FCSTD DOCUMENT  (FreeCAD 1.0R39285 (Git))
Label: TroubleBrewingCharacterIconsV2
License: All rights reserved
LicenseURL: https://en.wikipedia.org/wiki/All_rights_reserved
objects: Sketcher::SketchObject×22, Part::Extrusion×22, Part::Scale×22, Spreadsheet::Sheet×1
note: 88 computed .brp shape members not serialized (recipe doc carries the construction recipe); baked Part::Feature solids carry a one-line shape summary decoded from their .brp

FEATURE [Spreadsheet::Sheet] Spreadsheet  label="Icon_Params"
  cells = A1='IconDepth; B1='IconScale; A2(IconDepth)=3; B2(IconScale)=1.5
FEATURE [Sketcher::SketchObject] Sketch  label="Baron-Sketch"
  ArcFitTolerance = 1e-06
  FullyConstrained = false
  MakeInternals = false
  sketch-geometry (131):
    g0: BSplineCurve PolesCount=4 KnotsCount=2 Degree=3 IsPeriodic=0
    g1: BSplineCurve PolesCount=4 KnotsCount=2 Degree=3 IsPeriodic=0
    g2: BSplineCurve PolesCount=4 KnotsCount=2 Degree=3 IsPeriodic=0
    g3: BSplineCurve PolesCount=4 KnotsCount=2 Degree=3 IsPeriodic=0
    g4: BSplineCurve PolesCount=4 KnotsCount=2 Degree=3 IsPeriodic=0
    g5: BSplineCurve PolesCount=4 KnotsCount=2 Degree=3 IsPeriodic=0
    g6: BSplineCurve PolesCount=4 KnotsCount=2 Degree=3 IsPeriodic=0
    g7: BSplineCurve PolesCount=4 KnotsCount=2 Degree=3 IsPeriodic=0
    g8: BSplineCurve PolesCount=4 KnotsCount=2 Degree=3 IsPeriodic=0
    g9: BSplineCurve PolesCount=4 KnotsCount=2 Degree=3 IsPeriodic=0
    g10: BSplineCurve PolesCount=4 KnotsCount=2 Degree=3 IsPeriodic=0
    g11: BSplineCurve PolesCount=4 KnotsCount=2 Degree=3 IsPeriodic=0
    g12: BSplineCurve PolesCount=4 KnotsCount=2 Degree=3 IsPeriodic=0
    g13: BSplineCurve PolesCount=4 KnotsCount=2 Degree=3 IsPeriodic=0
    g14: BSplineCurve PolesCount=4 KnotsCount=2 Degree=3 IsPeriodic=0
    g15: BSplineCurve PolesCount=2 KnotsCount=2 Degree=1 IsPeriodic=0
    g16: BSplineCurve PolesCount=2 KnotsCount=2 Degree=1 IsPeriodic=0
    g17: BSplineCurve PolesCount=4 KnotsCount=2 Degree=3 IsPeriodic=0
    g18: BSplineCurve PolesCount=4 KnotsCount=2 Degree=3 IsPeriodic=0
    g19: BSplineCurve PolesCount=4 KnotsCount=2 Degree=3 IsPeriodic=0
    g20: BSplineCurve PolesCount=4 KnotsCount=2 Degree=3 IsPeriodic=0
    g21: BSplineCurve PolesCount=4 KnotsCount=2 Degree=3 IsPeriodic=0
    g22: BSplineCurve PolesCount=4 KnotsCount=2 Degree=3 IsPeriodic=0
    g23: BSplineCurve PolesCount=4 KnotsCount=2 Degree=3 IsPeriodic=0
    g24: BSplineCurve PolesCount=2 KnotsCount=2 Degree=1 IsPeriodic=0
    g25: BSplineCurve PolesCount=4 KnotsCount=2 Degree=3 IsPeriodic=0
    g26: BSplineCurve PolesCount=2 KnotsCount=2 Degree=1 IsPeriodic=0
    g27: BSplineCurve PolesCount=2 KnotsCount=2 Degree=1 IsPeriodic=0
    g28: BSplineCurve PolesCount=4 KnotsCount=2 Degree=3 IsPeriodic=0
    g29: BSplineCurve PolesCount=4 KnotsCount=2 Degree=3 IsPeriodic=0
    g30: BSplineCurve PolesCount=2 KnotsCount=2 Degree=1 IsPeriodic=0
    g31: BSplineCurve PolesCount=2 KnotsCount=2 Degree=1 IsPeriodic=0
    g32: BSplineCurve PolesCount=4 KnotsCount=2 Degree=3 IsPeriodic=0
    g33: BSplineCurve PolesCount=4 KnotsCount=2 Degree=3 IsPeriodic=0
    g34: BSplineCurve PolesCount=4 KnotsCount=2 Degree=3 IsPeriodic=0
    g35: BSplineCurve PolesCount=4 KnotsCount=2 Degree=3 IsPeriodic=0
    g36: BSplineCurve PolesCount=2 KnotsCount=2 Degree=1 IsPeriodic=0
    g37: BSplineCurve PolesCount=2 KnotsCount=2 Degree=1 IsPeriodic=0
    g38: BSplineCurve PolesCount=4 KnotsCount=2 Degree=3 IsPeriodic=0
    g39: BSplineCurve PolesCount=2 KnotsCount=2 Degree=1 IsPeriodic=0
    g40: BSplineCurve PolesCount=2 KnotsCount=2 Degree=1 IsPeriodic=0
    g41: BSplineCurve PolesCount=4 KnotsCount=2 Degree=3 IsPeriodic=0
    g42: BSplineCurve PolesCount=4 KnotsCount=2 Degree=3 IsPeriodic=0
    g43: BSplineCurve PolesCount=4 KnotsCount=2 Degree=3 IsPeriodic=0
    g44: BSplineCurve PolesCount=4 KnotsCount=2 Degree=3 IsPeriodic=0
    g45: BSplineCurve PolesCount=4 KnotsCount=2 Degree=3 IsPeriodic=0
    g46: BSplineCurve PolesCount=4 KnotsCount=2 Degree=3 IsPeriodic=0
    g47: BSplineCurve PolesCount=4 KnotsCount=2 Degree=3 IsPeriodic=0
    g48: BSplineCurve PolesCount=4 KnotsCount=2 Degree=3 IsPeriodic=0
    g49: BSplineCurve PolesCount=4 KnotsCount=2 Degree=3 IsPeriodic=0
    g50: BSplineCurve PolesCount=4 KnotsCount=2 Degree=3 IsPeriodic=0
    g51: BSplineCurve PolesCount=4 KnotsCount=2 Degree=3 IsPeriodic=0
    g52: BSplineCurve PolesCount=2 KnotsCount=2 Degree=1 IsPeriodic=0
    g53: BSplineCurve PolesCount=2 KnotsCount=2 Degree=1 IsPeriodic=0
    g54: BSplineCurve PolesCount=4 KnotsCount=2 Degree=3 IsPeriodic=0
    g55: BSplineCurve PolesCount=4 KnotsCount=2 Degree=3 IsPeriodic=0
    g56: BSplineCurve PolesCount=4 KnotsCount=2 Degree=3 IsPeriodic=0
    g57: BSplineCurve PolesCount=4 KnotsCount=2 Degree=3 IsPeriodic=0
    g58: BSplineCurve PolesCount=4 KnotsCount=2 Degree=3 IsPeriodic=0
    g59: BSplineCurve PolesCount=4 KnotsCount=2 Degree=3 IsPeriodic=0
    g60: BSplineCurve PolesCount=4 KnotsCount=2 Degree=3 IsPeriodic=0
    g61: BSplineCurve PolesCount=2 KnotsCount=2 Degree=1 IsPeriodic=0
    g62: BSplineCurve PolesCount=2 KnotsCount=2 Degree=1 IsPeriodic=0
    g63: BSplineCurve PolesCount=4 KnotsCount=2 Degree=3 IsPeriodic=0
    g64: BSplineCurve PolesCount=4 KnotsCount=2 Degree=3 IsPeriodic=0
    g65: BSplineCurve PolesCount=4 KnotsCount=2 Degree=3 IsPeriodic=0
    g66: BSplineCurve PolesCount=4 KnotsCount=2 Degree=3 IsPeriodic=0
    g67: BSplineCurve PolesCount=4 KnotsCount=2 Degree=3 IsPeriodic=0
    g68: BSplineCurve PolesCount=4 KnotsCount=2 Degree=3 IsPeriodic=0
    g69: BSplineCurve PolesCount=4 KnotsCount=2 Degree=3 IsPeriodic=0
    g70: BSplineCurve PolesCount=4 KnotsCount=2 Degree=3 IsPeriodic=0
    g71: BSplineCurve PolesCount=4 KnotsCount=2 Degree=3 IsPeriodic=0
    g72: BSplineCurve PolesCount=4 KnotsCount=2 Degree=3 IsPeriodic=0
    g73: BSplineCurve PolesCount=4 KnotsCount=2 Degree=3 IsPeriodic=0
    g74: BSplineCurve PolesCount=4 KnotsCount=2 Degree=3 IsPeriodic=0
    g75: BSplineCurve PolesCount=4 KnotsCount=2 Degree=3 IsPeriodic=0
    g76: BSplineCurve PolesCount=4 KnotsCount=2 Degree=3 IsPeriodic=0
    g77: BSplineCurve PolesCount=4 KnotsCount=2 Degree=3 IsPeriodic=0
    g78: BSplineCurve PolesCount=4 KnotsCount=2 Degree=3 IsPeriodic=0
    g79: BSplineCurve PolesCount=4 KnotsCount=2 Degree=3 IsPeriodic=0
    g80: BSplineCurve PolesCount=4 KnotsCount=2 Degree=3 IsPeriodic=0
    g81: BSplineCurve PolesCount=4 KnotsCount=2 Degree=3 IsPeriodic=0
    g82: BSplineCurve PolesCount=4 KnotsCount=2 Degree=3 IsPeriodic=0
    g83: BSplineCurve PolesCount=4 KnotsCount=2 Degree=3 IsPeriodic=0
    g84: BSplineCurve PolesCount=4 KnotsCount=2 Degree=3 IsPeriodic=0
    g85: BSplineCurve PolesCount=4 KnotsCount=2 Degree=3 IsPeriodic=0
    g86: BSplineCurve PolesCount=4 KnotsCount=2 Degree=3 IsPeriodic=0
    g87: BSplineCurve PolesCount=4 KnotsCount=2 Degree=3 IsPeriodic=0
    g88: BSplineCurve PolesCount=4 KnotsCount=2 Degree=3 IsPeriodic=0
    g89: BSplineCurve PolesCount=4 KnotsCount=2 Degree=3 IsPeriodic=0
    g90: BSplineCurve PolesCount=4 KnotsCount=2 Degree=3 IsPeriodic=0
    g91: BSplineCurve PolesCount=4 KnotsCount=2 Degree=3 IsPeriodic=0
    g92: BSplineCurve PolesCount=4 KnotsCount=2 Degree=3 IsPeriodic=0
    g93: BSplineCurve PolesCount=4 KnotsCount=2 Degree=3 IsPeriodic=0
    g94: BSplineCurve PolesCount=4 KnotsCount=2 Degree=3 IsPeriodic=0
    g95: BSplineCurve PolesCount=4 KnotsCount=2 Degree=3 IsPeriodic=0
    g96: BSplineCurve PolesCount=2 KnotsCount=2 Degree=1 IsPeriodic=0
    g97: BSplineCurve PolesCount=2 KnotsCount=2 Degree=1 IsPeriodic=0
    g98: BSplineCurve PolesCount=2 KnotsCount=2 Degree=1 IsPeriodic=0
    g99: BSplineCurve PolesCount=2 KnotsCount=2 Degree=1 IsPeriodic=0
    g100: BSplineCurve PolesCount=4 KnotsCount=2 Degree=3 IsPeriodic=0
    g101: BSplineCurve PolesCount=4 KnotsCount=2 Degree=3 IsPeriodic=0
    g102: BSplineCurve PolesCount=4 KnotsCount=2 Degree=3 IsPeriodic=0
    g103: BSplineCurve PolesCount=4 KnotsCount=2 Degree=3 IsPeriodic=0
    g104: BSplineCurve PolesCount=4 KnotsCount=2 Degree=3 IsPeriodic=0
    g105: BSplineCurve PolesCount=4 KnotsCount=2 Degree=3 IsPeriodic=0
    g106: BSplineCurve PolesCount=4 KnotsCount=2 Degree=3 IsPeriodic=0
    g107: BSplineCurve PolesCount=4 KnotsCount=2 Degree=3 IsPeriodic=0
    g108: BSplineCurve PolesCount=4 KnotsCount=2 Degree=3 IsPeriodic=0
    g109: BSplineCurve PolesCount=4 KnotsCount=2 Degree=3 IsPeriodic=0
    g110: BSplineCurve PolesCount=4 KnotsCount=2 Degree=3 IsPeriodic=0
    g111: BSplineCurve PolesCount=4 KnotsCount=2 Degree=3 IsPeriodic=0
    g112: BSplineCurve PolesCount=4 KnotsCount=2 Degree=3 IsPeriodic=0
    g113: BSplineCurve PolesCount=4 KnotsCount=2 Degree=3 IsPeriodic=0
    g114: BSplineCurve PolesCount=4 KnotsCount=2 Degree=3 IsPeriodic=0
    g115: BSplineCurve PolesCount=4 KnotsCount=2 Degree=3 IsPeriodic=0
    g116: BSplineCurve PolesCount=4 KnotsCount=2 Degree=3 IsPeriodic=0
    g117: BSplineCurve PolesCount=2 KnotsCount=2 Degree=1 IsPeriodic=0
    g118: BSplineCurve PolesCount=2 KnotsCount=2 Degree=1 IsPeriodic=0
    g119: BSplineCurve PolesCount=4 KnotsCount=2 Degree=3 IsPeriodic=0
    g120: BSplineCurve PolesCount=4 KnotsCount=2 Degree=3 IsPeriodic=0
    g121: BSplineCurve PolesCount=4 KnotsCount=2 Degree=3 IsPeriodic=0
    g122: BSplineCurve PolesCount=4 KnotsCount=2 Degree=3 IsPeriodic=0
    g123: BSplineCurve PolesCount=4 KnotsCount=2 Degree=3 IsPeriodic=0
    g124: BSplineCurve PolesCount=4 KnotsCount=2 Degree=3 IsPeriodic=0
    g125: BSplineCurve PolesCount=4 KnotsCount=2 Degree=3 IsPeriodic=0
    g126: BSplineCurve PolesCount=4 KnotsCount=2 Degree=3 IsPeriodic=0
    g127: BSplineCurve PolesCount=4 KnotsCount=2 Degree=3 IsPeriodic=0
    g128: BSplineCurve PolesCount=4 KnotsCount=2 Degree=3 IsPeriodic=0
    g129: BSplineCurve PolesCount=4 KnotsCount=2 Degree=3 IsPeriodic=0
    g130: BSplineCurve PolesCount=4 KnotsCount=2 Degree=3 IsPeriodic=0
  constraints (132):
    c: Coincident(g0,g1)
    c: Coincident(g1,g2)
    c: Coincident(g2,g3)
    c: Coincident(g3,g4)
    c: Coincident(g4,g5)
    c: Coincident(g5,g6)
    c: Coincident(g6,g7)
    c: Coincident(g7,g8)
    c: Coincident(g8,g9)
    c: Coincident(g9,g10)
    c: Coincident(g10,g11)
    c: Coincident(g11,g12)
    c: Coincident(g12,g13)
    c: Coincident(g13,g14)
    c: Coincident(g14,g15)
    c: Coincident(g15,g16)
    c: Coincident(g16,g17)
    c: Coincident(g17,g18)
    c: Coincident(g18,g19)
    c: Coincident(g19,g20)
    c: Coincident(g20,g21)
    c: Coincident(g21,g22)
    c: Coincident(g22,g23)
    c: Coincident(g23,g0)
    c: Coincident(g24,g25)
    c: Coincident(g25,g26)
    c: Coincident(g26,g27)
    c: Coincident(g27,g28)
    c: Coincident(g28,g29)
    c: Coincident(g29,g30)
    c: Coincident(g30,g31)
    c: Coincident(g31,g32)
    c: Coincident(g32,g33)
    c: Coincident(g33,g34)
    c: Coincident(g34,g35)
    c: Coincident(g35,g36)
    c: Coincident(g36,g37)
    c: Coincident(g37,g38)
    c: Coincident(g38,g39)
    c: Coincident(g39,g40)
    c: Coincident(g40,g41)
    c: Coincident(g41,g42)
    c: Coincident(g42,g43)
    c: Coincident(g43,g24)
    c: Coincident(g44,g45)
    c: Coincident(g45,g46)
    c: Coincident(g46,g47)
    c: Coincident(g47,g48)
    c: Coincident(g48,g49)
    c: Coincident(g49,g50)
    c: Coincident(g50,g51)
    c: Coincident(g51,g52)
    c: Coincident(g52,g53)
    c: Coincident(g53,g54)
    c: Coincident(g54,g55)
    c: Coincident(g55,g56)
    c: Coincident(g56,g57)
    c: Coincident(g57,g58)
    c: Coincident(g58,g59)
    c: Coincident(g59,g60)
    c: Coincident(g60,g61)
    c: Coincident(g61,g62)
    c: Coincident(g62,g63)
    c: Coincident(g63,g44)
    c: Coincident(g64,g65)
    c: Coincident(g65,g66)
    c: Coincident(g66,g67)
    c: Coincident(g67,g68)
    c: Coincident(g68,g69)
    c: Coincident(g69,g70)
    c: Coincident(g70,g71)
    c: Coincident(g71,g72)
    c: Coincident(g72,g73)
    c: Coincident(g73,g74)
    c: Coincident(g74,g75)
    c: Coincident(g75,g76)
    c: Coincident(g76,g77)
    c: Coincident(g77,g78)
    c: Coincident(g78,g79)
    c: Coincident(g79,g80)
    c: Coincident(g80,g81)
    c: Coincident(g81,g82)
    c: Coincident(g82,g83)
    c: Coincident(g83,g84)
    c: Coincident(g84,g64)
    c: Coincident(g85,g86)
    c: Coincident(g86,g87)
    c: Coincident(g87,g88)
    c: Coincident(g88,g89)
    c: Coincident(g89,g90)
    c: Coincident(g90,g91)
    c: Coincident(g91,g92)
    c: Coincident(g92,g93)
    c: Coincident(g93,g94)
    c: Coincident(g94,g95)
    c: Coincident(g95,g96)
    c: Coincident(g96,g97)
    c: Coincident(g97,g98)
    c: Coincident(g98,g99)
    c: Coincident(g99,g100)
    c: Coincident(g100,g101)
    c: Coincident(g101,g102)
    c: Coincident(g102,g103)
    c: Coincident(g103,g104)
    c: Coincident(g104,g105)
    c: Coincident(g105,g106)
    c: Coincident(g106,g107)
    c: Coincident(g107,g108)
    c: Coincident(g108,g109)
    c: Coincident(g109,g110)
    c: Coincident(g110,g111)
    c: Coincident(g111,g112)
    c: Coincident(g112,g113)
    c: Coincident(g113,g114)
    c: Coincident(g114,g115)
    c: Coincident(g115,g116)
    c: Coincident(g116,g117)
    c: Coincident(g117,g118)
    c: Coincident(g118,g85)
    c: Coincident(g119,g120)
    c: Coincident(g120,g121)
    c: Coincident(g121,g122)
    c: Coincident(g122,g123)
    c: Coincident(g123,g124)
    c: Coincident(g124,g125)
    c: Coincident(g125,g126)
    c: Coincident(g126,g127)
    c: Coincident(g127,g128)
    c: Coincident(g128,g129)
    c: Coincident(g129,g130)
    c: Coincident(g130,g119)
    c: Coincident(g24,g24)
FEATURE [Part::Extrusion] Extrude  label="Baron-Extrude"
  Base = -> Sketch
  Dir = (0,0,1)
  DirMode = 0
  FaceMakerClass = Part::FaceMakerBullseye
  FaceMakerMode = 3
  LengthFwd = 0
  LengthRev = 3
  Solid = true
  Symmetric = false
  expr: LengthRev = <<Icon_Params>>.IconDepth
FEATURE [Part::Scale] Scale  label="Baron"
  Base = -> Extrude
  Uniform = true
  UniformScale = 1.5
  XScale = 1
  YScale = 1
  ZScale = 1
  expr: UniformScale = <<Icon_Params>>.IconScale
FEATURE [Sketcher::SketchObject] Sketch001  label="Butler-Sketch"
  ArcFitTolerance = 1e-06
  FullyConstrained = false
  MakeInternals = false
  sketch-geometry (215):
    g0: BSplineCurve PolesCount=4 KnotsCount=2 Degree=3 IsPeriodic=0
    g1: BSplineCurve PolesCount=4 KnotsCount=2 Degree=3 IsPeriodic=0
    g2: BSplineCurve PolesCount=2 KnotsCount=2 Degree=1 IsPeriodic=0
    g3: BSplineCurve PolesCount=2 KnotsCount=2 Degree=1 IsPeriodic=0
    g4: BSplineCurve PolesCount=4 KnotsCount=2 Degree=3 IsPeriodic=0
    g5: BSplineCurve PolesCount=4 KnotsCount=2 Degree=3 IsPeriodic=0
    g6: BSplineCurve PolesCount=4 KnotsCount=2 Degree=3 IsPeriodic=0
    g7: BSplineCurve PolesCount=4 KnotsCount=2 Degree=3 IsPeriodic=0
    g8: BSplineCurve PolesCount=4 KnotsCount=2 Degree=3 IsPeriodic=0
    g9: BSplineCurve PolesCount=4 KnotsCount=2 Degree=3 IsPeriodic=0
    g10: BSplineCurve PolesCount=2 KnotsCount=2 Degree=1 IsPeriodic=0
    g11: BSplineCurve PolesCount=2 KnotsCount=2 Degree=1 IsPeriodic=0
    g12: BSplineCurve PolesCount=4 KnotsCount=2 Degree=3 IsPeriodic=0
    g13: BSplineCurve PolesCount=4 KnotsCount=2 Degree=3 IsPeriodic=0
    g14: BSplineCurve PolesCount=4 KnotsCount=2 Degree=3 IsPeriodic=0
    g15: BSplineCurve PolesCount=2 KnotsCount=2 Degree=1 IsPeriodic=0
    g16: BSplineCurve PolesCount=2 KnotsCount=2 Degree=1 IsPeriodic=0
    g17: BSplineCurve PolesCount=4 KnotsCount=2 Degree=3 IsPeriodic=0
    g18: BSplineCurve PolesCount=2 KnotsCount=2 Degree=1 IsPeriodic=0
    g19: BSplineCurve PolesCount=2 KnotsCount=2 Degree=1 IsPeriodic=0
    g20: BSplineCurve PolesCount=4 KnotsCount=2 Degree=3 IsPeriodic=0
    g21: BSplineCurve PolesCount=4 KnotsCount=2 Degree=3 IsPeriodic=0
    g22: BSplineCurve PolesCount=4 KnotsCount=2 Degree=3 IsPeriodic=0
    g23: BSplineCurve PolesCount=4 KnotsCount=2 Degree=3 IsPeriodic=0
    g24: BSplineCurve PolesCount=4 KnotsCount=2 Degree=3 IsPeriodic=0
    g25: BSplineCurve PolesCount=4 KnotsCount=2 Degree=3 IsPeriodic=0
    g26: BSplineCurve PolesCount=4 KnotsCount=2 Degree=3 IsPeriodic=0
    g27: BSplineCurve PolesCount=4 KnotsCount=2 Degree=3 IsPeriodic=0
    g28: BSplineCurve PolesCount=2 KnotsCount=2 Degree=1 IsPeriodic=0
    g29: BSplineCurve PolesCount=2 KnotsCount=2 Degree=1 IsPeriodic=0
    g30: BSplineCurve PolesCount=4 KnotsCount=2 Degree=3 IsPeriodic=0
    g31: BSplineCurve PolesCount=4 KnotsCount=2 Degree=3 IsPeriodic=0
    g32: BSplineCurve PolesCount=2 KnotsCount=2 Degree=1 IsPeriodic=0
    g33: BSplineCurve PolesCount=2 KnotsCount=2 Degree=1 IsPeriodic=0
    g34: BSplineCurve PolesCount=4 KnotsCount=2 Degree=3 IsPeriodic=0
    g35: BSplineCurve PolesCount=4 KnotsCount=2 Degree=3 IsPeriodic=0
    g36: BSplineCurve PolesCount=4 KnotsCount=2 Degree=3 IsPeriodic=0
    g37: BSplineCurve PolesCount=4 KnotsCount=2 Degree=3 IsPeriodic=0
    g38: BSplineCurve PolesCount=4 KnotsCount=2 Degree=3 IsPeriodic=0
    g39: BSplineCurve PolesCount=4 KnotsCount=2 Degree=3 IsPeriodic=0
    g40: BSplineCurve PolesCount=4 KnotsCount=2 Degree=3 IsPeriodic=0
    g41: BSplineCurve PolesCount=4 KnotsCount=2 Degree=3 IsPeriodic=0
    g42: BSplineCurve PolesCount=4 KnotsCount=2 Degree=3 IsPeriodic=0
    g43: BSplineCurve PolesCount=4 KnotsCount=2 Degree=3 IsPeriodic=0
    g44: BSplineCurve PolesCount=2 KnotsCount=2 Degree=1 IsPeriodic=0
    g45: BSplineCurve PolesCount=2 KnotsCount=2 Degree=1 IsPeriodic=0
    g46: BSplineCurve PolesCount=4 KnotsCount=2 Degree=3 IsPeriodic=0
    g47: BSplineCurve PolesCount=4 KnotsCount=2 Degree=3 IsPeriodic=0
    g48: BSplineCurve PolesCount=2 KnotsCount=2 Degree=1 IsPeriodic=0
    g49: BSplineCurve PolesCount=2 KnotsCount=2 Degree=1 IsPeriodic=0
    g50: BSplineCurve PolesCount=2 KnotsCount=2 Degree=1 IsPeriodic=0
    g51: BSplineCurve PolesCount=2 KnotsCount=2 Degree=1 IsPeriodic=0
    g52: BSplineCurve PolesCount=4 KnotsCount=2 Degree=3 IsPeriodic=0
    g53: BSplineCurve PolesCount=4 KnotsCount=2 Degree=3 IsPeriodic=0
    g54: BSplineCurve PolesCount=4 KnotsCount=2 Degree=3 IsPeriodic=0
    g55: BSplineCurve PolesCount=4 KnotsCount=2 Degree=3 IsPeriodic=0
    g56: BSplineCurve PolesCount=4 KnotsCount=2 Degree=3 IsPeriodic=0
    g57: BSplineCurve PolesCount=4 KnotsCount=2 Degree=3 IsPeriodic=0
    g58: BSplineCurve PolesCount=4 KnotsCount=2 Degree=3 IsPeriodic=0
    g59: BSplineCurve PolesCount=4 KnotsCount=2 Degree=3 IsPeriodic=0
    g60: BSplineCurve PolesCount=4 KnotsCount=2 Degree=3 IsPeriodic=0
    g61: BSplineCurve PolesCount=4 KnotsCount=2 Degree=3 IsPeriodic=0
    g62: BSplineCurve PolesCount=4 KnotsCount=2 Degree=3 IsPeriodic=0
    g63: BSplineCurve PolesCount=4 KnotsCount=2 Degree=3 IsPeriodic=0
    g64: BSplineCurve PolesCount=4 KnotsCount=2 Degree=3 IsPeriodic=0
    g65: BSplineCurve PolesCount=4 KnotsCount=2 Degree=3 IsPeriodic=0
    g66: BSplineCurve PolesCount=4 KnotsCount=2 Degree=3 IsPeriodic=0
    g67: BSplineCurve PolesCount=4 KnotsCount=2 Degree=3 IsPeriodic=0
    g68: BSplineCurve PolesCount=4 KnotsCount=2 Degree=3 IsPeriodic=0
    g69: BSplineCurve PolesCount=4 KnotsCount=2 Degree=3 IsPeriodic=0
    g70: BSplineCurve PolesCount=4 KnotsCount=2 Degree=3 IsPeriodic=0
    g71: BSplineCurve PolesCount=4 KnotsCount=2 Degree=3 IsPeriodic=0
    g72: BSplineCurve PolesCount=4 KnotsCount=2 Degree=3 IsPeriodic=0
    g73: BSplineCurve PolesCount=4 KnotsCount=2 Degree=3 IsPeriodic=0
    g74: BSplineCurve PolesCount=4 KnotsCount=2 Degree=3 IsPeriodic=0
    g75: BSplineCurve PolesCount=4 KnotsCount=2 Degree=3 IsPeriodic=0
    g76: BSplineCurve PolesCount=4 KnotsCount=2 Degree=3 IsPeriodic=0
    g77: BSplineCurve PolesCount=4 KnotsCount=2 Degree=3 IsPeriodic=0
    g78: BSplineCurve PolesCount=4 KnotsCount=2 Degree=3 IsPeriodic=0
    g79: BSplineCurve PolesCount=4 KnotsCount=2 Degree=3 IsPeriodic=0
    g80: BSplineCurve PolesCount=4 KnotsCount=2 Degree=3 IsPeriodic=0
    g81: BSplineCurve PolesCount=4 KnotsCount=2 Degree=3 IsPeriodic=0
    g82: BSplineCurve PolesCount=4 KnotsCount=2 Degree=3 IsPeriodic=0
    g83: BSplineCurve PolesCount=4 KnotsCount=2 Degree=3 IsPeriodic=0
    g84: BSplineCurve PolesCount=4 KnotsCount=2 Degree=3 IsPeriodic=0
    g85: BSplineCurve PolesCount=4 KnotsCount=2 Degree=3 IsPeriodic=0
    g86: BSplineCurve PolesCount=4 KnotsCount=2 Degree=3 IsPeriodic=0
    g87: BSplineCurve PolesCount=4 KnotsCount=2 Degree=3 IsPeriodic=0
    g88: BSplineCurve PolesCount=4 KnotsCount=2 Degree=3 IsPeriodic=0
    g89: BSplineCurve PolesCount=4 KnotsCount=2 Degree=3 IsPeriodic=0
    g90: BSplineCurve PolesCount=4 KnotsCount=2 Degree=3 IsPeriodic=0
    g91: BSplineCurve PolesCount=4 KnotsCount=2 Degree=3 IsPeriodic=0
    g92: BSplineCurve PolesCount=4 KnotsCount=2 Degree=3 IsPeriodic=0
    g93: BSplineCurve PolesCount=4 KnotsCount=2 Degree=3 IsPeriodic=0
    g94: BSplineCurve PolesCount=4 KnotsCount=2 Degree=3 IsPeriodic=0
    g95: BSplineCurve PolesCount=4 KnotsCount=2 Degree=3 IsPeriodic=0
    g96: BSplineCurve PolesCount=4 KnotsCount=2 Degree=3 IsPeriodic=0
    g97: BSplineCurve PolesCount=2 KnotsCount=2 Degree=1 IsPeriodic=0
    g98: BSplineCurve PolesCount=2 KnotsCount=2 Degree=1 IsPeriodic=0
    g99: BSplineCurve PolesCount=2 KnotsCount=2 Degree=1 IsPeriodic=0
    g100: BSplineCurve PolesCount=2 KnotsCount=2 Degree=1 IsPeriodic=0
    g101: BSplineCurve PolesCount=4 KnotsCount=2 Degree=3 IsPeriodic=0
    g102: BSplineCurve PolesCount=4 KnotsCount=2 Degree=3 IsPeriodic=0
    g103: BSplineCurve PolesCount=4 KnotsCount=2 Degree=3 IsPeriodic=0
    g104: BSplineCurve PolesCount=4 KnotsCount=2 Degree=3 IsPeriodic=0
    g105: BSplineCurve PolesCount=4 KnotsCount=2 Degree=3 IsPeriodic=0
    g106: BSplineCurve PolesCount=4 KnotsCount=2 Degree=3 IsPeriodic=0
    g107: BSplineCurve PolesCount=4 KnotsCount=2 Degree=3 IsPeriodic=0
    g108: BSplineCurve PolesCount=4 KnotsCount=2 Degree=3 IsPeriodic=0
    g109: BSplineCurve PolesCount=4 KnotsCount=2 Degree=3 IsPeriodic=0
    g110: BSplineCurve PolesCount=4 KnotsCount=2 Degree=3 IsPeriodic=0
    g111: BSplineCurve PolesCount=4 KnotsCount=2 Degree=3 IsPeriodic=0
    g112: BSplineCurve PolesCount=4 KnotsCount=2 Degree=3 IsPeriodic=0
    g113: BSplineCurve PolesCount=4 KnotsCount=2 Degree=3 IsPeriodic=0
    g114: BSplineCurve PolesCount=2 KnotsCount=2 Degree=1 IsPeriodic=0
    g115: BSplineCurve PolesCount=2 KnotsCount=2 Degree=1 IsPeriodic=0
    g116: BSplineCurve PolesCount=4 KnotsCount=2 Degree=3 IsPeriodic=0
    g117: BSplineCurve PolesCount=4 KnotsCount=2 Degree=3 IsPeriodic=0
    g118: BSplineCurve PolesCount=4 KnotsCount=2 Degree=3 IsPeriodic=0
    g119: BSplineCurve PolesCount=4 KnotsCount=2 Degree=3 IsPeriodic=0
    g120: BSplineCurve PolesCount=2 KnotsCount=2 Degree=1 IsPeriodic=0
    g121: BSplineCurve PolesCount=2 KnotsCount=2 Degree=1 IsPeriodic=0
    g122: BSplineCurve PolesCount=4 KnotsCount=2 Degree=3 IsPeriodic=0
    g123: BSplineCurve PolesCount=4 KnotsCount=2 Degree=3 IsPeriodic=0
    g124: BSplineCurve PolesCount=4 KnotsCount=2 Degree=3 IsPeriodic=0
    g125: BSplineCurve PolesCount=4 KnotsCount=2 Degree=3 IsPeriodic=0
    g126: BSplineCurve PolesCount=4 KnotsCount=2 Degree=3 IsPeriodic=0
    g127: BSplineCurve PolesCount=4 KnotsCount=2 Degree=3 IsPeriodic=0
    g128: BSplineCurve PolesCount=4 KnotsCount=2 Degree=3 IsPeriodic=0
    g129: BSplineCurve PolesCount=4 KnotsCount=2 Degree=3 IsPeriodic=0
    g130: BSplineCurve PolesCount=4 KnotsCount=2 Degree=3 IsPeriodic=0
    g131: BSplineCurve PolesCount=4 KnotsCount=2 Degree=3 IsPeriodic=0
    g132: BSplineCurve PolesCount=4 KnotsCount=2 Degree=3 IsPeriodic=0
    g133: BSplineCurve PolesCount=4 KnotsCount=2 Degree=3 IsPeriodic=0
    g134: BSplineCurve PolesCount=4 KnotsCount=2 Degree=3 IsPeriodic=0
    g135: BSplineCurve PolesCount=4 KnotsCount=2 Degree=3 IsPeriodic=0
    g136: BSplineCurve PolesCount=4 KnotsCount=2 Degree=3 IsPeriodic=0
    g137: BSplineCurve PolesCount=4 KnotsCount=2 Degree=3 IsPeriodic=0
    g138: BSplineCurve PolesCount=4 KnotsCount=2 Degree=3 IsPeriodic=0
    g139: BSplineCurve PolesCount=4 KnotsCount=2 Degree=3 IsPeriodic=0
    g140: BSplineCurve PolesCount=4 KnotsCount=2 Degree=3 IsPeriodic=0
    g141: BSplineCurve PolesCount=4 KnotsCount=2 Degree=3 IsPeriodic=0
    g142: BSplineCurve PolesCount=4 KnotsCount=2 Degree=3 IsPeriodic=0
    g143: BSplineCurve PolesCount=4 KnotsCount=2 Degree=3 IsPeriodic=0
    g144: BSplineCurve PolesCount=4 KnotsCount=2 Degree=3 IsPeriodic=0
    g145: BSplineCurve PolesCount=4 KnotsCount=2 Degree=3 IsPeriodic=0
    g146: BSplineCurve PolesCount=4 KnotsCount=2 Degree=3 IsPeriodic=0
    g147: BSplineCurve PolesCount=4 KnotsCount=2 Degree=3 IsPeriodic=0
    g148: BSplineCurve PolesCount=4 KnotsCount=2 Degree=3 IsPeriodic=0
    g149: BSplineCurve PolesCount=2 KnotsCount=2 Degree=1 IsPeriodic=0
    g150: BSplineCurve PolesCount=2 KnotsCount=2 Degree=1 IsPeriodic=0
    g151: BSplineCurve PolesCount=4 KnotsCount=2 Degree=3 IsPeriodic=0
    g152: BSplineCurve PolesCount=4 KnotsCount=2 Degree=3 IsPeriodic=0
    g153: BSplineCurve PolesCount=4 KnotsCount=2 Degree=3 IsPeriodic=0
    g154: BSplineCurve PolesCount=4 KnotsCount=2 Degree=3 IsPeriodic=0
    g155: BSplineCurve PolesCount=4 KnotsCount=2 Degree=3 IsPeriodic=0
    g156: BSplineCurve PolesCount=4 KnotsCount=2 Degree=3 IsPeriodic=0
    g157: BSplineCurve PolesCount=4 KnotsCount=2 Degree=3 IsPeriodic=0
    g158: BSplineCurve PolesCount=4 KnotsCount=2 Degree=3 IsPeriodic=0
    g159: BSplineCurve PolesCount=4 KnotsCount=2 Degree=3 IsPeriodic=0
    g160: BSplineCurve PolesCount=4 KnotsCount=2 Degree=3 IsPeriodic=0
    g161: BSplineCurve PolesCount=4 KnotsCount=2 Degree=3 IsPeriodic=0
    g162: BSplineCurve PolesCount=2 KnotsCount=2 Degree=1 IsPeriodic=0
    g163: BSplineCurve PolesCount=2 KnotsCount=2 Degree=1 IsPeriodic=0
    g164: BSplineCurve PolesCount=2 KnotsCount=2 Degree=1 IsPeriodic=0
    g165: BSplineCurve PolesCount=2 KnotsCount=2 Degree=1 IsPeriodic=0
    g166: BSplineCurve PolesCount=4 KnotsCount=2 Degree=3 IsPeriodic=0
    g167: BSplineCurve PolesCount=4 KnotsCount=2 Degree=3 IsPeriodic=0
    g168: BSplineCurve PolesCount=4 KnotsCount=2 Degree=3 IsPeriodic=0
    g169: BSplineCurve PolesCount=4 KnotsCount=2 Degree=3 IsPeriodic=0
    g170: BSplineCurve PolesCount=4 KnotsCount=2 Degree=3 IsPeriodic=0
    g171: BSplineCurve PolesCount=4 KnotsCount=2 Degree=3 IsPeriodic=0
    g172: BSplineCurve PolesCount=4 KnotsCount=2 Degree=3 IsPeriodic=0
    g173: BSplineCurve PolesCount=4 KnotsCount=2 Degree=3 IsPeriodic=0
    g174: BSplineCurve PolesCount=4 KnotsCount=2 Degree=3 IsPeriodic=0
    g175: BSplineCurve PolesCount=4 KnotsCount=2 Degree=3 IsPeriodic=0
    g176: BSplineCurve PolesCount=4 KnotsCount=2 Degree=3 IsPeriodic=0
    g177: BSplineCurve PolesCount=4 KnotsCount=2 Degree=3 IsPeriodic=0
    g178: BSplineCurve PolesCount=4 KnotsCount=2 Degree=3 IsPeriodic=0
    g179: BSplineCurve PolesCount=4 KnotsCount=2 Degree=3 IsPeriodic=0
    g180: BSplineCurve PolesCount=4 KnotsCount=2 Degree=3 IsPeriodic=0
    g181: BSplineCurve PolesCount=4 KnotsCount=2 Degree=3 IsPeriodic=0
    g182: BSplineCurve PolesCount=4 KnotsCount=2 Degree=3 IsPeriodic=0
    g183: BSplineCurve PolesCount=4 KnotsCount=2 Degree=3 IsPeriodic=0
    g184: BSplineCurve PolesCount=4 KnotsCount=2 Degree=3 IsPeriodic=0
    g185: BSplineCurve PolesCount=4 KnotsCount=2 Degree=3 IsPeriodic=0
    g186: BSplineCurve PolesCount=2 KnotsCount=2 Degree=1 IsPeriodic=0
    g187: BSplineCurve PolesCount=2 KnotsCount=2 Degree=1 IsPeriodic=0
    g188: BSplineCurve PolesCount=4 KnotsCount=2 Degree=3 IsPeriodic=0
    g189: BSplineCurve PolesCount=4 KnotsCount=2 Degree=3 IsPeriodic=0
    g190: BSplineCurve PolesCount=4 KnotsCount=2 Degree=3 IsPeriodic=0
    g191: BSplineCurve PolesCount=4 KnotsCount=2 Degree=3 IsPeriodic=0
    g192: BSplineCurve PolesCount=4 KnotsCount=2 Degree=3 IsPeriodic=0
    g193: BSplineCurve PolesCount=4 KnotsCount=2 Degree=3 IsPeriodic=0
    g194: BSplineCurve PolesCount=4 KnotsCount=2 Degree=3 IsPeriodic=0
    g195: BSplineCurve PolesCount=4 KnotsCount=2 Degree=3 IsPeriodic=0
    g196: BSplineCurve PolesCount=4 KnotsCount=2 Degree=3 IsPeriodic=0
    g197: BSplineCurve PolesCount=4 KnotsCount=2 Degree=3 IsPeriodic=0
    g198: BSplineCurve PolesCount=4 KnotsCount=2 Degree=3 IsPeriodic=0
    g199: BSplineCurve PolesCount=2 KnotsCount=2 Degree=1 IsPeriodic=0
    g200: BSplineCurve PolesCount=4 KnotsCount=2 Degree=3 IsPeriodic=0
    g201: BSplineCurve PolesCount=4 KnotsCount=2 Degree=3 IsPeriodic=0
    g202: BSplineCurve PolesCount=4 KnotsCount=2 Degree=3 IsPeriodic=0
    g203: BSplineCurve PolesCount=2 KnotsCount=2 Degree=1 IsPeriodic=0
    g204: BSplineCurve PolesCount=4 KnotsCount=2 Degree=3 IsPeriodic=0
    g205: BSplineCurve PolesCount=4 KnotsCount=2 Degree=3 IsPeriodic=0
    g206: BSplineCurve PolesCount=4 KnotsCount=2 Degree=3 IsPeriodic=0
    g207: BSplineCurve PolesCount=4 KnotsCount=2 Degree=3 IsPeriodic=0
    g208: BSplineCurve PolesCount=4 KnotsCount=2 Degree=3 IsPeriodic=0
    g209: BSplineCurve PolesCount=4 KnotsCount=2 Degree=3 IsPeriodic=0
    g210: BSplineCurve PolesCount=4 KnotsCount=2 Degree=3 IsPeriodic=0
    g211: BSplineCurve PolesCount=4 KnotsCount=2 Degree=3 IsPeriodic=0
    g212: BSplineCurve PolesCount=4 KnotsCount=2 Degree=3 IsPeriodic=0
    g213: BSplineCurve PolesCount=4 KnotsCount=2 Degree=3 IsPeriodic=0
    g214: BSplineCurve PolesCount=4 KnotsCount=2 Degree=3 IsPeriodic=0
  constraints (215):
    c: Coincident(g0,g1)
    c: Coincident(g1,g2)
    c: Coincident(g2,g3)
    c: Coincident(g3,g4)
    c: Coincident(g4,g5)
    c: Coincident(g5,g0)
    c: Coincident(g6,g7)
    c: Coincident(g7,g8)
    c: Coincident(g8,g9)
    c: Coincident(g10,g11)
    c: Coincident(g11,g12)
    c: Coincident(g12,g13)
    c: Coincident(g13,g14)
    c: Coincident(g14,g15)
    c: Coincident(g15,g16)
    c: Coincident(g16,g17)
    c: Coincident(g17,g18)
    c: Coincident(g18,g19)
    c: Coincident(g19,g20)
    c: Coincident(g20,g21)
    c: Coincident(g21,g22)
    c: Coincident(g22,g23)
    c: Coincident(g23,g24)
    c: Coincident(g24,g25)
    c: Coincident(g26,g27)
    c: Coincident(g27,g28)
    c: Coincident(g28,g29)
    c: Coincident(g29,g30)
    c: Coincident(g30,g31)
    c: Coincident(g31,g32)
    c: Coincident(g32,g33)
    c: Coincident(g33,g34)
    c: Coincident(g34,g35)
    c: Coincident(g35,g36)
    c: Coincident(g36,g26)
    c: Coincident(g37,g38)
    c: Coincident(g38,g39)
    c: Coincident(g39,g40)
    c: Coincident(g40,g41)
    c: Coincident(g41,g37)
    c: Coincident(g42,g43)
    c: Coincident(g43,g44)
    c: Coincident(g44,g45)
    c: Coincident(g45,g46)
    c: Coincident(g46,g42)
    c: Coincident(g47,g48)
    c: Coincident(g48,g49)
    c: Coincident(g49,g50)
    c: Coincident(g50,g51)
    c: Coincident(g51,g52)
    c: Coincident(g52,g47)
    c: Coincident(g53,g54)
    c: Coincident(g54,g55)
    c: Coincident(g55,g56)
    c: Coincident(g56,g57)
    c: Coincident(g57,g58)
    c: Coincident(g58,g59)
    c: Coincident(g59,g60)
    c: Coincident(g60,g61)
    c: Coincident(g61,g62)
    c: Coincident(g62,g63)
    c: Coincident(g63,g64)
    c: Coincident(g64,g65)
    c: Coincident(g65,g66)
    c: Coincident(g66,g67)
    c: Coincident(g67,g68)
    c: Coincident(g68,g69)
    c: Coincident(g69,g70)
    c: Coincident(g70,g71)
    c: Coincident(g71,g72)
    c: Coincident(g72,g73)
    c: Coincident(g73,g74)
    c: Coincident(g74,g75)
    c: Coincident(g75,g76)
    c: Coincident(g76,g77)
    c: Coincident(g77,g78)
    c: Coincident(g78,g79)
    c: Coincident(g79,g80)
    c: Coincident(g80,g81)
    c: Coincident(g81,g82)
    c: Coincident(g82,g83)
    c: Coincident(g83,g84)
    c: Coincident(g84,g85)
    c: Coincident(g85,g53)
    c: Coincident(g86,g87)
    c: Coincident(g87,g88)
    c: Coincident(g88,g89)
    c: Coincident(g89,g86)
    c: Coincident(g90,g91)
    c: Coincident(g91,g92)
    c: Coincident(g92,g93)
    c: Coincident(g93,g94)
    c: Coincident(g94,g95)
    c: Coincident(g95,g96)
    c: Coincident(g96,g97)
    c: Coincident(g97,g98)
    c: Coincident(g98,g90)
    c: Coincident(g99,g100)
    c: Coincident(g100,g101)
    c: Coincident(g101,g102)
    c: Coincident(g102,g103)
    c: Coincident(g103,g104)
    c: Coincident(g105,g106)
    c: Coincident(g106,g107)
    c: Coincident(g107,g108)
    c: Coincident(g108,g109)
    c: Coincident(g109,g110)
    c: Coincident(g110,g105)
    c: Coincident(g111,g112)
    c: Coincident(g112,g113)
    c: Coincident(g113,g114)
    c: Coincident(g114,g115)
    c: Coincident(g115,g116)
    c: Coincident(g116,g111)
    c: Coincident(g117,g118)
    c: Coincident(g118,g119)
    c: Coincident(g119,g120)
    c: Coincident(g120,g121)
    c: Coincident(g121,g122)
    c: Coincident(g122,g123)
    c: Coincident(g123,g124)
    c: Coincident(g124,g125)
    c: Coincident(g125,g126)
    c: Coincident(g126,g127)
    c: Coincident(g127,g128)
    c: Coincident(g128,g129)
    c: Coincident(g129,g130)
    c: Coincident(g130,g131)
    c: Coincident(g131,g132)
    c: Coincident(g132,g133)
    c: Coincident(g133,g134)
    c: Coincident(g134,g135)
    c: Coincident(g135,g136)
    c: Coincident(g136,g137)
    c: Coincident(g137,g138)
    c: Coincident(g138,g139)
    c: Coincident(g139,g140)
    c: Coincident(g140,g141)
    c: Coincident(g141,g142)
    c: Coincident(g142,g143)
    c: Coincident(g143,g144)
    c: Coincident(g144,g145)
    c: Coincident(g145,g146)
    c: Coincident(g146,g147)
    c: Coincident(g147,g148)
    c: Coincident(g148,g149)
    c: Coincident(g149,g150)
    c: Coincident(g150,g151)
    c: Coincident(g151,g152)
    c: Coincident(g152,g153)
    c: Coincident(g153,g154)
    c: Coincident(g154,g155)
    c: Coincident(g155,g156)
    c: Coincident(g156,g157)
    c: Coincident(g157,g158)
    c: Coincident(g158,g159)
    c: Coincident(g159,g160)
    c: Coincident(g160,g161)
    c: Coincident(g161,g162)
    c: Coincident(g162,g163)
    c: Coincident(g163,g164)
    c: Coincident(g164,g165)
    c: Coincident(g165,g166)
    c: Coincident(g166,g167)
    c: Coincident(g167,g168)
    c: Coincident(g168,g169)
    c: Coincident(g169,g170)
    c: Coincident(g170,g171)
    c: Coincident(g171,g172)
    c: Coincident(g172,g173)
    c: Coincident(g173,g174)
    c: Coincident(g174,g175)
    c: Coincident(g175,g176)
    c: Coincident(g176,g177)
    c: Coincident(g177,g178)
    c: Coincident(g178,g179)
    c: Coincident(g179,g180)
    c: Coincident(g180,g181)
    c: Coincident(g181,g182)
    c: Coincident(g182,g183)
    c: Coincident(g184,g185)
    c: Coincident(g185,g186)
    c: Coincident(g186,g187)
    c: Coincident(g187,g188)
    c: Coincident(g188,g189)
    c: Coincident(g189,g190)
    c: Coincident(g190,g191)
    c: Coincident(g191,g184)
    c: Coincident(g192,g193)
    c: Coincident(g193,g194)
    c: Coincident(g194,g195)
    c: Coincident(g195,g196)
    c: Coincident(g196,g197)
    c: Coincident(g197,g198)
    c: Coincident(g199,g200)
    c: Coincident(g200,g201)
    c: Coincident(g201,g202)
    c: Coincident(g202,g203)
    c: Coincident(g203,g199)
    c: Coincident(g204,g205)
    c: Coincident(g205,g206)
    c: Coincident(g206,g207)
    c: Coincident(g207,g208)
    c: Coincident(g208,g204)
    c: Coincident(g209,g210)
    c: Coincident(g210,g211)
    c: Coincident(g211,g212)
    c: Coincident(g212,g213)
    c: Coincident(g213,g214)
    c: Coincident(g214,g209)
    c: Coincident(g25,g10)
    c: Coincident(g117,g183)
    c: Coincident(g192,g198)
    c: Coincident(g6,g9)
    c: Coincident(g99,g104)
FEATURE [Sketcher::SketchObject] Sketch002  label="Chef-Sketch"
  ArcFitTolerance = 1e-06
  FullyConstrained = false
  MakeInternals = false
  sketch-geometry (227):
    g0: BSplineCurve PolesCount=4 KnotsCount=2 Degree=3 IsPeriodic=0
    g1: BSplineCurve PolesCount=4 KnotsCount=2 Degree=3 IsPeriodic=0
    g2: BSplineCurve PolesCount=4 KnotsCount=2 Degree=3 IsPeriodic=0
    g3: BSplineCurve PolesCount=2 KnotsCount=2 Degree=1 IsPeriodic=0
    g4: BSplineCurve PolesCount=2 KnotsCount=2 Degree=1 IsPeriodic=0
    g5: BSplineCurve PolesCount=4 KnotsCount=2 Degree=3 IsPeriodic=0
    g6: BSplineCurve PolesCount=4 KnotsCount=2 Degree=3 IsPeriodic=0
    g7: BSplineCurve PolesCount=4 KnotsCount=2 Degree=3 IsPeriodic=0
    g8: BSplineCurve PolesCount=4 KnotsCount=2 Degree=3 IsPeriodic=0
    g9: BSplineCurve PolesCount=4 KnotsCount=2 Degree=3 IsPeriodic=0
    g10: BSplineCurve PolesCount=4 KnotsCount=2 Degree=3 IsPeriodic=0
    g11: BSplineCurve PolesCount=4 KnotsCount=2 Degree=3 IsPeriodic=0
    g12: BSplineCurve PolesCount=4 KnotsCount=2 Degree=3 IsPeriodic=0
    g13: BSplineCurve PolesCount=4 KnotsCount=2 Degree=3 IsPeriodic=0
    g14: BSplineCurve PolesCount=4 KnotsCount=2 Degree=3 IsPeriodic=0
    g15: BSplineCurve PolesCount=4 KnotsCount=2 Degree=3 IsPeriodic=0
    g16: BSplineCurve PolesCount=2 KnotsCount=2 Degree=1 IsPeriodic=0
    g17: BSplineCurve PolesCount=2 KnotsCount=2 Degree=1 IsPeriodic=0
    g18: BSplineCurve PolesCount=4 KnotsCount=2 Degree=3 IsPeriodic=0
    g19: BSplineCurve PolesCount=4 KnotsCount=2 Degree=3 IsPeriodic=0
    g20: BSplineCurve PolesCount=4 KnotsCount=2 Degree=3 IsPeriodic=0
    g21: BSplineCurve PolesCount=4 KnotsCount=2 Degree=3 IsPeriodic=0
    g22: BSplineCurve PolesCount=2 KnotsCount=2 Degree=1 IsPeriodic=0
    g23: BSplineCurve PolesCount=2 KnotsCount=2 Degree=1 IsPeriodic=0
    g24: BSplineCurve PolesCount=4 KnotsCount=2 Degree=3 IsPeriodic=0
    g25: BSplineCurve PolesCount=4 KnotsCount=2 Degree=3 IsPeriodic=0
    g26: BSplineCurve PolesCount=4 KnotsCount=2 Degree=3 IsPeriodic=0
    g27: BSplineCurve PolesCount=4 KnotsCount=2 Degree=3 IsPeriodic=0
    g28: BSplineCurve PolesCount=4 KnotsCount=2 Degree=3 IsPeriodic=0
    g29: BSplineCurve PolesCount=4 KnotsCount=2 Degree=3 IsPeriodic=0
    g30: BSplineCurve PolesCount=4 KnotsCount=2 Degree=3 IsPeriodic=0
    g31: BSplineCurve PolesCount=4 KnotsCount=2 Degree=3 IsPeriodic=0
    g32: BSplineCurve PolesCount=2 KnotsCount=2 Degree=1 IsPeriodic=0
    g33: BSplineCurve PolesCount=2 KnotsCount=2 Degree=1 IsPeriodic=0
    g34: BSplineCurve PolesCount=4 KnotsCount=2 Degree=3 IsPeriodic=0
    g35: BSplineCurve PolesCount=2 KnotsCount=2 Degree=1 IsPeriodic=0
    g36: BSplineCurve PolesCount=2 KnotsCount=2 Degree=1 IsPeriodic=0
    g37: BSplineCurve PolesCount=4 KnotsCount=2 Degree=3 IsPeriodic=0
    g38: BSplineCurve PolesCount=4 KnotsCount=2 Degree=3 IsPeriodic=0
    g39: BSplineCurve PolesCount=4 KnotsCount=2 Degree=3 IsPeriodic=0
    g40: BSplineCurve PolesCount=4 KnotsCount=2 Degree=3 IsPeriodic=0
    g41: BSplineCurve PolesCount=4 KnotsCount=2 Degree=3 IsPeriodic=0
    g42: BSplineCurve PolesCount=4 KnotsCount=2 Degree=3 IsPeriodic=0
    g43: BSplineCurve PolesCount=4 KnotsCount=2 Degree=3 IsPeriodic=0
    g44: BSplineCurve PolesCount=4 KnotsCount=2 Degree=3 IsPeriodic=0
    g45: BSplineCurve PolesCount=4 KnotsCount=2 Degree=3 IsPeriodic=0
    g46: BSplineCurve PolesCount=4 KnotsCount=2 Degree=3 IsPeriodic=0
    g47: BSplineCurve PolesCount=4 KnotsCount=2 Degree=3 IsPeriodic=0
    g48: BSplineCurve PolesCount=4 KnotsCount=2 Degree=3 IsPeriodic=0
    g49: BSplineCurve PolesCount=4 KnotsCount=2 Degree=3 IsPeriodic=0
    g50: BSplineCurve PolesCount=2 KnotsCount=2 Degree=1 IsPeriodic=0
    g51: BSplineCurve PolesCount=2 KnotsCount=2 Degree=1 IsPeriodic=0
    g52: BSplineCurve PolesCount=4 KnotsCount=2 Degree=3 IsPeriodic=0
    g53: BSplineCurve PolesCount=4 KnotsCount=2 Degree=3 IsPeriodic=0
    g54: BSplineCurve PolesCount=4 KnotsCount=2 Degree=3 IsPeriodic=0
    g55: BSplineCurve PolesCount=2 KnotsCount=2 Degree=1 IsPeriodic=0
    g56: BSplineCurve PolesCount=2 KnotsCount=2 Degree=1 IsPeriodic=0
    g57: BSplineCurve PolesCount=4 KnotsCount=2 Degree=3 IsPeriodic=0
    g58: BSplineCurve PolesCount=4 KnotsCount=2 Degree=3 IsPeriodic=0
    g59: BSplineCurve PolesCount=4 KnotsCount=2 Degree=3 IsPeriodic=0
    g60: BSplineCurve PolesCount=4 KnotsCount=2 Degree=3 IsPeriodic=0
    g61: BSplineCurve PolesCount=4 KnotsCount=2 Degree=3 IsPeriodic=0
    g62: BSplineCurve PolesCount=4 KnotsCount=2 Degree=3 IsPeriodic=0
    g63: BSplineCurve PolesCount=4 KnotsCount=2 Degree=3 IsPeriodic=0
    g64: BSplineCurve PolesCount=4 KnotsCount=2 Degree=3 IsPeriodic=0
    g65: BSplineCurve PolesCount=4 KnotsCount=2 Degree=3 IsPeriodic=0
    g66: BSplineCurve PolesCount=2 KnotsCount=2 Degree=1 IsPeriodic=0
    g67: BSplineCurve PolesCount=2 KnotsCount=2 Degree=1 IsPeriodic=0
    g68: BSplineCurve PolesCount=4 KnotsCount=2 Degree=3 IsPeriodic=0
    g69: BSplineCurve PolesCount=2 KnotsCount=2 Degree=1 IsPeriodic=0
    g70: BSplineCurve PolesCount=4 KnotsCount=2 Degree=3 IsPeriodic=0
    g71: BSplineCurve PolesCount=4 KnotsCount=2 Degree=3 IsPeriodic=0
    g72: BSplineCurve PolesCount=2 KnotsCount=2 Degree=1 IsPeriodic=0
    g73: BSplineCurve PolesCount=2 KnotsCount=2 Degree=1 IsPeriodic=0
    g74: BSplineCurve PolesCount=4 KnotsCount=2 Degree=3 IsPeriodic=0
    g75: BSplineCurve PolesCount=2 KnotsCount=2 Degree=1 IsPeriodic=0
    g76: BSplineCurve PolesCount=2 KnotsCount=2 Degree=1 IsPeriodic=0
    g77: BSplineCurve PolesCount=4 KnotsCount=2 Degree=3 IsPeriodic=0
    g78: BSplineCurve PolesCount=4 KnotsCount=2 Degree=3 IsPeriodic=0
    g79: BSplineCurve PolesCount=4 KnotsCount=2 Degree=3 IsPeriodic=0
    g80: BSplineCurve PolesCount=4 KnotsCount=2 Degree=3 IsPeriodic=0
    g81: BSplineCurve PolesCount=2 KnotsCount=2 Degree=1 IsPeriodic=0
    g82: BSplineCurve PolesCount=2 KnotsCount=2 Degree=1 IsPeriodic=0
    g83: BSplineCurve PolesCount=4 KnotsCount=2 Degree=3 IsPeriodic=0
    g84: BSplineCurve PolesCount=4 KnotsCount=2 Degree=3 IsPeriodic=0
    g85: BSplineCurve PolesCount=4 KnotsCount=2 Degree=3 IsPeriodic=0
    g86: BSplineCurve PolesCount=2 KnotsCount=2 Degree=1 IsPeriodic=0
    g87: BSplineCurve PolesCount=2 KnotsCount=2 Degree=1 IsPeriodic=0
    g88: BSplineCurve PolesCount=4 KnotsCount=2 Degree=3 IsPeriodic=0
    g89: BSplineCurve PolesCount=2 KnotsCount=2 Degree=1 IsPeriodic=0
    g90: BSplineCurve PolesCount=4 KnotsCount=2 Degree=3 IsPeriodic=0
    g91: BSplineCurve PolesCount=4 KnotsCount=2 Degree=3 IsPeriodic=0
    g92: BSplineCurve PolesCount=4 KnotsCount=2 Degree=3 IsPeriodic=0
    g93: BSplineCurve PolesCount=2 KnotsCount=2 Degree=1 IsPeriodic=0
    g94: BSplineCurve PolesCount=2 KnotsCount=2 Degree=1 IsPeriodic=0
    g95: BSplineCurve PolesCount=4 KnotsCount=2 Degree=3 IsPeriodic=0
    g96: BSplineCurve PolesCount=2 KnotsCount=2 Degree=1 IsPeriodic=0
    g97: BSplineCurve PolesCount=2 KnotsCount=2 Degree=1 IsPeriodic=0
    g98: BSplineCurve PolesCount=2 KnotsCount=2 Degree=1 IsPeriodic=0
    g99: BSplineCurve PolesCount=4 KnotsCount=2 Degree=3 IsPeriodic=0
    g100: BSplineCurve PolesCount=4 KnotsCount=2 Degree=3 IsPeriodic=0
    g101: BSplineCurve PolesCount=4 KnotsCount=2 Degree=3 IsPeriodic=0
    g102: BSplineCurve PolesCount=4 KnotsCount=2 Degree=3 IsPeriodic=0
    g103: BSplineCurve PolesCount=4 KnotsCount=2 Degree=3 IsPeriodic=0
    g104: BSplineCurve PolesCount=4 KnotsCount=2 Degree=3 IsPeriodic=0
    g105: BSplineCurve PolesCount=4 KnotsCount=2 Degree=3 IsPeriodic=0
    g106: BSplineCurve PolesCount=4 KnotsCount=2 Degree=3 IsPeriodic=0
    g107: BSplineCurve PolesCount=4 KnotsCount=2 Degree=3 IsPeriodic=0
    g108: BSplineCurve PolesCount=4 KnotsCount=2 Degree=3 IsPeriodic=0
    g109: BSplineCurve PolesCount=4 KnotsCount=2 Degree=3 IsPeriodic=0
    g110: BSplineCurve PolesCount=4 KnotsCount=2 Degree=3 IsPeriodic=0
    g111: BSplineCurve PolesCount=2 KnotsCount=2 Degree=1 IsPeriodic=0
    g112: BSplineCurve PolesCount=4 KnotsCount=2 Degree=3 IsPeriodic=0
    g113: BSplineCurve PolesCount=4 KnotsCount=2 Degree=3 IsPeriodic=0
    g114: BSplineCurve PolesCount=4 KnotsCount=2 Degree=3 IsPeriodic=0
    g115: BSplineCurve PolesCount=4 KnotsCount=2 Degree=3 IsPeriodic=0
    g116: BSplineCurve PolesCount=4 KnotsCount=2 Degree=3 IsPeriodic=0
    g117: BSplineCurve PolesCount=2 KnotsCount=2 Degree=1 IsPeriodic=0
    g118: BSplineCurve PolesCount=2 KnotsCount=2 Degree=1 IsPeriodic=0
    g119: BSplineCurve PolesCount=4 KnotsCount=2 Degree=3 IsPeriodic=0
    g120: BSplineCurve PolesCount=4 KnotsCount=2 Degree=3 IsPeriodic=0
    g121: BSplineCurve PolesCount=4 KnotsCount=2 Degree=3 IsPeriodic=0
    g122: BSplineCurve PolesCount=4 KnotsCount=2 Degree=3 IsPeriodic=0
    g123: BSplineCurve PolesCount=4 KnotsCount=2 Degree=3 IsPeriodic=0
    g124: BSplineCurve PolesCount=4 KnotsCount=2 Degree=3 IsPeriodic=0
    g125: BSplineCurve PolesCount=2 KnotsCount=2 Degree=1 IsPeriodic=0
    g126: BSplineCurve PolesCount=4 KnotsCount=2 Degree=3 IsPeriodic=0
    g127: BSplineCurve PolesCount=4 KnotsCount=2 Degree=3 IsPeriodic=0
    g128: BSplineCurve PolesCount=2 KnotsCount=2 Degree=1 IsPeriodic=0
    g129: BSplineCurve PolesCount=2 KnotsCount=2 Degree=1 IsPeriodic=0
    g130: BSplineCurve PolesCount=4 KnotsCount=2 Degree=3 IsPeriodic=0
    g131: BSplineCurve PolesCount=4 KnotsCount=2 Degree=3 IsPeriodic=0
    g132: BSplineCurve PolesCount=4 KnotsCount=2 Degree=3 IsPeriodic=0
    g133: BSplineCurve PolesCount=4 KnotsCount=2 Degree=3 IsPeriodic=0
    g134: BSplineCurve PolesCount=4 KnotsCount=2 Degree=3 IsPeriodic=0
    g135: BSplineCurve PolesCount=4 KnotsCount=2 Degree=3 IsPeriodic=0
    g136: BSplineCurve PolesCount=4 KnotsCount=2 Degree=3 IsPeriodic=0
    g137: BSplineCurve PolesCount=2 KnotsCount=2 Degree=1 IsPeriodic=0
    g138: BSplineCurve PolesCount=2 KnotsCount=2 Degree=1 IsPeriodic=0
    g139: BSplineCurve PolesCount=4 KnotsCount=2 Degree=3 IsPeriodic=0
    g140: BSplineCurve PolesCount=4 KnotsCount=2 Degree=3 IsPeriodic=0
    g141: BSplineCurve PolesCount=2 KnotsCount=2 Degree=1 IsPeriodic=0
    g142: BSplineCurve PolesCount=2 KnotsCount=2 Degree=1 IsPeriodic=0
    g143: BSplineCurve PolesCount=4 KnotsCount=2 Degree=3 IsPeriodic=0
    g144: BSplineCurve PolesCount=4 KnotsCount=2 Degree=3 IsPeriodic=0
    g145: BSplineCurve PolesCount=4 KnotsCount=2 Degree=3 IsPeriodic=0
    g146: BSplineCurve PolesCount=4 KnotsCount=2 Degree=3 IsPeriodic=0
    g147: BSplineCurve PolesCount=4 KnotsCount=2 Degree=3 IsPeriodic=0
    g148: BSplineCurve PolesCount=4 KnotsCount=2 Degree=3 IsPeriodic=0
    g149: BSplineCurve PolesCount=4 KnotsCount=2 Degree=3 IsPeriodic=0
    g150: BSplineCurve PolesCount=4 KnotsCount=2 Degree=3 IsPeriodic=0
    g151: BSplineCurve PolesCount=4 KnotsCount=2 Degree=3 IsPeriodic=0
    g152: BSplineCurve PolesCount=4 KnotsCount=2 Degree=3 IsPeriodic=0
    g153: BSplineCurve PolesCount=4 KnotsCount=2 Degree=3 IsPeriodic=0
    g154: BSplineCurve PolesCount=4 KnotsCount=2 Degree=3 IsPeriodic=0
    g155: BSplineCurve PolesCount=4 KnotsCount=2 Degree=3 IsPeriodic=0
    g156: BSplineCurve PolesCount=4 KnotsCount=2 Degree=3 IsPeriodic=0
    g157: BSplineCurve PolesCount=4 KnotsCount=2 Degree=3 IsPeriodic=0
    g158: BSplineCurve PolesCount=4 KnotsCount=2 Degree=3 IsPeriodic=0
    g159: BSplineCurve PolesCount=4 KnotsCount=2 Degree=3 IsPeriodic=0
    g160: BSplineCurve PolesCount=4 KnotsCount=2 Degree=3 IsPeriodic=0
    g161: BSplineCurve PolesCount=4 KnotsCount=2 Degree=3 IsPeriodic=0
    g162: BSplineCurve PolesCount=4 KnotsCount=2 Degree=3 IsPeriodic=0
    g163: BSplineCurve PolesCount=4 KnotsCount=2 Degree=3 IsPeriodic=0
    g164: BSplineCurve PolesCount=4 KnotsCount=2 Degree=3 IsPeriodic=0
    g165: BSplineCurve PolesCount=4 KnotsCount=2 Degree=3 IsPeriodic=0
    g166: BSplineCurve PolesCount=4 KnotsCount=2 Degree=3 IsPeriodic=0
    g167: BSplineCurve PolesCount=4 KnotsCount=2 Degree=3 IsPeriodic=0
    g168: BSplineCurve PolesCount=4 KnotsCount=2 Degree=3 IsPeriodic=0
    g169: BSplineCurve PolesCount=4 KnotsCount=2 Degree=3 IsPeriodic=0
    g170: BSplineCurve PolesCount=4 KnotsCount=2 Degree=3 IsPeriodic=0
    g171: BSplineCurve PolesCount=4 KnotsCount=2 Degree=3 IsPeriodic=0
    g172: BSplineCurve PolesCount=4 KnotsCount=2 Degree=3 IsPeriodic=0
    g173: BSplineCurve PolesCount=4 KnotsCount=2 Degree=3 IsPeriodic=0
    g174: BSplineCurve PolesCount=4 KnotsCount=2 Degree=3 IsPeriodic=0
    g175: BSplineCurve PolesCount=4 KnotsCount=2 Degree=3 IsPeriodic=0
    g176: BSplineCurve PolesCount=4 KnotsCount=2 Degree=3 IsPeriodic=0
    g177: BSplineCurve PolesCount=4 KnotsCount=2 Degree=3 IsPeriodic=0
    g178: BSplineCurve PolesCount=4 KnotsCount=2 Degree=3 IsPeriodic=0
    g179: BSplineCurve PolesCount=4 KnotsCount=2 Degree=3 IsPeriodic=0
    g180: BSplineCurve PolesCount=4 KnotsCount=2 Degree=3 IsPeriodic=0
    g181: BSplineCurve PolesCount=4 KnotsCount=2 Degree=3 IsPeriodic=0
    g182: BSplineCurve PolesCount=4 KnotsCount=2 Degree=3 IsPeriodic=0
    g183: BSplineCurve PolesCount=4 KnotsCount=2 Degree=3 IsPeriodic=0
    g184: BSplineCurve PolesCount=4 KnotsCount=2 Degree=3 IsPeriodic=0
    g185: BSplineCurve PolesCount=4 KnotsCount=2 Degree=3 IsPeriodic=0
    g186: BSplineCurve PolesCount=4 KnotsCount=2 Degree=3 IsPeriodic=0
    g187: BSplineCurve PolesCount=4 KnotsCount=2 Degree=3 IsPeriodic=0
    g188: BSplineCurve PolesCount=4 KnotsCount=2 Degree=3 IsPeriodic=0
    g189: BSplineCurve PolesCount=4 KnotsCount=2 Degree=3 IsPeriodic=0
    g190: BSplineCurve PolesCount=4 KnotsCount=2 Degree=3 IsPeriodic=0
    g191: BSplineCurve PolesCount=4 KnotsCount=2 Degree=3 IsPeriodic=0
    g192: BSplineCurve PolesCount=4 KnotsCount=2 Degree=3 IsPeriodic=0
    g193: BSplineCurve PolesCount=2 KnotsCount=2 Degree=1 IsPeriodic=0
    g194: BSplineCurve PolesCount=2 KnotsCount=2 Degree=1 IsPeriodic=0
    g195: BSplineCurve PolesCount=4 KnotsCount=2 Degree=3 IsPeriodic=0
    g196: BSplineCurve PolesCount=4 KnotsCount=2 Degree=3 IsPeriodic=0
    g197: BSplineCurve PolesCount=4 KnotsCount=2 Degree=3 IsPeriodic=0
    g198: BSplineCurve PolesCount=2 KnotsCount=2 Degree=1 IsPeriodic=0
    g199: BSplineCurve PolesCount=2 KnotsCount=2 Degree=1 IsPeriodic=0
    g200: BSplineCurve PolesCount=4 KnotsCount=2 Degree=3 IsPeriodic=0
    g201: BSplineCurve PolesCount=4 KnotsCount=2 Degree=3 IsPeriodic=0
    g202: BSplineCurve PolesCount=4 KnotsCount=2 Degree=3 IsPeriodic=0
    g203: BSplineCurve PolesCount=4 KnotsCount=2 Degree=3 IsPeriodic=0
    g204: BSplineCurve PolesCount=4 KnotsCount=2 Degree=3 IsPeriodic=0
    g205: BSplineCurve PolesCount=4 KnotsCount=2 Degree=3 IsPeriodic=0
    g206: BSplineCurve PolesCount=4 KnotsCount=2 Degree=3 IsPeriodic=0
    g207: BSplineCurve PolesCount=4 KnotsCount=2 Degree=3 IsPeriodic=0
    g208: BSplineCurve PolesCount=4 KnotsCount=2 Degree=3 IsPeriodic=0
    g209: BSplineCurve PolesCount=4 KnotsCount=2 Degree=3 IsPeriodic=0
    g210: BSplineCurve PolesCount=4 KnotsCount=2 Degree=3 IsPeriodic=0
    g211: BSplineCurve PolesCount=4 KnotsCount=2 Degree=3 IsPeriodic=0
    g212: BSplineCurve PolesCount=2 KnotsCount=2 Degree=1 IsPeriodic=0
    g213: BSplineCurve PolesCount=2 KnotsCount=2 Degree=1 IsPeriodic=0
    g214: BSplineCurve PolesCount=4 KnotsCount=2 Degree=3 IsPeriodic=0
    g215: BSplineCurve PolesCount=4 KnotsCount=2 Degree=3 IsPeriodic=0
    g216: BSplineCurve PolesCount=4 KnotsCount=2 Degree=3 IsPeriodic=0
    g217: BSplineCurve PolesCount=4 KnotsCount=2 Degree=3 IsPeriodic=0
    g218: BSplineCurve PolesCount=4 KnotsCount=2 Degree=3 IsPeriodic=0
    g219: BSplineCurve PolesCount=4 KnotsCount=2 Degree=3 IsPeriodic=0
    g220: BSplineCurve PolesCount=4 KnotsCount=2 Degree=3 IsPeriodic=0
    g221: BSplineCurve PolesCount=4 KnotsCount=2 Degree=3 IsPeriodic=0
    g222: BSplineCurve PolesCount=4 KnotsCount=2 Degree=3 IsPeriodic=0
    g223: BSplineCurve PolesCount=4 KnotsCount=2 Degree=3 IsPeriodic=0
    g224: BSplineCurve PolesCount=4 KnotsCount=2 Degree=3 IsPeriodic=0
    g225: BSplineCurve PolesCount=4 KnotsCount=2 Degree=3 IsPeriodic=0
    g226: BSplineCurve PolesCount=4 KnotsCount=2 Degree=3 IsPeriodic=0
  constraints (232):
    c: Coincident(g0,g1)
    c: Coincident(g1,g2)
    c: Coincident(g2,g3)
    c: Coincident(g3,g4)
    c: Coincident(g4,g5)
    c: Coincident(g5,g6)
    c: Coincident(g6,g7)
    c: Coincident(g7,g8)
    c: Coincident(g8,g9)
    c: Coincident(g9,g10)
    c: Coincident(g10,g11)
    c: Coincident(g11,g12)
    c: Coincident(g12,g13)
    c: Coincident(g13,g14)
    c: Coincident(g14,g15)
    c: Coincident(g15,g16)
    c: Coincident(g16,g17)
    c: Coincident(g17,g18)
    c: Coincident(g18,g19)
    c: Coincident(g19,g20)
    c: Coincident(g20,g21)
    c: Coincident(g21,g22)
    c: Coincident(g22,g23)
    c: Coincident(g23,g24)
    c: Coincident(g24,g25)
    c: Coincident(g25,g26)
    c: Coincident(g26,g27)
    c: Coincident(g27,g28)
    c: Coincident(g28,g29)
    c: Coincident(g29,g30)
    c: Coincident(g30,g31)
    c: Coincident(g31,g32)
    c: Coincident(g32,g33)
    c: Coincident(g33,g34)
    c: Coincident(g34,g35)
    c: Coincident(g35,g36)
    c: Coincident(g36,g37)
    c: Coincident(g37,g38)
    c: Coincident(g38,g39)
    c: Coincident(g39,g40)
    c: Coincident(g40,g41)
    c: Coincident(g41,g42)
    c: Coincident(g42,g43)
    c: Coincident(g43,g44)
    c: Coincident(g44,g0)
    c: Coincident(g45,g46)
    c: Coincident(g46,g47)
    c: Coincident(g47,g45)
    c: Coincident(g48,g49)
    c: Coincident(g49,g50)
    c: Coincident(g50,g51)
    c: Coincident(g51,g52)
    c: Coincident(g52,g53)
    c: Coincident(g53,g54)
    c: Coincident(g54,g55)
    c: Coincident(g55,g56)
    c: Coincident(g56,g48)
    c: Coincident(g57,g58)
    c: Coincident(g58,g59)
    c: Coincident(g59,g60)
    c: Coincident(g60,g57)
    c: Coincident(g61,g62)
    c: Coincident(g62,g63)
    c: Coincident(g63,g64)
    c: Coincident(g64,g65)
    c: Coincident(g65,g66)
    c: Coincident(g66,g67)
    c: Coincident(g67,g68)
    c: Coincident(g68,g61)
    c: Coincident(g69,g70)
    c: Coincident(g70,g71)
    c: Coincident(g71,g72)
    c: Coincident(g72,g73)
    c: Coincident(g73,g74)
    c: Coincident(g74,g75)
    c: Coincident(g75,g69)
    c: Coincident(g76,g77)
    c: Coincident(g77,g78)
    c: Coincident(g78,g79)
    c: Coincident(g79,g80)
    c: Coincident(g80,g81)
    c: Coincident(g81,g76)
    c: Coincident(g82,g83)
    c: Coincident(g83,g84)
    c: Coincident(g84,g85)
    c: Coincident(g85,g86)
    c: Coincident(g86,g87)
    c: Coincident(g87,g88)
    c: Coincident(g88,g82)
    c: Coincident(g89,g90)
    c: Coincident(g90,g91)
    c: Coincident(g91,g92)
    c: Coincident(g92,g93)
    c: Coincident(g93,g94)
    c: Coincident(g94,g95)
    c: Coincident(g95,g89)
    c: Coincident(g96,g97)
    c: Coincident(g97,g98)
    c: Coincident(g98,g99)
    c: Coincident(g99,g100)
    c: Coincident(g100,g101)
    c: Coincident(g101,g102)
    c: Coincident(g102,g103)
    c: Coincident(g103,g104)
    c: Coincident(g104,g96)
    c: Coincident(g105,g106)
    c: Coincident(g106,g107)
    c: Coincident(g107,g108)
    c: Coincident(g108,g109)
    c: Coincident(g109,g110)
    c: Coincident(g110,g105)
    c: Coincident(g111,g112)
    c: Coincident(g112,g113)
    c: Coincident(g113,g114)
    c: Coincident(g114,g115)
    c: Coincident(g115,g116)
    c: Coincident(g116,g117)
    c: Coincident(g117,g118)
    c: Coincident(g118,g119)
    c: Coincident(g119,g111)
    c: Coincident(g120,g121)
    c: Coincident(g121,g122)
    c: Coincident(g122,g123)
    c: Coincident(g123,g124)
    c: Coincident(g124,g120)
    c: Coincident(g125,g126)
    c: Coincident(g126,g127)
    c: Coincident(g127,g128)
    c: Coincident(g128,g129)
    c: Coincident(g129,g130)
    c: Coincident(g130,g131)
    c: Coincident(g131,g132)
    c: Coincident(g132,g133)
    c: Coincident(g133,g134)
    c: Coincident(g134,g135)
    c: Coincident(g135,g136)
    c: Coincident(g136,g137)
    c: Coincident(g137,g138)
    c: Coincident(g138,g139)
    c: Coincident(g139,g140)
    c: Coincident(g140,g141)
    c: Coincident(g141,g142)
    c: Coincident(g142,g143)
    c: Coincident(g143,g144)
    c: Coincident(g144,g145)
    c: Coincident(g145,g146)
    c: Coincident(g146,g147)
    c: Coincident(g147,g148)
    c: Coincident(g148,g149)
    c: Coincident(g149,g150)
    c: Coincident(g150,g151)
    c: Coincident(g151,g152)
    c: Coincident(g152,g153)
    c: Coincident(g153,g154)
    c: Coincident(g154,g155)
    c: Coincident(g155,g156)
    c: Coincident(g156,g157)
    c: Coincident(g157,g158)
    c: Coincident(g158,g159)
    c: Coincident(g159,g160)
    c: Coincident(g160,g161)
    c: Coincident(g161,g162)
    c: Coincident(g162,g163)
    c: Coincident(g163,g164)
    c: Coincident(g164,g165)
    c: Coincident(g165,g166)
    c: Coincident(g166,g167)
    c: Coincident(g167,g168)
    c: Coincident(g168,g169)
    c: Coincident(g169,g170)
    c: Coincident(g170,g171)
    c: Coincident(g171,g172)
    c: Coincident(g172,g173)
    c: Coincident(g173,g174)
    c: Coincident(g174,g175)
    c: Coincident(g175,g176)
    c: Coincident(g176,g177)
    c: Coincident(g177,g178)
    c: Coincident(g178,g179)
    c: Coincident(g179,g180)
    c: Coincident(g180,g181)
    c: Coincident(g181,g182)
    c: Coincident(g182,g183)
    c: Coincident(g183,g184)
    c: Coincident(g184,g185)
    c: Coincident(g185,g186)
    c: Coincident(g186,g187)
    c: Coincident(g187,g188)
    c: Coincident(g188,g189)
    c: Coincident(g189,g190)
    c: Coincident(g190,g191)
    c: Coincident(g191,g192)
    c: Coincident(g192,g193)
    c: Coincident(g193,g194)
    c: Coincident(g194,g195)
    c: Coincident(g195,g196)
    c: Coincident(g196,g197)
    c: Coincident(g197,g198)
    c: Coincident(g198,g199)
    c: Coincident(g199,g200)
    c: Coincident(g200,g201)
    c: Coincident(g201,g202)
    c: Coincident(g202,g203)
    c: Coincident(g203,g204)
    c: Coincident(g204,g205)
    c: Coincident(g205,g206)
    c: Coincident(g206,g207)
    c: Coincident(g207,g208)
    c: Coincident(g208,g209)
    c: Coincident(g209,g210)
    c: Coincident(g210,g211)
    c: Coincident(g211,g212)
    c: Coincident(g212,g213)
    c: Coincident(g213,g214)
    c: Coincident(g214,g215)
    c: Coincident(g215,g216)
    c: Coincident(g216,g217)
    c: Coincident(g217,g218)
    c: Coincident(g218,g219)
    c: Coincident(g219,g220)
    c: Coincident(g220,g221)
    c: Coincident(g221,g222)
    c: Coincident(g222,g223)
    c: Coincident(g223,g224)
    c: Coincident(g224,g225)
    c: Coincident(g225,g226)
    c: Coincident(g226,g125)
    c: Coincident(g111,g111)
    c: Coincident(g96,g96)
    c: Coincident(g89,g89)
    c: Coincident(g82,g82)
    c: Coincident(g125,g125)
FEATURE [Sketcher::SketchObject] Sketch003  label="Drunk-Sketch"
  ArcFitTolerance = 1e-06
  FullyConstrained = false
  MakeInternals = false
  sketch-geometry (324):
    g0: BSplineCurve PolesCount=4 KnotsCount=2 Degree=3 IsPeriodic=0
    g1: BSplineCurve PolesCount=4 KnotsCount=2 Degree=3 IsPeriodic=0
    g2: BSplineCurve PolesCount=4 KnotsCount=2 Degree=3 IsPeriodic=0
    g3: BSplineCurve PolesCount=4 KnotsCount=2 Degree=3 IsPeriodic=0
    g4: BSplineCurve PolesCount=4 KnotsCount=2 Degree=3 IsPeriodic=0
    g5: BSplineCurve PolesCount=4 KnotsCount=2 Degree=3 IsPeriodic=0
    g6: BSplineCurve PolesCount=4 KnotsCount=2 Degree=3 IsPeriodic=0
    g7: BSplineCurve PolesCount=4 KnotsCount=2 Degree=3 IsPeriodic=0
    g8: BSplineCurve PolesCount=4 KnotsCount=2 Degree=3 IsPeriodic=0
    g9: BSplineCurve PolesCount=4 KnotsCount=2 Degree=3 IsPeriodic=0
    g10: BSplineCurve PolesCount=4 KnotsCount=2 Degree=3 IsPeriodic=0
    g11: BSplineCurve PolesCount=4 KnotsCount=2 Degree=3 IsPeriodic=0
    g12: BSplineCurve PolesCount=4 KnotsCount=2 Degree=3 IsPeriodic=0
    g13: BSplineCurve PolesCount=4 KnotsCount=2 Degree=3 IsPeriodic=0
    g14: BSplineCurve PolesCount=4 KnotsCount=2 Degree=3 IsPeriodic=0
    g15: BSplineCurve PolesCount=4 KnotsCount=2 Degree=3 IsPeriodic=0
    g16: BSplineCurve PolesCount=2 KnotsCount=2 Degree=1 IsPeriodic=0
    g17: BSplineCurve PolesCount=2 KnotsCount=2 Degree=1 IsPeriodic=0
    g18: BSplineCurve PolesCount=4 KnotsCount=2 Degree=3 IsPeriodic=0
    g19: BSplineCurve PolesCount=4 KnotsCount=2 Degree=3 IsPeriodic=0
    g20: BSplineCurve PolesCount=4 KnotsCount=2 Degree=3 IsPeriodic=0
    g21: BSplineCurve PolesCount=4 KnotsCount=2 Degree=3 IsPeriodic=0
    g22: BSplineCurve PolesCount=4 KnotsCount=2 Degree=3 IsPeriodic=0
    g23: BSplineCurve PolesCount=4 KnotsCount=2 Degree=3 IsPeriodic=0
    g24: BSplineCurve PolesCount=4 KnotsCount=2 Degree=3 IsPeriodic=0
    g25: BSplineCurve PolesCount=4 KnotsCount=2 Degree=3 IsPeriodic=0
    g26: BSplineCurve PolesCount=4 KnotsCount=2 Degree=3 IsPeriodic=0
    g27: BSplineCurve PolesCount=4 KnotsCount=2 Degree=3 IsPeriodic=0
    g28: BSplineCurve PolesCount=4 KnotsCount=2 Degree=3 IsPeriodic=0
    g29: BSplineCurve PolesCount=4 KnotsCount=2 Degree=3 IsPeriodic=0
    g30: BSplineCurve PolesCount=4 KnotsCount=2 Degree=3 IsPeriodic=0
    g31: BSplineCurve PolesCount=4 KnotsCount=2 Degree=3 IsPeriodic=0
    g32: BSplineCurve PolesCount=4 KnotsCount=2 Degree=3 IsPeriodic=0
    g33: BSplineCurve PolesCount=4 KnotsCount=2 Degree=3 IsPeriodic=0
    g34: BSplineCurve PolesCount=4 KnotsCount=2 Degree=3 IsPeriodic=0
    g35: BSplineCurve PolesCount=4 KnotsCount=2 Degree=3 IsPeriodic=0
    g36: BSplineCurve PolesCount=4 KnotsCount=2 Degree=3 IsPeriodic=0
    g37: BSplineCurve PolesCount=4 KnotsCount=2 Degree=3 IsPeriodic=0
    g38: BSplineCurve PolesCount=4 KnotsCount=2 Degree=3 IsPeriodic=0
    g39: BSplineCurve PolesCount=4 KnotsCount=2 Degree=3 IsPeriodic=0
    g40: BSplineCurve PolesCount=4 KnotsCount=2 Degree=3 IsPeriodic=0
    g41: BSplineCurve PolesCount=4 KnotsCount=2 Degree=3 IsPeriodic=0
    g42: BSplineCurve PolesCount=4 KnotsCount=2 Degree=3 IsPeriodic=0
    g43: BSplineCurve PolesCount=4 KnotsCount=2 Degree=3 IsPeriodic=0
    g44: BSplineCurve PolesCount=4 KnotsCount=2 Degree=3 IsPeriodic=0
    g45: BSplineCurve PolesCount=4 KnotsCount=2 Degree=3 IsPeriodic=0
    g46: BSplineCurve PolesCount=4 KnotsCount=2 Degree=3 IsPeriodic=0
    g47: BSplineCurve PolesCount=2 KnotsCount=2 Degree=1 IsPeriodic=0
    g48: BSplineCurve PolesCount=2 KnotsCount=2 Degree=1 IsPeriodic=0
    g49: BSplineCurve PolesCount=4 KnotsCount=2 Degree=3 IsPeriodic=0
    g50: BSplineCurve PolesCount=4 KnotsCount=2 Degree=3 IsPeriodic=0
    g51: BSplineCurve PolesCount=4 KnotsCount=2 Degree=3 IsPeriodic=0
    g52: BSplineCurve PolesCount=4 KnotsCount=2 Degree=3 IsPeriodic=0
    g53: BSplineCurve PolesCount=4 KnotsCount=2 Degree=3 IsPeriodic=0
    g54: BSplineCurve PolesCount=4 KnotsCount=2 Degree=3 IsPeriodic=0
    g55: BSplineCurve PolesCount=4 KnotsCount=2 Degree=3 IsPeriodic=0
    g56: BSplineCurve PolesCount=2 KnotsCount=2 Degree=1 IsPeriodic=0
    g57: BSplineCurve PolesCount=2 KnotsCount=2 Degree=1 IsPeriodic=0
    g58: BSplineCurve PolesCount=4 KnotsCount=2 Degree=3 IsPeriodic=0
    g59: BSplineCurve PolesCount=4 KnotsCount=2 Degree=3 IsPeriodic=0
    g60: BSplineCurve PolesCount=4 KnotsCount=2 Degree=3 IsPeriodic=0
    g61: BSplineCurve PolesCount=4 KnotsCount=2 Degree=3 IsPeriodic=0
    g62: BSplineCurve PolesCount=4 KnotsCount=2 Degree=3 IsPeriodic=0
    g63: BSplineCurve PolesCount=4 KnotsCount=2 Degree=3 IsPeriodic=0
    g64: BSplineCurve PolesCount=4 KnotsCount=2 Degree=3 IsPeriodic=0
    g65: BSplineCurve PolesCount=4 KnotsCount=2 Degree=3 IsPeriodic=0
    g66: BSplineCurve PolesCount=4 KnotsCount=2 Degree=3 IsPeriodic=0
    g67: BSplineCurve PolesCount=2 KnotsCount=2 Degree=1 IsPeriodic=0
    g68: BSplineCurve PolesCount=4 KnotsCount=2 Degree=3 IsPeriodic=0
    g69: BSplineCurve PolesCount=4 KnotsCount=2 Degree=3 IsPeriodic=0
    g70: BSplineCurve PolesCount=4 KnotsCount=2 Degree=3 IsPeriodic=0
    g71: BSplineCurve PolesCount=4 KnotsCount=2 Degree=3 IsPeriodic=0
    g72: BSplineCurve PolesCount=4 KnotsCount=2 Degree=3 IsPeriodic=0
    g73: BSplineCurve PolesCount=4 KnotsCount=2 Degree=3 IsPeriodic=0
    g74: BSplineCurve PolesCount=2 KnotsCount=2 Degree=1 IsPeriodic=0
    g75: BSplineCurve PolesCount=2 KnotsCount=2 Degree=1 IsPeriodic=0
    g76: BSplineCurve PolesCount=4 KnotsCount=2 Degree=3 IsPeriodic=0
    g77: BSplineCurve PolesCount=4 KnotsCount=2 Degree=3 IsPeriodic=0
    g78: BSplineCurve PolesCount=4 KnotsCount=2 Degree=3 IsPeriodic=0
    g79: BSplineCurve PolesCount=4 KnotsCount=2 Degree=3 IsPeriodic=0
    g80: BSplineCurve PolesCount=4 KnotsCount=2 Degree=3 IsPeriodic=0
    g81: BSplineCurve PolesCount=4 KnotsCount=2 Degree=3 IsPeriodic=0
    g82: BSplineCurve PolesCount=4 KnotsCount=2 Degree=3 IsPeriodic=0
    g83: BSplineCurve PolesCount=4 KnotsCount=2 Degree=3 IsPeriodic=0
    g84: BSplineCurve PolesCount=4 KnotsCount=2 Degree=3 IsPeriodic=0
    g85: BSplineCurve PolesCount=4 KnotsCount=2 Degree=3 IsPeriodic=0
    g86: BSplineCurve PolesCount=4 KnotsCount=2 Degree=3 IsPeriodic=0
    g87: BSplineCurve PolesCount=4 KnotsCount=2 Degree=3 IsPeriodic=0
    g88: BSplineCurve PolesCount=4 KnotsCount=2 Degree=3 IsPeriodic=0
    g89: BSplineCurve PolesCount=4 KnotsCount=2 Degree=3 IsPeriodic=0
    g90: BSplineCurve PolesCount=4 KnotsCount=2 Degree=3 IsPeriodic=0
    g91: BSplineCurve PolesCount=4 KnotsCount=2 Degree=3 IsPeriodic=0
    g92: BSplineCurve PolesCount=4 KnotsCount=2 Degree=3 IsPeriodic=0
    g93: BSplineCurve PolesCount=4 KnotsCount=2 Degree=3 IsPeriodic=0
    g94: BSplineCurve PolesCount=2 KnotsCount=2 Degree=1 IsPeriodic=0
    g95: BSplineCurve PolesCount=4 KnotsCount=2 Degree=3 IsPeriodic=0
    g96: BSplineCurve PolesCount=4 KnotsCount=2 Degree=3 IsPeriodic=0
    g97: BSplineCurve PolesCount=4 KnotsCount=2 Degree=3 IsPeriodic=0
    g98: BSplineCurve PolesCount=4 KnotsCount=2 Degree=3 IsPeriodic=0
    g99: BSplineCurve PolesCount=4 KnotsCount=2 Degree=3 IsPeriodic=0
    g100: BSplineCurve PolesCount=4 KnotsCount=2 Degree=3 IsPeriodic=0
    g101: BSplineCurve PolesCount=4 KnotsCount=2 Degree=3 IsPeriodic=0
    g102: BSplineCurve PolesCount=4 KnotsCount=2 Degree=3 IsPeriodic=0
    g103: BSplineCurve PolesCount=4 KnotsCount=2 Degree=3 IsPeriodic=0
    g104: BSplineCurve PolesCount=4 KnotsCount=2 Degree=3 IsPeriodic=0
    g105: BSplineCurve PolesCount=4 KnotsCount=2 Degree=3 IsPeriodic=0
    g106: BSplineCurve PolesCount=4 KnotsCount=2 Degree=3 IsPeriodic=0
    g107: BSplineCurve PolesCount=4 KnotsCount=2 Degree=3 IsPeriodic=0
    g108: BSplineCurve PolesCount=4 KnotsCount=2 Degree=3 IsPeriodic=0
    g109: BSplineCurve PolesCount=2 KnotsCount=2 Degree=1 IsPeriodic=0
    g110: BSplineCurve PolesCount=2 KnotsCount=2 Degree=1 IsPeriodic=0
    g111: BSplineCurve PolesCount=4 KnotsCount=2 Degree=3 IsPeriodic=0
    g112: BSplineCurve PolesCount=4 KnotsCount=2 Degree=3 IsPeriodic=0
    g113: BSplineCurve PolesCount=4 KnotsCount=2 Degree=3 IsPeriodic=0
    g114: BSplineCurve PolesCount=4 KnotsCount=2 Degree=3 IsPeriodic=0
    g115: BSplineCurve PolesCount=4 KnotsCount=2 Degree=3 IsPeriodic=0
    g116: BSplineCurve PolesCount=4 KnotsCount=2 Degree=3 IsPeriodic=0
    g117: BSplineCurve PolesCount=4 KnotsCount=2 Degree=3 IsPeriodic=0
    g118: BSplineCurve PolesCount=4 KnotsCount=2 Degree=3 IsPeriodic=0
    g119: BSplineCurve PolesCount=4 KnotsCount=2 Degree=3 IsPeriodic=0
    g120: BSplineCurve PolesCount=4 KnotsCount=2 Degree=3 IsPeriodic=0
    g121: BSplineCurve PolesCount=4 KnotsCount=2 Degree=3 IsPeriodic=0
    g122: BSplineCurve PolesCount=4 KnotsCount=2 Degree=3 IsPeriodic=0
    g123: BSplineCurve PolesCount=2 KnotsCount=2 Degree=1 IsPeriodic=0
    g124: BSplineCurve PolesCount=4 KnotsCount=2 Degree=3 IsPeriodic=0
    g125: BSplineCurve PolesCount=4 KnotsCount=2 Degree=3 IsPeriodic=0
    g126: BSplineCurve PolesCount=4 KnotsCount=2 Degree=3 IsPeriodic=0
    g127: BSplineCurve PolesCount=2 KnotsCount=2 Degree=1 IsPeriodic=0
    g128: BSplineCurve PolesCount=2 KnotsCount=2 Degree=1 IsPeriodic=0
    g129: BSplineCurve PolesCount=4 KnotsCount=2 Degree=3 IsPeriodic=0
    g130: BSplineCurve PolesCount=4 KnotsCount=2 Degree=3 IsPeriodic=0
    g131: BSplineCurve PolesCount=4 KnotsCount=2 Degree=3 IsPeriodic=0
    g132: BSplineCurve PolesCount=4 KnotsCount=2 Degree=3 IsPeriodic=0
    g133: BSplineCurve PolesCount=4 KnotsCount=2 Degree=3 IsPeriodic=0
    g134: BSplineCurve PolesCount=4 KnotsCount=2 Degree=3 IsPeriodic=0
    g135: BSplineCurve PolesCount=4 KnotsCount=2 Degree=3 IsPeriodic=0
    g136: BSplineCurve PolesCount=4 KnotsCount=2 Degree=3 IsPeriodic=0
    g137: BSplineCurve PolesCount=4 KnotsCount=2 Degree=3 IsPeriodic=0
    g138: BSplineCurve PolesCount=4 KnotsCount=2 Degree=3 IsPeriodic=0
    g139: BSplineCurve PolesCount=2 KnotsCount=2 Degree=1 IsPeriodic=0
    g140: BSplineCurve PolesCount=2 KnotsCount=2 Degree=1 IsPeriodic=0
    g141: BSplineCurve PolesCount=4 KnotsCount=2 Degree=3 IsPeriodic=0
    g142: BSplineCurve PolesCount=4 KnotsCount=2 Degree=3 IsPeriodic=0
    g143: BSplineCurve PolesCount=4 KnotsCount=2 Degree=3 IsPeriodic=0
    g144: BSplineCurve PolesCount=4 KnotsCount=2 Degree=3 IsPeriodic=0
    g145: BSplineCurve PolesCount=4 KnotsCount=2 Degree=3 IsPeriodic=0
    g146: BSplineCurve PolesCount=2 KnotsCount=2 Degree=1 IsPeriodic=0
    g147: BSplineCurve PolesCount=4 KnotsCount=2 Degree=3 IsPeriodic=0
    g148: BSplineCurve PolesCount=4 KnotsCount=2 Degree=3 IsPeriodic=0
    g149: BSplineCurve PolesCount=4 KnotsCount=2 Degree=3 IsPeriodic=0
    g150: BSplineCurve PolesCount=2 KnotsCount=2 Degree=1 IsPeriodic=0
    g151: BSplineCurve PolesCount=2 KnotsCount=2 Degree=1 IsPeriodic=0
    g152: BSplineCurve PolesCount=4 KnotsCount=2 Degree=3 IsPeriodic=0
    g153: BSplineCurve PolesCount=4 KnotsCount=2 Degree=3 IsPeriodic=0
    g154: BSplineCurve PolesCount=4 KnotsCount=2 Degree=3 IsPeriodic=0
    g155: BSplineCurve PolesCount=4 KnotsCount=2 Degree=3 IsPeriodic=0
    g156: BSplineCurve PolesCount=4 KnotsCount=2 Degree=3 IsPeriodic=0
    g157: BSplineCurve PolesCount=4 KnotsCount=2 Degree=3 IsPeriodic=0
    g158: BSplineCurve PolesCount=4 KnotsCount=2 Degree=3 IsPeriodic=0
    g159: BSplineCurve PolesCount=4 KnotsCount=2 Degree=3 IsPeriodic=0
    g160: BSplineCurve PolesCount=4 KnotsCount=2 Degree=3 IsPeriodic=0
    g161: BSplineCurve PolesCount=4 KnotsCount=2 Degree=3 IsPeriodic=0
    g162: BSplineCurve PolesCount=4 KnotsCount=2 Degree=3 IsPeriodic=0
    g163: BSplineCurve PolesCount=2 KnotsCount=2 Degree=1 IsPeriodic=0
    g164: BSplineCurve PolesCount=4 KnotsCount=2 Degree=3 IsPeriodic=0
    g165: BSplineCurve PolesCount=4 KnotsCount=2 Degree=3 IsPeriodic=0
    g166: BSplineCurve PolesCount=4 KnotsCount=2 Degree=3 IsPeriodic=0
    g167: BSplineCurve PolesCount=4 KnotsCount=2 Degree=3 IsPeriodic=0
    g168: BSplineCurve PolesCount=4 KnotsCount=2 Degree=3 IsPeriodic=0
    g169: BSplineCurve PolesCount=4 KnotsCount=2 Degree=3 IsPeriodic=0
    g170: BSplineCurve PolesCount=4 KnotsCount=2 Degree=3 IsPeriodic=0
    g171: BSplineCurve PolesCount=4 KnotsCount=2 Degree=3 IsPeriodic=0
    g172: BSplineCurve PolesCount=4 KnotsCount=2 Degree=3 IsPeriodic=0
    g173: BSplineCurve PolesCount=4 KnotsCount=2 Degree=3 IsPeriodic=0
    g174: BSplineCurve PolesCount=4 KnotsCount=2 Degree=3 IsPeriodic=0
    g175: BSplineCurve PolesCount=4 KnotsCount=2 Degree=3 IsPeriodic=0
    g176: BSplineCurve PolesCount=4 KnotsCount=2 Degree=3 IsPeriodic=0
    g177: BSplineCurve PolesCount=4 KnotsCount=2 Degree=3 IsPeriodic=0
    g178: BSplineCurve PolesCount=4 KnotsCount=2 Degree=3 IsPeriodic=0
    g179: BSplineCurve PolesCount=4 KnotsCount=2 Degree=3 IsPeriodic=0
    g180: BSplineCurve PolesCount=4 KnotsCount=2 Degree=3 IsPeriodic=0
    g181: BSplineCurve PolesCount=4 KnotsCount=2 Degree=3 IsPeriodic=0
    g182: BSplineCurve PolesCount=4 KnotsCount=2 Degree=3 IsPeriodic=0
    g183: BSplineCurve PolesCount=4 KnotsCount=2 Degree=3 IsPeriodic=0
    g184: BSplineCurve PolesCount=4 KnotsCount=2 Degree=3 IsPeriodic=0
    g185: BSplineCurve PolesCount=4 KnotsCount=2 Degree=3 IsPeriodic=0
    g186: BSplineCurve PolesCount=4 KnotsCount=2 Degree=3 IsPeriodic=0
    g187: BSplineCurve PolesCount=4 KnotsCount=2 Degree=3 IsPeriodic=0
    g188: BSplineCurve PolesCount=4 KnotsCount=2 Degree=3 IsPeriodic=0
    g189: BSplineCurve PolesCount=4 KnotsCount=2 Degree=3 IsPeriodic=0
    g190: BSplineCurve PolesCount=4 KnotsCount=2 Degree=3 IsPeriodic=0
    g191: BSplineCurve PolesCount=4 KnotsCount=2 Degree=3 IsPeriodic=0
    g192: BSplineCurve PolesCount=4 KnotsCount=2 Degree=3 IsPeriodic=0
    g193: BSplineCurve PolesCount=4 KnotsCount=2 Degree=3 IsPeriodic=0
    g194: BSplineCurve PolesCount=4 KnotsCount=2 Degree=3 IsPeriodic=0
    g195: BSplineCurve PolesCount=4 KnotsCount=2 Degree=3 IsPeriodic=0
    g196: BSplineCurve PolesCount=2 KnotsCount=2 Degree=1 IsPeriodic=0
    g197: BSplineCurve PolesCount=2 KnotsCount=2 Degree=1 IsPeriodic=0
    g198: BSplineCurve PolesCount=4 KnotsCount=2 Degree=3 IsPeriodic=0
    g199: BSplineCurve PolesCount=4 KnotsCount=2 Degree=3 IsPeriodic=0
    g200: BSplineCurve PolesCount=4 KnotsCount=2 Degree=3 IsPeriodic=0
    g201: BSplineCurve PolesCount=4 KnotsCount=2 Degree=3 IsPeriodic=0
    g202: BSplineCurve PolesCount=4 KnotsCount=2 Degree=3 IsPeriodic=0
    g203: BSplineCurve PolesCount=4 KnotsCount=2 Degree=3 IsPeriodic=0
    g204: BSplineCurve PolesCount=4 KnotsCount=2 Degree=3 IsPeriodic=0
    g205: BSplineCurve PolesCount=4 KnotsCount=2 Degree=3 IsPeriodic=0
    g206: BSplineCurve PolesCount=4 KnotsCount=2 Degree=3 IsPeriodic=0
    g207: BSplineCurve PolesCount=4 KnotsCount=2 Degree=3 IsPeriodic=0
    g208: BSplineCurve PolesCount=4 KnotsCount=2 Degree=3 IsPeriodic=0
    g209: BSplineCurve PolesCount=4 KnotsCount=2 Degree=3 IsPeriodic=0
    g210: BSplineCurve PolesCount=4 KnotsCount=2 Degree=3 IsPeriodic=0
    g211: BSplineCurve PolesCount=4 KnotsCount=2 Degree=3 IsPeriodic=0
    g212: BSplineCurve PolesCount=4 KnotsCount=2 Degree=3 IsPeriodic=0
    g213: BSplineCurve PolesCount=4 KnotsCount=2 Degree=3 IsPeriodic=0
    g214: BSplineCurve PolesCount=4 KnotsCount=2 Degree=3 IsPeriodic=0
    g215: BSplineCurve PolesCount=4 KnotsCount=2 Degree=3 IsPeriodic=0
    g216: BSplineCurve PolesCount=4 KnotsCount=2 Degree=3 IsPeriodic=0
    g217: BSplineCurve PolesCount=4 KnotsCount=2 Degree=3 IsPeriodic=0
    g218: BSplineCurve PolesCount=4 KnotsCount=2 Degree=3 IsPeriodic=0
    g219: BSplineCurve PolesCount=4 KnotsCount=2 Degree=3 IsPeriodic=0
    g220: BSplineCurve PolesCount=4 KnotsCount=2 Degree=3 IsPeriodic=0
    g221: BSplineCurve PolesCount=4 KnotsCount=2 Degree=3 IsPeriodic=0
    g222: BSplineCurve PolesCount=4 KnotsCount=2 Degree=3 IsPeriodic=0
    g223: BSplineCurve PolesCount=4 KnotsCount=2 Degree=3 IsPeriodic=0
    g224: BSplineCurve PolesCount=4 KnotsCount=2 Degree=3 IsPeriodic=0
    g225: BSplineCurve PolesCount=4 KnotsCount=2 Degree=3 IsPeriodic=0
    g226: BSplineCurve PolesCount=4 KnotsCount=2 Degree=3 IsPeriodic=0
    g227: BSplineCurve PolesCount=4 KnotsCount=2 Degree=3 IsPeriodic=0
    g228: BSplineCurve PolesCount=4 KnotsCount=2 Degree=3 IsPeriodic=0
    g229: BSplineCurve PolesCount=4 KnotsCount=2 Degree=3 IsPeriodic=0
    g230: BSplineCurve PolesCount=4 KnotsCount=2 Degree=3 IsPeriodic=0
    g231: BSplineCurve PolesCount=4 KnotsCount=2 Degree=3 IsPeriodic=0
    g232: BSplineCurve PolesCount=4 KnotsCount=2 Degree=3 IsPeriodic=0
    g233: BSplineCurve PolesCount=4 KnotsCount=2 Degree=3 IsPeriodic=0
    g234: BSplineCurve PolesCount=4 KnotsCount=2 Degree=3 IsPeriodic=0
    g235: BSplineCurve PolesCount=4 KnotsCount=2 Degree=3 IsPeriodic=0
    g236: BSplineCurve PolesCount=4 KnotsCount=2 Degree=3 IsPeriodic=0
    g237: BSplineCurve PolesCount=4 KnotsCount=2 Degree=3 IsPeriodic=0
    g238: BSplineCurve PolesCount=4 KnotsCount=2 Degree=3 IsPeriodic=0
    g239: BSplineCurve PolesCount=4 KnotsCount=2 Degree=3 IsPeriodic=0
    g240: BSplineCurve PolesCount=4 KnotsCount=2 Degree=3 IsPeriodic=0
    g241: BSplineCurve PolesCount=4 KnotsCount=2 Degree=3 IsPeriodic=0
    g242: BSplineCurve PolesCount=4 KnotsCount=2 Degree=3 IsPeriodic=0
    g243: BSplineCurve PolesCount=4 KnotsCount=2 Degree=3 IsPeriodic=0
    g244: BSplineCurve PolesCount=4 KnotsCount=2 Degree=3 IsPeriodic=0
    g245: BSplineCurve PolesCount=4 KnotsCount=2 Degree=3 IsPeriodic=0
    g246: BSplineCurve PolesCount=4 KnotsCount=2 Degree=3 IsPeriodic=0
    g247: BSplineCurve PolesCount=2 KnotsCount=2 Degree=1 IsPeriodic=0
    g248: BSplineCurve PolesCount=2 KnotsCount=2 Degree=1 IsPeriodic=0
    g249: BSplineCurve PolesCount=4 KnotsCount=2 Degree=3 IsPeriodic=0
    g250: BSplineCurve PolesCount=4 KnotsCount=2 Degree=3 IsPeriodic=0
    g251: BSplineCurve PolesCount=4 KnotsCount=2 Degree=3 IsPeriodic=0
    g252: BSplineCurve PolesCount=2 KnotsCount=2 Degree=1 IsPeriodic=0
    g253: BSplineCurve PolesCount=2 KnotsCount=2 Degree=1 IsPeriodic=0
    g254: BSplineCurve PolesCount=2 KnotsCount=2 Degree=1 IsPeriodic=0
    g255: BSplineCurve PolesCount=4 KnotsCount=2 Degree=3 IsPeriodic=0
    g256: BSplineCurve PolesCount=4 KnotsCount=2 Degree=3 IsPeriodic=0
    g257: BSplineCurve PolesCount=4 KnotsCount=2 Degree=3 IsPeriodic=0
    g258: BSplineCurve PolesCount=4 KnotsCount=2 Degree=3 IsPeriodic=0
    g259: BSplineCurve PolesCount=4 KnotsCount=2 Degree=3 IsPeriodic=0
    g260: BSplineCurve PolesCount=4 KnotsCount=2 Degree=3 IsPeriodic=0
    g261: BSplineCurve PolesCount=4 KnotsCount=2 Degree=3 IsPeriodic=0
    g262: BSplineCurve PolesCount=4 KnotsCount=2 Degree=3 IsPeriodic=0
    g263: BSplineCurve PolesCount=4 KnotsCount=2 Degree=3 IsPeriodic=0
    g264: BSplineCurve PolesCount=4 KnotsCount=2 Degree=3 IsPeriodic=0
    g265: BSplineCurve PolesCount=4 KnotsCount=2 Degree=3 IsPeriodic=0
    g266: BSplineCurve PolesCount=4 KnotsCount=2 Degree=3 IsPeriodic=0
    g267: BSplineCurve PolesCount=4 KnotsCount=2 Degree=3 IsPeriodic=0
    g268: BSplineCurve PolesCount=4 KnotsCount=2 Degree=3 IsPeriodic=0
    g269: BSplineCurve PolesCount=4 KnotsCount=2 Degree=3 IsPeriodic=0
    g270: BSplineCurve PolesCount=4 KnotsCount=2 Degree=3 IsPeriodic=0
    g271: BSplineCurve PolesCount=4 KnotsCount=2 Degree=3 IsPeriodic=0
    g272: BSplineCurve PolesCount=4 KnotsCount=2 Degree=3 IsPeriodic=0
    g273: BSplineCurve PolesCount=4 KnotsCount=2 Degree=3 IsPeriodic=0
    g274: BSplineCurve PolesCount=4 KnotsCount=2 Degree=3 IsPeriodic=0
    g275: BSplineCurve PolesCount=4 KnotsCount=2 Degree=3 IsPeriodic=0
    g276: BSplineCurve PolesCount=4 KnotsCount=2 Degree=3 IsPeriodic=0
    g277: BSplineCurve PolesCount=4 KnotsCount=2 Degree=3 IsPeriodic=0
    g278: BSplineCurve PolesCount=4 KnotsCount=2 Degree=3 IsPeriodic=0
    g279: BSplineCurve PolesCount=4 KnotsCount=2 Degree=3 IsPeriodic=0
    g280: BSplineCurve PolesCount=4 KnotsCount=2 Degree=3 IsPeriodic=0
    g281: BSplineCurve PolesCount=4 KnotsCount=2 Degree=3 IsPeriodic=0
    g282: BSplineCurve PolesCount=4 KnotsCount=2 Degree=3 IsPeriodic=0
    g283: BSplineCurve PolesCount=4 KnotsCount=2 Degree=3 IsPeriodic=0
    g284: BSplineCurve PolesCount=4 KnotsCount=2 Degree=3 IsPeriodic=0
    g285: BSplineCurve PolesCount=4 KnotsCount=2 Degree=3 IsPeriodic=0
    g286: BSplineCurve PolesCount=4 KnotsCount=2 Degree=3 IsPeriodic=0
    g287: BSplineCurve PolesCount=4 KnotsCount=2 Degree=3 IsPeriodic=0
    g288: BSplineCurve PolesCount=4 KnotsCount=2 Degree=3 IsPeriodic=0
    g289: BSplineCurve PolesCount=4 KnotsCount=2 Degree=3 IsPeriodic=0
    g290: BSplineCurve PolesCount=4 KnotsCount=2 Degree=3 IsPeriodic=0
    g291: BSplineCurve PolesCount=4 KnotsCount=2 Degree=3 IsPeriodic=0
    g292: BSplineCurve PolesCount=4 KnotsCount=2 Degree=3 IsPeriodic=0
    g293: BSplineCurve PolesCount=4 KnotsCount=2 Degree=3 IsPeriodic=0
    g294: BSplineCurve PolesCount=4 KnotsCount=2 Degree=3 IsPeriodic=0
    g295: BSplineCurve PolesCount=4 KnotsCount=2 Degree=3 IsPeriodic=0
    g296: BSplineCurve PolesCount=4 KnotsCount=2 Degree=3 IsPeriodic=0
    g297: BSplineCurve PolesCount=4 KnotsCount=2 Degree=3 IsPeriodic=0
    g298: BSplineCurve PolesCount=4 KnotsCount=2 Degree=3 IsPeriodic=0
    g299: BSplineCurve PolesCount=4 KnotsCount=2 Degree=3 IsPeriodic=0
    g300: BSplineCurve PolesCount=4 KnotsCount=2 Degree=3 IsPeriodic=0
    g301: BSplineCurve PolesCount=4 KnotsCount=2 Degree=3 IsPeriodic=0
    g302: BSplineCurve PolesCount=4 KnotsCount=2 Degree=3 IsPeriodic=0
    g303: BSplineCurve PolesCount=4 KnotsCount=2 Degree=3 IsPeriodic=0
    g304: BSplineCurve PolesCount=4 KnotsCount=2 Degree=3 IsPeriodic=0
    g305: BSplineCurve PolesCount=4 KnotsCount=2 Degree=3 IsPeriodic=0
    g306: BSplineCurve PolesCount=4 KnotsCount=2 Degree=3 IsPeriodic=0
    g307: BSplineCurve PolesCount=4 KnotsCount=2 Degree=3 IsPeriodic=0
    g308: BSplineCurve PolesCount=4 KnotsCount=2 Degree=3 IsPeriodic=0
    g309: BSplineCurve PolesCount=4 KnotsCount=2 Degree=3 IsPeriodic=0
    g310: BSplineCurve PolesCount=4 KnotsCount=2 Degree=3 IsPeriodic=0
    g311: BSplineCurve PolesCount=4 KnotsCount=2 Degree=3 IsPeriodic=0
    g312: BSplineCurve PolesCount=4 KnotsCount=2 Degree=3 IsPeriodic=0
    g313: BSplineCurve PolesCount=4 KnotsCount=2 Degree=3 IsPeriodic=0
    g314: BSplineCurve PolesCount=4 KnotsCount=2 Degree=3 IsPeriodic=0
    g315: BSplineCurve PolesCount=4 KnotsCount=2 Degree=3 IsPeriodic=0
    g316: BSplineCurve PolesCount=4 KnotsCount=2 Degree=3 IsPeriodic=0
    g317: BSplineCurve PolesCount=4 KnotsCount=2 Degree=3 IsPeriodic=0
    g318: BSplineCurve PolesCount=4 KnotsCount=2 Degree=3 IsPeriodic=0
    g319: BSplineCurve PolesCount=4 KnotsCount=2 Degree=3 IsPeriodic=0
    g320: BSplineCurve PolesCount=4 KnotsCount=2 Degree=3 IsPeriodic=0
    g321: BSplineCurve PolesCount=4 KnotsCount=2 Degree=3 IsPeriodic=0
    g322: BSplineCurve PolesCount=4 KnotsCount=2 Degree=3 IsPeriodic=0
    g323: BSplineCurve PolesCount=4 KnotsCount=2 Degree=3 IsPeriodic=0
  constraints (329):
    c: Coincident(g0,g1)
    c: Coincident(g1,g2)
    c: Coincident(g2,g3)
    c: Coincident(g3,g4)
    c: Coincident(g4,g5)
    c: Coincident(g5,g6)
    c: Coincident(g6,g7)
    c: Coincident(g7,g8)
    c: Coincident(g8,g9)
    c: Coincident(g9,g10)
    c: Coincident(g10,g11)
    c: Coincident(g11,g12)
    c: Coincident(g12,g13)
    c: Coincident(g13,g14)
    c: Coincident(g14,g15)
    c: Coincident(g15,g16)
    c: Coincident(g16,g17)
    c: Coincident(g17,g18)
    c: Coincident(g18,g19)
    c: Coincident(g19,g20)
    c: Coincident(g20,g21)
    c: Coincident(g21,g22)
    c: Coincident(g22,g23)
    c: Coincident(g23,g24)
    c: Coincident(g24,g25)
    c: Coincident(g25,g26)
    c: Coincident(g26,g27)
    c: Coincident(g27,g28)
    c: Coincident(g28,g29)
    c: Coincident(g29,g30)
    c: Coincident(g30,g31)
    c: Coincident(g31,g32)
    c: Coincident(g32,g33)
    c: Coincident(g33,g34)
    c: Coincident(g34,g35)
    c: Coincident(g35,g36)
    c: Coincident(g36,g37)
    c: Coincident(g37,g38)
    c: Coincident(g38,g39)
    c: Coincident(g39,g40)
    c: Coincident(g40,g41)
    c: Coincident(g41,g42)
    c: Coincident(g42,g43)
    c: Coincident(g43,g44)
    c: Coincident(g44,g45)
    c: Coincident(g45,g46)
    c: Coincident(g46,g47)
    c: Coincident(g47,g48)
    c: Coincident(g48,g49)
    c: Coincident(g49,g50)
    c: Coincident(g50,g51)
    c: Coincident(g51,g52)
    c: Coincident(g52,g53)
    c: Coincident(g53,g54)
    c: Coincident(g54,g55)
    c: Coincident(g55,g56)
    c: Coincident(g56,g57)
    c: Coincident(g57,g58)
    c: Coincident(g58,g59)
    c: Coincident(g59,g60)
    c: Coincident(g60,g61)
    c: Coincident(g61,g62)
    c: Coincident(g62,g63)
    c: Coincident(g63,g64)
    c: Coincident(g64,g65)
    c: Coincident(g65,g66)
    c: Coincident(g66,g67)
    c: Coincident(g67,g0)
    c: Coincident(g68,g69)
    c: Coincident(g69,g70)
    c: Coincident(g70,g71)
    c: Coincident(g71,g72)
    c: Coincident(g72,g73)
    c: Coincident(g73,g74)
    c: Coincident(g74,g75)
    c: Coincident(g75,g68)
    c: Coincident(g76,g77)
    c: Coincident(g77,g78)
    c: Coincident(g78,g79)
    c: Coincident(g79,g80)
    c: Coincident(g80,g81)
    c: Coincident(g81,g82)
    c: Coincident(g82,g83)
    c: Coincident(g83,g84)
    c: Coincident(g84,g85)
    c: Coincident(g85,g86)
    c: Coincident(g86,g87)
    c: Coincident(g87,g88)
    c: Coincident(g88,g76)
    c: Coincident(g89,g90)
    c: Coincident(g90,g91)
    c: Coincident(g91,g92)
    c: Coincident(g92,g93)
    c: Coincident(g93,g89)
    c: Coincident(g94,g95)
    c: Coincident(g95,g96)
    c: Coincident(g96,g97)
    c: Coincident(g97,g98)
    c: Coincident(g98,g99)
    c: Coincident(g99,g100)
    c: Coincident(g100,g101)
    c: Coincident(g101,g102)
    c: Coincident(g102,g103)
    c: Coincident(g103,g104)
    c: Coincident(g104,g105)
    c: Coincident(g105,g106)
    c: Coincident(g106,g107)
    c: Coincident(g107,g108)
    c: Coincident(g108,g109)
    c: Coincident(g109,g110)
    c: Coincident(g110,g111)
    c: Coincident(g111,g112)
    c: Coincident(g112,g113)
    c: Coincident(g113,g114)
    c: Coincident(g114,g94)
    c: Coincident(g115,g116)
    c: Coincident(g116,g117)
    c: Coincident(g117,g118)
    c: Coincident(g118,g119)
    c: Coincident(g119,g120)
    c: Coincident(g120,g121)
    c: Coincident(g121,g122)
    c: Coincident(g122,g115)
    c: Coincident(g123,g124)
    c: Coincident(g124,g125)
    c: Coincident(g125,g126)
    c: Coincident(g126,g127)
    c: Coincident(g127,g128)
    c: Coincident(g128,g129)
    c: Coincident(g129,g130)
    c: Coincident(g130,g131)
    c: Coincident(g131,g132)
    c: Coincident(g132,g133)
    c: Coincident(g133,g134)
    c: Coincident(g134,g135)
    c: Coincident(g135,g136)
    c: Coincident(g136,g137)
    c: Coincident(g137,g138)
    c: Coincident(g138,g139)
    c: Coincident(g139,g140)
    c: Coincident(g140,g141)
    c: Coincident(g141,g142)
    c: Coincident(g142,g143)
    c: Coincident(g143,g144)
    c: Coincident(g144,g145)
    c: Coincident(g145,g123)
    c: Coincident(g146,g147)
    c: Coincident(g147,g148)
    c: Coincident(g148,g149)
    c: Coincident(g149,g150)
    c: Coincident(g150,g151)
    c: Coincident(g151,g152)
    c: Coincident(g152,g153)
    c: Coincident(g153,g154)
    c: Coincident(g154,g146)
    c: Coincident(g155,g156)
    c: Coincident(g156,g157)
    c: Coincident(g157,g158)
    c: Coincident(g158,g159)
    c: Coincident(g159,g160)
    c: Coincident(g160,g161)
    c: Coincident(g161,g162)
    c: Coincident(g162,g155)
    c: Coincident(g163,g164)
    c: Coincident(g164,g165)
    c: Coincident(g165,g166)
    c: Coincident(g166,g167)
    c: Coincident(g167,g168)
    c: Coincident(g168,g169)
    c: Coincident(g169,g170)
    c: Coincident(g170,g171)
    c: Coincident(g171,g172)
    c: Coincident(g172,g173)
    c: Coincident(g173,g174)
    c: Coincident(g174,g175)
    c: Coincident(g175,g176)
    c: Coincident(g176,g177)
    c: Coincident(g177,g178)
    c: Coincident(g178,g179)
    c: Coincident(g179,g180)
    c: Coincident(g180,g181)
    c: Coincident(g181,g182)
    c: Coincident(g182,g183)
    c: Coincident(g183,g184)
    c: Coincident(g184,g185)
    c: Coincident(g185,g186)
    c: Coincident(g186,g187)
    c: Coincident(g187,g188)
    c: Coincident(g188,g189)
    c: Coincident(g189,g190)
    c: Coincident(g190,g191)
    c: Coincident(g191,g192)
    c: Coincident(g192,g193)
    c: Coincident(g193,g194)
    c: Coincident(g194,g195)
    c: Coincident(g195,g196)
    c: Coincident(g196,g197)
    c: Coincident(g197,g198)
    c: Coincident(g198,g199)
    c: Coincident(g199,g200)
    c: Coincident(g200,g201)
    c: Coincident(g201,g202)
    c: Coincident(g202,g203)
    c: Coincident(g203,g204)
    c: Coincident(g204,g205)
    c: Coincident(g205,g206)
    c: Coincident(g206,g207)
    c: Coincident(g207,g208)
    c: Coincident(g208,g209)
    c: Coincident(g209,g210)
    c: Coincident(g210,g211)
    c: Coincident(g211,g212)
    c: Coincident(g212,g213)
    c: Coincident(g213,g214)
    c: Coincident(g214,g215)
    c: Coincident(g215,g216)
    c: Coincident(g216,g217)
    c: Coincident(g217,g218)
    c: Coincident(g218,g219)
    c: Coincident(g219,g220)
    c: Coincident(g220,g221)
    c: Coincident(g221,g222)
    c: Coincident(g222,g223)
    c: Coincident(g223,g224)
    c: Coincident(g224,g225)
    c: Coincident(g225,g226)
    c: Coincident(g226,g227)
    c: Coincident(g227,g228)
    c: Coincident(g228,g229)
    c: Coincident(g229,g163)
    c: Coincident(g230,g231)
    c: Coincident(g231,g232)
    c: Coincident(g232,g233)
    c: Coincident(g233,g234)
    c: Coincident(g234,g235)
    c: Coincident(g235,g236)
    c: Coincident(g236,g230)
    c: Coincident(g237,g238)
    c: Coincident(g238,g239)
    c: Coincident(g239,g240)
    c: Coincident(g240,g241)
    c: Coincident(g241,g242)
    c: Coincident(g242,g243)
    c: Coincident(g243,g244)
    c: Coincident(g244,g245)
    c: Coincident(g245,g246)
    c: Coincident(g246,g247)
    c: Coincident(g247,g248)
    c: Coincident(g248,g249)
    c: Coincident(g249,g250)
    c: Coincident(g250,g251)
    c: Coincident(g251,g252)
    c: Coincident(g252,g253)
    c: Coincident(g253,g237)
    c: Coincident(g254,g255)
    c: Coincident(g255,g256)
    c: Coincident(g256,g257)
    c: Coincident(g257,g254)
    c: Coincident(g258,g259)
    c: Coincident(g259,g260)
    c: Coincident(g260,g258)
    c: Coincident(g261,g262)
    c: Coincident(g262,g263)
    c: Coincident(g263,g264)
    c: Coincident(g264,g265)
    c: Coincident(g265,g266)
    c: Coincident(g266,g267)
    c: Coincident(g267,g268)
    c: Coincident(g268,g269)
    c: Coincident(g269,g270)
    c: Coincident(g270,g271)
    c: Coincident(g271,g272)
    c: Coincident(g272,g273)
    c: Coincident(g273,g274)
    c: Coincident(g274,g275)
    c: Coincident(g275,g276)
    c: Coincident(g276,g277)
    c: Coincident(g277,g278)
    c: Coincident(g278,g279)
    c: Coincident(g279,g280)
    c: Coincident(g280,g281)
    c: Coincident(g281,g282)
    c: Coincident(g282,g283)
    c: Coincident(g283,g284)
    c: Coincident(g284,g285)
    c: Coincident(g285,g286)
    c: Coincident(g286,g287)
    c: Coincident(g287,g288)
    c: Coincident(g288,g261)
    c: Coincident(g289,g290)
    c: Coincident(g290,g291)
    c: Coincident(g291,g292)
    c: Coincident(g292,g293)
    c: Coincident(g293,g294)
    c: Coincident(g294,g295)
    c: Coincident(g295,g296)
    c: Coincident(g296,g297)
    c: Coincident(g297,g289)
    c: Coincident(g298,g299)
    c: Coincident(g299,g300)
    c: Coincident(g300,g298)
    c: Coincident(g301,g302)
    c: Coincident(g302,g303)
    c: Coincident(g303,g304)
    c: Coincident(g304,g305)
    c: Coincident(g305,g306)
    c: Coincident(g306,g307)
    c: Coincident(g307,g308)
    c: Coincident(g308,g301)
    c: Coincident(g309,g310)
    c: Coincident(g310,g311)
    c: Coincident(g311,g309)
    c: Coincident(g312,g313)
    c: Coincident(g313,g314)
    c: Coincident(g314,g312)
    c: Coincident(g315,g316)
    c: Coincident(g316,g317)
    c: Coincident(g317,g315)
    c: Coincident(g318,g319)
    c: Coincident(g319,g320)
    c: Coincident(g320,g318)
    c: Coincident(g321,g322)
    c: Coincident(g322,g323)
    c: Coincident(g323,g321)
    c: Coincident(g123,g123)
    c: Coincident(g254,g254)
    c: Coincident(g94,g94)
    c: Coincident(g163,g163)
    c: Coincident(g146,g146)
FEATURE [Sketcher::SketchObject] Sketch004  label="Empath-Sketch"
  ArcFitTolerance = 1e-06
  FullyConstrained = false
  MakeInternals = false
  sketch-geometry (137):
    g0: BSplineCurve PolesCount=4 KnotsCount=2 Degree=3 IsPeriodic=0
    g1: BSplineCurve PolesCount=4 KnotsCount=2 Degree=3 IsPeriodic=0
    g2: BSplineCurve PolesCount=4 KnotsCount=2 Degree=3 IsPeriodic=0
    g3: BSplineCurve PolesCount=4 KnotsCount=2 Degree=3 IsPeriodic=0
    g4: BSplineCurve PolesCount=4 KnotsCount=2 Degree=3 IsPeriodic=0
    g5: BSplineCurve PolesCount=4 KnotsCount=2 Degree=3 IsPeriodic=0
    g6: BSplineCurve PolesCount=4 KnotsCount=2 Degree=3 IsPeriodic=0
    g7: BSplineCurve PolesCount=4 KnotsCount=2 Degree=3 IsPeriodic=0
    g8: BSplineCurve PolesCount=4 KnotsCount=2 Degree=3 IsPeriodic=0
    g9: BSplineCurve PolesCount=4 KnotsCount=2 Degree=3 IsPeriodic=0
    g10: BSplineCurve PolesCount=4 KnotsCount=2 Degree=3 IsPeriodic=0
    g11: BSplineCurve PolesCount=2 KnotsCount=2 Degree=1 IsPeriodic=0
    g12: BSplineCurve PolesCount=2 KnotsCount=2 Degree=1 IsPeriodic=0
    g13: BSplineCurve PolesCount=4 KnotsCount=2 Degree=3 IsPeriodic=0
    g14: BSplineCurve PolesCount=4 KnotsCount=2 Degree=3 IsPeriodic=0
    g15: BSplineCurve PolesCount=4 KnotsCount=2 Degree=3 IsPeriodic=0
    g16: BSplineCurve PolesCount=4 KnotsCount=2 Degree=3 IsPeriodic=0
    g17: BSplineCurve PolesCount=4 KnotsCount=2 Degree=3 IsPeriodic=0
    g18: BSplineCurve PolesCount=4 KnotsCount=2 Degree=3 IsPeriodic=0
    g19: BSplineCurve PolesCount=4 KnotsCount=2 Degree=3 IsPeriodic=0
    g20: BSplineCurve PolesCount=4 KnotsCount=2 Degree=3 IsPeriodic=0
    g21: BSplineCurve PolesCount=4 KnotsCount=2 Degree=3 IsPeriodic=0
    g22: BSplineCurve PolesCount=4 KnotsCount=2 Degree=3 IsPeriodic=0
    g23: BSplineCurve PolesCount=4 KnotsCount=2 Degree=3 IsPeriodic=0
    g24: BSplineCurve PolesCount=4 KnotsCount=2 Degree=3 IsPeriodic=0
    g25: BSplineCurve PolesCount=4 KnotsCount=2 Degree=3 IsPeriodic=0
    g26: BSplineCurve PolesCount=2 KnotsCount=2 Degree=1 IsPeriodic=0
    g27: BSplineCurve PolesCount=2 KnotsCount=2 Degree=1 IsPeriodic=0
    g28: BSplineCurve PolesCount=4 KnotsCount=2 Degree=3 IsPeriodic=0
    g29: BSplineCurve PolesCount=4 KnotsCount=2 Degree=3 IsPeriodic=0
    g30: BSplineCurve PolesCount=4 KnotsCount=2 Degree=3 IsPeriodic=0
    g31: BSplineCurve PolesCount=4 KnotsCount=2 Degree=3 IsPeriodic=0
    g32: BSplineCurve PolesCount=4 KnotsCount=2 Degree=3 IsPeriodic=0
    g33: BSplineCurve PolesCount=4 KnotsCount=2 Degree=3 IsPeriodic=0
    g34: BSplineCurve PolesCount=4 KnotsCount=2 Degree=3 IsPeriodic=0
    g35: BSplineCurve PolesCount=4 KnotsCount=2 Degree=3 IsPeriodic=0
    g36: BSplineCurve PolesCount=4 KnotsCount=2 Degree=3 IsPeriodic=0
    g37: BSplineCurve PolesCount=4 KnotsCount=2 Degree=3 IsPeriodic=0
    g38: BSplineCurve PolesCount=4 KnotsCount=2 Degree=3 IsPeriodic=0
    g39: BSplineCurve PolesCount=4 KnotsCount=2 Degree=3 IsPeriodic=0
    g40: BSplineCurve PolesCount=4 KnotsCount=2 Degree=3 IsPeriodic=0
    g41: BSplineCurve PolesCount=2 KnotsCount=2 Degree=1 IsPeriodic=0
    g42: BSplineCurve PolesCount=2 KnotsCount=2 Degree=1 IsPeriodic=0
    g43: BSplineCurve PolesCount=2 KnotsCount=2 Degree=1 IsPeriodic=0
    g44: BSplineCurve PolesCount=4 KnotsCount=2 Degree=3 IsPeriodic=0
    g45: BSplineCurve PolesCount=4 KnotsCount=2 Degree=3 IsPeriodic=0
    g46: BSplineCurve PolesCount=4 KnotsCount=2 Degree=3 IsPeriodic=0
    g47: BSplineCurve PolesCount=4 KnotsCount=2 Degree=3 IsPeriodic=0
    g48: BSplineCurve PolesCount=4 KnotsCount=2 Degree=3 IsPeriodic=0
    g49: BSplineCurve PolesCount=4 KnotsCount=2 Degree=3 IsPeriodic=0
    g50: BSplineCurve PolesCount=4 KnotsCount=2 Degree=3 IsPeriodic=0
    g51: BSplineCurve PolesCount=4 KnotsCount=2 Degree=3 IsPeriodic=0
    g52: BSplineCurve PolesCount=4 KnotsCount=2 Degree=3 IsPeriodic=0
    g53: BSplineCurve PolesCount=4 KnotsCount=2 Degree=3 IsPeriodic=0
    g54: BSplineCurve PolesCount=4 KnotsCount=2 Degree=3 IsPeriodic=0
    g55: BSplineCurve PolesCount=4 KnotsCount=2 Degree=3 IsPeriodic=0
    g56: BSplineCurve PolesCount=4 KnotsCount=2 Degree=3 IsPeriodic=0
    g57: BSplineCurve PolesCount=4 KnotsCount=2 Degree=3 IsPeriodic=0
    g58: BSplineCurve PolesCount=4 KnotsCount=2 Degree=3 IsPeriodic=0
    g59: BSplineCurve PolesCount=4 KnotsCount=2 Degree=3 IsPeriodic=0
    g60: BSplineCurve PolesCount=4 KnotsCount=2 Degree=3 IsPeriodic=0
    g61: BSplineCurve PolesCount=2 KnotsCount=2 Degree=1 IsPeriodic=0
    g62: BSplineCurve PolesCount=2 KnotsCount=2 Degree=1 IsPeriodic=0
    g63: BSplineCurve PolesCount=4 KnotsCount=2 Degree=3 IsPeriodic=0
    g64: BSplineCurve PolesCount=4 KnotsCount=2 Degree=3 IsPeriodic=0
    g65: BSplineCurve PolesCount=4 KnotsCount=2 Degree=3 IsPeriodic=0
    g66: BSplineCurve PolesCount=4 KnotsCount=2 Degree=3 IsPeriodic=0
    g67: BSplineCurve PolesCount=4 KnotsCount=2 Degree=3 IsPeriodic=0
    g68: BSplineCurve PolesCount=4 KnotsCount=2 Degree=3 IsPeriodic=0
    g69: BSplineCurve PolesCount=4 KnotsCount=2 Degree=3 IsPeriodic=0
    g70: BSplineCurve PolesCount=4 KnotsCount=2 Degree=3 IsPeriodic=0
    g71: BSplineCurve PolesCount=4 KnotsCount=2 Degree=3 IsPeriodic=0
    g72: BSplineCurve PolesCount=2 KnotsCount=2 Degree=1 IsPeriodic=0
    g73: BSplineCurve PolesCount=2 KnotsCount=2 Degree=1 IsPeriodic=0
    g74: BSplineCurve PolesCount=4 KnotsCount=2 Degree=3 IsPeriodic=0
    g75: BSplineCurve PolesCount=4 KnotsCount=2 Degree=3 IsPeriodic=0
    g76: BSplineCurve PolesCount=4 KnotsCount=2 Degree=3 IsPeriodic=0
    g77: BSplineCurve PolesCount=4 KnotsCount=2 Degree=3 IsPeriodic=0
    g78: BSplineCurve PolesCount=4 KnotsCount=2 Degree=3 IsPeriodic=0
    g79: BSplineCurve PolesCount=4 KnotsCount=2 Degree=3 IsPeriodic=0
    g80: BSplineCurve PolesCount=4 KnotsCount=2 Degree=3 IsPeriodic=0
    g81: BSplineCurve PolesCount=4 KnotsCount=2 Degree=3 IsPeriodic=0
    g82: BSplineCurve PolesCount=4 KnotsCount=2 Degree=3 IsPeriodic=0
    g83: BSplineCurve PolesCount=4 KnotsCount=2 Degree=3 IsPeriodic=0
    g84: BSplineCurve PolesCount=4 KnotsCount=2 Degree=3 IsPeriodic=0
    g85: BSplineCurve PolesCount=4 KnotsCount=2 Degree=3 IsPeriodic=0
    g86: BSplineCurve PolesCount=4 KnotsCount=2 Degree=3 IsPeriodic=0
    g87: BSplineCurve PolesCount=4 KnotsCount=2 Degree=3 IsPeriodic=0
    g88: BSplineCurve PolesCount=4 KnotsCount=2 Degree=3 IsPeriodic=0
    g89: BSplineCurve PolesCount=4 KnotsCount=2 Degree=3 IsPeriodic=0
    g90: BSplineCurve PolesCount=4 KnotsCount=2 Degree=3 IsPeriodic=0
    g91: BSplineCurve PolesCount=4 KnotsCount=2 Degree=3 IsPeriodic=0
    g92: BSplineCurve PolesCount=4 KnotsCount=2 Degree=3 IsPeriodic=0
    g93: BSplineCurve PolesCount=4 KnotsCount=2 Degree=3 IsPeriodic=0
    g94: BSplineCurve PolesCount=4 KnotsCount=2 Degree=3 IsPeriodic=0
    g95: BSplineCurve PolesCount=4 KnotsCount=2 Degree=3 IsPeriodic=0
    g96: BSplineCurve PolesCount=4 KnotsCount=2 Degree=3 IsPeriodic=0
    g97: BSplineCurve PolesCount=4 KnotsCount=2 Degree=3 IsPeriodic=0
    g98: BSplineCurve PolesCount=4 KnotsCount=2 Degree=3 IsPeriodic=0
    g99: BSplineCurve PolesCount=4 KnotsCount=2 Degree=3 IsPeriodic=0
    g100: BSplineCurve PolesCount=2 KnotsCount=2 Degree=1 IsPeriodic=0
    g101: BSplineCurve PolesCount=2 KnotsCount=2 Degree=1 IsPeriodic=0
    g102: BSplineCurve PolesCount=2 KnotsCount=2 Degree=1 IsPeriodic=0
    g103: BSplineCurve PolesCount=4 KnotsCount=2 Degree=3 IsPeriodic=0
    g104: BSplineCurve PolesCount=4 KnotsCount=2 Degree=3 IsPeriodic=0
    g105: BSplineCurve PolesCount=4 KnotsCount=2 Degree=3 IsPeriodic=0
    g106: BSplineCurve PolesCount=4 KnotsCount=2 Degree=3 IsPeriodic=0
    g107: BSplineCurve PolesCount=4 KnotsCount=2 Degree=3 IsPeriodic=0
    g108: BSplineCurve PolesCount=4 KnotsCount=2 Degree=3 IsPeriodic=0
    g109: BSplineCurve PolesCount=4 KnotsCount=2 Degree=3 IsPeriodic=0
    g110: BSplineCurve PolesCount=4 KnotsCount=2 Degree=3 IsPeriodic=0
    g111: BSplineCurve PolesCount=4 KnotsCount=2 Degree=3 IsPeriodic=0
    g112: BSplineCurve PolesCount=4 KnotsCount=2 Degree=3 IsPeriodic=0
    g113: BSplineCurve PolesCount=4 KnotsCount=2 Degree=3 IsPeriodic=0
    g114: BSplineCurve PolesCount=2 KnotsCount=2 Degree=1 IsPeriodic=0
    g115: BSplineCurve PolesCount=2 KnotsCount=2 Degree=1 IsPeriodic=0
    g116: BSplineCurve PolesCount=4 KnotsCount=2 Degree=3 IsPeriodic=0
    g117: BSplineCurve PolesCount=4 KnotsCount=2 Degree=3 IsPeriodic=0
    g118: BSplineCurve PolesCount=4 KnotsCount=2 Degree=3 IsPeriodic=0
    g119: BSplineCurve PolesCount=4 KnotsCount=2 Degree=3 IsPeriodic=0
    g120: BSplineCurve PolesCount=4 KnotsCount=2 Degree=3 IsPeriodic=0
    g121: BSplineCurve PolesCount=4 KnotsCount=2 Degree=3 IsPeriodic=0
    g122: BSplineCurve PolesCount=4 KnotsCount=2 Degree=3 IsPeriodic=0
    g123: BSplineCurve PolesCount=4 KnotsCount=2 Degree=3 IsPeriodic=0
    g124: BSplineCurve PolesCount=4 KnotsCount=2 Degree=3 IsPeriodic=0
    g125: BSplineCurve PolesCount=4 KnotsCount=2 Degree=3 IsPeriodic=0
    g126: BSplineCurve PolesCount=4 KnotsCount=2 Degree=3 IsPeriodic=0
    g127: BSplineCurve PolesCount=4 KnotsCount=2 Degree=3 IsPeriodic=0
    g128: BSplineCurve PolesCount=4 KnotsCount=2 Degree=3 IsPeriodic=0
    g129: BSplineCurve PolesCount=4 KnotsCount=2 Degree=3 IsPeriodic=0
    g130: BSplineCurve PolesCount=4 KnotsCount=2 Degree=3 IsPeriodic=0
    g131: BSplineCurve PolesCount=4 KnotsCount=2 Degree=3 IsPeriodic=0
    g132: BSplineCurve PolesCount=4 KnotsCount=2 Degree=3 IsPeriodic=0
    g133: BSplineCurve PolesCount=4 KnotsCount=2 Degree=3 IsPeriodic=0
    g134: BSplineCurve PolesCount=4 KnotsCount=2 Degree=3 IsPeriodic=0
    g135: BSplineCurve PolesCount=4 KnotsCount=2 Degree=3 IsPeriodic=0
    g136: BSplineCurve PolesCount=4 KnotsCount=2 Degree=3 IsPeriodic=0
  constraints (139):
    c: Coincident(g0,g1)
    c: Coincident(g1,g2)
    c: Coincident(g2,g3)
    c: Coincident(g3,g4)
    c: Coincident(g4,g5)
    c: Coincident(g5,g6)
    c: Coincident(g6,g7)
    c: Coincident(g7,g8)
    c: Coincident(g8,g9)
    c: Coincident(g9,g10)
    c: Coincident(g10,g11)
    c: Coincident(g11,g12)
    c: Coincident(g12,g13)
    c: Coincident(g13,g14)
    c: Coincident(g14,g15)
    c: Coincident(g15,g16)
    c: Coincident(g16,g17)
    c: Coincident(g17,g18)
    c: Coincident(g18,g19)
    c: Coincident(g19,g20)
    c: Coincident(g20,g21)
    c: Coincident(g21,g22)
    c: Coincident(g22,g23)
    c: Coincident(g23,g24)
    c: Coincident(g24,g25)
    c: Coincident(g25,g26)
    c: Coincident(g26,g27)
    c: Coincident(g27,g28)
    c: Coincident(g28,g29)
    c: Coincident(g29,g30)
    c: Coincident(g30,g31)
    c: Coincident(g31,g32)
    c: Coincident(g32,g33)
    c: Coincident(g33,g34)
    c: Coincident(g34,g35)
    c: Coincident(g35,g36)
    c: Coincident(g36,g37)
    c: Coincident(g37,g38)
    c: Coincident(g38,g39)
    c: Coincident(g39,g40)
    c: Coincident(g40,g41)
    c: Coincident(g41,g42)
    c: Coincident(g42,g0)
    c: Coincident(g43,g44)
    c: Coincident(g44,g45)
    c: Coincident(g45,g46)
    c: Coincident(g46,g47)
    c: Coincident(g47,g48)
    c: Coincident(g48,g49)
    c: Coincident(g49,g50)
    c: Coincident(g50,g51)
    c: Coincident(g51,g52)
    c: Coincident(g52,g53)
    c: Coincident(g53,g54)
    c: Coincident(g54,g55)
    c: Coincident(g55,g56)
    c: Coincident(g56,g57)
    c: Coincident(g57,g58)
    c: Coincident(g58,g43)
    c: Coincident(g59,g60)
    c: Coincident(g60,g61)
    c: Coincident(g61,g62)
    c: Coincident(g62,g63)
    c: Coincident(g63,g64)
    c: Coincident(g64,g65)
    c: Coincident(g65,g66)
    c: Coincident(g66,g67)
    c: Coincident(g67,g68)
    c: Coincident(g68,g69)
    c: Coincident(g69,g70)
    c: Coincident(g70,g71)
    c: Coincident(g71,g72)
    c: Coincident(g72,g73)
    c: Coincident(g73,g74)
    c: Coincident(g74,g75)
    c: Coincident(g75,g76)
    c: Coincident(g76,g77)
    c: Coincident(g77,g78)
    c: Coincident(g78,g79)
    c: Coincident(g79,g80)
    c: Coincident(g80,g81)
    c: Coincident(g81,g82)
    c: Coincident(g82,g83)
    c: Coincident(g83,g84)
    c: Coincident(g84,g85)
    c: Coincident(g85,g86)
    c: Coincident(g86,g87)
    c: Coincident(g87,g88)
    c: Coincident(g88,g89)
    c: Coincident(g89,g90)
    c: Coincident(g90,g91)
    c: Coincident(g91,g92)
    c: Coincident(g92,g93)
    c: Coincident(g93,g94)
    c: Coincident(g94,g95)
    c: Coincident(g95,g96)
    c: Coincident(g96,g97)
    c: Coincident(g97,g98)
    c: Coincident(g98,g99)
    c: Coincident(g99,g100)
    c: Coincident(g100,g101)
    c: Coincident(g101,g59)
    c: Coincident(g102,g103)
    c: Coincident(g103,g104)
    c: Coincident(g104,g105)
    c: Coincident(g105,g106)
    c: Coincident(g106,g107)
    c: Coincident(g107,g108)
    c: Coincident(g108,g109)
    c: Coincident(g109,g110)
    c: Coincident(g110,g111)
    c: Coincident(g111,g112)
    c: Coincident(g112,g113)
    c: Coincident(g113,g114)
    c: Coincident(g114,g115)
    c: Coincident(g115,g116)
    c: Coincident(g116,g117)
    c: Coincident(g117,g118)
    c: Coincident(g118,g119)
    c: Coincident(g119,g120)
    c: Coincident(g120,g121)
    c: Coincident(g121,g122)
    c: Coincident(g122,g123)
    c: Coincident(g123,g124)
    c: Coincident(g124,g125)
    c: Coincident(g125,g126)
    c: Coincident(g126,g127)
    c: Coincident(g127,g128)
    c: Coincident(g128,g129)
    c: Coincident(g129,g130)
    c: Coincident(g130,g131)
    c: Coincident(g131,g132)
    c: Coincident(g132,g133)
    c: Coincident(g133,g134)
    c: Coincident(g134,g135)
    c: Coincident(g135,g136)
    c: Coincident(g136,g102)
    c: Coincident(g43,g43)
    c: Coincident(g102,g102)
FEATURE [Sketcher::SketchObject] Sketch005  label="Fortune_Teller-Sketch"
  ArcFitTolerance = 1e-06
  FullyConstrained = false
  MakeInternals = false
  sketch-geometry (145):
    g0: BSplineCurve PolesCount=4 KnotsCount=2 Degree=3 IsPeriodic=0
    g1: BSplineCurve PolesCount=4 KnotsCount=2 Degree=3 IsPeriodic=0
    g2: BSplineCurve PolesCount=4 KnotsCount=2 Degree=3 IsPeriodic=0
    g3: BSplineCurve PolesCount=4 KnotsCount=2 Degree=3 IsPeriodic=0
    g4: BSplineCurve PolesCount=4 KnotsCount=2 Degree=3 IsPeriodic=0
    g5: BSplineCurve PolesCount=4 KnotsCount=2 Degree=3 IsPeriodic=0
    g6: BSplineCurve PolesCount=4 KnotsCount=2 Degree=3 IsPeriodic=0
    g7: BSplineCurve PolesCount=4 KnotsCount=2 Degree=3 IsPeriodic=0
    g8: BSplineCurve PolesCount=4 KnotsCount=2 Degree=3 IsPeriodic=0
    g9: BSplineCurve PolesCount=4 KnotsCount=2 Degree=3 IsPeriodic=0
    g10: BSplineCurve PolesCount=4 KnotsCount=2 Degree=3 IsPeriodic=0
    g11: BSplineCurve PolesCount=4 KnotsCount=2 Degree=3 IsPeriodic=0
    g12: BSplineCurve PolesCount=4 KnotsCount=2 Degree=3 IsPeriodic=0
    g13: BSplineCurve PolesCount=4 KnotsCount=2 Degree=3 IsPeriodic=0
    g14: BSplineCurve PolesCount=4 KnotsCount=2 Degree=3 IsPeriodic=0
    g15: BSplineCurve PolesCount=4 KnotsCount=2 Degree=3 IsPeriodic=0
    g16: BSplineCurve PolesCount=4 KnotsCount=2 Degree=3 IsPeriodic=0
    g17: BSplineCurve PolesCount=4 KnotsCount=2 Degree=3 IsPeriodic=0
    g18: BSplineCurve PolesCount=4 KnotsCount=2 Degree=3 IsPeriodic=0
    g19: BSplineCurve PolesCount=4 KnotsCount=2 Degree=3 IsPeriodic=0
    g20: BSplineCurve PolesCount=4 KnotsCount=2 Degree=3 IsPeriodic=0
    g21: BSplineCurve PolesCount=4 KnotsCount=2 Degree=3 IsPeriodic=0
    g22: BSplineCurve PolesCount=4 KnotsCount=2 Degree=3 IsPeriodic=0
    g23: BSplineCurve PolesCount=4 KnotsCount=2 Degree=3 IsPeriodic=0
    g24: BSplineCurve PolesCount=4 KnotsCount=2 Degree=3 IsPeriodic=0
    g25: BSplineCurve PolesCount=4 KnotsCount=2 Degree=3 IsPeriodic=0
    g26: BSplineCurve PolesCount=2 KnotsCount=2 Degree=1 IsPeriodic=0
    g27: BSplineCurve PolesCount=2 KnotsCount=2 Degree=1 IsPeriodic=0
    g28: BSplineCurve PolesCount=4 KnotsCount=2 Degree=3 IsPeriodic=0
    g29: BSplineCurve PolesCount=4 KnotsCount=2 Degree=3 IsPeriodic=0
    g30: BSplineCurve PolesCount=4 KnotsCount=2 Degree=3 IsPeriodic=0
    g31: BSplineCurve PolesCount=4 KnotsCount=2 Degree=3 IsPeriodic=0
    g32: BSplineCurve PolesCount=4 KnotsCount=2 Degree=3 IsPeriodic=0
    g33: BSplineCurve PolesCount=4 KnotsCount=2 Degree=3 IsPeriodic=0
    g34: BSplineCurve PolesCount=2 KnotsCount=2 Degree=1 IsPeriodic=0
    g35: BSplineCurve PolesCount=2 KnotsCount=2 Degree=1 IsPeriodic=0
    g36: BSplineCurve PolesCount=4 KnotsCount=2 Degree=3 IsPeriodic=0
    g37: BSplineCurve PolesCount=2 KnotsCount=2 Degree=1 IsPeriodic=0
    g38: BSplineCurve PolesCount=2 KnotsCount=2 Degree=1 IsPeriodic=0
    g39: BSplineCurve PolesCount=4 KnotsCount=2 Degree=3 IsPeriodic=0
    g40: BSplineCurve PolesCount=4 KnotsCount=2 Degree=3 IsPeriodic=0
    g41: BSplineCurve PolesCount=4 KnotsCount=2 Degree=3 IsPeriodic=0
    g42: BSplineCurve PolesCount=4 KnotsCount=2 Degree=3 IsPeriodic=0
    g43: BSplineCurve PolesCount=4 KnotsCount=2 Degree=3 IsPeriodic=0
    g44: BSplineCurve PolesCount=4 KnotsCount=2 Degree=3 IsPeriodic=0
    g45: BSplineCurve PolesCount=4 KnotsCount=2 Degree=3 IsPeriodic=0
    g46: BSplineCurve PolesCount=4 KnotsCount=2 Degree=3 IsPeriodic=0
    g47: BSplineCurve PolesCount=4 KnotsCount=2 Degree=3 IsPeriodic=0
    g48: BSplineCurve PolesCount=4 KnotsCount=2 Degree=3 IsPeriodic=0
    g49: BSplineCurve PolesCount=4 KnotsCount=2 Degree=3 IsPeriodic=0
    g50: BSplineCurve PolesCount=4 KnotsCount=2 Degree=3 IsPeriodic=0
    g51: BSplineCurve PolesCount=4 KnotsCount=2 Degree=3 IsPeriodic=0
    g52: BSplineCurve PolesCount=4 KnotsCount=2 Degree=3 IsPeriodic=0
    g53: BSplineCurve PolesCount=4 KnotsCount=2 Degree=3 IsPeriodic=0
    g54: BSplineCurve PolesCount=4 KnotsCount=2 Degree=3 IsPeriodic=0
    g55: BSplineCurve PolesCount=4 KnotsCount=2 Degree=3 IsPeriodic=0
    g56: BSplineCurve PolesCount=4 KnotsCount=2 Degree=3 IsPeriodic=0
    g57: BSplineCurve PolesCount=4 KnotsCount=2 Degree=3 IsPeriodic=0
    g58: BSplineCurve PolesCount=4 KnotsCount=2 Degree=3 IsPeriodic=0
    g59: BSplineCurve PolesCount=4 KnotsCount=2 Degree=3 IsPeriodic=0
    g60: BSplineCurve PolesCount=4 KnotsCount=2 Degree=3 IsPeriodic=0
    g61: BSplineCurve PolesCount=4 KnotsCount=2 Degree=3 IsPeriodic=0
    g62: BSplineCurve PolesCount=4 KnotsCount=2 Degree=3 IsPeriodic=0
    g63: BSplineCurve PolesCount=4 KnotsCount=2 Degree=3 IsPeriodic=0
    g64: BSplineCurve PolesCount=4 KnotsCount=2 Degree=3 IsPeriodic=0
    g65: BSplineCurve PolesCount=4 KnotsCount=2 Degree=3 IsPeriodic=0
    g66: BSplineCurve PolesCount=4 KnotsCount=2 Degree=3 IsPeriodic=0
    g67: BSplineCurve PolesCount=4 KnotsCount=2 Degree=3 IsPeriodic=0
    g68: BSplineCurve PolesCount=4 KnotsCount=2 Degree=3 IsPeriodic=0
    g69: BSplineCurve PolesCount=4 KnotsCount=2 Degree=3 IsPeriodic=0
    g70: BSplineCurve PolesCount=2 KnotsCount=2 Degree=1 IsPeriodic=0
    g71: BSplineCurve PolesCount=4 KnotsCount=2 Degree=3 IsPeriodic=0
    g72: BSplineCurve PolesCount=4 KnotsCount=2 Degree=3 IsPeriodic=0
    g73: BSplineCurve PolesCount=4 KnotsCount=2 Degree=3 IsPeriodic=0
    g74: BSplineCurve PolesCount=4 KnotsCount=2 Degree=3 IsPeriodic=0
    g75: BSplineCurve PolesCount=4 KnotsCount=2 Degree=3 IsPeriodic=0
    g76: BSplineCurve PolesCount=4 KnotsCount=2 Degree=3 IsPeriodic=0
    g77: BSplineCurve PolesCount=4 KnotsCount=2 Degree=3 IsPeriodic=0
    g78: BSplineCurve PolesCount=4 KnotsCount=2 Degree=3 IsPeriodic=0
    g79: BSplineCurve PolesCount=4 KnotsCount=2 Degree=3 IsPeriodic=0
    g80: BSplineCurve PolesCount=2 KnotsCount=2 Degree=1 IsPeriodic=0
    g81: BSplineCurve PolesCount=4 KnotsCount=2 Degree=3 IsPeriodic=0
    g82: BSplineCurve PolesCount=4 KnotsCount=2 Degree=3 IsPeriodic=0
    g83: BSplineCurve PolesCount=4 KnotsCount=2 Degree=3 IsPeriodic=0
    g84: BSplineCurve PolesCount=4 KnotsCount=2 Degree=3 IsPeriodic=0
    g85: BSplineCurve PolesCount=4 KnotsCount=2 Degree=3 IsPeriodic=0
    g86: BSplineCurve PolesCount=4 KnotsCount=2 Degree=3 IsPeriodic=0
    g87: BSplineCurve PolesCount=4 KnotsCount=2 Degree=3 IsPeriodic=0
    g88: BSplineCurve PolesCount=4 KnotsCount=2 Degree=3 IsPeriodic=0
    g89: BSplineCurve PolesCount=4 KnotsCount=2 Degree=3 IsPeriodic=0
    g90: BSplineCurve PolesCount=4 KnotsCount=2 Degree=3 IsPeriodic=0
    g91: BSplineCurve PolesCount=4 KnotsCount=2 Degree=3 IsPeriodic=0
    g92: BSplineCurve PolesCount=2 KnotsCount=2 Degree=1 IsPeriodic=0
    g93: BSplineCurve PolesCount=2 KnotsCount=2 Degree=1 IsPeriodic=0
    g94: BSplineCurve PolesCount=4 KnotsCount=2 Degree=3 IsPeriodic=0
    g95: BSplineCurve PolesCount=4 KnotsCount=2 Degree=3 IsPeriodic=0
    g96: BSplineCurve PolesCount=4 KnotsCount=2 Degree=3 IsPeriodic=0
    g97: BSplineCurve PolesCount=4 KnotsCount=2 Degree=3 IsPeriodic=0
    g98: BSplineCurve PolesCount=4 KnotsCount=2 Degree=3 IsPeriodic=0
    g99: BSplineCurve PolesCount=4 KnotsCount=2 Degree=3 IsPeriodic=0
    g100: BSplineCurve PolesCount=4 KnotsCount=2 Degree=3 IsPeriodic=0
    g101: BSplineCurve PolesCount=4 KnotsCount=2 Degree=3 IsPeriodic=0
    g102: BSplineCurve PolesCount=4 KnotsCount=2 Degree=3 IsPeriodic=0
    g103: BSplineCurve PolesCount=4 KnotsCount=2 Degree=3 IsPeriodic=0
    g104: BSplineCurve PolesCount=4 KnotsCount=2 Degree=3 IsPeriodic=0
    g105: BSplineCurve PolesCount=4 KnotsCount=2 Degree=3 IsPeriodic=0
    g106: BSplineCurve PolesCount=4 KnotsCount=2 Degree=3 IsPeriodic=0
    g107: BSplineCurve PolesCount=4 KnotsCount=2 Degree=3 IsPeriodic=0
    g108: BSplineCurve PolesCount=4 KnotsCount=2 Degree=3 IsPeriodic=0
    g109: BSplineCurve PolesCount=4 KnotsCount=2 Degree=3 IsPeriodic=0
    g110: BSplineCurve PolesCount=4 KnotsCount=2 Degree=3 IsPeriodic=0
    g111: BSplineCurve PolesCount=4 KnotsCount=2 Degree=3 IsPeriodic=0
    g112: BSplineCurve PolesCount=4 KnotsCount=2 Degree=3 IsPeriodic=0
    g113: BSplineCurve PolesCount=4 KnotsCount=2 Degree=3 IsPeriodic=0
    g114: BSplineCurve PolesCount=4 KnotsCount=2 Degree=3 IsPeriodic=0
    g115: BSplineCurve PolesCount=4 KnotsCount=2 Degree=3 IsPeriodic=0
    g116: BSplineCurve PolesCount=4 KnotsCount=2 Degree=3 IsPeriodic=0
    g117: BSplineCurve PolesCount=4 KnotsCount=2 Degree=3 IsPeriodic=0
    g118: BSplineCurve PolesCount=4 KnotsCount=2 Degree=3 IsPeriodic=0
    g119: BSplineCurve PolesCount=4 KnotsCount=2 Degree=3 IsPeriodic=0
    g120: BSplineCurve PolesCount=4 KnotsCount=2 Degree=3 IsPeriodic=0
    g121: BSplineCurve PolesCount=4 KnotsCount=2 Degree=3 IsPeriodic=0
    g122: BSplineCurve PolesCount=4 KnotsCount=2 Degree=3 IsPeriodic=0
    g123: BSplineCurve PolesCount=4 KnotsCount=2 Degree=3 IsPeriodic=0
    g124: BSplineCurve PolesCount=4 KnotsCount=2 Degree=3 IsPeriodic=0
    g125: BSplineCurve PolesCount=4 KnotsCount=2 Degree=3 IsPeriodic=0
    g126: BSplineCurve PolesCount=4 KnotsCount=2 Degree=3 IsPeriodic=0
    g127: BSplineCurve PolesCount=4 KnotsCount=2 Degree=3 IsPeriodic=0
    g128: BSplineCurve PolesCount=4 KnotsCount=2 Degree=3 IsPeriodic=0
    g129: BSplineCurve PolesCount=4 KnotsCount=2 Degree=3 IsPeriodic=0
    g130: BSplineCurve PolesCount=4 KnotsCount=2 Degree=3 IsPeriodic=0
    g131: BSplineCurve PolesCount=2 KnotsCount=2 Degree=1 IsPeriodic=0
    g132: BSplineCurve PolesCount=4 KnotsCount=2 Degree=3 IsPeriodic=0
    g133: BSplineCurve PolesCount=4 KnotsCount=2 Degree=3 IsPeriodic=0
    g134: BSplineCurve PolesCount=4 KnotsCount=2 Degree=3 IsPeriodic=0
    g135: BSplineCurve PolesCount=4 KnotsCount=2 Degree=3 IsPeriodic=0
    g136: BSplineCurve PolesCount=4 KnotsCount=2 Degree=3 IsPeriodic=0
    g137: BSplineCurve PolesCount=4 KnotsCount=2 Degree=3 IsPeriodic=0
    g138: BSplineCurve PolesCount=4 KnotsCount=2 Degree=3 IsPeriodic=0
    g139: BSplineCurve PolesCount=2 KnotsCount=2 Degree=1 IsPeriodic=0
    g140: BSplineCurve PolesCount=4 KnotsCount=2 Degree=3 IsPeriodic=0
    g141: BSplineCurve PolesCount=4 KnotsCount=2 Degree=3 IsPeriodic=0
    g142: BSplineCurve PolesCount=4 KnotsCount=2 Degree=3 IsPeriodic=0
    g143: BSplineCurve PolesCount=4 KnotsCount=2 Degree=3 IsPeriodic=0
    g144: BSplineCurve PolesCount=2 KnotsCount=2 Degree=1 IsPeriodic=0
  constraints (148):
    c: Coincident(g0,g1)
    c: Coincident(g1,g2)
    c: Coincident(g2,g3)
    c: Coincident(g3,g4)
    c: Coincident(g4,g5)
    c: Coincident(g5,g6)
    c: Coincident(g6,g7)
    c: Coincident(g7,g8)
    c: Coincident(g8,g9)
    c: Coincident(g9,g10)
    c: Coincident(g10,g11)
    c: Coincident(g11,g12)
    c: Coincident(g12,g13)
    c: Coincident(g13,g14)
    c: Coincident(g14,g15)
    c: Coincident(g15,g16)
    c: Coincident(g16,g17)
    c: Coincident(g17,g18)
    c: Coincident(g18,g19)
    c: Coincident(g19,g20)
    c: Coincident(g20,g21)
    c: Coincident(g21,g22)
    c: Coincident(g22,g23)
    c: Coincident(g23,g24)
    c: Coincident(g24,g25)
    c: Coincident(g25,g26)
    c: Coincident(g26,g27)
    c: Coincident(g27,g28)
    c: Coincident(g28,g29)
    c: Coincident(g29,g30)
    c: Coincident(g30,g31)
    c: Coincident(g31,g32)
    c: Coincident(g32,g33)
    c: Coincident(g33,g34)
    c: Coincident(g34,g35)
    c: Coincident(g35,g36)
    c: Coincident(g36,g37)
    c: Coincident(g37,g38)
    c: Coincident(g38,g39)
    c: Coincident(g39,g0)
    c: Coincident(g40,g41)
    c: Coincident(g41,g42)
    c: Coincident(g42,g43)
    c: Coincident(g43,g44)
    c: Coincident(g44,g40)
    c: Coincident(g45,g46)
    c: Coincident(g46,g47)
    c: Coincident(g47,g48)
    c: Coincident(g48,g45)
    c: Coincident(g49,g50)
    c: Coincident(g50,g51)
    c: Coincident(g51,g52)
    c: Coincident(g52,g49)
    c: Coincident(g53,g54)
    c: Coincident(g54,g55)
    c: Coincident(g55,g56)
    c: Coincident(g56,g57)
    c: Coincident(g57,g53)
    c: Coincident(g58,g59)
    c: Coincident(g59,g60)
    c: Coincident(g60,g61)
    c: Coincident(g61,g62)
    c: Coincident(g62,g63)
    c: Coincident(g63,g64)
    c: Coincident(g64,g58)
    c: Coincident(g65,g66)
    c: Coincident(g66,g67)
    c: Coincident(g67,g68)
    c: Coincident(g68,g69)
    c: Coincident(g69,g65)
    c: Coincident(g70,g71)
    c: Coincident(g71,g72)
    c: Coincident(g72,g73)
    c: Coincident(g73,g70)
    c: Coincident(g74,g75)
    c: Coincident(g75,g76)
    c: Coincident(g76,g74)
    c: Coincident(g77,g78)
    c: Coincident(g78,g79)
    c: Coincident(g79,g77)
    c: Coincident(g80,g81)
    c: Coincident(g81,g82)
    c: Coincident(g82,g83)
    c: Coincident(g83,g80)
    c: Coincident(g84,g85)
    c: Coincident(g85,g86)
    c: Coincident(g86,g84)
    c: Coincident(g87,g88)
    c: Coincident(g88,g89)
    c: Coincident(g89,g87)
    c: Coincident(g90,g91)
    c: Coincident(g91,g92)
    c: Coincident(g92,g93)
    c: Coincident(g93,g94)
    c: Coincident(g94,g95)
    c: Coincident(g95,g90)
    c: Coincident(g96,g97)
    c: Coincident(g97,g98)
    c: Coincident(g98,g99)
    c: Coincident(g99,g96)
    c: Coincident(g100,g101)
    c: Coincident(g101,g102)
    c: Coincident(g102,g100)
    c: Coincident(g103,g104)
    c: Coincident(g104,g105)
    c: Coincident(g105,g106)
    c: Coincident(g106,g103)
    c: Coincident(g107,g108)
    c: Coincident(g108,g109)
    c: Coincident(g109,g110)
    c: Coincident(g110,g107)
    c: Coincident(g111,g112)
    c: Coincident(g112,g113)
    c: Coincident(g113,g111)
    c: Coincident(g114,g115)
    c: Coincident(g115,g116)
    c: Coincident(g116,g117)
    c: Coincident(g117,g118)
    c: Coincident(g118,g119)
    c: Coincident(g119,g120)
    c: Coincident(g120,g121)
    c: Coincident(g121,g122)
    c: Coincident(g122,g123)
    c: Coincident(g123,g124)
    c: Coincident(g124,g114)
    c: Coincident(g125,g126)
    c: Coincident(g126,g127)
    c: Coincident(g127,g128)
    c: Coincident(g128,g129)
    c: Coincident(g129,g125)
    c: Coincident(g130,g131)
    c: Coincident(g131,g132)
    c: Coincident(g132,g133)
    c: Coincident(g133,g134)
    c: Coincident(g134,g135)
    c: Coincident(g135,g136)
    c: Coincident(g136,g137)
    c: Coincident(g137,g138)
    c: Coincident(g138,g130)
    c: Coincident(g139,g140)
    c: Coincident(g140,g141)
    c: Coincident(g141,g142)
    c: Coincident(g142,g143)
    c: Coincident(g143,g144)
    c: Coincident(g144,g139)
    c: Coincident(g130,g131)
    c: Coincident(g70,g70)
    c: Coincident(g80,g80)
FEATURE [Sketcher::SketchObject] Sketch006  label="Imp-Sketch"
  ArcFitTolerance = 1e-06
  FullyConstrained = false
  MakeInternals = false
  sketch-geometry (85):
    g0: BSplineCurve PolesCount=4 KnotsCount=2 Degree=3 IsPeriodic=0
    g1: BSplineCurve PolesCount=4 KnotsCount=2 Degree=3 IsPeriodic=0
    g2: BSplineCurve PolesCount=4 KnotsCount=2 Degree=3 IsPeriodic=0
    g3: BSplineCurve PolesCount=4 KnotsCount=2 Degree=3 IsPeriodic=0
    g4: BSplineCurve PolesCount=4 KnotsCount=2 Degree=3 IsPeriodic=0
    g5: BSplineCurve PolesCount=4 KnotsCount=2 Degree=3 IsPeriodic=0
    g6: BSplineCurve PolesCount=4 KnotsCount=2 Degree=3 IsPeriodic=0
    g7: BSplineCurve PolesCount=4 KnotsCount=2 Degree=3 IsPeriodic=0
    g8: BSplineCurve PolesCount=4 KnotsCount=2 Degree=3 IsPeriodic=0
    g9: BSplineCurve PolesCount=4 KnotsCount=2 Degree=3 IsPeriodic=0
    g10: BSplineCurve PolesCount=4 KnotsCount=2 Degree=3 IsPeriodic=0
    g11: BSplineCurve PolesCount=4 KnotsCount=2 Degree=3 IsPeriodic=0
    g12: BSplineCurve PolesCount=4 KnotsCount=2 Degree=3 IsPeriodic=0
    g13: BSplineCurve PolesCount=4 KnotsCount=2 Degree=3 IsPeriodic=0
    g14: BSplineCurve PolesCount=2 KnotsCount=2 Degree=1 IsPeriodic=0
    g15: BSplineCurve PolesCount=2 KnotsCount=2 Degree=1 IsPeriodic=0
    g16: BSplineCurve PolesCount=4 KnotsCount=2 Degree=3 IsPeriodic=0
    g17: BSplineCurve PolesCount=2 KnotsCount=2 Degree=1 IsPeriodic=0
    g18: BSplineCurve PolesCount=2 KnotsCount=2 Degree=1 IsPeriodic=0
    g19: BSplineCurve PolesCount=4 KnotsCount=2 Degree=3 IsPeriodic=0
    g20: BSplineCurve PolesCount=4 KnotsCount=2 Degree=3 IsPeriodic=0
    g21: BSplineCurve PolesCount=2 KnotsCount=2 Degree=1 IsPeriodic=0
    g22: BSplineCurve PolesCount=2 KnotsCount=2 Degree=1 IsPeriodic=0
    g23: BSplineCurve PolesCount=4 KnotsCount=2 Degree=3 IsPeriodic=0
    g24: BSplineCurve PolesCount=4 KnotsCount=2 Degree=3 IsPeriodic=0
    g25: BSplineCurve PolesCount=4 KnotsCount=2 Degree=3 IsPeriodic=0
    g26: BSplineCurve PolesCount=4 KnotsCount=2 Degree=3 IsPeriodic=0
    g27: BSplineCurve PolesCount=4 KnotsCount=2 Degree=3 IsPeriodic=0
    g28: BSplineCurve PolesCount=4 KnotsCount=2 Degree=3 IsPeriodic=0
    g29: BSplineCurve PolesCount=4 KnotsCount=2 Degree=3 IsPeriodic=0
    g30: BSplineCurve PolesCount=4 KnotsCount=2 Degree=3 IsPeriodic=0
    g31: BSplineCurve PolesCount=4 KnotsCount=2 Degree=3 IsPeriodic=0
    g32: BSplineCurve PolesCount=2 KnotsCount=2 Degree=1 IsPeriodic=0
    g33: BSplineCurve PolesCount=2 KnotsCount=2 Degree=1 IsPeriodic=0
    g34: BSplineCurve PolesCount=2 KnotsCount=2 Degree=1 IsPeriodic=0
    g35: BSplineCurve PolesCount=2 KnotsCount=2 Degree=1 IsPeriodic=0
    g36: BSplineCurve PolesCount=4 KnotsCount=2 Degree=3 IsPeriodic=0
    g37: BSplineCurve PolesCount=4 KnotsCount=2 Degree=3 IsPeriodic=0
    g38: BSplineCurve PolesCount=4 KnotsCount=2 Degree=3 IsPeriodic=0
    g39: BSplineCurve PolesCount=4 KnotsCount=2 Degree=3 IsPeriodic=0
    g40: BSplineCurve PolesCount=4 KnotsCount=2 Degree=3 IsPeriodic=0
    g41: BSplineCurve PolesCount=2 KnotsCount=2 Degree=1 IsPeriodic=0
    g42: BSplineCurve PolesCount=2 KnotsCount=2 Degree=1 IsPeriodic=0
    g43: BSplineCurve PolesCount=4 KnotsCount=2 Degree=3 IsPeriodic=0
    g44: BSplineCurve PolesCount=4 KnotsCount=2 Degree=3 IsPeriodic=0
    g45: BSplineCurve PolesCount=4 KnotsCount=2 Degree=3 IsPeriodic=0
    g46: BSplineCurve PolesCount=4 KnotsCount=2 Degree=3 IsPeriodic=0
    g47: BSplineCurve PolesCount=2 KnotsCount=2 Degree=1 IsPeriodic=0
    g48: BSplineCurve PolesCount=2 KnotsCount=2 Degree=1 IsPeriodic=0
    g49: BSplineCurve PolesCount=2 KnotsCount=2 Degree=1 IsPeriodic=0
    g50: BSplineCurve PolesCount=2 KnotsCount=2 Degree=1 IsPeriodic=0
    g51: BSplineCurve PolesCount=4 KnotsCount=2 Degree=3 IsPeriodic=0
    g52: BSplineCurve PolesCount=4 KnotsCount=2 Degree=3 IsPeriodic=0
    g53: BSplineCurve PolesCount=4 KnotsCount=2 Degree=3 IsPeriodic=0
    g54: BSplineCurve PolesCount=4 KnotsCount=2 Degree=3 IsPeriodic=0
    g55: BSplineCurve PolesCount=4 KnotsCount=2 Degree=3 IsPeriodic=0
    g56: BSplineCurve PolesCount=2 KnotsCount=2 Degree=1 IsPeriodic=0
    g57: BSplineCurve PolesCount=2 KnotsCount=2 Degree=1 IsPeriodic=0
    g58: BSplineCurve PolesCount=2 KnotsCount=2 Degree=1 IsPeriodic=0
    g59: BSplineCurve PolesCount=2 KnotsCount=2 Degree=1 IsPeriodic=0
    g60: BSplineCurve PolesCount=4 KnotsCount=2 Degree=3 IsPeriodic=0
    g61: BSplineCurve PolesCount=4 KnotsCount=2 Degree=3 IsPeriodic=0
    g62: BSplineCurve PolesCount=2 KnotsCount=2 Degree=1 IsPeriodic=0
    g63: BSplineCurve PolesCount=4 KnotsCount=2 Degree=3 IsPeriodic=0
    g64: BSplineCurve PolesCount=4 KnotsCount=2 Degree=3 IsPeriodic=0
    g65: BSplineCurve PolesCount=4 KnotsCount=2 Degree=3 IsPeriodic=0
    g66: BSplineCurve PolesCount=4 KnotsCount=2 Degree=3 IsPeriodic=0
    g67: BSplineCurve PolesCount=4 KnotsCount=2 Degree=3 IsPeriodic=0
    g68: BSplineCurve PolesCount=4 KnotsCount=2 Degree=3 IsPeriodic=0
    g69: BSplineCurve PolesCount=4 KnotsCount=2 Degree=3 IsPeriodic=0
    g70: BSplineCurve PolesCount=2 KnotsCount=2 Degree=1 IsPeriodic=0
    g71: BSplineCurve PolesCount=4 KnotsCount=2 Degree=3 IsPeriodic=0
    g72: BSplineCurve PolesCount=4 KnotsCount=2 Degree=3 IsPeriodic=0
    g73: BSplineCurve PolesCount=4 KnotsCount=2 Degree=3 IsPeriodic=0
    g74: BSplineCurve PolesCount=4 KnotsCount=2 Degree=3 IsPeriodic=0
    g75: BSplineCurve PolesCount=4 KnotsCount=2 Degree=3 IsPeriodic=0
    g76: BSplineCurve PolesCount=4 KnotsCount=2 Degree=3 IsPeriodic=0
    g77: BSplineCurve PolesCount=4 KnotsCount=2 Degree=3 IsPeriodic=0
    g78: BSplineCurve PolesCount=4 KnotsCount=2 Degree=3 IsPeriodic=0
    g79: BSplineCurve PolesCount=4 KnotsCount=2 Degree=3 IsPeriodic=0
    g80: BSplineCurve PolesCount=4 KnotsCount=2 Degree=3 IsPeriodic=0
    g81: BSplineCurve PolesCount=4 KnotsCount=2 Degree=3 IsPeriodic=0
    g82: BSplineCurve PolesCount=4 KnotsCount=2 Degree=3 IsPeriodic=0
    g83: BSplineCurve PolesCount=4 KnotsCount=2 Degree=3 IsPeriodic=0
    g84: BSplineCurve PolesCount=4 KnotsCount=2 Degree=3 IsPeriodic=0
  constraints (87):
    c: Coincident(g0,g1)
    c: Coincident(g1,g2)
    c: Coincident(g2,g3)
    c: Coincident(g3,g4)
    c: Coincident(g4,g5)
    c: Coincident(g5,g6)
    c: Coincident(g6,g7)
    c: Coincident(g7,g8)
    c: Coincident(g8,g9)
    c: Coincident(g9,g10)
    c: Coincident(g10,g11)
    c: Coincident(g11,g12)
    c: Coincident(g12,g13)
    c: Coincident(g13,g14)
    c: Coincident(g14,g15)
    c: Coincident(g15,g16)
    c: Coincident(g16,g17)
    c: Coincident(g17,g18)
    c: Coincident(g18,g19)
    c: Coincident(g19,g20)
    c: Coincident(g20,g21)
    c: Coincident(g21,g22)
    c: Coincident(g22,g23)
    c: Coincident(g23,g24)
    c: Coincident(g24,g25)
    c: Coincident(g25,g26)
    c: Coincident(g26,g27)
    c: Coincident(g27,g28)
    c: Coincident(g28,g29)
    c: Coincident(g29,g30)
    c: Coincident(g30,g31)
    c: Coincident(g31,g32)
    c: Coincident(g32,g33)
    c: Coincident(g33,g34)
    c: Coincident(g34,g35)
    c: Coincident(g35,g36)
    c: Coincident(g36,g37)
    c: Coincident(g37,g38)
    c: Coincident(g38,g39)
    c: Coincident(g39,g40)
    c: Coincident(g40,g41)
    c: Coincident(g41,g42)
    c: Coincident(g42,g43)
    c: Coincident(g43,g44)
    c: Coincident(g44,g45)
    c: Coincident(g45,g46)
    c: Coincident(g46,g47)
    c: Coincident(g47,g48)
    c: Coincident(g48,g49)
    c: Coincident(g49,g50)
    c: Coincident(g50,g51)
    c: Coincident(g51,g52)
    c: Coincident(g52,g53)
    c: Coincident(g53,g54)
    c: Coincident(g54,g55)
    c: Coincident(g55,g56)
    c: Coincident(g56,g57)
    c: Coincident(g57,g58)
    c: Coincident(g58,g59)
    c: Coincident(g59,g60)
    c: Coincident(g60,g61)
    c: Coincident(g61,g62)
    c: Coincident(g62,g0)
    c: Coincident(g63,g64)
    c: Coincident(g64,g65)
    c: Coincident(g65,g66)
    c: Coincident(g66,g67)
    c: Coincident(g67,g68)
    c: Coincident(g68,g69)
    c: Coincident(g69,g63)
    c: Coincident(g70,g71)
    c: Coincident(g71,g72)
    c: Coincident(g72,g73)
    c: Coincident(g73,g74)
    c: Coincident(g74,g75)
    c: Coincident(g75,g76)
    c: Coincident(g76,g70)
    c: Coincident(g77,g78)
    c: Coincident(g78,g79)
    c: Coincident(g79,g80)
    c: Coincident(g80,g81)
    c: Coincident(g81,g82)
    c: Coincident(g82,g83)
    c: Coincident(g83,g84)
    c: Coincident(g84,g77)
    c: Coincident(g70,g70)
    c: Coincident(g61,g0)
FEATURE [Sketcher::SketchObject] Sketch007  label="Investigator-Sketch"
  ArcFitTolerance = 1e-06
  FullyConstrained = false
  MakeInternals = false
  sketch-geometry (199):
    g0: BSplineCurve PolesCount=4 KnotsCount=2 Degree=3 IsPeriodic=0
    g1: BSplineCurve PolesCount=4 KnotsCount=2 Degree=3 IsPeriodic=0
    g2: BSplineCurve PolesCount=4 KnotsCount=2 Degree=3 IsPeriodic=0
    g3: BSplineCurve PolesCount=4 KnotsCount=2 Degree=3 IsPeriodic=0
    g4: BSplineCurve PolesCount=4 KnotsCount=2 Degree=3 IsPeriodic=0
    g5: BSplineCurve PolesCount=4 KnotsCount=2 Degree=3 IsPeriodic=0
    g6: BSplineCurve PolesCount=4 KnotsCount=2 Degree=3 IsPeriodic=0
    g7: BSplineCurve PolesCount=4 KnotsCount=2 Degree=3 IsPeriodic=0
    g8: BSplineCurve PolesCount=4 KnotsCount=2 Degree=3 IsPeriodic=0
    g9: BSplineCurve PolesCount=4 KnotsCount=2 Degree=3 IsPeriodic=0
    g10: BSplineCurve PolesCount=4 KnotsCount=2 Degree=3 IsPeriodic=0
    g11: BSplineCurve PolesCount=4 KnotsCount=2 Degree=3 IsPeriodic=0
    g12: BSplineCurve PolesCount=4 KnotsCount=2 Degree=3 IsPeriodic=0
    g13: BSplineCurve PolesCount=4 KnotsCount=2 Degree=3 IsPeriodic=0
    g14: BSplineCurve PolesCount=4 KnotsCount=2 Degree=3 IsPeriodic=0
    g15: BSplineCurve PolesCount=4 KnotsCount=2 Degree=3 IsPeriodic=0
    g16: BSplineCurve PolesCount=4 KnotsCount=2 Degree=3 IsPeriodic=0
    g17: BSplineCurve PolesCount=4 KnotsCount=2 Degree=3 IsPeriodic=0
    g18: BSplineCurve PolesCount=4 KnotsCount=2 Degree=3 IsPeriodic=0
    g19: BSplineCurve PolesCount=4 KnotsCount=2 Degree=3 IsPeriodic=0
    g20: BSplineCurve PolesCount=4 KnotsCount=2 Degree=3 IsPeriodic=0
    g21: BSplineCurve PolesCount=4 KnotsCount=2 Degree=3 IsPeriodic=0
    g22: BSplineCurve PolesCount=4 KnotsCount=2 Degree=3 IsPeriodic=0
    g23: BSplineCurve PolesCount=4 KnotsCount=2 Degree=3 IsPeriodic=0
    g24: BSplineCurve PolesCount=4 KnotsCount=2 Degree=3 IsPeriodic=0
    g25: BSplineCurve PolesCount=4 KnotsCount=2 Degree=3 IsPeriodic=0
    g26: BSplineCurve PolesCount=4 KnotsCount=2 Degree=3 IsPeriodic=0
    g27: BSplineCurve PolesCount=4 KnotsCount=2 Degree=3 IsPeriodic=0
    g28: BSplineCurve PolesCount=4 KnotsCount=2 Degree=3 IsPeriodic=0
    g29: BSplineCurve PolesCount=4 KnotsCount=2 Degree=3 IsPeriodic=0
    g30: BSplineCurve PolesCount=4 KnotsCount=2 Degree=3 IsPeriodic=0
    g31: BSplineCurve PolesCount=4 KnotsCount=2 Degree=3 IsPeriodic=0
    g32: BSplineCurve PolesCount=4 KnotsCount=2 Degree=3 IsPeriodic=0
    g33: BSplineCurve PolesCount=4 KnotsCount=2 Degree=3 IsPeriodic=0
    g34: BSplineCurve PolesCount=4 KnotsCount=2 Degree=3 IsPeriodic=0
    g35: BSplineCurve PolesCount=4 KnotsCount=2 Degree=3 IsPeriodic=0
    g36: BSplineCurve PolesCount=4 KnotsCount=2 Degree=3 IsPeriodic=0
    g37: BSplineCurve PolesCount=4 KnotsCount=2 Degree=3 IsPeriodic=0
    g38: BSplineCurve PolesCount=4 KnotsCount=2 Degree=3 IsPeriodic=0
    g39: BSplineCurve PolesCount=4 KnotsCount=2 Degree=3 IsPeriodic=0
    g40: BSplineCurve PolesCount=4 KnotsCount=2 Degree=3 IsPeriodic=0
    g41: BSplineCurve PolesCount=4 KnotsCount=2 Degree=3 IsPeriodic=0
    g42: BSplineCurve PolesCount=4 KnotsCount=2 Degree=3 IsPeriodic=0
    g43: BSplineCurve PolesCount=4 KnotsCount=2 Degree=3 IsPeriodic=0
    g44: BSplineCurve PolesCount=4 KnotsCount=2 Degree=3 IsPeriodic=0
    g45: BSplineCurve PolesCount=4 KnotsCount=2 Degree=3 IsPeriodic=0
    g46: BSplineCurve PolesCount=4 KnotsCount=2 Degree=3 IsPeriodic=0
    g47: BSplineCurve PolesCount=4 KnotsCount=2 Degree=3 IsPeriodic=0
    g48: BSplineCurve PolesCount=4 KnotsCount=2 Degree=3 IsPeriodic=0
    g49: BSplineCurve PolesCount=2 KnotsCount=2 Degree=1 IsPeriodic=0
    g50: BSplineCurve PolesCount=4 KnotsCount=2 Degree=3 IsPeriodic=0
    g51: BSplineCurve PolesCount=4 KnotsCount=2 Degree=3 IsPeriodic=0
    g52: BSplineCurve PolesCount=4 KnotsCount=2 Degree=3 IsPeriodic=0
    g53: BSplineCurve PolesCount=4 KnotsCount=2 Degree=3 IsPeriodic=0
    g54: BSplineCurve PolesCount=4 KnotsCount=2 Degree=3 IsPeriodic=0
    g55: BSplineCurve PolesCount=4 KnotsCount=2 Degree=3 IsPeriodic=0
    g56: BSplineCurve PolesCount=4 KnotsCount=2 Degree=3 IsPeriodic=0
    g57: BSplineCurve PolesCount=4 KnotsCount=2 Degree=3 IsPeriodic=0
    g58: BSplineCurve PolesCount=4 KnotsCount=2 Degree=3 IsPeriodic=0
    g59: BSplineCurve PolesCount=4 KnotsCount=2 Degree=3 IsPeriodic=0
    g60: BSplineCurve PolesCount=4 KnotsCount=2 Degree=3 IsPeriodic=0
    g61: BSplineCurve PolesCount=4 KnotsCount=2 Degree=3 IsPeriodic=0
    g62: BSplineCurve PolesCount=4 KnotsCount=2 Degree=3 IsPeriodic=0
    g63: BSplineCurve PolesCount=4 KnotsCount=2 Degree=3 IsPeriodic=0
    g64: BSplineCurve PolesCount=4 KnotsCount=2 Degree=3 IsPeriodic=0
    g65: BSplineCurve PolesCount=4 KnotsCount=2 Degree=3 IsPeriodic=0
    g66: BSplineCurve PolesCount=4 KnotsCount=2 Degree=3 IsPeriodic=0
    g67: BSplineCurve PolesCount=4 KnotsCount=2 Degree=3 IsPeriodic=0
    g68: BSplineCurve PolesCount=4 KnotsCount=2 Degree=3 IsPeriodic=0
    g69: BSplineCurve PolesCount=4 KnotsCount=2 Degree=3 IsPeriodic=0
    g70: BSplineCurve PolesCount=4 KnotsCount=2 Degree=3 IsPeriodic=0
    g71: BSplineCurve PolesCount=4 KnotsCount=2 Degree=3 IsPeriodic=0
    g72: BSplineCurve PolesCount=4 KnotsCount=2 Degree=3 IsPeriodic=0
    g73: BSplineCurve PolesCount=4 KnotsCount=2 Degree=3 IsPeriodic=0
    g74: BSplineCurve PolesCount=4 KnotsCount=2 Degree=3 IsPeriodic=0
    g75: BSplineCurve PolesCount=4 KnotsCount=2 Degree=3 IsPeriodic=0
    g76: BSplineCurve PolesCount=4 KnotsCount=2 Degree=3 IsPeriodic=0
    g77: BSplineCurve PolesCount=4 KnotsCount=2 Degree=3 IsPeriodic=0
    g78: BSplineCurve PolesCount=4 KnotsCount=2 Degree=3 IsPeriodic=0
    g79: BSplineCurve PolesCount=4 KnotsCount=2 Degree=3 IsPeriodic=0
    g80: BSplineCurve PolesCount=4 KnotsCount=2 Degree=3 IsPeriodic=0
    g81: BSplineCurve PolesCount=4 KnotsCount=2 Degree=3 IsPeriodic=0
    g82: BSplineCurve PolesCount=4 KnotsCount=2 Degree=3 IsPeriodic=0
    g83: BSplineCurve PolesCount=4 KnotsCount=2 Degree=3 IsPeriodic=0
    g84: BSplineCurve PolesCount=4 KnotsCount=2 Degree=3 IsPeriodic=0
    g85: BSplineCurve PolesCount=4 KnotsCount=2 Degree=3 IsPeriodic=0
    g86: BSplineCurve PolesCount=4 KnotsCount=2 Degree=3 IsPeriodic=0
    g87: BSplineCurve PolesCount=4 KnotsCount=2 Degree=3 IsPeriodic=0
    g88: BSplineCurve PolesCount=4 KnotsCount=2 Degree=3 IsPeriodic=0
    g89: BSplineCurve PolesCount=4 KnotsCount=2 Degree=3 IsPeriodic=0
    g90: BSplineCurve PolesCount=4 KnotsCount=2 Degree=3 IsPeriodic=0
    g91: BSplineCurve PolesCount=4 KnotsCount=2 Degree=3 IsPeriodic=0
    g92: BSplineCurve PolesCount=4 KnotsCount=2 Degree=3 IsPeriodic=0
    g93: BSplineCurve PolesCount=2 KnotsCount=2 Degree=1 IsPeriodic=0
    g94: BSplineCurve PolesCount=4 KnotsCount=2 Degree=3 IsPeriodic=0
    g95: BSplineCurve PolesCount=4 KnotsCount=2 Degree=3 IsPeriodic=0
    g96: BSplineCurve PolesCount=4 KnotsCount=2 Degree=3 IsPeriodic=0
    g97: BSplineCurve PolesCount=2 KnotsCount=2 Degree=1 IsPeriodic=0
    g98: BSplineCurve PolesCount=4 KnotsCount=2 Degree=3 IsPeriodic=0
    g99: BSplineCurve PolesCount=4 KnotsCount=2 Degree=3 IsPeriodic=0
    g100: BSplineCurve PolesCount=4 KnotsCount=2 Degree=3 IsPeriodic=0
    g101: BSplineCurve PolesCount=4 KnotsCount=2 Degree=3 IsPeriodic=0
    g102: BSplineCurve PolesCount=4 KnotsCount=2 Degree=3 IsPeriodic=0
    g103: BSplineCurve PolesCount=4 KnotsCount=2 Degree=3 IsPeriodic=0
    g104: BSplineCurve PolesCount=2 KnotsCount=2 Degree=1 IsPeriodic=0
    g105: BSplineCurve PolesCount=4 KnotsCount=2 Degree=3 IsPeriodic=0
    g106: BSplineCurve PolesCount=4 KnotsCount=2 Degree=3 IsPeriodic=0
    g107: BSplineCurve PolesCount=4 KnotsCount=2 Degree=3 IsPeriodic=0
    g108: BSplineCurve PolesCount=4 KnotsCount=2 Degree=3 IsPeriodic=0
    g109: BSplineCurve PolesCount=4 KnotsCount=2 Degree=3 IsPeriodic=0
    g110: BSplineCurve PolesCount=4 KnotsCount=2 Degree=3 IsPeriodic=0
    g111: BSplineCurve PolesCount=4 KnotsCount=2 Degree=3 IsPeriodic=0
    g112: BSplineCurve PolesCount=2 KnotsCount=2 Degree=1 IsPeriodic=0
    g113: BSplineCurve PolesCount=4 KnotsCount=2 Degree=3 IsPeriodic=0
    g114: BSplineCurve PolesCount=4 KnotsCount=2 Degree=3 IsPeriodic=0
    g115: BSplineCurve PolesCount=4 KnotsCount=2 Degree=3 IsPeriodic=0
    g116: BSplineCurve PolesCount=4 KnotsCount=2 Degree=3 IsPeriodic=0
    g117: BSplineCurve PolesCount=4 KnotsCount=2 Degree=3 IsPeriodic=0
    g118: BSplineCurve PolesCount=4 KnotsCount=2 Degree=3 IsPeriodic=0
    g119: BSplineCurve PolesCount=4 KnotsCount=2 Degree=3 IsPeriodic=0
    g120: BSplineCurve PolesCount=4 KnotsCount=2 Degree=3 IsPeriodic=0
    g121: BSplineCurve PolesCount=4 KnotsCount=2 Degree=3 IsPeriodic=0
    g122: BSplineCurve PolesCount=4 KnotsCount=2 Degree=3 IsPeriodic=0
    g123: BSplineCurve PolesCount=4 KnotsCount=2 Degree=3 IsPeriodic=0
    g124: BSplineCurve PolesCount=4 KnotsCount=2 Degree=3 IsPeriodic=0
    g125: BSplineCurve PolesCount=4 KnotsCount=2 Degree=3 IsPeriodic=0
    g126: BSplineCurve PolesCount=4 KnotsCount=2 Degree=3 IsPeriodic=0
    g127: BSplineCurve PolesCount=4 KnotsCount=2 Degree=3 IsPeriodic=0
    g128: BSplineCurve PolesCount=4 KnotsCount=2 Degree=3 IsPeriodic=0
    g129: BSplineCurve PolesCount=4 KnotsCount=2 Degree=3 IsPeriodic=0
    g130: BSplineCurve PolesCount=4 KnotsCount=2 Degree=3 IsPeriodic=0
    g131: BSplineCurve PolesCount=2 KnotsCount=2 Degree=1 IsPeriodic=0
    g132: BSplineCurve PolesCount=4 KnotsCount=2 Degree=3 IsPeriodic=0
    g133: BSplineCurve PolesCount=4 KnotsCount=2 Degree=3 IsPeriodic=0
    g134: BSplineCurve PolesCount=4 KnotsCount=2 Degree=3 IsPeriodic=0
    g135: BSplineCurve PolesCount=4 KnotsCount=2 Degree=3 IsPeriodic=0
    g136: BSplineCurve PolesCount=4 KnotsCount=2 Degree=3 IsPeriodic=0
    g137: BSplineCurve PolesCount=4 KnotsCount=2 Degree=3 IsPeriodic=0
    g138: BSplineCurve PolesCount=4 KnotsCount=2 Degree=3 IsPeriodic=0
    g139: BSplineCurve PolesCount=4 KnotsCount=2 Degree=3 IsPeriodic=0
    g140: BSplineCurve PolesCount=4 KnotsCount=2 Degree=3 IsPeriodic=0
    g141: BSplineCurve PolesCount=4 KnotsCount=2 Degree=3 IsPeriodic=0
    g142: BSplineCurve PolesCount=2 KnotsCount=2 Degree=1 IsPeriodic=0
    g143: BSplineCurve PolesCount=4 KnotsCount=2 Degree=3 IsPeriodic=0
    g144: BSplineCurve PolesCount=2 KnotsCount=2 Degree=1 IsPeriodic=0
    g145: BSplineCurve PolesCount=2 KnotsCount=2 Degree=1 IsPeriodic=0
    g146: BSplineCurve PolesCount=4 KnotsCount=2 Degree=3 IsPeriodic=0
    g147: BSplineCurve PolesCount=4 KnotsCount=2 Degree=3 IsPeriodic=0
    g148: BSplineCurve PolesCount=4 KnotsCount=2 Degree=3 IsPeriodic=0
    g149: BSplineCurve PolesCount=4 KnotsCount=2 Degree=3 IsPeriodic=0
    g150: BSplineCurve PolesCount=4 KnotsCount=2 Degree=3 IsPeriodic=0
    g151: BSplineCurve PolesCount=4 KnotsCount=2 Degree=3 IsPeriodic=0
    g152: BSplineCurve PolesCount=4 KnotsCount=2 Degree=3 IsPeriodic=0
    g153: BSplineCurve PolesCount=4 KnotsCount=2 Degree=3 IsPeriodic=0
    g154: BSplineCurve PolesCount=4 KnotsCount=2 Degree=3 IsPeriodic=0
    g155: BSplineCurve PolesCount=4 KnotsCount=2 Degree=3 IsPeriodic=0
    g156: BSplineCurve PolesCount=4 KnotsCount=2 Degree=3 IsPeriodic=0
    g157: BSplineCurve PolesCount=4 KnotsCount=2 Degree=3 IsPeriodic=0
    g158: BSplineCurve PolesCount=4 KnotsCount=2 Degree=3 IsPeriodic=0
    g159: BSplineCurve PolesCount=2 KnotsCount=2 Degree=1 IsPeriodic=0
    g160: BSplineCurve PolesCount=4 KnotsCount=2 Degree=3 IsPeriodic=0
    g161: BSplineCurve PolesCount=4 KnotsCount=2 Degree=3 IsPeriodic=0
    g162: BSplineCurve PolesCount=4 KnotsCount=2 Degree=3 IsPeriodic=0
    g163: BSplineCurve PolesCount=4 KnotsCount=2 Degree=3 IsPeriodic=0
    g164: BSplineCurve PolesCount=4 KnotsCount=2 Degree=3 IsPeriodic=0
    g165: BSplineCurve PolesCount=4 KnotsCount=2 Degree=3 IsPeriodic=0
    g166: BSplineCurve PolesCount=4 KnotsCount=2 Degree=3 IsPeriodic=0
    g167: BSplineCurve PolesCount=4 KnotsCount=2 Degree=3 IsPeriodic=0
    g168: BSplineCurve PolesCount=2 KnotsCount=2 Degree=1 IsPeriodic=0
    g169: BSplineCurve PolesCount=2 KnotsCount=2 Degree=1 IsPeriodic=0
    g170: BSplineCurve PolesCount=2 KnotsCount=2 Degree=1 IsPeriodic=0
    g171: BSplineCurve PolesCount=4 KnotsCount=2 Degree=3 IsPeriodic=0
    g172: BSplineCurve PolesCount=4 KnotsCount=2 Degree=3 IsPeriodic=0
    g173: BSplineCurve PolesCount=4 KnotsCount=2 Degree=3 IsPeriodic=0
    g174: BSplineCurve PolesCount=2 KnotsCount=2 Degree=1 IsPeriodic=0
    g175: BSplineCurve PolesCount=4 KnotsCount=2 Degree=3 IsPeriodic=0
    g176: BSplineCurve PolesCount=4 KnotsCount=2 Degree=3 IsPeriodic=0
    g177: BSplineCurve PolesCount=4 KnotsCount=2 Degree=3 IsPeriodic=0
    g178: BSplineCurve PolesCount=4 KnotsCount=2 Degree=3 IsPeriodic=0
    g179: BSplineCurve PolesCount=4 KnotsCount=2 Degree=3 IsPeriodic=0
    g180: BSplineCurve PolesCount=4 KnotsCount=2 Degree=3 IsPeriodic=0
    g181: BSplineCurve PolesCount=4 KnotsCount=2 Degree=3 IsPeriodic=0
    g182: BSplineCurve PolesCount=4 KnotsCount=2 Degree=3 IsPeriodic=0
    g183: BSplineCurve PolesCount=4 KnotsCount=2 Degree=3 IsPeriodic=0
    g184: BSplineCurve PolesCount=4 KnotsCount=2 Degree=3 IsPeriodic=0
    g185: BSplineCurve PolesCount=4 KnotsCount=2 Degree=3 IsPeriodic=0
    g186: BSplineCurve PolesCount=4 KnotsCount=2 Degree=3 IsPeriodic=0
    g187: BSplineCurve PolesCount=4 KnotsCount=2 Degree=3 IsPeriodic=0
    g188: BSplineCurve PolesCount=4 KnotsCount=2 Degree=3 IsPeriodic=0
    g189: BSplineCurve PolesCount=4 KnotsCount=2 Degree=3 IsPeriodic=0
    g190: BSplineCurve PolesCount=4 KnotsCount=2 Degree=3 IsPeriodic=0
    g191: BSplineCurve PolesCount=4 KnotsCount=2 Degree=3 IsPeriodic=0
    g192: BSplineCurve PolesCount=4 KnotsCount=2 Degree=3 IsPeriodic=0
    g193: BSplineCurve PolesCount=4 KnotsCount=2 Degree=3 IsPeriodic=0
    g194: BSplineCurve PolesCount=4 KnotsCount=2 Degree=3 IsPeriodic=0
    g195: BSplineCurve PolesCount=4 KnotsCount=2 Degree=3 IsPeriodic=0
    g196: BSplineCurve PolesCount=2 KnotsCount=2 Degree=1 IsPeriodic=0
    g197: BSplineCurve PolesCount=2 KnotsCount=2 Degree=1 IsPeriodic=0
    g198: BSplineCurve PolesCount=4 KnotsCount=2 Degree=3 IsPeriodic=0
  constraints (209):
    c: Coincident(g0,g1)
    c: Coincident(g1,g2)
    c: Coincident(g2,g3)
    c: Coincident(g3,g4)
    c: Coincident(g4,g5)
    c: Coincident(g5,g6)
    c: Coincident(g6,g7)
    c: Coincident(g7,g8)
    c: Coincident(g8,g9)
    c: Coincident(g9,g10)
    c: Coincident(g10,g11)
    c: Coincident(g11,g12)
    c: Coincident(g12,g13)
    c: Coincident(g13,g14)
    c: Coincident(g14,g15)
    c: Coincident(g15,g16)
    c: Coincident(g16,g17)
    c: Coincident(g17,g18)
    c: Coincident(g18,g19)
    c: Coincident(g19,g20)
    c: Coincident(g20,g21)
    c: Coincident(g21,g22)
    c: Coincident(g22,g23)
    c: Coincident(g23,g24)
    c: Coincident(g24,g25)
    c: Coincident(g25,g26)
    c: Coincident(g26,g27)
    c: Coincident(g27,g28)
    c: Coincident(g28,g29)
    c: Coincident(g29,g30)
    c: Coincident(g30,g31)
    c: Coincident(g31,g32)
    c: Coincident(g32,g33)
    c: Coincident(g33,g34)
    c: Coincident(g34,g35)
    c: Coincident(g35,g36)
    c: Coincident(g36,g37)
    c: Coincident(g37,g38)
    c: Coincident(g38,g39)
    c: Coincident(g39,g40)
    c: Coincident(g40,g41)
    c: Coincident(g41,g42)
    c: Coincident(g42,g43)
    c: Coincident(g43,g44)
    c: Coincident(g44,g0)
    c: Coincident(g45,g46)
    c: Coincident(g46,g47)
    c: Coincident(g47,g48)
    c: Coincident(g48,g45)
    c: Coincident(g49,g50)
    c: Coincident(g50,g51)
    c: Coincident(g51,g52)
    c: Coincident(g52,g53)
    c: Coincident(g53,g49)
    c: Coincident(g54,g55)
    c: Coincident(g55,g56)
    c: Coincident(g56,g57)
    c: Coincident(g57,g58)
    c: Coincident(g58,g59)
    c: Coincident(g59,g60)
    c: Coincident(g60,g54)
    c: Coincident(g61,g62)
    c: Coincident(g62,g63)
    c: Coincident(g63,g61)
    c: Coincident(g64,g65)
    c: Coincident(g65,g66)
    c: Coincident(g66,g67)
    c: Coincident(g67,g64)
    c: Coincident(g68,g69)
    c: Coincident(g69,g70)
    c: Coincident(g70,g71)
    c: Coincident(g71,g72)
    c: Coincident(g72,g73)
    c: Coincident(g73,g68)
    c: Coincident(g74,g75)
    c: Coincident(g75,g76)
    c: Coincident(g76,g77)
    c: Coincident(g77,g78)
    c: Coincident(g78,g79)
    c: Coincident(g79,g80)
    c: Coincident(g80,g81)
    c: Coincident(g81,g82)
    c: Coincident(g82,g74)
    c: Coincident(g83,g84)
    c: Coincident(g84,g85)
    c: Coincident(g85,g83)
    c: Coincident(g86,g87)
    c: Coincident(g87,g88)
    c: Coincident(g88,g89)
    c: Coincident(g89,g86)
    c: Coincident(g90,g91)
    c: Coincident(g91,g92)
    c: Coincident(g92,g90)
    c: Coincident(g93,g94)
    c: Coincident(g94,g95)
    c: Coincident(g95,g96)
    c: Coincident(g96,g93)
    c: Coincident(g97,g98)
    c: Coincident(g98,g99)
    c: Coincident(g99,g100)
    c: Coincident(g100,g97)
    c: Coincident(g101,g102)
    c: Coincident(g102,g103)
    c: Coincident(g103,g101)
    c: Coincident(g104,g105)
    c: Coincident(g105,g106)
    c: Coincident(g106,g107)
    c: Coincident(g107,g108)
    c: Coincident(g108,g109)
    c: Coincident(g109,g110)
    c: Coincident(g110,g111)
    c: Coincident(g111,g104)
    c: Coincident(g112,g113)
    c: Coincident(g113,g114)
    c: Coincident(g114,g115)
    c: Coincident(g115,g116)
    c: Coincident(g116,g117)
    c: Coincident(g117,g112)
    c: Coincident(g118,g119)
    c: Coincident(g119,g120)
    c: Coincident(g120,g118)
    c: Coincident(g121,g122)
    c: Coincident(g122,g123)
    c: Coincident(g123,g124)
    c: Coincident(g124,g121)
    c: Coincident(g125,g126)
    c: Coincident(g126,g127)
    c: Coincident(g127,g125)
    c: Coincident(g128,g129)
    c: Coincident(g129,g130)
    c: Coincident(g130,g128)
    c: Coincident(g131,g132)
    c: Coincident(g132,g133)
    c: Coincident(g133,g134)
    c: Coincident(g134,g135)
    c: Coincident(g135,g131)
    c: Coincident(g136,g137)
    c: Coincident(g137,g138)
    c: Coincident(g138,g136)
    c: Coincident(g139,g140)
    c: Coincident(g140,g141)
    c: Coincident(g141,g139)
    c: Coincident(g142,g143)
    c: Coincident(g143,g144)
    c: Coincident(g144,g145)
    c: Coincident(g145,g146)
    c: Coincident(g146,g147)
    c: Coincident(g147,g142)
    c: Coincident(g148,g149)
    c: Coincident(g149,g150)
    c: Coincident(g150,g151)
    c: Coincident(g151,g152)
    c: Coincident(g152,g148)
    c: Coincident(g153,g154)
    c: Coincident(g154,g155)
    c: Coincident(g155,g156)
    c: Coincident(g156,g157)
    c: Coincident(g157,g158)
    c: Coincident(g158,g153)
    c: Coincident(g159,g160)
    c: Coincident(g160,g161)
    c: Coincident(g161,g162)
    c: Coincident(g162,g163)
    c: Coincident(g163,g164)
    c: Coincident(g164,g165)
    c: Coincident(g165,g166)
    c: Coincident(g166,g167)
    c: Coincident(g167,g159)
    c: Coincident(g168,g169)
    c: Coincident(g169,g170)
    c: Coincident(g170,g171)
    c: Coincident(g171,g172)
    c: Coincident(g172,g173)
    c: Coincident(g173,g168)
    c: Coincident(g174,g175)
    c: Coincident(g175,g176)
    c: Coincident(g176,g177)
    c: Coincident(g177,g178)
    c: Coincident(g178,g179)
    c: Coincident(g179,g174)
    c: Coincident(g180,g181)
    c: Coincident(g181,g182)
    c: Coincident(g182,g180)
    c: Coincident(g183,g184)
    c: Coincident(g184,g185)
    c: Coincident(g185,g186)
    c: Coincident(g186,g183)
    c: Coincident(g187,g188)
    c: Coincident(g188,g189)
    c: Coincident(g189,g190)
    c: Coincident(g190,g191)
    c: Coincident(g191,g187)
    c: Coincident(g192,g193)
    c: Coincident(g193,g194)
    c: Coincident(g194,g195)
    c: Coincident(g195,g196)
    c: Coincident(g196,g197)
    c: Coincident(g197,g198)
    c: Coincident(g198,g192)
    c: Coincident(g142,g142)
    c: Coincident(g174,g174)
    c: Coincident(g112,g112)
    c: Coincident(g93,g93)
    c: Coincident(g97,g97)
    c: Coincident(g104,g104)
    c: Coincident(g159,g159)
    c: Coincident(g131,g131)
    c: Coincident(g168,g168)
    c: Coincident(g49,g49)
FEATURE [Sketcher::SketchObject] Sketch008  label="Librarian-Sketch"
  ArcFitTolerance = 1e-06
  FullyConstrained = false
  MakeInternals = false
  sketch-geometry (146):
    g0: BSplineCurve PolesCount=4 KnotsCount=2 Degree=3 IsPeriodic=0
    g1: BSplineCurve PolesCount=2 KnotsCount=2 Degree=1 IsPeriodic=0
    g2: BSplineCurve PolesCount=2 KnotsCount=2 Degree=1 IsPeriodic=0
    g3: BSplineCurve PolesCount=4 KnotsCount=2 Degree=3 IsPeriodic=0
    g4: BSplineCurve PolesCount=4 KnotsCount=2 Degree=3 IsPeriodic=0
    g5: BSplineCurve PolesCount=4 KnotsCount=2 Degree=3 IsPeriodic=0
    g6: BSplineCurve PolesCount=4 KnotsCount=2 Degree=3 IsPeriodic=0
    g7: BSplineCurve PolesCount=4 KnotsCount=2 Degree=3 IsPeriodic=0
    g8: BSplineCurve PolesCount=4 KnotsCount=2 Degree=3 IsPeriodic=0
    g9: BSplineCurve PolesCount=4 KnotsCount=2 Degree=3 IsPeriodic=0
    g10: BSplineCurve PolesCount=4 KnotsCount=2 Degree=3 IsPeriodic=0
    g11: BSplineCurve PolesCount=4 KnotsCount=2 Degree=3 IsPeriodic=0
    g12: BSplineCurve PolesCount=4 KnotsCount=2 Degree=3 IsPeriodic=0
    g13: BSplineCurve PolesCount=4 KnotsCount=2 Degree=3 IsPeriodic=0
    g14: BSplineCurve PolesCount=4 KnotsCount=2 Degree=3 IsPeriodic=0
    g15: BSplineCurve PolesCount=2 KnotsCount=2 Degree=1 IsPeriodic=0
    g16: BSplineCurve PolesCount=2 KnotsCount=2 Degree=1 IsPeriodic=0
    g17: BSplineCurve PolesCount=4 KnotsCount=2 Degree=3 IsPeriodic=0
    g18: BSplineCurve PolesCount=4 KnotsCount=2 Degree=3 IsPeriodic=0
    g19: BSplineCurve PolesCount=4 KnotsCount=2 Degree=3 IsPeriodic=0
    g20: BSplineCurve PolesCount=2 KnotsCount=2 Degree=1 IsPeriodic=0
    g21: BSplineCurve PolesCount=2 KnotsCount=2 Degree=1 IsPeriodic=0
    g22: BSplineCurve PolesCount=2 KnotsCount=2 Degree=1 IsPeriodic=0
    g23: BSplineCurve PolesCount=2 KnotsCount=2 Degree=1 IsPeriodic=0
    g24: BSplineCurve PolesCount=4 KnotsCount=2 Degree=3 IsPeriodic=0
    g25: BSplineCurve PolesCount=4 KnotsCount=2 Degree=3 IsPeriodic=0
    g26: BSplineCurve PolesCount=4 KnotsCount=2 Degree=3 IsPeriodic=0
    g27: BSplineCurve PolesCount=4 KnotsCount=2 Degree=3 IsPeriodic=0
    g28: BSplineCurve PolesCount=4 KnotsCount=2 Degree=3 IsPeriodic=0
    g29: BSplineCurve PolesCount=4 KnotsCount=2 Degree=3 IsPeriodic=0
    g30: BSplineCurve PolesCount=4 KnotsCount=2 Degree=3 IsPeriodic=0
    g31: BSplineCurve PolesCount=4 KnotsCount=2 Degree=3 IsPeriodic=0
    g32: BSplineCurve PolesCount=4 KnotsCount=2 Degree=3 IsPeriodic=0
    g33: BSplineCurve PolesCount=4 KnotsCount=2 Degree=3 IsPeriodic=0
    g34: BSplineCurve PolesCount=4 KnotsCount=2 Degree=3 IsPeriodic=0
    g35: BSplineCurve PolesCount=4 KnotsCount=2 Degree=3 IsPeriodic=0
    g36: BSplineCurve PolesCount=2 KnotsCount=2 Degree=1 IsPeriodic=0
    g37: BSplineCurve PolesCount=2 KnotsCount=2 Degree=1 IsPeriodic=0
    g38: BSplineCurve PolesCount=4 KnotsCount=2 Degree=3 IsPeriodic=0
    g39: BSplineCurve PolesCount=4 KnotsCount=2 Degree=3 IsPeriodic=0
    g40: BSplineCurve PolesCount=4 KnotsCount=2 Degree=3 IsPeriodic=0
    g41: BSplineCurve PolesCount=4 KnotsCount=2 Degree=3 IsPeriodic=0
    g42: BSplineCurve PolesCount=4 KnotsCount=2 Degree=3 IsPeriodic=0
    g43: BSplineCurve PolesCount=2 KnotsCount=2 Degree=1 IsPeriodic=0
    g44: BSplineCurve PolesCount=2 KnotsCount=2 Degree=1 IsPeriodic=0
    g45: BSplineCurve PolesCount=2 KnotsCount=2 Degree=1 IsPeriodic=0
    g46: BSplineCurve PolesCount=4 KnotsCount=2 Degree=3 IsPeriodic=0
    g47: BSplineCurve PolesCount=4 KnotsCount=2 Degree=3 IsPeriodic=0
    g48: BSplineCurve PolesCount=4 KnotsCount=2 Degree=3 IsPeriodic=0
    g49: BSplineCurve PolesCount=4 KnotsCount=2 Degree=3 IsPeriodic=0
    g50: BSplineCurve PolesCount=4 KnotsCount=2 Degree=3 IsPeriodic=0
    g51: BSplineCurve PolesCount=4 KnotsCount=2 Degree=3 IsPeriodic=0
    g52: BSplineCurve PolesCount=2 KnotsCount=2 Degree=1 IsPeriodic=0
    g53: BSplineCurve PolesCount=2 KnotsCount=2 Degree=1 IsPeriodic=0
    g54: BSplineCurve PolesCount=4 KnotsCount=2 Degree=3 IsPeriodic=0
    g55: BSplineCurve PolesCount=4 KnotsCount=2 Degree=3 IsPeriodic=0
    g56: BSplineCurve PolesCount=4 KnotsCount=2 Degree=3 IsPeriodic=0
    g57: BSplineCurve PolesCount=4 KnotsCount=2 Degree=3 IsPeriodic=0
    g58: BSplineCurve PolesCount=4 KnotsCount=2 Degree=3 IsPeriodic=0
    g59: BSplineCurve PolesCount=4 KnotsCount=2 Degree=3 IsPeriodic=0
    g60: BSplineCurve PolesCount=4 KnotsCount=2 Degree=3 IsPeriodic=0
    g61: BSplineCurve PolesCount=4 KnotsCount=2 Degree=3 IsPeriodic=0
    g62: BSplineCurve PolesCount=4 KnotsCount=2 Degree=3 IsPeriodic=0
    g63: BSplineCurve PolesCount=4 KnotsCount=2 Degree=3 IsPeriodic=0
    g64: BSplineCurve PolesCount=4 KnotsCount=2 Degree=3 IsPeriodic=0
    g65: BSplineCurve PolesCount=4 KnotsCount=2 Degree=3 IsPeriodic=0
    g66: BSplineCurve PolesCount=4 KnotsCount=2 Degree=3 IsPeriodic=0
    g67: BSplineCurve PolesCount=4 KnotsCount=2 Degree=3 IsPeriodic=0
    g68: BSplineCurve PolesCount=4 KnotsCount=2 Degree=3 IsPeriodic=0
    g69: BSplineCurve PolesCount=4 KnotsCount=2 Degree=3 IsPeriodic=0
    g70: BSplineCurve PolesCount=2 KnotsCount=2 Degree=1 IsPeriodic=0
    g71: BSplineCurve PolesCount=2 KnotsCount=2 Degree=1 IsPeriodic=0
    g72: BSplineCurve PolesCount=4 KnotsCount=2 Degree=3 IsPeriodic=0
    g73: BSplineCurve PolesCount=4 KnotsCount=2 Degree=3 IsPeriodic=0
    g74: BSplineCurve PolesCount=4 KnotsCount=2 Degree=3 IsPeriodic=0
    g75: BSplineCurve PolesCount=4 KnotsCount=2 Degree=3 IsPeriodic=0
    g76: BSplineCurve PolesCount=4 KnotsCount=2 Degree=3 IsPeriodic=0
    g77: BSplineCurve PolesCount=4 KnotsCount=2 Degree=3 IsPeriodic=0
    g78: BSplineCurve PolesCount=4 KnotsCount=2 Degree=3 IsPeriodic=0
    g79: BSplineCurve PolesCount=4 KnotsCount=2 Degree=3 IsPeriodic=0
    g80: BSplineCurve PolesCount=4 KnotsCount=2 Degree=3 IsPeriodic=0
    g81: BSplineCurve PolesCount=4 KnotsCount=2 Degree=3 IsPeriodic=0
    g82: BSplineCurve PolesCount=4 KnotsCount=2 Degree=3 IsPeriodic=0
    g83: BSplineCurve PolesCount=4 KnotsCount=2 Degree=3 IsPeriodic=0
    g84: BSplineCurve PolesCount=4 KnotsCount=2 Degree=3 IsPeriodic=0
    g85: BSplineCurve PolesCount=4 KnotsCount=2 Degree=3 IsPeriodic=0
    g86: BSplineCurve PolesCount=4 KnotsCount=2 Degree=3 IsPeriodic=0
    g87: BSplineCurve PolesCount=4 KnotsCount=2 Degree=3 IsPeriodic=0
    g88: BSplineCurve PolesCount=4 KnotsCount=2 Degree=3 IsPeriodic=0
    g89: BSplineCurve PolesCount=4 KnotsCount=2 Degree=3 IsPeriodic=0
    g90: BSplineCurve PolesCount=4 KnotsCount=2 Degree=3 IsPeriodic=0
    g91: BSplineCurve PolesCount=2 KnotsCount=2 Degree=1 IsPeriodic=0
    g92: BSplineCurve PolesCount=4 KnotsCount=2 Degree=3 IsPeriodic=0
    g93: BSplineCurve PolesCount=2 KnotsCount=2 Degree=1 IsPeriodic=0
    g94: BSplineCurve PolesCount=2 KnotsCount=2 Degree=1 IsPeriodic=0
    g95: BSplineCurve PolesCount=4 KnotsCount=2 Degree=3 IsPeriodic=0
    g96: BSplineCurve PolesCount=4 KnotsCount=2 Degree=3 IsPeriodic=0
    g97: BSplineCurve PolesCount=4 KnotsCount=2 Degree=3 IsPeriodic=0
    g98: BSplineCurve PolesCount=4 KnotsCount=2 Degree=3 IsPeriodic=0
    g99: BSplineCurve PolesCount=4 KnotsCount=2 Degree=3 IsPeriodic=0
    g100: BSplineCurve PolesCount=2 KnotsCount=2 Degree=1 IsPeriodic=0
    g101: BSplineCurve PolesCount=2 KnotsCount=2 Degree=1 IsPeriodic=0
    g102: BSplineCurve PolesCount=4 KnotsCount=2 Degree=3 IsPeriodic=0
    g103: BSplineCurve PolesCount=4 KnotsCount=2 Degree=3 IsPeriodic=0
    g104: BSplineCurve PolesCount=4 KnotsCount=2 Degree=3 IsPeriodic=0
    g105: BSplineCurve PolesCount=4 KnotsCount=2 Degree=3 IsPeriodic=0
    g106: BSplineCurve PolesCount=4 KnotsCount=2 Degree=3 IsPeriodic=0
    g107: BSplineCurve PolesCount=4 KnotsCount=2 Degree=3 IsPeriodic=0
    g108: BSplineCurve PolesCount=4 KnotsCount=2 Degree=3 IsPeriodic=0
    g109: BSplineCurve PolesCount=2 KnotsCount=2 Degree=1 IsPeriodic=0
    g110: BSplineCurve PolesCount=2 KnotsCount=2 Degree=1 IsPeriodic=0
    g111: BSplineCurve PolesCount=4 KnotsCount=2 Degree=3 IsPeriodic=0
    g112: BSplineCurve PolesCount=4 KnotsCount=2 Degree=3 IsPeriodic=0
    g113: BSplineCurve PolesCount=4 KnotsCount=2 Degree=3 IsPeriodic=0
    g114: BSplineCurve PolesCount=4 KnotsCount=2 Degree=3 IsPeriodic=0
    g115: BSplineCurve PolesCount=4 KnotsCount=2 Degree=3 IsPeriodic=0
    g116: BSplineCurve PolesCount=4 KnotsCount=2 Degree=3 IsPeriodic=0
    g117: BSplineCurve PolesCount=4 KnotsCount=2 Degree=3 IsPeriodic=0
    g118: BSplineCurve PolesCount=2 KnotsCount=2 Degree=1 IsPeriodic=0
    g119: BSplineCurve PolesCount=2 KnotsCount=2 Degree=1 IsPeriodic=0
    g120: BSplineCurve PolesCount=4 KnotsCount=2 Degree=3 IsPeriodic=0
    g121: BSplineCurve PolesCount=4 KnotsCount=2 Degree=3 IsPeriodic=0
    g122: BSplineCurve PolesCount=4 KnotsCount=2 Degree=3 IsPeriodic=0
    g123: BSplineCurve PolesCount=4 KnotsCount=2 Degree=3 IsPeriodic=0
    g124: BSplineCurve PolesCount=4 KnotsCount=2 Degree=3 IsPeriodic=0
    g125: BSplineCurve PolesCount=4 KnotsCount=2 Degree=3 IsPeriodic=0
    g126: BSplineCurve PolesCount=4 KnotsCount=2 Degree=3 IsPeriodic=0
    g127: BSplineCurve PolesCount=4 KnotsCount=2 Degree=3 IsPeriodic=0
    g128: BSplineCurve PolesCount=4 KnotsCount=2 Degree=3 IsPeriodic=0
    g129: BSplineCurve PolesCount=4 KnotsCount=2 Degree=3 IsPeriodic=0
    g130: BSplineCurve PolesCount=4 KnotsCount=2 Degree=3 IsPeriodic=0
    g131: BSplineCurve PolesCount=4 KnotsCount=2 Degree=3 IsPeriodic=0
    g132: BSplineCurve PolesCount=4 KnotsCount=2 Degree=3 IsPeriodic=0
    g133: BSplineCurve PolesCount=4 KnotsCount=2 Degree=3 IsPeriodic=0
    g134: BSplineCurve PolesCount=4 KnotsCount=2 Degree=3 IsPeriodic=0
    g135: BSplineCurve PolesCount=4 KnotsCount=2 Degree=3 IsPeriodic=0
    g136: BSplineCurve PolesCount=4 KnotsCount=2 Degree=3 IsPeriodic=0
    g137: BSplineCurve PolesCount=4 KnotsCount=2 Degree=3 IsPeriodic=0
    g138: BSplineCurve PolesCount=4 KnotsCount=2 Degree=3 IsPeriodic=0
    g139: BSplineCurve PolesCount=4 KnotsCount=2 Degree=3 IsPeriodic=0
    g140: BSplineCurve PolesCount=4 KnotsCount=2 Degree=3 IsPeriodic=0
    g141: BSplineCurve PolesCount=4 KnotsCount=2 Degree=3 IsPeriodic=0
    g142: BSplineCurve PolesCount=4 KnotsCount=2 Degree=3 IsPeriodic=0
    g143: BSplineCurve PolesCount=2 KnotsCount=2 Degree=1 IsPeriodic=0
    g144: BSplineCurve PolesCount=2 KnotsCount=2 Degree=1 IsPeriodic=0
    g145: BSplineCurve PolesCount=4 KnotsCount=2 Degree=3 IsPeriodic=0
  constraints (148):
    c: Coincident(g0,g1)
    c: Coincident(g1,g2)
    c: Coincident(g2,g3)
    c: Coincident(g3,g4)
    c: Coincident(g4,g5)
    c: Coincident(g5,g6)
    c: Coincident(g6,g7)
    c: Coincident(g7,g8)
    c: Coincident(g8,g9)
    c: Coincident(g9,g10)
    c: Coincident(g10,g11)
    c: Coincident(g11,g12)
    c: Coincident(g12,g13)
    c: Coincident(g13,g14)
    c: Coincident(g14,g15)
    c: Coincident(g15,g16)
    c: Coincident(g16,g17)
    c: Coincident(g17,g18)
    c: Coincident(g18,g19)
    c: Coincident(g19,g20)
    c: Coincident(g20,g21)
    c: Coincident(g21,g22)
    c: Coincident(g22,g23)
    c: Coincident(g23,g24)
    c: Coincident(g24,g25)
    c: Coincident(g25,g26)
    c: Coincident(g26,g27)
    c: Coincident(g27,g28)
    c: Coincident(g28,g29)
    c: Coincident(g29,g30)
    c: Coincident(g30,g31)
    c: Coincident(g31,g32)
    c: Coincident(g32,g33)
    c: Coincident(g33,g34)
    c: Coincident(g34,g35)
    c: Coincident(g35,g36)
    c: Coincident(g36,g37)
    c: Coincident(g37,g38)
    c: Coincident(g38,g39)
    c: Coincident(g39,g40)
    c: Coincident(g40,g41)
    c: Coincident(g41,g42)
    c: Coincident(g42,g43)
    c: Coincident(g43,g44)
    c: Coincident(g44,g0)
    c: Coincident(g45,g46)
    c: Coincident(g46,g47)
    c: Coincident(g47,g48)
    c: Coincident(g48,g49)
    c: Coincident(g49,g50)
    c: Coincident(g50,g51)
    c: Coincident(g51,g52)
    c: Coincident(g52,g53)
    c: Coincident(g53,g54)
    c: Coincident(g54,g45)
    c: Coincident(g55,g56)
    c: Coincident(g56,g57)
    c: Coincident(g57,g58)
    c: Coincident(g58,g59)
    c: Coincident(g59,g60)
    c: Coincident(g60,g61)
    c: Coincident(g61,g62)
    c: Coincident(g62,g63)
    c: Coincident(g63,g64)
    c: Coincident(g64,g65)
    c: Coincident(g65,g66)
    c: Coincident(g66,g67)
    c: Coincident(g67,g68)
    c: Coincident(g68,g69)
    c: Coincident(g69,g70)
    c: Coincident(g70,g71)
    c: Coincident(g71,g72)
    c: Coincident(g72,g73)
    c: Coincident(g73,g74)
    c: Coincident(g74,g75)
    c: Coincident(g75,g76)
    c: Coincident(g76,g77)
    c: Coincident(g77,g78)
    c: Coincident(g78,g79)
    c: Coincident(g79,g80)
    c: Coincident(g80,g81)
    c: Coincident(g81,g82)
    c: Coincident(g82,g83)
    c: Coincident(g83,g84)
    c: Coincident(g84,g85)
    c: Coincident(g85,g86)
    c: Coincident(g86,g87)
    c: Coincident(g87,g88)
    c: Coincident(g88,g89)
    c: Coincident(g89,g90)
    c: Coincident(g90,g55)
    c: Coincident(g91,g92)
    c: Coincident(g92,g93)
    c: Coincident(g93,g94)
    c: Coincident(g94,g95)
    c: Coincident(g95,g96)
    c: Coincident(g96,g97)
    c: Coincident(g97,g98)
    c: Coincident(g98,g99)
    c: Coincident(g99,g100)
    c: Coincident(g100,g101)
    c: Coincident(g101,g102)
    c: Coincident(g102,g103)
    c: Coincident(g103,g104)
    c: Coincident(g104,g105)
    c: Coincident(g105,g91)
    c: Coincident(g106,g107)
    c: Coincident(g107,g108)
    c: Coincident(g108,g109)
    c: Coincident(g109,g110)
    c: Coincident(g110,g111)
    c: Coincident(g111,g112)
    c: Coincident(g112,g113)
    c: Coincident(g113,g114)
    c: Coincident(g114,g115)
    c: Coincident(g115,g116)
    c: Coincident(g116,g117)
    c: Coincident(g117,g118)
    c: Coincident(g118,g119)
    c: Coincident(g119,g120)
    c: Coincident(g120,g121)
    c: Coincident(g121,g122)
    c: Coincident(g122,g123)
    c: Coincident(g123,g124)
    c: Coincident(g124,g125)
    c: Coincident(g125,g106)
    c: Coincident(g126,g127)
    c: Coincident(g127,g128)
    c: Coincident(g128,g129)
    c: Coincident(g129,g126)
    c: Coincident(g130,g131)
    c: Coincident(g131,g132)
    c: Coincident(g132,g130)
    c: Coincident(g133,g134)
    c: Coincident(g134,g135)
    c: Coincident(g135,g136)
    c: Coincident(g136,g137)
    c: Coincident(g137,g138)
    c: Coincident(g138,g133)
    c: Coincident(g139,g140)
    c: Coincident(g140,g141)
    c: Coincident(g141,g142)
    c: Coincident(g142,g143)
    c: Coincident(g143,g144)
    c: Coincident(g144,g145)
    c: Coincident(g145,g139)
    c: Coincident(g91,g91)
    c: Coincident(g45,g45)
FEATURE [Sketcher::SketchObject] Sketch009  label="Mayor-Sketch"
  ArcFitTolerance = 1e-06
  FullyConstrained = false
  MakeInternals = false
  sketch-geometry (268):
    g0: BSplineCurve PolesCount=4 KnotsCount=2 Degree=3 IsPeriodic=0
    g1: BSplineCurve PolesCount=4 KnotsCount=2 Degree=3 IsPeriodic=0
    g2: BSplineCurve PolesCount=2 KnotsCount=2 Degree=1 IsPeriodic=0
    g3: BSplineCurve PolesCount=2 KnotsCount=2 Degree=1 IsPeriodic=0
    g4: BSplineCurve PolesCount=2 KnotsCount=2 Degree=1 IsPeriodic=0
    g5: BSplineCurve PolesCount=2 KnotsCount=2 Degree=1 IsPeriodic=0
    g6: BSplineCurve PolesCount=4 KnotsCount=2 Degree=3 IsPeriodic=0
    g7: BSplineCurve PolesCount=4 KnotsCount=2 Degree=3 IsPeriodic=0
    g8: BSplineCurve PolesCount=4 KnotsCount=2 Degree=3 IsPeriodic=0
    g9: BSplineCurve PolesCount=4 KnotsCount=2 Degree=3 IsPeriodic=0
    g10: BSplineCurve PolesCount=2 KnotsCount=2 Degree=1 IsPeriodic=0
    g11: BSplineCurve PolesCount=4 KnotsCount=2 Degree=3 IsPeriodic=0
    g12: BSplineCurve PolesCount=4 KnotsCount=2 Degree=3 IsPeriodic=0
    g13: BSplineCurve PolesCount=4 KnotsCount=2 Degree=3 IsPeriodic=0
    g14: BSplineCurve PolesCount=2 KnotsCount=2 Degree=1 IsPeriodic=0
    g15: BSplineCurve PolesCount=2 KnotsCount=2 Degree=1 IsPeriodic=0
    g16: BSplineCurve PolesCount=4 KnotsCount=2 Degree=3 IsPeriodic=0
    g17: BSplineCurve PolesCount=2 KnotsCount=2 Degree=1 IsPeriodic=0
    g18: BSplineCurve PolesCount=2 KnotsCount=2 Degree=1 IsPeriodic=0
    g19: BSplineCurve PolesCount=4 KnotsCount=2 Degree=3 IsPeriodic=0
    g20: BSplineCurve PolesCount=4 KnotsCount=2 Degree=3 IsPeriodic=0
    g21: BSplineCurve PolesCount=4 KnotsCount=2 Degree=3 IsPeriodic=0
    g22: BSplineCurve PolesCount=4 KnotsCount=2 Degree=3 IsPeriodic=0
    g23: BSplineCurve PolesCount=4 KnotsCount=2 Degree=3 IsPeriodic=0
    g24: BSplineCurve PolesCount=4 KnotsCount=2 Degree=3 IsPeriodic=0
    g25: BSplineCurve PolesCount=4 KnotsCount=2 Degree=3 IsPeriodic=0
    g26: BSplineCurve PolesCount=4 KnotsCount=2 Degree=3 IsPeriodic=0
    g27: BSplineCurve PolesCount=4 KnotsCount=2 Degree=3 IsPeriodic=0
    g28: BSplineCurve PolesCount=4 KnotsCount=2 Degree=3 IsPeriodic=0
    g29: BSplineCurve PolesCount=4 KnotsCount=2 Degree=3 IsPeriodic=0
    g30: BSplineCurve PolesCount=4 KnotsCount=2 Degree=3 IsPeriodic=0
    g31: BSplineCurve PolesCount=4 KnotsCount=2 Degree=3 IsPeriodic=0
    g32: BSplineCurve PolesCount=4 KnotsCount=2 Degree=3 IsPeriodic=0
    g33: BSplineCurve PolesCount=4 KnotsCount=2 Degree=3 IsPeriodic=0
    g34: BSplineCurve PolesCount=4 KnotsCount=2 Degree=3 IsPeriodic=0
    g35: BSplineCurve PolesCount=4 KnotsCount=2 Degree=3 IsPeriodic=0
    g36: BSplineCurve PolesCount=4 KnotsCount=2 Degree=3 IsPeriodic=0
    g37: BSplineCurve PolesCount=4 KnotsCount=2 Degree=3 IsPeriodic=0
    g38: BSplineCurve PolesCount=4 KnotsCount=2 Degree=3 IsPeriodic=0
    g39: BSplineCurve PolesCount=4 KnotsCount=2 Degree=3 IsPeriodic=0
    g40: BSplineCurve PolesCount=4 KnotsCount=2 Degree=3 IsPeriodic=0
    g41: BSplineCurve PolesCount=4 KnotsCount=2 Degree=3 IsPeriodic=0
    g42: BSplineCurve PolesCount=4 KnotsCount=2 Degree=3 IsPeriodic=0
    g43: BSplineCurve PolesCount=2 KnotsCount=2 Degree=1 IsPeriodic=0
    g44: BSplineCurve PolesCount=2 KnotsCount=2 Degree=1 IsPeriodic=0
    g45: BSplineCurve PolesCount=4 KnotsCount=2 Degree=3 IsPeriodic=0
    g46: BSplineCurve PolesCount=2 KnotsCount=2 Degree=1 IsPeriodic=0
    g47: BSplineCurve PolesCount=4 KnotsCount=2 Degree=3 IsPeriodic=0
    g48: BSplineCurve PolesCount=4 KnotsCount=2 Degree=3 IsPeriodic=0
    g49: BSplineCurve PolesCount=4 KnotsCount=2 Degree=3 IsPeriodic=0
    g50: BSplineCurve PolesCount=4 KnotsCount=2 Degree=3 IsPeriodic=0
    g51: BSplineCurve PolesCount=4 KnotsCount=2 Degree=3 IsPeriodic=0
    g52: BSplineCurve PolesCount=4 KnotsCount=2 Degree=3 IsPeriodic=0
    g53: BSplineCurve PolesCount=4 KnotsCount=2 Degree=3 IsPeriodic=0
    g54: BSplineCurve PolesCount=4 KnotsCount=2 Degree=3 IsPeriodic=0
    g55: BSplineCurve PolesCount=4 KnotsCount=2 Degree=3 IsPeriodic=0
    g56: BSplineCurve PolesCount=4 KnotsCount=2 Degree=3 IsPeriodic=0
    g57: BSplineCurve PolesCount=4 KnotsCount=2 Degree=3 IsPeriodic=0
    g58: BSplineCurve PolesCount=4 KnotsCount=2 Degree=3 IsPeriodic=0
    g59: BSplineCurve PolesCount=4 KnotsCount=2 Degree=3 IsPeriodic=0
    g60: BSplineCurve PolesCount=4 KnotsCount=2 Degree=3 IsPeriodic=0
    g61: BSplineCurve PolesCount=4 KnotsCount=2 Degree=3 IsPeriodic=0
    g62: BSplineCurve PolesCount=4 KnotsCount=2 Degree=3 IsPeriodic=0
    g63: BSplineCurve PolesCount=4 KnotsCount=2 Degree=3 IsPeriodic=0
    g64: BSplineCurve PolesCount=4 KnotsCount=2 Degree=3 IsPeriodic=0
    g65: BSplineCurve PolesCount=4 KnotsCount=2 Degree=3 IsPeriodic=0
    g66: BSplineCurve PolesCount=4 KnotsCount=2 Degree=3 IsPeriodic=0
    g67: BSplineCurve PolesCount=4 KnotsCount=2 Degree=3 IsPeriodic=0
    g68: BSplineCurve PolesCount=4 KnotsCount=2 Degree=3 IsPeriodic=0
    g69: BSplineCurve PolesCount=4 KnotsCount=2 Degree=3 IsPeriodic=0
    g70: BSplineCurve PolesCount=4 KnotsCount=2 Degree=3 IsPeriodic=0
    g71: BSplineCurve PolesCount=4 KnotsCount=2 Degree=3 IsPeriodic=0
    g72: BSplineCurve PolesCount=4 KnotsCount=2 Degree=3 IsPeriodic=0
    g73: BSplineCurve PolesCount=4 KnotsCount=2 Degree=3 IsPeriodic=0
    g74: BSplineCurve PolesCount=4 KnotsCount=2 Degree=3 IsPeriodic=0
    g75: BSplineCurve PolesCount=4 KnotsCount=2 Degree=3 IsPeriodic=0
    g76: BSplineCurve PolesCount=4 KnotsCount=2 Degree=3 IsPeriodic=0
    g77: BSplineCurve PolesCount=4 KnotsCount=2 Degree=3 IsPeriodic=0
    g78: BSplineCurve PolesCount=4 KnotsCount=2 Degree=3 IsPeriodic=0
    g79: BSplineCurve PolesCount=2 KnotsCount=2 Degree=1 IsPeriodic=0
    g80: BSplineCurve PolesCount=2 KnotsCount=2 Degree=1 IsPeriodic=0
    g81: BSplineCurve PolesCount=2 KnotsCount=2 Degree=1 IsPeriodic=0
    g82: BSplineCurve PolesCount=2 KnotsCount=2 Degree=1 IsPeriodic=0
    g83: BSplineCurve PolesCount=4 KnotsCount=2 Degree=3 IsPeriodic=0
    g84: BSplineCurve PolesCount=4 KnotsCount=2 Degree=3 IsPeriodic=0
    g85: BSplineCurve PolesCount=4 KnotsCount=2 Degree=3 IsPeriodic=0
    g86: BSplineCurve PolesCount=2 KnotsCount=2 Degree=1 IsPeriodic=0
    g87: BSplineCurve PolesCount=4 KnotsCount=2 Degree=3 IsPeriodic=0
    g88: BSplineCurve PolesCount=4 KnotsCount=2 Degree=3 IsPeriodic=0
    g89: BSplineCurve PolesCount=4 KnotsCount=2 Degree=3 IsPeriodic=0
    g90: BSplineCurve PolesCount=4 KnotsCount=2 Degree=3 IsPeriodic=0
    g91: BSplineCurve PolesCount=4 KnotsCount=2 Degree=3 IsPeriodic=0
    g92: BSplineCurve PolesCount=4 KnotsCount=2 Degree=3 IsPeriodic=0
    g93: BSplineCurve PolesCount=2 KnotsCount=2 Degree=1 IsPeriodic=0
    g94: BSplineCurve PolesCount=2 KnotsCount=2 Degree=1 IsPeriodic=0
    g95: BSplineCurve PolesCount=4 KnotsCount=2 Degree=3 IsPeriodic=0
    g96: BSplineCurve PolesCount=4 KnotsCount=2 Degree=3 IsPeriodic=0
    g97: BSplineCurve PolesCount=4 KnotsCount=2 Degree=3 IsPeriodic=0
    g98: BSplineCurve PolesCount=4 KnotsCount=2 Degree=3 IsPeriodic=0
    g99: BSplineCurve PolesCount=4 KnotsCount=2 Degree=3 IsPeriodic=0
    g100: BSplineCurve PolesCount=4 KnotsCount=2 Degree=3 IsPeriodic=0
    g101: BSplineCurve PolesCount=4 KnotsCount=2 Degree=3 IsPeriodic=0
    g102: BSplineCurve PolesCount=4 KnotsCount=2 Degree=3 IsPeriodic=0
    g103: BSplineCurve PolesCount=4 KnotsCount=2 Degree=3 IsPeriodic=0
    g104: BSplineCurve PolesCount=4 KnotsCount=2 Degree=3 IsPeriodic=0
    g105: BSplineCurve PolesCount=4 KnotsCount=2 Degree=3 IsPeriodic=0
    g106: BSplineCurve PolesCount=4 KnotsCount=2 Degree=3 IsPeriodic=0
    g107: BSplineCurve PolesCount=2 KnotsCount=2 Degree=1 IsPeriodic=0
    g108: BSplineCurve PolesCount=2 KnotsCount=2 Degree=1 IsPeriodic=0
    g109: BSplineCurve PolesCount=2 KnotsCount=2 Degree=1 IsPeriodic=0
    g110: BSplineCurve PolesCount=2 KnotsCount=2 Degree=1 IsPeriodic=0
    g111: BSplineCurve PolesCount=4 KnotsCount=2 Degree=3 IsPeriodic=0
    g112: BSplineCurve PolesCount=4 KnotsCount=2 Degree=3 IsPeriodic=0
    g113: BSplineCurve PolesCount=4 KnotsCount=2 Degree=3 IsPeriodic=0
    g114: BSplineCurve PolesCount=4 KnotsCount=2 Degree=3 IsPeriodic=0
    g115: BSplineCurve PolesCount=4 KnotsCount=2 Degree=3 IsPeriodic=0
    g116: BSplineCurve PolesCount=4 KnotsCount=2 Degree=3 IsPeriodic=0
    g117: BSplineCurve PolesCount=4 KnotsCount=2 Degree=3 IsPeriodic=0
    g118: BSplineCurve PolesCount=4 KnotsCount=2 Degree=3 IsPeriodic=0
    g119: BSplineCurve PolesCount=4 KnotsCount=2 Degree=3 IsPeriodic=0
    g120: BSplineCurve PolesCount=2 KnotsCount=2 Degree=1 IsPeriodic=0
    g121: BSplineCurve PolesCount=2 KnotsCount=2 Degree=1 IsPeriodic=0
    g122: BSplineCurve PolesCount=4 KnotsCount=2 Degree=3 IsPeriodic=0
    g123: BSplineCurve PolesCount=2 KnotsCount=2 Degree=1 IsPeriodic=0
    g124: BSplineCurve PolesCount=4 KnotsCount=2 Degree=3 IsPeriodic=0
    g125: BSplineCurve PolesCount=4 KnotsCount=2 Degree=3 IsPeriodic=0
    g126: BSplineCurve PolesCount=4 KnotsCount=2 Degree=3 IsPeriodic=0
    g127: BSplineCurve PolesCount=4 KnotsCount=2 Degree=3 IsPeriodic=0
    g128: BSplineCurve PolesCount=4 KnotsCount=2 Degree=3 IsPeriodic=0
    g129: BSplineCurve PolesCount=4 KnotsCount=2 Degree=3 IsPeriodic=0
    g130: BSplineCurve PolesCount=4 KnotsCount=2 Degree=3 IsPeriodic=0
    g131: BSplineCurve PolesCount=4 KnotsCount=2 Degree=3 IsPeriodic=0
    g132: BSplineCurve PolesCount=4 KnotsCount=2 Degree=3 IsPeriodic=0
    g133: BSplineCurve PolesCount=4 KnotsCount=2 Degree=3 IsPeriodic=0
    g134: BSplineCurve PolesCount=4 KnotsCount=2 Degree=3 IsPeriodic=0
    g135: BSplineCurve PolesCount=4 KnotsCount=2 Degree=3 IsPeriodic=0
    g136: BSplineCurve PolesCount=4 KnotsCount=2 Degree=3 IsPeriodic=0
    g137: BSplineCurve PolesCount=4 KnotsCount=2 Degree=3 IsPeriodic=0
    g138: BSplineCurve PolesCount=4 KnotsCount=2 Degree=3 IsPeriodic=0
    g139: BSplineCurve PolesCount=4 KnotsCount=2 Degree=3 IsPeriodic=0
    g140: BSplineCurve PolesCount=4 KnotsCount=2 Degree=3 IsPeriodic=0
    g141: BSplineCurve PolesCount=4 KnotsCount=2 Degree=3 IsPeriodic=0
    g142: BSplineCurve PolesCount=4 KnotsCount=2 Degree=3 IsPeriodic=0
    g143: BSplineCurve PolesCount=4 KnotsCount=2 Degree=3 IsPeriodic=0
    g144: BSplineCurve PolesCount=4 KnotsCount=2 Degree=3 IsPeriodic=0
    g145: BSplineCurve PolesCount=4 KnotsCount=2 Degree=3 IsPeriodic=0
    g146: BSplineCurve PolesCount=4 KnotsCount=2 Degree=3 IsPeriodic=0
    g147: BSplineCurve PolesCount=4 KnotsCount=2 Degree=3 IsPeriodic=0
    g148: BSplineCurve PolesCount=2 KnotsCount=2 Degree=1 IsPeriodic=0
    g149: BSplineCurve PolesCount=2 KnotsCount=2 Degree=1 IsPeriodic=0
    g150: BSplineCurve PolesCount=4 KnotsCount=2 Degree=3 IsPeriodic=0
    g151: BSplineCurve PolesCount=4 KnotsCount=2 Degree=3 IsPeriodic=0
    g152: BSplineCurve PolesCount=4 KnotsCount=2 Degree=3 IsPeriodic=0
    g153: BSplineCurve PolesCount=4 KnotsCount=2 Degree=3 IsPeriodic=0
    g154: BSplineCurve PolesCount=4 KnotsCount=2 Degree=3 IsPeriodic=0
    g155: BSplineCurve PolesCount=4 KnotsCount=2 Degree=3 IsPeriodic=0
    g156: BSplineCurve PolesCount=4 KnotsCount=2 Degree=3 IsPeriodic=0
    g157: BSplineCurve PolesCount=4 KnotsCount=2 Degree=3 IsPeriodic=0
    g158: BSplineCurve PolesCount=2 KnotsCount=2 Degree=1 IsPeriodic=0
    g159: BSplineCurve PolesCount=2 KnotsCount=2 Degree=1 IsPeriodic=0
    g160: BSplineCurve PolesCount=4 KnotsCount=2 Degree=3 IsPeriodic=0
    g161: BSplineCurve PolesCount=2 KnotsCount=2 Degree=1 IsPeriodic=0
    g162: BSplineCurve PolesCount=4 KnotsCount=2 Degree=3 IsPeriodic=0
    g163: BSplineCurve PolesCount=4 KnotsCount=2 Degree=3 IsPeriodic=0
    g164: BSplineCurve PolesCount=4 KnotsCount=2 Degree=3 IsPeriodic=0
    g165: BSplineCurve PolesCount=4 KnotsCount=2 Degree=3 IsPeriodic=0
    g166: BSplineCurve PolesCount=4 KnotsCount=2 Degree=3 IsPeriodic=0
    g167: BSplineCurve PolesCount=4 KnotsCount=2 Degree=3 IsPeriodic=0
    g168: BSplineCurve PolesCount=4 KnotsCount=2 Degree=3 IsPeriodic=0
    g169: BSplineCurve PolesCount=4 KnotsCount=2 Degree=3 IsPeriodic=0
    g170: BSplineCurve PolesCount=4 KnotsCount=2 Degree=3 IsPeriodic=0
    g171: BSplineCurve PolesCount=4 KnotsCount=2 Degree=3 IsPeriodic=0
    g172: BSplineCurve PolesCount=4 KnotsCount=2 Degree=3 IsPeriodic=0
    g173: BSplineCurve PolesCount=4 KnotsCount=2 Degree=3 IsPeriodic=0
    g174: BSplineCurve PolesCount=4 KnotsCount=2 Degree=3 IsPeriodic=0
    g175: BSplineCurve PolesCount=2 KnotsCount=2 Degree=1 IsPeriodic=0
    g176: BSplineCurve PolesCount=2 KnotsCount=2 Degree=1 IsPeriodic=0
    g177: BSplineCurve PolesCount=2 KnotsCount=2 Degree=1 IsPeriodic=0
    g178: BSplineCurve PolesCount=4 KnotsCount=2 Degree=3 IsPeriodic=0
    g179: BSplineCurve PolesCount=2 KnotsCount=2 Degree=1 IsPeriodic=0
    g180: BSplineCurve PolesCount=2 KnotsCount=2 Degree=1 IsPeriodic=0
    g181: BSplineCurve PolesCount=4 KnotsCount=2 Degree=3 IsPeriodic=0
    g182: BSplineCurve PolesCount=4 KnotsCount=2 Degree=3 IsPeriodic=0
    g183: BSplineCurve PolesCount=4 KnotsCount=2 Degree=3 IsPeriodic=0
    g184: BSplineCurve PolesCount=4 KnotsCount=2 Degree=3 IsPeriodic=0
    g185: BSplineCurve PolesCount=2 KnotsCount=2 Degree=1 IsPeriodic=0
    g186: BSplineCurve PolesCount=2 KnotsCount=2 Degree=1 IsPeriodic=0
    g187: BSplineCurve PolesCount=4 KnotsCount=2 Degree=3 IsPeriodic=0
    g188: BSplineCurve PolesCount=2 KnotsCount=2 Degree=1 IsPeriodic=0
    g189: BSplineCurve PolesCount=2 KnotsCount=2 Degree=1 IsPeriodic=0
    g190: BSplineCurve PolesCount=4 KnotsCount=2 Degree=3 IsPeriodic=0
    g191: BSplineCurve PolesCount=4 KnotsCount=2 Degree=3 IsPeriodic=0
    g192: BSplineCurve PolesCount=4 KnotsCount=2 Degree=3 IsPeriodic=0
    g193: BSplineCurve PolesCount=4 KnotsCount=2 Degree=3 IsPeriodic=0
    g194: BSplineCurve PolesCount=4 KnotsCount=2 Degree=3 IsPeriodic=0
    g195: BSplineCurve PolesCount=4 KnotsCount=2 Degree=3 IsPeriodic=0
    g196: BSplineCurve PolesCount=4 KnotsCount=2 Degree=3 IsPeriodic=0
    g197: BSplineCurve PolesCount=2 KnotsCount=2 Degree=1 IsPeriodic=0
    g198: BSplineCurve PolesCount=2 KnotsCount=2 Degree=1 IsPeriodic=0
    g199: BSplineCurve PolesCount=4 KnotsCount=2 Degree=3 IsPeriodic=0
    g200: BSplineCurve PolesCount=2 KnotsCount=2 Degree=1 IsPeriodic=0
    g201: BSplineCurve PolesCount=2 KnotsCount=2 Degree=1 IsPeriodic=0
    g202: BSplineCurve PolesCount=4 KnotsCount=2 Degree=3 IsPeriodic=0
    g203: BSplineCurve PolesCount=2 KnotsCount=2 Degree=1 IsPeriodic=0
    g204: BSplineCurve PolesCount=2 KnotsCount=2 Degree=1 IsPeriodic=0
    g205: BSplineCurve PolesCount=4 KnotsCount=2 Degree=3 IsPeriodic=0
    g206: BSplineCurve PolesCount=4 KnotsCount=2 Degree=3 IsPeriodic=0
    g207: BSplineCurve PolesCount=4 KnotsCount=2 Degree=3 IsPeriodic=0
    g208: BSplineCurve PolesCount=4 KnotsCount=2 Degree=3 IsPeriodic=0
    g209: BSplineCurve PolesCount=2 KnotsCount=2 Degree=1 IsPeriodic=0
    g210: BSplineCurve PolesCount=2 KnotsCount=2 Degree=1 IsPeriodic=0
    g211: BSplineCurve PolesCount=4 KnotsCount=2 Degree=3 IsPeriodic=0
    g212: BSplineCurve PolesCount=4 KnotsCount=2 Degree=3 IsPeriodic=0
    g213: BSplineCurve PolesCount=4 KnotsCount=2 Degree=3 IsPeriodic=0
    g214: BSplineCurve PolesCount=2 KnotsCount=2 Degree=1 IsPeriodic=0
    g215: BSplineCurve PolesCount=2 KnotsCount=2 Degree=1 IsPeriodic=0
    g216: BSplineCurve PolesCount=2 KnotsCount=2 Degree=1 IsPeriodic=0
    g217: BSplineCurve PolesCount=2 KnotsCount=2 Degree=1 IsPeriodic=0
    g218: BSplineCurve PolesCount=4 KnotsCount=2 Degree=3 IsPeriodic=0
    g219: BSplineCurve PolesCount=4 KnotsCount=2 Degree=3 IsPeriodic=0
    g220: BSplineCurve PolesCount=2 KnotsCount=2 Degree=1 IsPeriodic=0
    g221: BSplineCurve PolesCount=2 KnotsCount=2 Degree=1 IsPeriodic=0
    g222: BSplineCurve PolesCount=4 KnotsCount=2 Degree=3 IsPeriodic=0
    g223: BSplineCurve PolesCount=2 KnotsCount=2 Degree=1 IsPeriodic=0
    g224: BSplineCurve PolesCount=4 KnotsCount=2 Degree=3 IsPeriodic=0
    g225: BSplineCurve PolesCount=4 KnotsCount=2 Degree=3 IsPeriodic=0
    g226: BSplineCurve PolesCount=4 KnotsCount=2 Degree=3 IsPeriodic=0
    g227: BSplineCurve PolesCount=4 KnotsCount=2 Degree=3 IsPeriodic=0
    g228: BSplineCurve PolesCount=4 KnotsCount=2 Degree=3 IsPeriodic=0
    g229: BSplineCurve PolesCount=4 KnotsCount=2 Degree=3 IsPeriodic=0
    g230: BSplineCurve PolesCount=4 KnotsCount=2 Degree=3 IsPeriodic=0
    g231: BSplineCurve PolesCount=4 KnotsCount=2 Degree=3 IsPeriodic=0
    g232: BSplineCurve PolesCount=4 KnotsCount=2 Degree=3 IsPeriodic=0
    g233: BSplineCurve PolesCount=4 KnotsCount=2 Degree=3 IsPeriodic=0
    g234: BSplineCurve PolesCount=4 KnotsCount=2 Degree=3 IsPeriodic=0
    g235: BSplineCurve PolesCount=4 KnotsCount=2 Degree=3 IsPeriodic=0
    g236: BSplineCurve PolesCount=2 KnotsCount=2 Degree=1 IsPeriodic=0
    g237: BSplineCurve PolesCount=2 KnotsCount=2 Degree=1 IsPeriodic=0
    g238: BSplineCurve PolesCount=2 KnotsCount=2 Degree=1 IsPeriodic=0
    g239: BSplineCurve PolesCount=2 KnotsCount=2 Degree=1 IsPeriodic=0
    g240: BSplineCurve PolesCount=4 KnotsCount=2 Degree=3 IsPeriodic=0
    g241: BSplineCurve PolesCount=2 KnotsCount=2 Degree=1 IsPeriodic=0
    g242: BSplineCurve PolesCount=2 KnotsCount=2 Degree=1 IsPeriodic=0
    g243: BSplineCurve PolesCount=4 KnotsCount=2 Degree=3 IsPeriodic=0
    g244: BSplineCurve PolesCount=2 KnotsCount=2 Degree=1 IsPeriodic=0
    g245: BSplineCurve PolesCount=4 KnotsCount=2 Degree=3 IsPeriodic=0
    g246: BSplineCurve PolesCount=4 KnotsCount=2 Degree=3 IsPeriodic=0
    g247: BSplineCurve PolesCount=4 KnotsCount=2 Degree=3 IsPeriodic=0
    g248: BSplineCurve PolesCount=4 KnotsCount=2 Degree=3 IsPeriodic=0
    g249: BSplineCurve PolesCount=2 KnotsCount=2 Degree=1 IsPeriodic=0
    g250: BSplineCurve PolesCount=2 KnotsCount=2 Degree=1 IsPeriodic=0
    g251: BSplineCurve PolesCount=4 KnotsCount=2 Degree=3 IsPeriodic=0
    g252: BSplineCurve PolesCount=2 KnotsCount=2 Degree=1 IsPeriodic=0
    g253: BSplineCurve PolesCount=2 KnotsCount=2 Degree=1 IsPeriodic=0
    g254: BSplineCurve PolesCount=2 KnotsCount=2 Degree=1 IsPeriodic=0
    g255: BSplineCurve PolesCount=2 KnotsCount=2 Degree=1 IsPeriodic=0
    g256: BSplineCurve PolesCount=2 KnotsCount=2 Degree=1 IsPeriodic=0
    g257: BSplineCurve PolesCount=2 KnotsCount=2 Degree=1 IsPeriodic=0
    g258: BSplineCurve PolesCount=4 KnotsCount=2 Degree=3 IsPeriodic=0
    g259: BSplineCurve PolesCount=4 KnotsCount=2 Degree=3 IsPeriodic=0
    g260: BSplineCurve PolesCount=4 KnotsCount=2 Degree=3 IsPeriodic=0
    g261: BSplineCurve PolesCount=4 KnotsCount=2 Degree=3 IsPeriodic=0
    g262: BSplineCurve PolesCount=4 KnotsCount=2 Degree=3 IsPeriodic=0
    g263: BSplineCurve PolesCount=4 KnotsCount=2 Degree=3 IsPeriodic=0
    g264: BSplineCurve PolesCount=4 KnotsCount=2 Degree=3 IsPeriodic=0
    g265: BSplineCurve PolesCount=4 KnotsCount=2 Degree=3 IsPeriodic=0
    g266: BSplineCurve PolesCount=4 KnotsCount=2 Degree=3 IsPeriodic=0
    g267: BSplineCurve PolesCount=2 KnotsCount=2 Degree=1 IsPeriodic=0
  constraints (277):
    c: Coincident(g0,g1)
    c: Coincident(g1,g2)
    c: Coincident(g2,g3)
    c: Coincident(g3,g4)
    c: Coincident(g4,g5)
    c: Coincident(g5,g6)
    c: Coincident(g6,g7)
    c: Coincident(g7,g8)
    c: Coincident(g8,g9)
    c: Coincident(g9,g10)
    c: Coincident(g10,g0)
    c: Coincident(g11,g12)
    c: Coincident(g12,g13)
    c: Coincident(g13,g14)
    c: Coincident(g14,g15)
    c: Coincident(g15,g16)
    c: Coincident(g16,g17)
    c: Coincident(g17,g18)
    c: Coincident(g18,g11)
    c: Coincident(g19,g20)
    c: Coincident(g20,g21)
    c: Coincident(g21,g22)
    c: Coincident(g22,g23)
    c: Coincident(g23,g24)
    c: Coincident(g24,g25)
    c: Coincident(g25,g26)
    c: Coincident(g26,g27)
    c: Coincident(g27,g28)
    c: Coincident(g28,g29)
    c: Coincident(g29,g30)
    c: Coincident(g30,g31)
    c: Coincident(g31,g32)
    c: Coincident(g32,g33)
    c: Coincident(g33,g34)
    c: Coincident(g34,g35)
    c: Coincident(g35,g36)
    c: Coincident(g36,g37)
    c: Coincident(g37,g38)
    c: Coincident(g38,g39)
    c: Coincident(g39,g40)
    c: Coincident(g40,g41)
    c: Coincident(g41,g42)
    c: Coincident(g42,g43)
    c: Coincident(g43,g44)
    c: Coincident(g44,g45)
    c: Coincident(g45,g19)
    c: Coincident(g46,g47)
    c: Coincident(g47,g48)
    c: Coincident(g48,g49)
    c: Coincident(g49,g50)
    c: Coincident(g50,g51)
    c: Coincident(g51,g52)
    c: Coincident(g52,g53)
    c: Coincident(g53,g54)
    c: Coincident(g54,g55)
    c: Coincident(g55,g56)
    c: Coincident(g56,g57)
    c: Coincident(g57,g58)
    c: Coincident(g58,g59)
    c: Coincident(g59,g60)
    c: Coincident(g60,g61)
    c: Coincident(g61,g62)
    c: Coincident(g62,g46)
    c: Coincident(g63,g64)
    c: Coincident(g64,g65)
    c: Coincident(g65,g66)
    c: Coincident(g66,g67)
    c: Coincident(g67,g68)
    c: Coincident(g68,g69)
    c: Coincident(g69,g70)
    c: Coincident(g70,g71)
    c: Coincident(g71,g72)
    c: Coincident(g72,g73)
    c: Coincident(g73,g74)
    c: Coincident(g74,g75)
    c: Coincident(g75,g76)
    c: Coincident(g76,g77)
    c: Coincident(g77,g78)
    c: Coincident(g78,g79)
    c: Coincident(g79,g80)
    c: Coincident(g80,g81)
    c: Coincident(g81,g82)
    c: Coincident(g82,g63)
    c: Coincident(g83,g84)
    c: Coincident(g84,g85)
    c: Coincident(g85,g83)
    c: Coincident(g86,g87)
    c: Coincident(g87,g88)
    c: Coincident(g88,g89)
    c: Coincident(g89,g90)
    c: Coincident(g90,g91)
    c: Coincident(g91,g92)
    c: Coincident(g92,g93)
    c: Coincident(g93,g94)
    c: Coincident(g94,g95)
    c: Coincident(g95,g96)
    c: Coincident(g96,g97)
    c: Coincident(g97,g98)
    c: Coincident(g98,g99)
    c: Coincident(g99,g86)
    c: Coincident(g100,g101)
    c: Coincident(g101,g102)
    c: Coincident(g102,g103)
    c: Coincident(g103,g104)
    c: Coincident(g104,g105)
    c: Coincident(g105,g106)
    c: Coincident(g106,g107)
    c: Coincident(g107,g108)
    c: Coincident(g108,g109)
    c: Coincident(g109,g110)
    c: Coincident(g110,g111)
    c: Coincident(g111,g112)
    c: Coincident(g112,g113)
    c: Coincident(g113,g114)
    c: Coincident(g114,g115)
    c: Coincident(g115,g116)
    c: Coincident(g116,g117)
    c: Coincident(g117,g118)
    c: Coincident(g118,g119)
    c: Coincident(g119,g120)
    c: Coincident(g120,g121)
    c: Coincident(g121,g122)
    c: Coincident(g122,g123)
    c: Coincident(g123,g100)
    c: Coincident(g124,g125)
    c: Coincident(g125,g126)
    c: Coincident(g126,g127)
    c: Coincident(g127,g128)
    c: Coincident(g128,g129)
    c: Coincident(g129,g130)
    c: Coincident(g130,g131)
    c: Coincident(g131,g132)
    c: Coincident(g132,g133)
    c: Coincident(g133,g134)
    c: Coincident(g134,g135)
    c: Coincident(g135,g136)
    c: Coincident(g136,g137)
    c: Coincident(g137,g124)
    c: Coincident(g138,g139)
    c: Coincident(g139,g140)
    c: Coincident(g140,g141)
    c: Coincident(g141,g142)
    c: Coincident(g142,g143)
    c: Coincident(g143,g144)
    c: Coincident(g144,g145)
    c: Coincident(g145,g146)
    c: Coincident(g146,g147)
    c: Coincident(g147,g148)
    c: Coincident(g148,g149)
    c: Coincident(g149,g150)
    c: Coincident(g150,g151)
    c: Coincident(g151,g152)
    c: Coincident(g152,g153)
    c: Coincident(g153,g154)
    c: Coincident(g154,g155)
    c: Coincident(g155,g156)
    c: Coincident(g156,g157)
    c: Coincident(g157,g158)
    c: Coincident(g158,g159)
    c: Coincident(g159,g160)
    c: Coincident(g160,g161)
    c: Coincident(g161,g138)
    c: Coincident(g162,g163)
    c: Coincident(g163,g164)
    c: Coincident(g164,g165)
    c: Coincident(g165,g166)
    c: Coincident(g166,g167)
    c: Coincident(g167,g168)
    c: Coincident(g168,g169)
    c: Coincident(g169,g170)
    c: Coincident(g170,g171)
    c: Coincident(g171,g172)
    c: Coincident(g172,g173)
    c: Coincident(g173,g174)
    c: Coincident(g174,g162)
    c: Coincident(g175,g176)
    c: Coincident(g176,g177)
    c: Coincident(g177,g178)
    c: Coincident(g178,g179)
    c: Coincident(g179,g180)
    c: Coincident(g180,g181)
    c: Coincident(g181,g175)
    c: Coincident(g182,g183)
    c: Coincident(g183,g184)
    c: Coincident(g184,g182)
    c: Coincident(g185,g186)
    c: Coincident(g186,g187)
    c: Coincident(g187,g188)
    c: Coincident(g188,g189)
    c: Coincident(g189,g190)
    c: Coincident(g190,g191)
    c: Coincident(g191,g192)
    c: Coincident(g192,g193)
    c: Coincident(g193,g194)
    c: Coincident(g194,g195)
    c: Coincident(g195,g196)
    c: Coincident(g196,g197)
    c: Coincident(g197,g198)
    c: Coincident(g198,g199)
    c: Coincident(g199,g200)
    c: Coincident(g200,g201)
    c: Coincident(g201,g202)
    c: Coincident(g202,g185)
    c: Coincident(g203,g204)
    c: Coincident(g204,g205)
    c: Coincident(g205,g206)
    c: Coincident(g206,g207)
    c: Coincident(g207,g208)
    c: Coincident(g208,g209)
    c: Coincident(g209,g210)
    c: Coincident(g210,g211)
    c: Coincident(g211,g212)
    c: Coincident(g212,g213)
    c: Coincident(g213,g214)
    c: Coincident(g214,g215)
    c: Coincident(g215,g216)
    c: Coincident(g216,g217)
    c: Coincident(g217,g218)
    c: Coincident(g218,g219)
    c: Coincident(g219,g220)
    c: Coincident(g220,g221)
    c: Coincident(g221,g222)
    c: Coincident(g222,g223)
    c: Coincident(g223,g203)
    c: Coincident(g224,g225)
    c: Coincident(g225,g226)
    c: Coincident(g226,g227)
    c: Coincident(g227,g228)
    c: Coincident(g228,g229)
    c: Coincident(g229,g230)
    c: Coincident(g230,g231)
    c: Coincident(g231,g224)
    c: Coincident(g232,g233)
    c: Coincident(g233,g234)
    c: Coincident(g234,g235)
    c: Coincident(g235,g236)
    c: Coincident(g236,g237)
    c: Coincident(g237,g238)
    c: Coincident(g238,g239)
    c: Coincident(g239,g240)
    c: Coincident(g240,g241)
    c: Coincident(g241,g242)
    c: Coincident(g242,g243)
    c: Coincident(g243,g244)
    c: Coincident(g244,g232)
    c: Coincident(g245,g246)
    c: Coincident(g246,g247)
    c: Coincident(g247,g248)
    c: Coincident(g248,g249)
    c: Coincident(g249,g250)
    c: Coincident(g250,g251)
    c: Coincident(g251,g252)
    c: Coincident(g252,g253)
    c: Coincident(g253,g254)
    c: Coincident(g254,g255)
    c: Coincident(g255,g245)
    c: Coincident(g256,g257)
    c: Coincident(g257,g258)
    c: Coincident(g258,g259)
    c: Coincident(g259,g260)
    c: Coincident(g260,g261)
    c: Coincident(g261,g262)
    c: Coincident(g262,g263)
    c: Coincident(g263,g264)
    c: Coincident(g264,g265)
    c: Coincident(g265,g266)
    c: Coincident(g266,g267)
    c: Coincident(g267,g256)
    c: Coincident(g222,g203)
    c: Coincident(g9,g0)
    c: Coincident(g160,g138)
    c: Coincident(g175,g175)
    c: Coincident(g266,g256)
    c: Coincident(g122,g100)
    c: Coincident(g86,g86)
    c: Coincident(g243,g232)
    c: Coincident(g46,g46)
FEATURE [Sketcher::SketchObject] Sketch010  label="Monk-Sketch"
  ArcFitTolerance = 1e-06
  FullyConstrained = false
  MakeInternals = false
  sketch-geometry (271):
    g0: BSplineCurve PolesCount=4 KnotsCount=2 Degree=3 IsPeriodic=0
    g1: BSplineCurve PolesCount=4 KnotsCount=2 Degree=3 IsPeriodic=0
    g2: BSplineCurve PolesCount=4 KnotsCount=2 Degree=3 IsPeriodic=0
    g3: BSplineCurve PolesCount=4 KnotsCount=2 Degree=3 IsPeriodic=0
    g4: BSplineCurve PolesCount=4 KnotsCount=2 Degree=3 IsPeriodic=0
    g5: BSplineCurve PolesCount=4 KnotsCount=2 Degree=3 IsPeriodic=0
    g6: BSplineCurve PolesCount=4 KnotsCount=2 Degree=3 IsPeriodic=0
    g7: BSplineCurve PolesCount=4 KnotsCount=2 Degree=3 IsPeriodic=0
    g8: BSplineCurve PolesCount=4 KnotsCount=2 Degree=3 IsPeriodic=0
    g9: BSplineCurve PolesCount=4 KnotsCount=2 Degree=3 IsPeriodic=0
    g10: BSplineCurve PolesCount=4 KnotsCount=2 Degree=3 IsPeriodic=0
    g11: BSplineCurve PolesCount=4 KnotsCount=2 Degree=3 IsPeriodic=0
    g12: BSplineCurve PolesCount=4 KnotsCount=2 Degree=3 IsPeriodic=0
    g13: BSplineCurve PolesCount=4 KnotsCount=2 Degree=3 IsPeriodic=0
    g14: BSplineCurve PolesCount=4 KnotsCount=2 Degree=3 IsPeriodic=0
    g15: BSplineCurve PolesCount=4 KnotsCount=2 Degree=3 IsPeriodic=0
    g16: BSplineCurve PolesCount=4 KnotsCount=2 Degree=3 IsPeriodic=0
    g17: BSplineCurve PolesCount=4 KnotsCount=2 Degree=3 IsPeriodic=0
    g18: BSplineCurve PolesCount=4 KnotsCount=2 Degree=3 IsPeriodic=0
    g19: BSplineCurve PolesCount=4 KnotsCount=2 Degree=3 IsPeriodic=0
    g20: BSplineCurve PolesCount=4 KnotsCount=2 Degree=3 IsPeriodic=0
    g21: BSplineCurve PolesCount=4 KnotsCount=2 Degree=3 IsPeriodic=0
    g22: BSplineCurve PolesCount=4 KnotsCount=2 Degree=3 IsPeriodic=0
    g23: BSplineCurve PolesCount=4 KnotsCount=2 Degree=3 IsPeriodic=0
    g24: BSplineCurve PolesCount=4 KnotsCount=2 Degree=3 IsPeriodic=0
    g25: BSplineCurve PolesCount=4 KnotsCount=2 Degree=3 IsPeriodic=0
    g26: BSplineCurve PolesCount=4 KnotsCount=2 Degree=3 IsPeriodic=0
    g27: BSplineCurve PolesCount=4 KnotsCount=2 Degree=3 IsPeriodic=0
    g28: BSplineCurve PolesCount=4 KnotsCount=2 Degree=3 IsPeriodic=0
    g29: BSplineCurve PolesCount=4 KnotsCount=2 Degree=3 IsPeriodic=0
    g30: BSplineCurve PolesCount=4 KnotsCount=2 Degree=3 IsPeriodic=0
    g31: BSplineCurve PolesCount=4 KnotsCount=2 Degree=3 IsPeriodic=0
    g32: BSplineCurve PolesCount=4 KnotsCount=2 Degree=3 IsPeriodic=0
    g33: BSplineCurve PolesCount=4 KnotsCount=2 Degree=3 IsPeriodic=0
    g34: BSplineCurve PolesCount=4 KnotsCount=2 Degree=3 IsPeriodic=0
    g35: BSplineCurve PolesCount=4 KnotsCount=2 Degree=3 IsPeriodic=0
    g36: BSplineCurve PolesCount=4 KnotsCount=2 Degree=3 IsPeriodic=0
    g37: BSplineCurve PolesCount=4 KnotsCount=2 Degree=3 IsPeriodic=0
    g38: BSplineCurve PolesCount=4 KnotsCount=2 Degree=3 IsPeriodic=0
    g39: BSplineCurve PolesCount=4 KnotsCount=2 Degree=3 IsPeriodic=0
    g40: BSplineCurve PolesCount=4 KnotsCount=2 Degree=3 IsPeriodic=0
    g41: BSplineCurve PolesCount=4 KnotsCount=2 Degree=3 IsPeriodic=0
    g42: BSplineCurve PolesCount=4 KnotsCount=2 Degree=3 IsPeriodic=0
    g43: BSplineCurve PolesCount=4 KnotsCount=2 Degree=3 IsPeriodic=0
    g44: BSplineCurve PolesCount=4 KnotsCount=2 Degree=3 IsPeriodic=0
    g45: BSplineCurve PolesCount=4 KnotsCount=2 Degree=3 IsPeriodic=0
    g46: BSplineCurve PolesCount=2 KnotsCount=2 Degree=1 IsPeriodic=0
    g47: BSplineCurve PolesCount=2 KnotsCount=2 Degree=1 IsPeriodic=0
    g48: BSplineCurve PolesCount=4 KnotsCount=2 Degree=3 IsPeriodic=0
    g49: BSplineCurve PolesCount=4 KnotsCount=2 Degree=3 IsPeriodic=0
    g50: BSplineCurve PolesCount=4 KnotsCount=2 Degree=3 IsPeriodic=0
    g51: BSplineCurve PolesCount=4 KnotsCount=2 Degree=3 IsPeriodic=0
    g52: BSplineCurve PolesCount=4 KnotsCount=2 Degree=3 IsPeriodic=0
    g53: BSplineCurve PolesCount=4 KnotsCount=2 Degree=3 IsPeriodic=0
    g54: BSplineCurve PolesCount=4 KnotsCount=2 Degree=3 IsPeriodic=0
    g55: BSplineCurve PolesCount=4 KnotsCount=2 Degree=3 IsPeriodic=0
    g56: BSplineCurve PolesCount=4 KnotsCount=2 Degree=3 IsPeriodic=0
    g57: BSplineCurve PolesCount=4 KnotsCount=2 Degree=3 IsPeriodic=0
    g58: BSplineCurve PolesCount=4 KnotsCount=2 Degree=3 IsPeriodic=0
    g59: BSplineCurve PolesCount=4 KnotsCount=2 Degree=3 IsPeriodic=0
    g60: BSplineCurve PolesCount=4 KnotsCount=2 Degree=3 IsPeriodic=0
    g61: BSplineCurve PolesCount=4 KnotsCount=2 Degree=3 IsPeriodic=0
    g62: BSplineCurve PolesCount=4 KnotsCount=2 Degree=3 IsPeriodic=0
    g63: BSplineCurve PolesCount=4 KnotsCount=2 Degree=3 IsPeriodic=0
    g64: BSplineCurve PolesCount=4 KnotsCount=2 Degree=3 IsPeriodic=0
    g65: BSplineCurve PolesCount=4 KnotsCount=2 Degree=3 IsPeriodic=0
    g66: BSplineCurve PolesCount=4 KnotsCount=2 Degree=3 IsPeriodic=0
    g67: BSplineCurve PolesCount=4 KnotsCount=2 Degree=3 IsPeriodic=0
    g68: BSplineCurve PolesCount=4 KnotsCount=2 Degree=3 IsPeriodic=0
    g69: BSplineCurve PolesCount=4 KnotsCount=2 Degree=3 IsPeriodic=0
    g70: BSplineCurve PolesCount=4 KnotsCount=2 Degree=3 IsPeriodic=0
    g71: BSplineCurve PolesCount=2 KnotsCount=2 Degree=1 IsPeriodic=0
    g72: BSplineCurve PolesCount=4 KnotsCount=2 Degree=3 IsPeriodic=0
    g73: BSplineCurve PolesCount=4 KnotsCount=2 Degree=3 IsPeriodic=0
    g74: BSplineCurve PolesCount=4 KnotsCount=2 Degree=3 IsPeriodic=0
    g75: BSplineCurve PolesCount=4 KnotsCount=2 Degree=3 IsPeriodic=0
    g76: BSplineCurve PolesCount=4 KnotsCount=2 Degree=3 IsPeriodic=0
    g77: BSplineCurve PolesCount=4 KnotsCount=2 Degree=3 IsPeriodic=0
    g78: BSplineCurve PolesCount=4 KnotsCount=2 Degree=3 IsPeriodic=0
    g79: BSplineCurve PolesCount=4 KnotsCount=2 Degree=3 IsPeriodic=0
    g80: BSplineCurve PolesCount=4 KnotsCount=2 Degree=3 IsPeriodic=0
    g81: BSplineCurve PolesCount=4 KnotsCount=2 Degree=3 IsPeriodic=0
    g82: BSplineCurve PolesCount=4 KnotsCount=2 Degree=3 IsPeriodic=0
    g83: BSplineCurve PolesCount=4 KnotsCount=2 Degree=3 IsPeriodic=0
    g84: BSplineCurve PolesCount=4 KnotsCount=2 Degree=3 IsPeriodic=0
    g85: BSplineCurve PolesCount=4 KnotsCount=2 Degree=3 IsPeriodic=0
    g86: BSplineCurve PolesCount=4 KnotsCount=2 Degree=3 IsPeriodic=0
    g87: BSplineCurve PolesCount=4 KnotsCount=2 Degree=3 IsPeriodic=0
    g88: BSplineCurve PolesCount=4 KnotsCount=2 Degree=3 IsPeriodic=0
    g89: BSplineCurve PolesCount=4 KnotsCount=2 Degree=3 IsPeriodic=0
    g90: BSplineCurve PolesCount=4 KnotsCount=2 Degree=3 IsPeriodic=0
    g91: BSplineCurve PolesCount=4 KnotsCount=2 Degree=3 IsPeriodic=0
    g92: BSplineCurve PolesCount=4 KnotsCount=2 Degree=3 IsPeriodic=0
    g93: BSplineCurve PolesCount=4 KnotsCount=2 Degree=3 IsPeriodic=0
    g94: BSplineCurve PolesCount=4 KnotsCount=2 Degree=3 IsPeriodic=0
    g95: BSplineCurve PolesCount=4 KnotsCount=2 Degree=3 IsPeriodic=0
    g96: BSplineCurve PolesCount=4 KnotsCount=2 Degree=3 IsPeriodic=0
    g97: BSplineCurve PolesCount=4 KnotsCount=2 Degree=3 IsPeriodic=0
    g98: BSplineCurve PolesCount=4 KnotsCount=2 Degree=3 IsPeriodic=0
    g99: BSplineCurve PolesCount=4 KnotsCount=2 Degree=3 IsPeriodic=0
    g100: BSplineCurve PolesCount=4 KnotsCount=2 Degree=3 IsPeriodic=0
    g101: BSplineCurve PolesCount=4 KnotsCount=2 Degree=3 IsPeriodic=0
    g102: BSplineCurve PolesCount=4 KnotsCount=2 Degree=3 IsPeriodic=0
    g103: BSplineCurve PolesCount=4 KnotsCount=2 Degree=3 IsPeriodic=0
    g104: BSplineCurve PolesCount=4 KnotsCount=2 Degree=3 IsPeriodic=0
    g105: BSplineCurve PolesCount=4 KnotsCount=2 Degree=3 IsPeriodic=0
    g106: BSplineCurve PolesCount=4 KnotsCount=2 Degree=3 IsPeriodic=0
    g107: BSplineCurve PolesCount=2 KnotsCount=2 Degree=1 IsPeriodic=0
    g108: BSplineCurve PolesCount=2 KnotsCount=2 Degree=1 IsPeriodic=0
    g109: BSplineCurve PolesCount=4 KnotsCount=2 Degree=3 IsPeriodic=0
    g110: BSplineCurve PolesCount=4 KnotsCount=2 Degree=3 IsPeriodic=0
    g111: BSplineCurve PolesCount=4 KnotsCount=2 Degree=3 IsPeriodic=0
    g112: BSplineCurve PolesCount=4 KnotsCount=2 Degree=3 IsPeriodic=0
    g113: BSplineCurve PolesCount=4 KnotsCount=2 Degree=3 IsPeriodic=0
    g114: BSplineCurve PolesCount=2 KnotsCount=2 Degree=1 IsPeriodic=0
    g115: BSplineCurve PolesCount=2 KnotsCount=2 Degree=1 IsPeriodic=0
    g116: BSplineCurve PolesCount=4 KnotsCount=2 Degree=3 IsPeriodic=0
    g117: BSplineCurve PolesCount=2 KnotsCount=2 Degree=1 IsPeriodic=0
    g118: BSplineCurve PolesCount=2 KnotsCount=2 Degree=1 IsPeriodic=0
    g119: BSplineCurve PolesCount=4 KnotsCount=2 Degree=3 IsPeriodic=0
    g120: BSplineCurve PolesCount=4 KnotsCount=2 Degree=3 IsPeriodic=0
    g121: BSplineCurve PolesCount=4 KnotsCount=2 Degree=3 IsPeriodic=0
    g122: BSplineCurve PolesCount=4 KnotsCount=2 Degree=3 IsPeriodic=0
    g123: BSplineCurve PolesCount=4 KnotsCount=2 Degree=3 IsPeriodic=0
    g124: BSplineCurve PolesCount=4 KnotsCount=2 Degree=3 IsPeriodic=0
    g125: BSplineCurve PolesCount=4 KnotsCount=2 Degree=3 IsPeriodic=0
    g126: BSplineCurve PolesCount=4 KnotsCount=2 Degree=3 IsPeriodic=0
    g127: BSplineCurve PolesCount=4 KnotsCount=2 Degree=3 IsPeriodic=0
    g128: BSplineCurve PolesCount=4 KnotsCount=2 Degree=3 IsPeriodic=0
    g129: BSplineCurve PolesCount=4 KnotsCount=2 Degree=3 IsPeriodic=0
    g130: BSplineCurve PolesCount=4 KnotsCount=2 Degree=3 IsPeriodic=0
    g131: BSplineCurve PolesCount=4 KnotsCount=2 Degree=3 IsPeriodic=0
    g132: BSplineCurve PolesCount=4 KnotsCount=2 Degree=3 IsPeriodic=0
    g133: BSplineCurve PolesCount=4 KnotsCount=2 Degree=3 IsPeriodic=0
    g134: BSplineCurve PolesCount=4 KnotsCount=2 Degree=3 IsPeriodic=0
    g135: BSplineCurve PolesCount=4 KnotsCount=2 Degree=3 IsPeriodic=0
    g136: BSplineCurve PolesCount=4 KnotsCount=2 Degree=3 IsPeriodic=0
    g137: BSplineCurve PolesCount=4 KnotsCount=2 Degree=3 IsPeriodic=0
    g138: BSplineCurve PolesCount=4 KnotsCount=2 Degree=3 IsPeriodic=0
    g139: BSplineCurve PolesCount=4 KnotsCount=2 Degree=3 IsPeriodic=0
    g140: BSplineCurve PolesCount=4 KnotsCount=2 Degree=3 IsPeriodic=0
    g141: BSplineCurve PolesCount=4 KnotsCount=2 Degree=3 IsPeriodic=0
    g142: BSplineCurve PolesCount=4 KnotsCount=2 Degree=3 IsPeriodic=0
    g143: BSplineCurve PolesCount=4 KnotsCount=2 Degree=3 IsPeriodic=0
    g144: BSplineCurve PolesCount=4 KnotsCount=2 Degree=3 IsPeriodic=0
    g145: BSplineCurve PolesCount=4 KnotsCount=2 Degree=3 IsPeriodic=0
    g146: BSplineCurve PolesCount=4 KnotsCount=2 Degree=3 IsPeriodic=0
    g147: BSplineCurve PolesCount=4 KnotsCount=2 Degree=3 IsPeriodic=0
    g148: BSplineCurve PolesCount=4 KnotsCount=2 Degree=3 IsPeriodic=0
    g149: BSplineCurve PolesCount=4 KnotsCount=2 Degree=3 IsPeriodic=0
    g150: BSplineCurve PolesCount=4 KnotsCount=2 Degree=3 IsPeriodic=0
    g151: BSplineCurve PolesCount=4 KnotsCount=2 Degree=3 IsPeriodic=0
    g152: BSplineCurve PolesCount=2 KnotsCount=2 Degree=1 IsPeriodic=0
    g153: BSplineCurve PolesCount=4 KnotsCount=2 Degree=3 IsPeriodic=0
    g154: BSplineCurve PolesCount=4 KnotsCount=2 Degree=3 IsPeriodic=0
    g155: BSplineCurve PolesCount=4 KnotsCount=2 Degree=3 IsPeriodic=0
    g156: BSplineCurve PolesCount=4 KnotsCount=2 Degree=3 IsPeriodic=0
    g157: BSplineCurve PolesCount=4 KnotsCount=2 Degree=3 IsPeriodic=0
    g158: BSplineCurve PolesCount=4 KnotsCount=2 Degree=3 IsPeriodic=0
    g159: BSplineCurve PolesCount=4 KnotsCount=2 Degree=3 IsPeriodic=0
    g160: BSplineCurve PolesCount=2 KnotsCount=2 Degree=1 IsPeriodic=0
    g161: BSplineCurve PolesCount=4 KnotsCount=2 Degree=3 IsPeriodic=0
    g162: BSplineCurve PolesCount=2 KnotsCount=2 Degree=1 IsPeriodic=0
    g163: BSplineCurve PolesCount=2 KnotsCount=2 Degree=1 IsPeriodic=0
    g164: BSplineCurve PolesCount=4 KnotsCount=2 Degree=3 IsPeriodic=0
    g165: BSplineCurve PolesCount=2 KnotsCount=2 Degree=1 IsPeriodic=0
    g166: BSplineCurve PolesCount=2 KnotsCount=2 Degree=1 IsPeriodic=0
    g167: BSplineCurve PolesCount=2 KnotsCount=2 Degree=1 IsPeriodic=0
    g168: BSplineCurve PolesCount=2 KnotsCount=2 Degree=1 IsPeriodic=0
    g169: BSplineCurve PolesCount=4 KnotsCount=2 Degree=3 IsPeriodic=0
    g170: BSplineCurve PolesCount=4 KnotsCount=2 Degree=3 IsPeriodic=0
    g171: BSplineCurve PolesCount=2 KnotsCount=2 Degree=1 IsPeriodic=0
    g172: BSplineCurve PolesCount=2 KnotsCount=2 Degree=1 IsPeriodic=0
    g173: BSplineCurve PolesCount=4 KnotsCount=2 Degree=3 IsPeriodic=0
    g174: BSplineCurve PolesCount=4 KnotsCount=2 Degree=3 IsPeriodic=0
    g175: BSplineCurve PolesCount=2 KnotsCount=2 Degree=1 IsPeriodic=0
    g176: BSplineCurve PolesCount=4 KnotsCount=2 Degree=3 IsPeriodic=0
    g177: BSplineCurve PolesCount=4 KnotsCount=2 Degree=3 IsPeriodic=0
    g178: BSplineCurve PolesCount=4 KnotsCount=2 Degree=3 IsPeriodic=0
    g179: BSplineCurve PolesCount=4 KnotsCount=2 Degree=3 IsPeriodic=0
    g180: BSplineCurve PolesCount=4 KnotsCount=2 Degree=3 IsPeriodic=0
    g181: BSplineCurve PolesCount=4 KnotsCount=2 Degree=3 IsPeriodic=0
    g182: BSplineCurve PolesCount=4 KnotsCount=2 Degree=3 IsPeriodic=0
    g183: BSplineCurve PolesCount=4 KnotsCount=2 Degree=3 IsPeriodic=0
    g184: BSplineCurve PolesCount=4 KnotsCount=2 Degree=3 IsPeriodic=0
    g185: BSplineCurve PolesCount=4 KnotsCount=2 Degree=3 IsPeriodic=0
    g186: BSplineCurve PolesCount=4 KnotsCount=2 Degree=3 IsPeriodic=0
    g187: BSplineCurve PolesCount=4 KnotsCount=2 Degree=3 IsPeriodic=0
    g188: BSplineCurve PolesCount=4 KnotsCount=2 Degree=3 IsPeriodic=0
    g189: BSplineCurve PolesCount=4 KnotsCount=2 Degree=3 IsPeriodic=0
    g190: BSplineCurve PolesCount=4 KnotsCount=2 Degree=3 IsPeriodic=0
    g191: BSplineCurve PolesCount=4 KnotsCount=2 Degree=3 IsPeriodic=0
    g192: BSplineCurve PolesCount=4 KnotsCount=2 Degree=3 IsPeriodic=0
    g193: BSplineCurve PolesCount=4 KnotsCount=2 Degree=3 IsPeriodic=0
    g194: BSplineCurve PolesCount=4 KnotsCount=2 Degree=3 IsPeriodic=0
    g195: BSplineCurve PolesCount=4 KnotsCount=2 Degree=3 IsPeriodic=0
    g196: BSplineCurve PolesCount=4 KnotsCount=2 Degree=3 IsPeriodic=0
    g197: BSplineCurve PolesCount=2 KnotsCount=2 Degree=1 IsPeriodic=0
    g198: BSplineCurve PolesCount=2 KnotsCount=2 Degree=1 IsPeriodic=0
    g199: BSplineCurve PolesCount=2 KnotsCount=2 Degree=1 IsPeriodic=0
    g200: BSplineCurve PolesCount=2 KnotsCount=2 Degree=1 IsPeriodic=0
    g201: BSplineCurve PolesCount=4 KnotsCount=2 Degree=3 IsPeriodic=0
    g202: BSplineCurve PolesCount=4 KnotsCount=2 Degree=3 IsPeriodic=0
    g203: BSplineCurve PolesCount=4 KnotsCount=2 Degree=3 IsPeriodic=0
    g204: BSplineCurve PolesCount=4 KnotsCount=2 Degree=3 IsPeriodic=0
    g205: BSplineCurve PolesCount=4 KnotsCount=2 Degree=3 IsPeriodic=0
    g206: BSplineCurve PolesCount=4 KnotsCount=2 Degree=3 IsPeriodic=0
    g207: BSplineCurve PolesCount=4 KnotsCount=2 Degree=3 IsPeriodic=0
    g208: BSplineCurve PolesCount=4 KnotsCount=2 Degree=3 IsPeriodic=0
    g209: BSplineCurve PolesCount=4 KnotsCount=2 Degree=3 IsPeriodic=0
    g210: BSplineCurve PolesCount=4 KnotsCount=2 Degree=3 IsPeriodic=0
    g211: BSplineCurve PolesCount=4 KnotsCount=2 Degree=3 IsPeriodic=0
    g212: BSplineCurve PolesCount=2 KnotsCount=2 Degree=1 IsPeriodic=0
    g213: BSplineCurve PolesCount=2 KnotsCount=2 Degree=1 IsPeriodic=0
    g214: BSplineCurve PolesCount=4 KnotsCount=2 Degree=3 IsPeriodic=0
    g215: BSplineCurve PolesCount=4 KnotsCount=2 Degree=3 IsPeriodic=0
    g216: BSplineCurve PolesCount=4 KnotsCount=2 Degree=3 IsPeriodic=0
    g217: BSplineCurve PolesCount=4 KnotsCount=2 Degree=3 IsPeriodic=0
    g218: BSplineCurve PolesCount=4 KnotsCount=2 Degree=3 IsPeriodic=0
    g219: BSplineCurve PolesCount=4 KnotsCount=2 Degree=3 IsPeriodic=0
    g220: BSplineCurve PolesCount=4 KnotsCount=2 Degree=3 IsPeriodic=0
    g221: BSplineCurve PolesCount=4 KnotsCount=2 Degree=3 IsPeriodic=0
    g222: BSplineCurve PolesCount=4 KnotsCount=2 Degree=3 IsPeriodic=0
    g223: BSplineCurve PolesCount=2 KnotsCount=2 Degree=1 IsPeriodic=0
    g224: BSplineCurve PolesCount=2 KnotsCount=2 Degree=1 IsPeriodic=0
    g225: BSplineCurve PolesCount=2 KnotsCount=2 Degree=1 IsPeriodic=0
    g226: BSplineCurve PolesCount=2 KnotsCount=2 Degree=1 IsPeriodic=0
    g227: BSplineCurve PolesCount=2 KnotsCount=2 Degree=1 IsPeriodic=0
    g228: BSplineCurve PolesCount=4 KnotsCount=2 Degree=3 IsPeriodic=0
    g229: BSplineCurve PolesCount=2 KnotsCount=2 Degree=1 IsPeriodic=0
    g230: BSplineCurve PolesCount=2 KnotsCount=2 Degree=1 IsPeriodic=0
    g231: BSplineCurve PolesCount=2 KnotsCount=2 Degree=1 IsPeriodic=0
    g232: BSplineCurve PolesCount=4 KnotsCount=2 Degree=3 IsPeriodic=0
    g233: BSplineCurve PolesCount=4 KnotsCount=2 Degree=3 IsPeriodic=0
    g234: BSplineCurve PolesCount=4 KnotsCount=2 Degree=3 IsPeriodic=0
    g235: BSplineCurve PolesCount=4 KnotsCount=2 Degree=3 IsPeriodic=0
    g236: BSplineCurve PolesCount=4 KnotsCount=2 Degree=3 IsPeriodic=0
    g237: BSplineCurve PolesCount=4 KnotsCount=2 Degree=3 IsPeriodic=0
    g238: BSplineCurve PolesCount=4 KnotsCount=2 Degree=3 IsPeriodic=0
    g239: BSplineCurve PolesCount=4 KnotsCount=2 Degree=3 IsPeriodic=0
    g240: BSplineCurve PolesCount=4 KnotsCount=2 Degree=3 IsPeriodic=0
    g241: BSplineCurve PolesCount=4 KnotsCount=2 Degree=3 IsPeriodic=0
    g242: BSplineCurve PolesCount=4 KnotsCount=2 Degree=3 IsPeriodic=0
    g243: BSplineCurve PolesCount=4 KnotsCount=2 Degree=3 IsPeriodic=0
    g244: BSplineCurve PolesCount=4 KnotsCount=2 Degree=3 IsPeriodic=0
    g245: BSplineCurve PolesCount=4 KnotsCount=2 Degree=3 IsPeriodic=0
    g246: BSplineCurve PolesCount=4 KnotsCount=2 Degree=3 IsPeriodic=0
    g247: BSplineCurve PolesCount=4 KnotsCount=2 Degree=3 IsPeriodic=0
    g248: BSplineCurve PolesCount=4 KnotsCount=2 Degree=3 IsPeriodic=0
    g249: BSplineCurve PolesCount=4 KnotsCount=2 Degree=3 IsPeriodic=0
    g250: BSplineCurve PolesCount=4 KnotsCount=2 Degree=3 IsPeriodic=0
    g251: BSplineCurve PolesCount=4 KnotsCount=2 Degree=3 IsPeriodic=0
    g252: BSplineCurve PolesCount=4 KnotsCount=2 Degree=3 IsPeriodic=0
    g253: BSplineCurve PolesCount=4 KnotsCount=2 Degree=3 IsPeriodic=0
    g254: BSplineCurve PolesCount=4 KnotsCount=2 Degree=3 IsPeriodic=0
    g255: BSplineCurve PolesCount=4 KnotsCount=2 Degree=3 IsPeriodic=0
    g256: BSplineCurve PolesCount=4 KnotsCount=2 Degree=3 IsPeriodic=0
    g257: BSplineCurve PolesCount=4 KnotsCount=2 Degree=3 IsPeriodic=0
    g258: BSplineCurve PolesCount=4 KnotsCount=2 Degree=3 IsPeriodic=0
    g259: BSplineCurve PolesCount=4 KnotsCount=2 Degree=3 IsPeriodic=0
    g260: BSplineCurve PolesCount=4 KnotsCount=2 Degree=3 IsPeriodic=0
    g261: BSplineCurve PolesCount=4 KnotsCount=2 Degree=3 IsPeriodic=0
    g262: BSplineCurve PolesCount=4 KnotsCount=2 Degree=3 IsPeriodic=0
    g263: BSplineCurve PolesCount=4 KnotsCount=2 Degree=3 IsPeriodic=0
    g264: BSplineCurve PolesCount=4 KnotsCount=2 Degree=3 IsPeriodic=0
    g265: BSplineCurve PolesCount=2 KnotsCount=2 Degree=1 IsPeriodic=0
    g266: BSplineCurve PolesCount=2 KnotsCount=2 Degree=1 IsPeriodic=0
    g267: BSplineCurve PolesCount=4 KnotsCount=2 Degree=3 IsPeriodic=0
    g268: BSplineCurve PolesCount=2 KnotsCount=2 Degree=1 IsPeriodic=0
    g269: BSplineCurve PolesCount=2 KnotsCount=2 Degree=1 IsPeriodic=0
    g270: BSplineCurve PolesCount=4 KnotsCount=2 Degree=3 IsPeriodic=0
  constraints (275):
    c: Coincident(g0,g1)
    c: Coincident(g1,g2)
    c: Coincident(g2,g3)
    c: Coincident(g3,g4)
    c: Coincident(g4,g5)
    c: Coincident(g5,g6)
    c: Coincident(g6,g7)
    c: Coincident(g7,g8)
    c: Coincident(g8,g9)
    c: Coincident(g9,g10)
    c: Coincident(g10,g11)
    c: Coincident(g11,g12)
    c: Coincident(g12,g13)
    c: Coincident(g13,g14)
    c: Coincident(g14,g15)
    c: Coincident(g15,g16)
    c: Coincident(g16,g17)
    c: Coincident(g17,g18)
    c: Coincident(g18,g19)
    c: Coincident(g19,g20)
    c: Coincident(g20,g21)
    c: Coincident(g21,g22)
    c: Coincident(g22,g23)
    c: Coincident(g23,g24)
    c: Coincident(g24,g25)
    c: Coincident(g25,g26)
    c: Coincident(g26,g27)
    c: Coincident(g27,g28)
    c: Coincident(g28,g29)
    c: Coincident(g29,g30)
    c: Coincident(g30,g31)
    c: Coincident(g31,g32)
    c: Coincident(g32,g33)
    c: Coincident(g33,g34)
    c: Coincident(g34,g35)
    c: Coincident(g35,g36)
    c: Coincident(g36,g37)
    c: Coincident(g37,g38)
    c: Coincident(g38,g39)
    c: Coincident(g39,g40)
    c: Coincident(g40,g41)
    c: Coincident(g41,g42)
    c: Coincident(g42,g43)
    c: Coincident(g43,g44)
    c: Coincident(g44,g45)
    c: Coincident(g45,g46)
    c: Coincident(g46,g47)
    c: Coincident(g47,g48)
    c: Coincident(g48,g49)
    c: Coincident(g49,g50)
    c: Coincident(g50,g51)
    c: Coincident(g51,g52)
    c: Coincident(g52,g53)
    c: Coincident(g53,g54)
    c: Coincident(g54,g55)
    c: Coincident(g55,g56)
    c: Coincident(g56,g57)
    c: Coincident(g57,g58)
    c: Coincident(g58,g59)
    c: Coincident(g59,g60)
    c: Coincident(g60,g61)
    c: Coincident(g61,g62)
    c: Coincident(g62,g63)
    c: Coincident(g63,g64)
    c: Coincident(g64,g65)
    c: Coincident(g65,g66)
    c: Coincident(g66,g67)
    c: Coincident(g67,g68)
    c: Coincident(g68,g69)
    c: Coincident(g69,g70)
    c: Coincident(g70,g71)
    c: Coincident(g71,g0)
    c: Coincident(g72,g73)
    c: Coincident(g73,g74)
    c: Coincident(g74,g75)
    c: Coincident(g75,g72)
    c: Coincident(g76,g77)
    c: Coincident(g77,g78)
    c: Coincident(g78,g79)
    c: Coincident(g79,g76)
    c: Coincident(g80,g81)
    c: Coincident(g81,g82)
    c: Coincident(g82,g83)
    c: Coincident(g83,g84)
    c: Coincident(g84,g85)
    c: Coincident(g85,g86)
    c: Coincident(g86,g87)
    c: Coincident(g87,g88)
    c: Coincident(g88,g89)
    c: Coincident(g89,g90)
    c: Coincident(g90,g91)
    c: Coincident(g91,g92)
    c: Coincident(g92,g93)
    c: Coincident(g93,g94)
    c: Coincident(g94,g95)
    c: Coincident(g95,g96)
    c: Coincident(g96,g97)
    c: Coincident(g97,g98)
    c: Coincident(g98,g99)
    c: Coincident(g99,g100)
    c: Coincident(g100,g101)
    c: Coincident(g101,g102)
    c: Coincident(g102,g103)
    c: Coincident(g103,g104)
    c: Coincident(g104,g105)
    c: Coincident(g105,g106)
    c: Coincident(g106,g107)
    c: Coincident(g107,g108)
    c: Coincident(g108,g109)
    c: Coincident(g109,g110)
    c: Coincident(g110,g111)
    c: Coincident(g111,g112)
    c: Coincident(g112,g113)
    c: Coincident(g113,g114)
    c: Coincident(g114,g115)
    c: Coincident(g115,g116)
    c: Coincident(g116,g117)
    c: Coincident(g117,g118)
    c: Coincident(g118,g119)
    c: Coincident(g119,g120)
    c: Coincident(g120,g121)
    c: Coincident(g121,g122)
    c: Coincident(g122,g123)
    c: Coincident(g123,g124)
    c: Coincident(g124,g125)
    c: Coincident(g125,g126)
    c: Coincident(g126,g127)
    c: Coincident(g127,g128)
    c: Coincident(g128,g129)
    c: Coincident(g129,g130)
    c: Coincident(g130,g131)
    c: Coincident(g131,g132)
    c: Coincident(g132,g133)
    c: Coincident(g133,g134)
    c: Coincident(g134,g135)
    c: Coincident(g135,g136)
    c: Coincident(g136,g137)
    c: Coincident(g137,g138)
    c: Coincident(g138,g139)
    c: Coincident(g139,g140)
    c: Coincident(g140,g141)
    c: Coincident(g141,g142)
    c: Coincident(g142,g143)
    c: Coincident(g143,g144)
    c: Coincident(g144,g145)
    c: Coincident(g145,g146)
    c: Coincident(g146,g147)
    c: Coincident(g147,g148)
    c: Coincident(g148,g149)
    c: Coincident(g149,g150)
    c: Coincident(g150,g151)
    c: Coincident(g151,g152)
    c: Coincident(g152,g80)
    c: Coincident(g153,g154)
    c: Coincident(g154,g155)
    c: Coincident(g155,g156)
    c: Coincident(g156,g157)
    c: Coincident(g157,g158)
    c: Coincident(g158,g159)
    c: Coincident(g159,g153)
    c: Coincident(g160,g161)
    c: Coincident(g161,g162)
    c: Coincident(g162,g163)
    c: Coincident(g163,g164)
    c: Coincident(g164,g165)
    c: Coincident(g165,g166)
    c: Coincident(g166,g167)
    c: Coincident(g167,g168)
    c: Coincident(g168,g169)
    c: Coincident(g169,g170)
    c: Coincident(g170,g171)
    c: Coincident(g171,g172)
    c: Coincident(g172,g173)
    c: Coincident(g173,g174)
    c: Coincident(g174,g160)
    c: Coincident(g175,g176)
    c: Coincident(g176,g177)
    c: Coincident(g177,g178)
    c: Coincident(g178,g175)
    c: Coincident(g179,g180)
    c: Coincident(g180,g181)
    c: Coincident(g181,g182)
    c: Coincident(g182,g179)
    c: Coincident(g183,g184)
    c: Coincident(g184,g185)
    c: Coincident(g185,g186)
    c: Coincident(g186,g183)
    c: Coincident(g187,g188)
    c: Coincident(g188,g189)
    c: Coincident(g189,g187)
    c: Coincident(g190,g191)
    c: Coincident(g191,g192)
    c: Coincident(g192,g190)
    c: Coincident(g193,g194)
    c: Coincident(g194,g195)
    c: Coincident(g195,g196)
    c: Coincident(g196,g197)
    c: Coincident(g197,g198)
    c: Coincident(g198,g199)
    c: Coincident(g199,g200)
    c: Coincident(g200,g201)
    c: Coincident(g201,g202)
    c: Coincident(g202,g203)
    c: Coincident(g203,g193)
    c: Coincident(g204,g205)
    c: Coincident(g205,g206)
    c: Coincident(g206,g207)
    c: Coincident(g207,g204)
    c: Coincident(g208,g209)
    c: Coincident(g209,g210)
    c: Coincident(g210,g211)
    c: Coincident(g211,g212)
    c: Coincident(g212,g213)
    c: Coincident(g213,g214)
    c: Coincident(g214,g208)
    c: Coincident(g215,g216)
    c: Coincident(g216,g217)
    c: Coincident(g217,g218)
    c: Coincident(g218,g215)
    c: Coincident(g219,g220)
    c: Coincident(g220,g221)
    c: Coincident(g221,g222)
    c: Coincident(g222,g223)
    c: Coincident(g223,g224)
    c: Coincident(g224,g225)
    c: Coincident(g225,g226)
    c: Coincident(g226,g219)
    c: Coincident(g227,g228)
    c: Coincident(g228,g229)
    c: Coincident(g229,g230)
    c: Coincident(g230,g231)
    c: Coincident(g231,g227)
    c: Coincident(g232,g233)
    c: Coincident(g233,g234)
    c: Coincident(g234,g235)
    c: Coincident(g235,g232)
    c: Coincident(g236,g237)
    c: Coincident(g237,g238)
    c: Coincident(g238,g239)
    c: Coincident(g239,g236)
    c: Coincident(g240,g241)
    c: Coincident(g241,g242)
    c: Coincident(g242,g243)
    c: Coincident(g243,g244)
    c: Coincident(g244,g240)
    c: Coincident(g245,g246)
    c: Coincident(g246,g247)
    c: Coincident(g247,g248)
    c: Coincident(g248,g245)
    c: Coincident(g249,g250)
    c: Coincident(g250,g251)
    c: Coincident(g251,g252)
    c: Coincident(g252,g253)
    c: Coincident(g253,g254)
    c: Coincident(g254,g255)
    c: Coincident(g255,g256)
    c: Coincident(g256,g249)
    c: Coincident(g257,g258)
    c: Coincident(g258,g259)
    c: Coincident(g259,g260)
    c: Coincident(g260,g257)
    c: Coincident(g261,g262)
    c: Coincident(g262,g263)
    c: Coincident(g263,g264)
    c: Coincident(g264,g265)
    c: Coincident(g265,g266)
    c: Coincident(g266,g267)
    c: Coincident(g267,g268)
    c: Coincident(g268,g269)
    c: Coincident(g269,g270)
    c: Coincident(g270,g261)
    c: Coincident(g175,g175)
    c: Coincident(g151,g80)
    c: Coincident(g160,g160)
    c: Coincident(g70,g0)
FEATURE [Sketcher::SketchObject] Sketch011  label="Poisoner-Sketch"
  ArcFitTolerance = 1e-06
  FullyConstrained = false
  MakeInternals = false
  sketch-geometry (107):
    g0: BSplineCurve PolesCount=4 KnotsCount=2 Degree=3 IsPeriodic=0
    g1: BSplineCurve PolesCount=4 KnotsCount=2 Degree=3 IsPeriodic=0
    g2: BSplineCurve PolesCount=4 KnotsCount=2 Degree=3 IsPeriodic=0
    g3: BSplineCurve PolesCount=4 KnotsCount=2 Degree=3 IsPeriodic=0
    g4: BSplineCurve PolesCount=4 KnotsCount=2 Degree=3 IsPeriodic=0
    g5: BSplineCurve PolesCount=4 KnotsCount=2 Degree=3 IsPeriodic=0
    g6: BSplineCurve PolesCount=4 KnotsCount=2 Degree=3 IsPeriodic=0
    g7: BSplineCurve PolesCount=4 KnotsCount=2 Degree=3 IsPeriodic=0
    g8: BSplineCurve PolesCount=4 KnotsCount=2 Degree=3 IsPeriodic=0
    g9: BSplineCurve PolesCount=4 KnotsCount=2 Degree=3 IsPeriodic=0
    g10: BSplineCurve PolesCount=2 KnotsCount=2 Degree=1 IsPeriodic=0
    g11: BSplineCurve PolesCount=2 KnotsCount=2 Degree=1 IsPeriodic=0
    g12: BSplineCurve PolesCount=2 KnotsCount=2 Degree=1 IsPeriodic=0
    g13: BSplineCurve PolesCount=2 KnotsCount=2 Degree=1 IsPeriodic=0
    g14: BSplineCurve PolesCount=4 KnotsCount=2 Degree=3 IsPeriodic=0
    g15: BSplineCurve PolesCount=4 KnotsCount=2 Degree=3 IsPeriodic=0
    g16: BSplineCurve PolesCount=4 KnotsCount=2 Degree=3 IsPeriodic=0
    g17: BSplineCurve PolesCount=4 KnotsCount=2 Degree=3 IsPeriodic=0
    g18: BSplineCurve PolesCount=4 KnotsCount=2 Degree=3 IsPeriodic=0
    g19: BSplineCurve PolesCount=4 KnotsCount=2 Degree=3 IsPeriodic=0
    g20: BSplineCurve PolesCount=4 KnotsCount=2 Degree=3 IsPeriodic=0
    g21: BSplineCurve PolesCount=4 KnotsCount=2 Degree=3 IsPeriodic=0
    g22: BSplineCurve PolesCount=4 KnotsCount=2 Degree=3 IsPeriodic=0
    g23: BSplineCurve PolesCount=4 KnotsCount=2 Degree=3 IsPeriodic=0
    g24: BSplineCurve PolesCount=4 KnotsCount=2 Degree=3 IsPeriodic=0
    g25: BSplineCurve PolesCount=4 KnotsCount=2 Degree=3 IsPeriodic=0
    g26: BSplineCurve PolesCount=4 KnotsCount=2 Degree=3 IsPeriodic=0
    g27: BSplineCurve PolesCount=4 KnotsCount=2 Degree=3 IsPeriodic=0
    g28: BSplineCurve PolesCount=4 KnotsCount=2 Degree=3 IsPeriodic=0
    g29: BSplineCurve PolesCount=4 KnotsCount=2 Degree=3 IsPeriodic=0
    g30: BSplineCurve PolesCount=4 KnotsCount=2 Degree=3 IsPeriodic=0
    g31: BSplineCurve PolesCount=4 KnotsCount=2 Degree=3 IsPeriodic=0
    g32: BSplineCurve PolesCount=4 KnotsCount=2 Degree=3 IsPeriodic=0
    g33: BSplineCurve PolesCount=4 KnotsCount=2 Degree=3 IsPeriodic=0
    g34: BSplineCurve PolesCount=4 KnotsCount=2 Degree=3 IsPeriodic=0
    g35: BSplineCurve PolesCount=4 KnotsCount=2 Degree=3 IsPeriodic=0
    g36: BSplineCurve PolesCount=4 KnotsCount=2 Degree=3 IsPeriodic=0
    g37: BSplineCurve PolesCount=2 KnotsCount=2 Degree=1 IsPeriodic=0
    g38: BSplineCurve PolesCount=4 KnotsCount=2 Degree=3 IsPeriodic=0
    g39: BSplineCurve PolesCount=4 KnotsCount=2 Degree=3 IsPeriodic=0
    g40: BSplineCurve PolesCount=4 KnotsCount=2 Degree=3 IsPeriodic=0
    g41: BSplineCurve PolesCount=4 KnotsCount=2 Degree=3 IsPeriodic=0
    g42: BSplineCurve PolesCount=4 KnotsCount=2 Degree=3 IsPeriodic=0
    g43: BSplineCurve PolesCount=2 KnotsCount=2 Degree=1 IsPeriodic=0
    g44: BSplineCurve PolesCount=2 KnotsCount=2 Degree=1 IsPeriodic=0
    g45: BSplineCurve PolesCount=4 KnotsCount=2 Degree=3 IsPeriodic=0
    g46: BSplineCurve PolesCount=2 KnotsCount=2 Degree=1 IsPeriodic=0
    g47: BSplineCurve PolesCount=4 KnotsCount=2 Degree=3 IsPeriodic=0
    g48: BSplineCurve PolesCount=4 KnotsCount=2 Degree=3 IsPeriodic=0
    g49: BSplineCurve PolesCount=4 KnotsCount=2 Degree=3 IsPeriodic=0
    g50: BSplineCurve PolesCount=4 KnotsCount=2 Degree=3 IsPeriodic=0
    g51: BSplineCurve PolesCount=4 KnotsCount=2 Degree=3 IsPeriodic=0
    g52: BSplineCurve PolesCount=4 KnotsCount=2 Degree=3 IsPeriodic=0
    g53: BSplineCurve PolesCount=4 KnotsCount=2 Degree=3 IsPeriodic=0
    g54: BSplineCurve PolesCount=4 KnotsCount=2 Degree=3 IsPeriodic=0
    g55: BSplineCurve PolesCount=2 KnotsCount=2 Degree=1 IsPeriodic=0
    g56: BSplineCurve PolesCount=2 KnotsCount=2 Degree=1 IsPeriodic=0
    g57: BSplineCurve PolesCount=4 KnotsCount=2 Degree=3 IsPeriodic=0
    g58: BSplineCurve PolesCount=4 KnotsCount=2 Degree=3 IsPeriodic=0
    g59: BSplineCurve PolesCount=4 KnotsCount=2 Degree=3 IsPeriodic=0
    g60: BSplineCurve PolesCount=4 KnotsCount=2 Degree=3 IsPeriodic=0
    g61: BSplineCurve PolesCount=4 KnotsCount=2 Degree=3 IsPeriodic=0
    g62: BSplineCurve PolesCount=4 KnotsCount=2 Degree=3 IsPeriodic=0
    g63: BSplineCurve PolesCount=4 KnotsCount=2 Degree=3 IsPeriodic=0
    g64: BSplineCurve PolesCount=4 KnotsCount=2 Degree=3 IsPeriodic=0
    g65: BSplineCurve PolesCount=4 KnotsCount=2 Degree=3 IsPeriodic=0
    g66: BSplineCurve PolesCount=4 KnotsCount=2 Degree=3 IsPeriodic=0
    g67: BSplineCurve PolesCount=4 KnotsCount=2 Degree=3 IsPeriodic=0
    g68: BSplineCurve PolesCount=4 KnotsCount=2 Degree=3 IsPeriodic=0
    g69: BSplineCurve PolesCount=4 KnotsCount=2 Degree=3 IsPeriodic=0
    g70: BSplineCurve PolesCount=4 KnotsCount=2 Degree=3 IsPeriodic=0
    g71: BSplineCurve PolesCount=4 KnotsCount=2 Degree=3 IsPeriodic=0
    g72: BSplineCurve PolesCount=4 KnotsCount=2 Degree=3 IsPeriodic=0
    g73: BSplineCurve PolesCount=4 KnotsCount=2 Degree=3 IsPeriodic=0
    g74: BSplineCurve PolesCount=4 KnotsCount=2 Degree=3 IsPeriodic=0
    g75: BSplineCurve PolesCount=4 KnotsCount=2 Degree=3 IsPeriodic=0
    g76: BSplineCurve PolesCount=4 KnotsCount=2 Degree=3 IsPeriodic=0
    g77: BSplineCurve PolesCount=4 KnotsCount=2 Degree=3 IsPeriodic=0
    g78: BSplineCurve PolesCount=4 KnotsCount=2 Degree=3 IsPeriodic=0
    g79: BSplineCurve PolesCount=4 KnotsCount=2 Degree=3 IsPeriodic=0
    g80: BSplineCurve PolesCount=4 KnotsCount=2 Degree=3 IsPeriodic=0
    g81: BSplineCurve PolesCount=4 KnotsCount=2 Degree=3 IsPeriodic=0
    g82: BSplineCurve PolesCount=4 KnotsCount=2 Degree=3 IsPeriodic=0
    g83: BSplineCurve PolesCount=2 KnotsCount=2 Degree=1 IsPeriodic=0
    g84: BSplineCurve PolesCount=4 KnotsCount=2 Degree=3 IsPeriodic=0
    g85: BSplineCurve PolesCount=4 KnotsCount=2 Degree=3 IsPeriodic=0
    g86: BSplineCurve PolesCount=4 KnotsCount=2 Degree=3 IsPeriodic=0
    g87: BSplineCurve PolesCount=4 KnotsCount=2 Degree=3 IsPeriodic=0
    g88: BSplineCurve PolesCount=4 KnotsCount=2 Degree=3 IsPeriodic=0
    g89: BSplineCurve PolesCount=4 KnotsCount=2 Degree=3 IsPeriodic=0
    g90: BSplineCurve PolesCount=4 KnotsCount=2 Degree=3 IsPeriodic=0
    g91: BSplineCurve PolesCount=4 KnotsCount=2 Degree=3 IsPeriodic=0
    g92: BSplineCurve PolesCount=4 KnotsCount=2 Degree=3 IsPeriodic=0
    g93: BSplineCurve PolesCount=4 KnotsCount=2 Degree=3 IsPeriodic=0
    g94: BSplineCurve PolesCount=4 KnotsCount=2 Degree=3 IsPeriodic=0
    g95: BSplineCurve PolesCount=4 KnotsCount=2 Degree=3 IsPeriodic=0
    g96: BSplineCurve PolesCount=4 KnotsCount=2 Degree=3 IsPeriodic=0
    g97: BSplineCurve PolesCount=4 KnotsCount=2 Degree=3 IsPeriodic=0
    g98: BSplineCurve PolesCount=4 KnotsCount=2 Degree=3 IsPeriodic=0
    g99: BSplineCurve PolesCount=4 KnotsCount=2 Degree=3 IsPeriodic=0
    g100: BSplineCurve PolesCount=4 KnotsCount=2 Degree=3 IsPeriodic=0
    g101: BSplineCurve PolesCount=4 KnotsCount=2 Degree=3 IsPeriodic=0
    g102: BSplineCurve PolesCount=4 KnotsCount=2 Degree=3 IsPeriodic=0
    g103: BSplineCurve PolesCount=4 KnotsCount=2 Degree=3 IsPeriodic=0
    g104: BSplineCurve PolesCount=4 KnotsCount=2 Degree=3 IsPeriodic=0
    g105: BSplineCurve PolesCount=4 KnotsCount=2 Degree=3 IsPeriodic=0
    g106: BSplineCurve PolesCount=4 KnotsCount=2 Degree=3 IsPeriodic=0
  constraints (110):
    c: Coincident(g0,g1)
    c: Coincident(g1,g2)
    c: Coincident(g2,g3)
    c: Coincident(g3,g4)
    c: Coincident(g4,g5)
    c: Coincident(g5,g6)
    c: Coincident(g6,g7)
    c: Coincident(g7,g8)
    c: Coincident(g8,g9)
    c: Coincident(g9,g10)
    c: Coincident(g10,g11)
    c: Coincident(g11,g12)
    c: Coincident(g12,g13)
    c: Coincident(g13,g14)
    c: Coincident(g14,g15)
    c: Coincident(g15,g16)
    c: Coincident(g16,g17)
    c: Coincident(g17,g18)
    c: Coincident(g18,g19)
    c: Coincident(g19,g20)
    c: Coincident(g20,g21)
    c: Coincident(g21,g22)
    c: Coincident(g22,g23)
    c: Coincident(g23,g24)
    c: Coincident(g24,g25)
    c: Coincident(g25,g26)
    c: Coincident(g26,g27)
    c: Coincident(g27,g28)
    c: Coincident(g28,g29)
    c: Coincident(g29,g30)
    c: Coincident(g30,g31)
    c: Coincident(g31,g32)
    c: Coincident(g32,g33)
    c: Coincident(g33,g34)
    c: Coincident(g34,g35)
    c: Coincident(g35,g36)
    c: Coincident(g36,g0)
    c: Coincident(g37,g38)
    c: Coincident(g38,g39)
    c: Coincident(g39,g40)
    c: Coincident(g40,g41)
    c: Coincident(g41,g42)
    c: Coincident(g42,g43)
    c: Coincident(g43,g44)
    c: Coincident(g44,g45)
    c: Coincident(g45,g37)
    c: Coincident(g46,g47)
    c: Coincident(g47,g48)
    c: Coincident(g48,g49)
    c: Coincident(g49,g50)
    c: Coincident(g50,g51)
    c: Coincident(g51,g52)
    c: Coincident(g52,g53)
    c: Coincident(g53,g54)
    c: Coincident(g54,g55)
    c: Coincident(g55,g56)
    c: Coincident(g56,g57)
    c: Coincident(g57,g58)
    c: Coincident(g58,g59)
    c: Coincident(g59,g60)
    c: Coincident(g60,g61)
    c: Coincident(g61,g62)
    c: Coincident(g62,g63)
    c: Coincident(g63,g64)
    c: Coincident(g64,g65)
    c: Coincident(g65,g66)
    c: Coincident(g66,g67)
    c: Coincident(g67,g68)
    c: Coincident(g68,g46)
    c: Coincident(g69,g70)
    c: Coincident(g70,g71)
    c: Coincident(g71,g72)
    c: Coincident(g72,g73)
    c: Coincident(g73,g74)
    c: Coincident(g74,g75)
    c: Coincident(g75,g76)
    c: Coincident(g76,g69)
    c: Coincident(g77,g78)
    c: Coincident(g78,g79)
    c: Coincident(g79,g77)
    c: Coincident(g80,g81)
    c: Coincident(g81,g82)
    c: Coincident(g82,g80)
    c: Coincident(g83,g84)
    c: Coincident(g84,g85)
    c: Coincident(g85,g86)
    c: Coincident(g86,g87)
    c: Coincident(g87,g88)
    c: Coincident(g88,g89)
    c: Coincident(g89,g90)
    c: Coincident(g90,g91)
    c: Coincident(g91,g92)
    c: Coincident(g92,g93)
    c: Coincident(g93,g94)
    c: Coincident(g94,g95)
    c: Coincident(g95,g96)
    c: Coincident(g96,g97)
    c: Coincident(g97,g98)
    c: Coincident(g98,g99)
    c: Coincident(g99,g100)
    c: Coincident(g100,g101)
    c: Coincident(g101,g102)
    c: Coincident(g102,g103)
    c: Coincident(g103,g104)
    c: Coincident(g104,g105)
    c: Coincident(g105,g106)
    c: Coincident(g106,g83)
    c: Coincident(g83,g83)
    c: Coincident(g46,g46)
    c: Coincident(g37,g37)
FEATURE [Sketcher::SketchObject] Sketch012  label="Ravenskeeper-Sketch"
  ArcFitTolerance = 1e-06
  FullyConstrained = false
  MakeInternals = false
  sketch-geometry (109):
    g0: BSplineCurve PolesCount=4 KnotsCount=2 Degree=3 IsPeriodic=0
    g1: BSplineCurve PolesCount=4 KnotsCount=2 Degree=3 IsPeriodic=0
    g2: BSplineCurve PolesCount=2 KnotsCount=2 Degree=1 IsPeriodic=0
    g3: BSplineCurve PolesCount=2 KnotsCount=2 Degree=1 IsPeriodic=0
    g4: BSplineCurve PolesCount=4 KnotsCount=2 Degree=3 IsPeriodic=0
    g5: BSplineCurve PolesCount=4 KnotsCount=2 Degree=3 IsPeriodic=0
    g6: BSplineCurve PolesCount=4 KnotsCount=2 Degree=3 IsPeriodic=0
    g7: BSplineCurve PolesCount=4 KnotsCount=2 Degree=3 IsPeriodic=0
    g8: BSplineCurve PolesCount=4 KnotsCount=2 Degree=3 IsPeriodic=0
    g9: BSplineCurve PolesCount=4 KnotsCount=2 Degree=3 IsPeriodic=0
    g10: BSplineCurve PolesCount=4 KnotsCount=2 Degree=3 IsPeriodic=0
    g11: BSplineCurve PolesCount=4 KnotsCount=2 Degree=3 IsPeriodic=0
    g12: BSplineCurve PolesCount=4 KnotsCount=2 Degree=3 IsPeriodic=0
    g13: BSplineCurve PolesCount=4 KnotsCount=2 Degree=3 IsPeriodic=0
    g14: BSplineCurve PolesCount=2 KnotsCount=2 Degree=1 IsPeriodic=0
    g15: BSplineCurve PolesCount=2 KnotsCount=2 Degree=1 IsPeriodic=0
    g16: BSplineCurve PolesCount=4 KnotsCount=2 Degree=3 IsPeriodic=0
    g17: BSplineCurve PolesCount=4 KnotsCount=2 Degree=3 IsPeriodic=0
    g18: BSplineCurve PolesCount=4 KnotsCount=2 Degree=3 IsPeriodic=0
    g19: BSplineCurve PolesCount=4 KnotsCount=2 Degree=3 IsPeriodic=0
    g20: BSplineCurve PolesCount=4 KnotsCount=2 Degree=3 IsPeriodic=0
    g21: BSplineCurve PolesCount=4 KnotsCount=2 Degree=3 IsPeriodic=0
    g22: BSplineCurve PolesCount=4 KnotsCount=2 Degree=3 IsPeriodic=0
    g23: BSplineCurve PolesCount=4 KnotsCount=2 Degree=3 IsPeriodic=0
    g24: BSplineCurve PolesCount=4 KnotsCount=2 Degree=3 IsPeriodic=0
    g25: BSplineCurve PolesCount=2 KnotsCount=2 Degree=1 IsPeriodic=0
    g26: BSplineCurve PolesCount=2 KnotsCount=2 Degree=1 IsPeriodic=0
    g27: BSplineCurve PolesCount=4 KnotsCount=2 Degree=3 IsPeriodic=0
    g28: BSplineCurve PolesCount=4 KnotsCount=2 Degree=3 IsPeriodic=0
    g29: BSplineCurve PolesCount=4 KnotsCount=2 Degree=3 IsPeriodic=0
    g30: BSplineCurve PolesCount=4 KnotsCount=2 Degree=3 IsPeriodic=0
    g31: BSplineCurve PolesCount=2 KnotsCount=2 Degree=1 IsPeriodic=0
    g32: BSplineCurve PolesCount=2 KnotsCount=2 Degree=1 IsPeriodic=0
    g33: BSplineCurve PolesCount=4 KnotsCount=2 Degree=3 IsPeriodic=0
    g34: BSplineCurve PolesCount=4 KnotsCount=2 Degree=3 IsPeriodic=0
    g35: BSplineCurve PolesCount=4 KnotsCount=2 Degree=3 IsPeriodic=0
    g36: BSplineCurve PolesCount=4 KnotsCount=2 Degree=3 IsPeriodic=0
    g37: BSplineCurve PolesCount=4 KnotsCount=2 Degree=3 IsPeriodic=0
    g38: BSplineCurve PolesCount=4 KnotsCount=2 Degree=3 IsPeriodic=0
    g39: BSplineCurve PolesCount=4 KnotsCount=2 Degree=3 IsPeriodic=0
    g40: BSplineCurve PolesCount=4 KnotsCount=2 Degree=3 IsPeriodic=0
    g41: BSplineCurve PolesCount=4 KnotsCount=2 Degree=3 IsPeriodic=0
    g42: BSplineCurve PolesCount=4 KnotsCount=2 Degree=3 IsPeriodic=0
    g43: BSplineCurve PolesCount=4 KnotsCount=2 Degree=3 IsPeriodic=0
    g44: BSplineCurve PolesCount=4 KnotsCount=2 Degree=3 IsPeriodic=0
    g45: BSplineCurve PolesCount=4 KnotsCount=2 Degree=3 IsPeriodic=0
    g46: BSplineCurve PolesCount=4 KnotsCount=2 Degree=3 IsPeriodic=0
    g47: BSplineCurve PolesCount=4 KnotsCount=2 Degree=3 IsPeriodic=0
    g48: BSplineCurve PolesCount=4 KnotsCount=2 Degree=3 IsPeriodic=0
    g49: BSplineCurve PolesCount=4 KnotsCount=2 Degree=3 IsPeriodic=0
    g50: BSplineCurve PolesCount=2 KnotsCount=2 Degree=1 IsPeriodic=0
    g51: BSplineCurve PolesCount=2 KnotsCount=2 Degree=1 IsPeriodic=0
    g52: BSplineCurve PolesCount=4 KnotsCount=2 Degree=3 IsPeriodic=0
    g53: BSplineCurve PolesCount=4 KnotsCount=2 Degree=3 IsPeriodic=0
    g54: BSplineCurve PolesCount=4 KnotsCount=2 Degree=3 IsPeriodic=0
    g55: BSplineCurve PolesCount=4 KnotsCount=2 Degree=3 IsPeriodic=0
    g56: BSplineCurve PolesCount=4 KnotsCount=2 Degree=3 IsPeriodic=0
    g57: BSplineCurve PolesCount=4 KnotsCount=2 Degree=3 IsPeriodic=0
    g58: BSplineCurve PolesCount=4 KnotsCount=2 Degree=3 IsPeriodic=0
    g59: BSplineCurve PolesCount=4 KnotsCount=2 Degree=3 IsPeriodic=0
    g60: BSplineCurve PolesCount=4 KnotsCount=2 Degree=3 IsPeriodic=0
    g61: BSplineCurve PolesCount=2 KnotsCount=2 Degree=1 IsPeriodic=0
    g62: BSplineCurve PolesCount=4 KnotsCount=2 Degree=3 IsPeriodic=0
    g63: BSplineCurve PolesCount=4 KnotsCount=2 Degree=3 IsPeriodic=0
    g64: BSplineCurve PolesCount=4 KnotsCount=2 Degree=3 IsPeriodic=0
    g65: BSplineCurve PolesCount=4 KnotsCount=2 Degree=3 IsPeriodic=0
    g66: BSplineCurve PolesCount=4 KnotsCount=2 Degree=3 IsPeriodic=0
    g67: BSplineCurve PolesCount=4 KnotsCount=2 Degree=3 IsPeriodic=0
    g68: BSplineCurve PolesCount=4 KnotsCount=2 Degree=3 IsPeriodic=0
    g69: BSplineCurve PolesCount=4 KnotsCount=2 Degree=3 IsPeriodic=0
    g70: BSplineCurve PolesCount=4 KnotsCount=2 Degree=3 IsPeriodic=0
    g71: BSplineCurve PolesCount=4 KnotsCount=2 Degree=3 IsPeriodic=0
    g72: BSplineCurve PolesCount=4 KnotsCount=2 Degree=3 IsPeriodic=0
    g73: BSplineCurve PolesCount=4 KnotsCount=2 Degree=3 IsPeriodic=0
    g74: BSplineCurve PolesCount=4 KnotsCount=2 Degree=3 IsPeriodic=0
    g75: BSplineCurve PolesCount=4 KnotsCount=2 Degree=3 IsPeriodic=0
    g76: BSplineCurve PolesCount=4 KnotsCount=2 Degree=3 IsPeriodic=0
    g77: BSplineCurve PolesCount=4 KnotsCount=2 Degree=3 IsPeriodic=0
    g78: BSplineCurve PolesCount=2 KnotsCount=2 Degree=1 IsPeriodic=0
    g79: BSplineCurve PolesCount=2 KnotsCount=2 Degree=1 IsPeriodic=0
    g80: BSplineCurve PolesCount=4 KnotsCount=2 Degree=3 IsPeriodic=0
    g81: BSplineCurve PolesCount=4 KnotsCount=2 Degree=3 IsPeriodic=0
    g82: BSplineCurve PolesCount=4 KnotsCount=2 Degree=3 IsPeriodic=0
    g83: BSplineCurve PolesCount=2 KnotsCount=2 Degree=1 IsPeriodic=0
    g84: BSplineCurve PolesCount=2 KnotsCount=2 Degree=1 IsPeriodic=0
    g85: BSplineCurve PolesCount=4 KnotsCount=2 Degree=3 IsPeriodic=0
    g86: BSplineCurve PolesCount=4 KnotsCount=2 Degree=3 IsPeriodic=0
    g87: BSplineCurve PolesCount=4 KnotsCount=2 Degree=3 IsPeriodic=0
    g88: BSplineCurve PolesCount=4 KnotsCount=2 Degree=3 IsPeriodic=0
    g89: BSplineCurve PolesCount=4 KnotsCount=2 Degree=3 IsPeriodic=0
    g90: BSplineCurve PolesCount=4 KnotsCount=2 Degree=3 IsPeriodic=0
    g91: BSplineCurve PolesCount=4 KnotsCount=2 Degree=3 IsPeriodic=0
    g92: BSplineCurve PolesCount=4 KnotsCount=2 Degree=3 IsPeriodic=0
    g93: BSplineCurve PolesCount=4 KnotsCount=2 Degree=3 IsPeriodic=0
    g94: BSplineCurve PolesCount=4 KnotsCount=2 Degree=3 IsPeriodic=0
    g95: BSplineCurve PolesCount=4 KnotsCount=2 Degree=3 IsPeriodic=0
    g96: BSplineCurve PolesCount=4 KnotsCount=2 Degree=3 IsPeriodic=0
    g97: BSplineCurve PolesCount=4 KnotsCount=2 Degree=3 IsPeriodic=0
    g98: BSplineCurve PolesCount=4 KnotsCount=2 Degree=3 IsPeriodic=0
    g99: BSplineCurve PolesCount=4 KnotsCount=2 Degree=3 IsPeriodic=0
    g100: BSplineCurve PolesCount=4 KnotsCount=2 Degree=3 IsPeriodic=0
    g101: BSplineCurve PolesCount=4 KnotsCount=2 Degree=3 IsPeriodic=0
    g102: BSplineCurve PolesCount=4 KnotsCount=2 Degree=3 IsPeriodic=0
    g103: BSplineCurve PolesCount=4 KnotsCount=2 Degree=3 IsPeriodic=0
    g104: BSplineCurve PolesCount=4 KnotsCount=2 Degree=3 IsPeriodic=0
    g105: BSplineCurve PolesCount=4 KnotsCount=2 Degree=3 IsPeriodic=0
    g106: BSplineCurve PolesCount=4 KnotsCount=2 Degree=3 IsPeriodic=0
    g107: BSplineCurve PolesCount=4 KnotsCount=2 Degree=3 IsPeriodic=0
    g108: BSplineCurve PolesCount=4 KnotsCount=2 Degree=3 IsPeriodic=0
  constraints (110):
    c: Coincident(g0,g1)
    c: Coincident(g1,g2)
    c: Coincident(g2,g3)
    c: Coincident(g3,g4)
    c: Coincident(g4,g5)
    c: Coincident(g5,g6)
    c: Coincident(g6,g7)
    c: Coincident(g7,g8)
    c: Coincident(g8,g9)
    c: Coincident(g9,g10)
    c: Coincident(g10,g11)
    c: Coincident(g11,g12)
    c: Coincident(g12,g13)
    c: Coincident(g13,g14)
    c: Coincident(g14,g15)
    c: Coincident(g15,g16)
    c: Coincident(g16,g17)
    c: Coincident(g17,g18)
    c: Coincident(g18,g19)
    c: Coincident(g19,g20)
    c: Coincident(g20,g21)
    c: Coincident(g21,g22)
    c: Coincident(g22,g23)
    c: Coincident(g23,g24)
    c: Coincident(g24,g25)
    c: Coincident(g25,g26)
    c: Coincident(g26,g27)
    c: Coincident(g27,g28)
    c: Coincident(g28,g29)
    c: Coincident(g29,g30)
    c: Coincident(g30,g31)
    c: Coincident(g31,g32)
    c: Coincident(g32,g33)
    c: Coincident(g33,g34)
    c: Coincident(g34,g35)
    c: Coincident(g35,g36)
    c: Coincident(g36,g37)
    c: Coincident(g37,g38)
    c: Coincident(g38,g39)
    c: Coincident(g39,g40)
    c: Coincident(g40,g41)
    c: Coincident(g41,g42)
    c: Coincident(g42,g43)
    c: Coincident(g43,g44)
    c: Coincident(g44,g45)
    c: Coincident(g45,g46)
    c: Coincident(g46,g47)
    c: Coincident(g47,g48)
    c: Coincident(g48,g49)
    c: Coincident(g49,g50)
    c: Coincident(g50,g51)
    c: Coincident(g51,g52)
    c: Coincident(g52,g53)
    c: Coincident(g53,g54)
    c: Coincident(g54,g55)
    c: Coincident(g55,g56)
    c: Coincident(g56,g57)
    c: Coincident(g57,g58)
    c: Coincident(g58,g59)
    c: Coincident(g59,g60)
    c: Coincident(g60,g61)
    c: Coincident(g61,g0)
    c: Coincident(g62,g63)
    c: Coincident(g63,g64)
    c: Coincident(g64,g65)
    c: Coincident(g65,g66)
    c: Coincident(g66,g67)
    c: Coincident(g67,g68)
    c: Coincident(g68,g69)
    c: Coincident(g69,g70)
    c: Coincident(g70,g62)
    c: Coincident(g71,g72)
    c: Coincident(g72,g73)
    c: Coincident(g73,g74)
    c: Coincident(g74,g75)
    c: Coincident(g75,g71)
    c: Coincident(g76,g77)
    c: Coincident(g77,g78)
    c: Coincident(g78,g79)
    c: Coincident(g79,g80)
    c: Coincident(g80,g81)
    c: Coincident(g81,g82)
    c: Coincident(g82,g83)
    c: Coincident(g83,g84)
    c: Coincident(g84,g85)
    c: Coincident(g85,g86)
    c: Coincident(g86,g87)
    c: Coincident(g87,g88)
    c: Coincident(g88,g89)
    c: Coincident(g89,g90)
    c: Coincident(g90,g91)
    c: Coincident(g91,g92)
    c: Coincident(g92,g93)
    c: Coincident(g93,g94)
    c: Coincident(g94,g95)
    c: Coincident(g95,g96)
    c: Coincident(g96,g97)
    c: Coincident(g97,g98)
    c: Coincident(g98,g99)
    c: Coincident(g99,g100)
    c: Coincident(g100,g101)
    c: Coincident(g101,g102)
    c: Coincident(g102,g103)
    c: Coincident(g103,g104)
    c: Coincident(g104,g105)
    c: Coincident(g105,g106)
    c: Coincident(g106,g107)
    c: Coincident(g107,g108)
    c: Coincident(g108,g76)
    c: Coincident(g60,g0)
FEATURE [Sketcher::SketchObject] Sketch013  label="Recluse-Sketch"
  ArcFitTolerance = 1e-06
  FullyConstrained = false
  MakeInternals = false
  sketch-geometry (194):
    g0: BSplineCurve PolesCount=4 KnotsCount=2 Degree=3 IsPeriodic=0
    g1: BSplineCurve PolesCount=2 KnotsCount=2 Degree=1 IsPeriodic=0
    g2: BSplineCurve PolesCount=2 KnotsCount=2 Degree=1 IsPeriodic=0
    g3: BSplineCurve PolesCount=2 KnotsCount=2 Degree=1 IsPeriodic=0
    g4: BSplineCurve PolesCount=2 KnotsCount=2 Degree=1 IsPeriodic=0
    g5: BSplineCurve PolesCount=4 KnotsCount=2 Degree=3 IsPeriodic=0
    g6: BSplineCurve PolesCount=4 KnotsCount=2 Degree=3 IsPeriodic=0
    g7: BSplineCurve PolesCount=4 KnotsCount=2 Degree=3 IsPeriodic=0
    g8: BSplineCurve PolesCount=4 KnotsCount=2 Degree=3 IsPeriodic=0
    g9: BSplineCurve PolesCount=4 KnotsCount=2 Degree=3 IsPeriodic=0
    g10: BSplineCurve PolesCount=4 KnotsCount=2 Degree=3 IsPeriodic=0
    g11: BSplineCurve PolesCount=4 KnotsCount=2 Degree=3 IsPeriodic=0
    g12: BSplineCurve PolesCount=4 KnotsCount=2 Degree=3 IsPeriodic=0
    g13: BSplineCurve PolesCount=4 KnotsCount=2 Degree=3 IsPeriodic=0
    g14: BSplineCurve PolesCount=4 KnotsCount=2 Degree=3 IsPeriodic=0
    g15: BSplineCurve PolesCount=4 KnotsCount=2 Degree=3 IsPeriodic=0
    g16: BSplineCurve PolesCount=4 KnotsCount=2 Degree=3 IsPeriodic=0
    g17: BSplineCurve PolesCount=2 KnotsCount=2 Degree=1 IsPeriodic=0
    g18: BSplineCurve PolesCount=2 KnotsCount=2 Degree=1 IsPeriodic=0
    g19: BSplineCurve PolesCount=4 KnotsCount=2 Degree=3 IsPeriodic=0
    g20: BSplineCurve PolesCount=4 KnotsCount=2 Degree=3 IsPeriodic=0
    g21: BSplineCurve PolesCount=4 KnotsCount=2 Degree=3 IsPeriodic=0
    g22: BSplineCurve PolesCount=4 KnotsCount=2 Degree=3 IsPeriodic=0
    g23: BSplineCurve PolesCount=4 KnotsCount=2 Degree=3 IsPeriodic=0
    g24: BSplineCurve PolesCount=4 KnotsCount=2 Degree=3 IsPeriodic=0
    g25: BSplineCurve PolesCount=4 KnotsCount=2 Degree=3 IsPeriodic=0
    g26: BSplineCurve PolesCount=4 KnotsCount=2 Degree=3 IsPeriodic=0
    g27: BSplineCurve PolesCount=4 KnotsCount=2 Degree=3 IsPeriodic=0
    g28: BSplineCurve PolesCount=4 KnotsCount=2 Degree=3 IsPeriodic=0
    g29: BSplineCurve PolesCount=4 KnotsCount=2 Degree=3 IsPeriodic=0
    g30: BSplineCurve PolesCount=4 KnotsCount=2 Degree=3 IsPeriodic=0
    g31: BSplineCurve PolesCount=4 KnotsCount=2 Degree=3 IsPeriodic=0
    g32: BSplineCurve PolesCount=4 KnotsCount=2 Degree=3 IsPeriodic=0
    g33: BSplineCurve PolesCount=4 KnotsCount=2 Degree=3 IsPeriodic=0
    g34: BSplineCurve PolesCount=4 KnotsCount=2 Degree=3 IsPeriodic=0
    g35: BSplineCurve PolesCount=4 KnotsCount=2 Degree=3 IsPeriodic=0
    g36: BSplineCurve PolesCount=4 KnotsCount=2 Degree=3 IsPeriodic=0
    g37: BSplineCurve PolesCount=4 KnotsCount=2 Degree=3 IsPeriodic=0
    g38: BSplineCurve PolesCount=4 KnotsCount=2 Degree=3 IsPeriodic=0
    g39: BSplineCurve PolesCount=4 KnotsCount=2 Degree=3 IsPeriodic=0
    g40: BSplineCurve PolesCount=4 KnotsCount=2 Degree=3 IsPeriodic=0
    g41: BSplineCurve PolesCount=2 KnotsCount=2 Degree=1 IsPeriodic=0
    g42: BSplineCurve PolesCount=2 KnotsCount=2 Degree=1 IsPeriodic=0
    g43: BSplineCurve PolesCount=4 KnotsCount=2 Degree=3 IsPeriodic=0
    g44: BSplineCurve PolesCount=4 KnotsCount=2 Degree=3 IsPeriodic=0
    g45: BSplineCurve PolesCount=4 KnotsCount=2 Degree=3 IsPeriodic=0
    g46: BSplineCurve PolesCount=4 KnotsCount=2 Degree=3 IsPeriodic=0
    g47: BSplineCurve PolesCount=4 KnotsCount=2 Degree=3 IsPeriodic=0
    g48: BSplineCurve PolesCount=4 KnotsCount=2 Degree=3 IsPeriodic=0
    g49: BSplineCurve PolesCount=4 KnotsCount=2 Degree=3 IsPeriodic=0
    g50: BSplineCurve PolesCount=4 KnotsCount=2 Degree=3 IsPeriodic=0
    g51: BSplineCurve PolesCount=4 KnotsCount=2 Degree=3 IsPeriodic=0
    g52: BSplineCurve PolesCount=4 KnotsCount=2 Degree=3 IsPeriodic=0
    g53: BSplineCurve PolesCount=4 KnotsCount=2 Degree=3 IsPeriodic=0
    g54: BSplineCurve PolesCount=4 KnotsCount=2 Degree=3 IsPeriodic=0
    g55: BSplineCurve PolesCount=4 KnotsCount=2 Degree=3 IsPeriodic=0
    g56: BSplineCurve PolesCount=4 KnotsCount=2 Degree=3 IsPeriodic=0
    g57: BSplineCurve PolesCount=4 KnotsCount=2 Degree=3 IsPeriodic=0
    g58: BSplineCurve PolesCount=4 KnotsCount=2 Degree=3 IsPeriodic=0
    g59: BSplineCurve PolesCount=4 KnotsCount=2 Degree=3 IsPeriodic=0
    g60: BSplineCurve PolesCount=4 KnotsCount=2 Degree=3 IsPeriodic=0
    g61: BSplineCurve PolesCount=4 KnotsCount=2 Degree=3 IsPeriodic=0
    g62: BSplineCurve PolesCount=4 KnotsCount=2 Degree=3 IsPeriodic=0
    g63: BSplineCurve PolesCount=4 KnotsCount=2 Degree=3 IsPeriodic=0
    g64: BSplineCurve PolesCount=2 KnotsCount=2 Degree=1 IsPeriodic=0
    g65: BSplineCurve PolesCount=2 KnotsCount=2 Degree=1 IsPeriodic=0
    g66: BSplineCurve PolesCount=2 KnotsCount=2 Degree=1 IsPeriodic=0
    g67: BSplineCurve PolesCount=2 KnotsCount=2 Degree=1 IsPeriodic=0
    g68: BSplineCurve PolesCount=2 KnotsCount=2 Degree=1 IsPeriodic=0
    g69: BSplineCurve PolesCount=2 KnotsCount=2 Degree=1 IsPeriodic=0
    g70: BSplineCurve PolesCount=2 KnotsCount=2 Degree=1 IsPeriodic=0
    g71: BSplineCurve PolesCount=2 KnotsCount=2 Degree=1 IsPeriodic=0
    g72: BSplineCurve PolesCount=4 KnotsCount=2 Degree=3 IsPeriodic=0
    g73: BSplineCurve PolesCount=4 KnotsCount=2 Degree=3 IsPeriodic=0
    g74: BSplineCurve PolesCount=4 KnotsCount=2 Degree=3 IsPeriodic=0
    g75: BSplineCurve PolesCount=4 KnotsCount=2 Degree=3 IsPeriodic=0
    g76: BSplineCurve PolesCount=2 KnotsCount=2 Degree=1 IsPeriodic=0
    g77: BSplineCurve PolesCount=2 KnotsCount=2 Degree=1 IsPeriodic=0
    g78: BSplineCurve PolesCount=4 KnotsCount=2 Degree=3 IsPeriodic=0
    g79: BSplineCurve PolesCount=4 KnotsCount=2 Degree=3 IsPeriodic=0
    g80: BSplineCurve PolesCount=2 KnotsCount=2 Degree=1 IsPeriodic=0
    g81: BSplineCurve PolesCount=2 KnotsCount=2 Degree=1 IsPeriodic=0
    g82: BSplineCurve PolesCount=4 KnotsCount=2 Degree=3 IsPeriodic=0
    g83: BSplineCurve PolesCount=4 KnotsCount=2 Degree=3 IsPeriodic=0
    g84: BSplineCurve PolesCount=4 KnotsCount=2 Degree=3 IsPeriodic=0
    g85: BSplineCurve PolesCount=4 KnotsCount=2 Degree=3 IsPeriodic=0
    g86: BSplineCurve PolesCount=4 KnotsCount=2 Degree=3 IsPeriodic=0
    g87: BSplineCurve PolesCount=4 KnotsCount=2 Degree=3 IsPeriodic=0
    g88: BSplineCurve PolesCount=4 KnotsCount=2 Degree=3 IsPeriodic=0
    g89: BSplineCurve PolesCount=4 KnotsCount=2 Degree=3 IsPeriodic=0
    g90: BSplineCurve PolesCount=2 KnotsCount=2 Degree=1 IsPeriodic=0
    g91: BSplineCurve PolesCount=2 KnotsCount=2 Degree=1 IsPeriodic=0
    g92: BSplineCurve PolesCount=4 KnotsCount=2 Degree=3 IsPeriodic=0
    g93: BSplineCurve PolesCount=4 KnotsCount=2 Degree=3 IsPeriodic=0
    g94: BSplineCurve PolesCount=4 KnotsCount=2 Degree=3 IsPeriodic=0
    g95: BSplineCurve PolesCount=4 KnotsCount=2 Degree=3 IsPeriodic=0
    g96: BSplineCurve PolesCount=4 KnotsCount=2 Degree=3 IsPeriodic=0
    g97: BSplineCurve PolesCount=4 KnotsCount=2 Degree=3 IsPeriodic=0
    g98: BSplineCurve PolesCount=4 KnotsCount=2 Degree=3 IsPeriodic=0
    g99: BSplineCurve PolesCount=4 KnotsCount=2 Degree=3 IsPeriodic=0
    g100: BSplineCurve PolesCount=4 KnotsCount=2 Degree=3 IsPeriodic=0
    g101: BSplineCurve PolesCount=4 KnotsCount=2 Degree=3 IsPeriodic=0
    g102: BSplineCurve PolesCount=4 KnotsCount=2 Degree=3 IsPeriodic=0
    g103: BSplineCurve PolesCount=4 KnotsCount=2 Degree=3 IsPeriodic=0
    g104: BSplineCurve PolesCount=4 KnotsCount=2 Degree=3 IsPeriodic=0
    g105: BSplineCurve PolesCount=4 KnotsCount=2 Degree=3 IsPeriodic=0
    g106: BSplineCurve PolesCount=4 KnotsCount=2 Degree=3 IsPeriodic=0
    g107: BSplineCurve PolesCount=2 KnotsCount=2 Degree=1 IsPeriodic=0
    g108: BSplineCurve PolesCount=2 KnotsCount=2 Degree=1 IsPeriodic=0
    g109: BSplineCurve PolesCount=4 KnotsCount=2 Degree=3 IsPeriodic=0
    g110: BSplineCurve PolesCount=4 KnotsCount=2 Degree=3 IsPeriodic=0
    g111: BSplineCurve PolesCount=4 KnotsCount=2 Degree=3 IsPeriodic=0
    g112: BSplineCurve PolesCount=4 KnotsCount=2 Degree=3 IsPeriodic=0
    g113: BSplineCurve PolesCount=4 KnotsCount=2 Degree=3 IsPeriodic=0
    g114: BSplineCurve PolesCount=4 KnotsCount=2 Degree=3 IsPeriodic=0
    g115: BSplineCurve PolesCount=4 KnotsCount=2 Degree=3 IsPeriodic=0
    g116: BSplineCurve PolesCount=4 KnotsCount=2 Degree=3 IsPeriodic=0
    g117: BSplineCurve PolesCount=4 KnotsCount=2 Degree=3 IsPeriodic=0
    g118: BSplineCurve PolesCount=4 KnotsCount=2 Degree=3 IsPeriodic=0
    g119: BSplineCurve PolesCount=4 KnotsCount=2 Degree=3 IsPeriodic=0
    g120: BSplineCurve PolesCount=4 KnotsCount=2 Degree=3 IsPeriodic=0
    g121: BSplineCurve PolesCount=4 KnotsCount=2 Degree=3 IsPeriodic=0
    g122: BSplineCurve PolesCount=4 KnotsCount=2 Degree=3 IsPeriodic=0
    g123: BSplineCurve PolesCount=4 KnotsCount=2 Degree=3 IsPeriodic=0
    g124: BSplineCurve PolesCount=4 KnotsCount=2 Degree=3 IsPeriodic=0
    g125: BSplineCurve PolesCount=4 KnotsCount=2 Degree=3 IsPeriodic=0
    g126: BSplineCurve PolesCount=4 KnotsCount=2 Degree=3 IsPeriodic=0
    g127: BSplineCurve PolesCount=4 KnotsCount=2 Degree=3 IsPeriodic=0
    g128: BSplineCurve PolesCount=4 KnotsCount=2 Degree=3 IsPeriodic=0
    g129: BSplineCurve PolesCount=4 KnotsCount=2 Degree=3 IsPeriodic=0
    g130: BSplineCurve PolesCount=4 KnotsCount=2 Degree=3 IsPeriodic=0
    g131: BSplineCurve PolesCount=4 KnotsCount=2 Degree=3 IsPeriodic=0
    g132: BSplineCurve PolesCount=4 KnotsCount=2 Degree=3 IsPeriodic=0
    g133: BSplineCurve PolesCount=4 KnotsCount=2 Degree=3 IsPeriodic=0
    g134: BSplineCurve PolesCount=4 KnotsCount=2 Degree=3 IsPeriodic=0
    g135: BSplineCurve PolesCount=4 KnotsCount=2 Degree=3 IsPeriodic=0
    g136: BSplineCurve PolesCount=4 KnotsCount=2 Degree=3 IsPeriodic=0
    g137: BSplineCurve PolesCount=4 KnotsCount=2 Degree=3 IsPeriodic=0
    g138: BSplineCurve PolesCount=4 KnotsCount=2 Degree=3 IsPeriodic=0
    g139: BSplineCurve PolesCount=4 KnotsCount=2 Degree=3 IsPeriodic=0
    g140: BSplineCurve PolesCount=4 KnotsCount=2 Degree=3 IsPeriodic=0
    g141: BSplineCurve PolesCount=4 KnotsCount=2 Degree=3 IsPeriodic=0
    g142: BSplineCurve PolesCount=4 KnotsCount=2 Degree=3 IsPeriodic=0
    g143: BSplineCurve PolesCount=4 KnotsCount=2 Degree=3 IsPeriodic=0
    g144: BSplineCurve PolesCount=4 KnotsCount=2 Degree=3 IsPeriodic=0
    g145: BSplineCurve PolesCount=4 KnotsCount=2 Degree=3 IsPeriodic=0
    g146: BSplineCurve PolesCount=4 KnotsCount=2 Degree=3 IsPeriodic=0
    g147: BSplineCurve PolesCount=4 KnotsCount=2 Degree=3 IsPeriodic=0
    g148: BSplineCurve PolesCount=4 KnotsCount=2 Degree=3 IsPeriodic=0
    g149: BSplineCurve PolesCount=4 KnotsCount=2 Degree=3 IsPeriodic=0
    g150: BSplineCurve PolesCount=4 KnotsCount=2 Degree=3 IsPeriodic=0
    g151: BSplineCurve PolesCount=4 KnotsCount=2 Degree=3 IsPeriodic=0
    g152: BSplineCurve PolesCount=4 KnotsCount=2 Degree=3 IsPeriodic=0
    g153: BSplineCurve PolesCount=4 KnotsCount=2 Degree=3 IsPeriodic=0
    g154: BSplineCurve PolesCount=4 KnotsCount=2 Degree=3 IsPeriodic=0
    g155: BSplineCurve PolesCount=4 KnotsCount=2 Degree=3 IsPeriodic=0
    g156: BSplineCurve PolesCount=4 KnotsCount=2 Degree=3 IsPeriodic=0
    g157: BSplineCurve PolesCount=4 KnotsCount=2 Degree=3 IsPeriodic=0
    g158: BSplineCurve PolesCount=4 KnotsCount=2 Degree=3 IsPeriodic=0
    g159: BSplineCurve PolesCount=4 KnotsCount=2 Degree=3 IsPeriodic=0
    g160: BSplineCurve PolesCount=2 KnotsCount=2 Degree=1 IsPeriodic=0
    g161: BSplineCurve PolesCount=2 KnotsCount=2 Degree=1 IsPeriodic=0
    g162: BSplineCurve PolesCount=4 KnotsCount=2 Degree=3 IsPeriodic=0
    g163: BSplineCurve PolesCount=4 KnotsCount=2 Degree=3 IsPeriodic=0
    g164: BSplineCurve PolesCount=4 KnotsCount=2 Degree=3 IsPeriodic=0
    g165: BSplineCurve PolesCount=4 KnotsCount=2 Degree=3 IsPeriodic=0
    g166: BSplineCurve PolesCount=4 KnotsCount=2 Degree=3 IsPeriodic=0
    g167: BSplineCurve PolesCount=4 KnotsCount=2 Degree=3 IsPeriodic=0
    g168: BSplineCurve PolesCount=4 KnotsCount=2 Degree=3 IsPeriodic=0
    g169: BSplineCurve PolesCount=4 KnotsCount=2 Degree=3 IsPeriodic=0
    g170: BSplineCurve PolesCount=2 KnotsCount=2 Degree=1 IsPeriodic=0
    g171: BSplineCurve PolesCount=2 KnotsCount=2 Degree=1 IsPeriodic=0
    g172: BSplineCurve PolesCount=4 KnotsCount=2 Degree=3 IsPeriodic=0
    g173: BSplineCurve PolesCount=4 KnotsCount=2 Degree=3 IsPeriodic=0
    g174: BSplineCurve PolesCount=4 KnotsCount=2 Degree=3 IsPeriodic=0
    g175: BSplineCurve PolesCount=4 KnotsCount=2 Degree=3 IsPeriodic=0
    g176: BSplineCurve PolesCount=4 KnotsCount=2 Degree=3 IsPeriodic=0
    g177: BSplineCurve PolesCount=4 KnotsCount=2 Degree=3 IsPeriodic=0
    g178: BSplineCurve PolesCount=2 KnotsCount=2 Degree=1 IsPeriodic=0
    g179: BSplineCurve PolesCount=4 KnotsCount=2 Degree=3 IsPeriodic=0
    g180: BSplineCurve PolesCount=4 KnotsCount=2 Degree=3 IsPeriodic=0
    g181: BSplineCurve PolesCount=4 KnotsCount=2 Degree=3 IsPeriodic=0
    g182: BSplineCurve PolesCount=4 KnotsCount=2 Degree=3 IsPeriodic=0
    g183: BSplineCurve PolesCount=4 KnotsCount=2 Degree=3 IsPeriodic=0
    g184: BSplineCurve PolesCount=4 KnotsCount=2 Degree=3 IsPeriodic=0
    g185: BSplineCurve PolesCount=2 KnotsCount=2 Degree=1 IsPeriodic=0
    g186: BSplineCurve PolesCount=4 KnotsCount=2 Degree=3 IsPeriodic=0
    g187: BSplineCurve PolesCount=4 KnotsCount=2 Degree=3 IsPeriodic=0
    g188: BSplineCurve PolesCount=2 KnotsCount=2 Degree=1 IsPeriodic=0
    g189: BSplineCurve PolesCount=2 KnotsCount=2 Degree=1 IsPeriodic=0
    g190: BSplineCurve PolesCount=4 KnotsCount=2 Degree=3 IsPeriodic=0
    g191: BSplineCurve PolesCount=4 KnotsCount=2 Degree=3 IsPeriodic=0
    g192: BSplineCurve PolesCount=4 KnotsCount=2 Degree=3 IsPeriodic=0
    g193: BSplineCurve PolesCount=4 KnotsCount=2 Degree=3 IsPeriodic=0
  constraints (200):
    c: Coincident(g0,g1)
    c: Coincident(g1,g2)
    c: Coincident(g2,g3)
    c: Coincident(g3,g4)
    c: Coincident(g4,g5)
    c: Coincident(g5,g6)
    c: Coincident(g6,g7)
    c: Coincident(g7,g8)
    c: Coincident(g8,g9)
    c: Coincident(g9,g10)
    c: Coincident(g10,g11)
    c: Coincident(g11,g12)
    c: Coincident(g12,g13)
    c: Coincident(g13,g14)
    c: Coincident(g14,g15)
    c: Coincident(g15,g16)
    c: Coincident(g16,g17)
    c: Coincident(g17,g0)
    c: Coincident(g18,g19)
    c: Coincident(g19,g20)
    c: Coincident(g20,g21)
    c: Coincident(g21,g22)
    c: Coincident(g22,g23)
    c: Coincident(g23,g24)
    c: Coincident(g24,g25)
    c: Coincident(g25,g26)
    c: Coincident(g26,g27)
    c: Coincident(g27,g28)
    c: Coincident(g28,g29)
    c: Coincident(g29,g30)
    c: Coincident(g30,g18)
    c: Coincident(g31,g32)
    c: Coincident(g32,g33)
    c: Coincident(g33,g34)
    c: Coincident(g34,g35)
    c: Coincident(g35,g36)
    c: Coincident(g36,g37)
    c: Coincident(g37,g38)
    c: Coincident(g38,g39)
    c: Coincident(g39,g40)
    c: Coincident(g40,g41)
    c: Coincident(g41,g42)
    c: Coincident(g42,g43)
    c: Coincident(g43,g44)
    c: Coincident(g44,g45)
    c: Coincident(g45,g46)
    c: Coincident(g46,g47)
    c: Coincident(g47,g48)
    c: Coincident(g48,g49)
    c: Coincident(g49,g50)
    c: Coincident(g50,g51)
    c: Coincident(g51,g52)
    c: Coincident(g52,g53)
    c: Coincident(g53,g54)
    c: Coincident(g54,g55)
    c: Coincident(g55,g56)
    c: Coincident(g56,g57)
    c: Coincident(g57,g58)
    c: Coincident(g58,g59)
    c: Coincident(g59,g60)
    c: Coincident(g60,g61)
    c: Coincident(g61,g62)
    c: Coincident(g62,g63)
    c: Coincident(g63,g64)
    c: Coincident(g64,g65)
    c: Coincident(g65,g66)
    c: Coincident(g66,g67)
    c: Coincident(g67,g68)
    c: Coincident(g68,g69)
    c: Coincident(g69,g70)
    c: Coincident(g70,g71)
    c: Coincident(g71,g72)
    c: Coincident(g72,g73)
    c: Coincident(g73,g74)
    c: Coincident(g74,g75)
    c: Coincident(g75,g76)
    c: Coincident(g76,g77)
    c: Coincident(g77,g78)
    c: Coincident(g78,g79)
    c: Coincident(g79,g80)
    c: Coincident(g80,g31)
    c: Coincident(g81,g82)
    c: Coincident(g82,g83)
    c: Coincident(g83,g84)
    c: Coincident(g84,g81)
    c: Coincident(g85,g86)
    c: Coincident(g86,g87)
    c: Coincident(g87,g88)
    c: Coincident(g88,g89)
    c: Coincident(g89,g90)
    c: Coincident(g90,g91)
    c: Coincident(g91,g92)
    c: Coincident(g92,g93)
    c: Coincident(g93,g94)
    c: Coincident(g94,g95)
    c: Coincident(g95,g96)
    c: Coincident(g96,g97)
    c: Coincident(g97,g98)
    c: Coincident(g98,g99)
    c: Coincident(g99,g100)
    c: Coincident(g100,g85)
    c: Coincident(g101,g102)
    c: Coincident(g102,g103)
    c: Coincident(g103,g104)
    c: Coincident(g104,g105)
    c: Coincident(g105,g106)
    c: Coincident(g106,g107)
    c: Coincident(g107,g108)
    c: Coincident(g108,g109)
    c: Coincident(g109,g110)
    c: Coincident(g110,g101)
    c: Coincident(g111,g112)
    c: Coincident(g112,g113)
    c: Coincident(g113,g114)
    c: Coincident(g114,g115)
    c: Coincident(g115,g111)
    c: Coincident(g116,g117)
    c: Coincident(g117,g118)
    c: Coincident(g118,g119)
    c: Coincident(g119,g120)
    c: Coincident(g120,g121)
    c: Coincident(g121,g122)
    c: Coincident(g122,g123)
    c: Coincident(g123,g124)
    c: Coincident(g124,g125)
    c: Coincident(g125,g126)
    c: Coincident(g126,g127)
    c: Coincident(g127,g128)
    c: Coincident(g128,g129)
    c: Coincident(g129,g130)
    c: Coincident(g130,g131)
    c: Coincident(g131,g132)
    c: Coincident(g132,g133)
    c: Coincident(g133,g134)
    c: Coincident(g134,g135)
    c: Coincident(g135,g136)
    c: Coincident(g136,g137)
    c: Coincident(g137,g138)
    c: Coincident(g138,g139)
    c: Coincident(g139,g140)
    c: Coincident(g140,g141)
    c: Coincident(g141,g142)
    c: Coincident(g142,g143)
    c: Coincident(g143,g144)
    c: Coincident(g144,g145)
    c: Coincident(g145,g116)
    c: Coincident(g146,g147)
    c: Coincident(g147,g148)
    c: Coincident(g148,g149)
    c: Coincident(g149,g150)
    c: Coincident(g150,g151)
    c: Coincident(g151,g152)
    c: Coincident(g152,g153)
    c: Coincident(g153,g154)
    c: Coincident(g154,g155)
    c: Coincident(g155,g156)
    c: Coincident(g156,g157)
    c: Coincident(g157,g146)
    c: Coincident(g158,g159)
    c: Coincident(g159,g160)
    c: Coincident(g160,g161)
    c: Coincident(g161,g162)
    c: Coincident(g162,g163)
    c: Coincident(g163,g164)
    c: Coincident(g164,g165)
    c: Coincident(g165,g166)
    c: Coincident(g166,g167)
    c: Coincident(g167,g168)
    c: Coincident(g168,g169)
    c: Coincident(g169,g170)
    c: Coincident(g170,g171)
    c: Coincident(g171,g172)
    c: Coincident(g172,g173)
    c: Coincident(g173,g174)
    c: Coincident(g174,g175)
    c: Coincident(g175,g176)
    c: Coincident(g176,g177)
    c: Coincident(g177,g158)
    c: Coincident(g178,g179)
    c: Coincident(g179,g180)
    c: Coincident(g180,g181)
    c: Coincident(g181,g182)
    c: Coincident(g182,g183)
    c: Coincident(g183,g184)
    c: Coincident(g184,g178)
    c: Coincident(g185,g186)
    c: Coincident(g186,g187)
    c: Coincident(g187,g188)
    c: Coincident(g188,g189)
    c: Coincident(g189,g190)
    c: Coincident(g190,g191)
    c: Coincident(g191,g192)
    c: Coincident(g192,g193)
    c: Coincident(g193,g185)
    c: Coincident(g79,g31)
    c: Coincident(g185,g185)
    c: Coincident(g16,g0)
    c: Coincident(g18,g18)
    c: Coincident(g81,g81)
    c: Coincident(g178,g178)
FEATURE [Sketcher::SketchObject] Sketch014  label="Saint-Sketch"
  ArcFitTolerance = 1e-06
  FullyConstrained = false
  MakeInternals = false
  sketch-geometry (563):
    g0: BSplineCurve PolesCount=4 KnotsCount=2 Degree=3 IsPeriodic=0
    g1: BSplineCurve PolesCount=4 KnotsCount=2 Degree=3 IsPeriodic=0
    g2: BSplineCurve PolesCount=4 KnotsCount=2 Degree=3 IsPeriodic=0
    g3: BSplineCurve PolesCount=4 KnotsCount=2 Degree=3 IsPeriodic=0
    g4: BSplineCurve PolesCount=4 KnotsCount=2 Degree=3 IsPeriodic=0
    g5: BSplineCurve PolesCount=4 KnotsCount=2 Degree=3 IsPeriodic=0
    g6: BSplineCurve PolesCount=4 KnotsCount=2 Degree=3 IsPeriodic=0
    g7: BSplineCurve PolesCount=4 KnotsCount=2 Degree=3 IsPeriodic=0
    g8: BSplineCurve PolesCount=4 KnotsCount=2 Degree=3 IsPeriodic=0
    g9: BSplineCurve PolesCount=4 KnotsCount=2 Degree=3 IsPeriodic=0
    g10: BSplineCurve PolesCount=4 KnotsCount=2 Degree=3 IsPeriodic=0
    g11: BSplineCurve PolesCount=4 KnotsCount=2 Degree=3 IsPeriodic=0
    g12: BSplineCurve PolesCount=4 KnotsCount=2 Degree=3 IsPeriodic=0
    g13: BSplineCurve PolesCount=4 KnotsCount=2 Degree=3 IsPeriodic=0
    g14: BSplineCurve PolesCount=4 KnotsCount=2 Degree=3 IsPeriodic=0
    g15: BSplineCurve PolesCount=4 KnotsCount=2 Degree=3 IsPeriodic=0
    g16: BSplineCurve PolesCount=4 KnotsCount=2 Degree=3 IsPeriodic=0
    g17: BSplineCurve PolesCount=4 KnotsCount=2 Degree=3 IsPeriodic=0
    g18: BSplineCurve PolesCount=4 KnotsCount=2 Degree=3 IsPeriodic=0
    g19: BSplineCurve PolesCount=4 KnotsCount=2 Degree=3 IsPeriodic=0
    g20: BSplineCurve PolesCount=4 KnotsCount=2 Degree=3 IsPeriodic=0
    g21: BSplineCurve PolesCount=4 KnotsCount=2 Degree=3 IsPeriodic=0
    g22: BSplineCurve PolesCount=4 KnotsCount=2 Degree=3 IsPeriodic=0
    g23: BSplineCurve PolesCount=4 KnotsCount=2 Degree=3 IsPeriodic=0
    g24: BSplineCurve PolesCount=4 KnotsCount=2 Degree=3 IsPeriodic=0
    g25: BSplineCurve PolesCount=4 KnotsCount=2 Degree=3 IsPeriodic=0
    g26: BSplineCurve PolesCount=4 KnotsCount=2 Degree=3 IsPeriodic=0
    g27: BSplineCurve PolesCount=4 KnotsCount=2 Degree=3 IsPeriodic=0
    g28: BSplineCurve PolesCount=4 KnotsCount=2 Degree=3 IsPeriodic=0
    g29: BSplineCurve PolesCount=4 KnotsCount=2 Degree=3 IsPeriodic=0
    g30: BSplineCurve PolesCount=4 KnotsCount=2 Degree=3 IsPeriodic=0
    g31: BSplineCurve PolesCount=4 KnotsCount=2 Degree=3 IsPeriodic=0
    g32: BSplineCurve PolesCount=4 KnotsCount=2 Degree=3 IsPeriodic=0
    g33: BSplineCurve PolesCount=4 KnotsCount=2 Degree=3 IsPeriodic=0
    g34: BSplineCurve PolesCount=4 KnotsCount=2 Degree=3 IsPeriodic=0
    g35: BSplineCurve PolesCount=4 KnotsCount=2 Degree=3 IsPeriodic=0
    g36: BSplineCurve PolesCount=4 KnotsCount=2 Degree=3 IsPeriodic=0
    g37: BSplineCurve PolesCount=4 KnotsCount=2 Degree=3 IsPeriodic=0
    g38: BSplineCurve PolesCount=2 KnotsCount=2 Degree=1 IsPeriodic=0
    g39: BSplineCurve PolesCount=2 KnotsCount=2 Degree=1 IsPeriodic=0
    g40: BSplineCurve PolesCount=4 KnotsCount=2 Degree=3 IsPeriodic=0
    g41: BSplineCurve PolesCount=2 KnotsCount=2 Degree=1 IsPeriodic=0
    g42: BSplineCurve PolesCount=2 KnotsCount=2 Degree=1 IsPeriodic=0
    g43: BSplineCurve PolesCount=4 KnotsCount=2 Degree=3 IsPeriodic=0
    g44: BSplineCurve PolesCount=4 KnotsCount=2 Degree=3 IsPeriodic=0
    g45: BSplineCurve PolesCount=4 KnotsCount=2 Degree=3 IsPeriodic=0
    g46: BSplineCurve PolesCount=4 KnotsCount=2 Degree=3 IsPeriodic=0
    g47: BSplineCurve PolesCount=2 KnotsCount=2 Degree=1 IsPeriodic=0
    g48: BSplineCurve PolesCount=2 KnotsCount=2 Degree=1 IsPeriodic=0
    g49: BSplineCurve PolesCount=4 KnotsCount=2 Degree=3 IsPeriodic=0
    g50: BSplineCurve PolesCount=4 KnotsCount=2 Degree=3 IsPeriodic=0
    g51: BSplineCurve PolesCount=4 KnotsCount=2 Degree=3 IsPeriodic=0
    g52: BSplineCurve PolesCount=4 KnotsCount=2 Degree=3 IsPeriodic=0
    g53: BSplineCurve PolesCount=4 KnotsCount=2 Degree=3 IsPeriodic=0
    g54: BSplineCurve PolesCount=4 KnotsCount=2 Degree=3 IsPeriodic=0
    g55: BSplineCurve PolesCount=4 KnotsCount=2 Degree=3 IsPeriodic=0
    g56: BSplineCurve PolesCount=4 KnotsCount=2 Degree=3 IsPeriodic=0
    g57: BSplineCurve PolesCount=2 KnotsCount=2 Degree=1 IsPeriodic=0
    g58: BSplineCurve PolesCount=2 KnotsCount=2 Degree=1 IsPeriodic=0
    g59: BSplineCurve PolesCount=4 KnotsCount=2 Degree=3 IsPeriodic=0
    g60: BSplineCurve PolesCount=4 KnotsCount=2 Degree=3 IsPeriodic=0
    g61: BSplineCurve PolesCount=4 KnotsCount=2 Degree=3 IsPeriodic=0
    g62: BSplineCurve PolesCount=4 KnotsCount=2 Degree=3 IsPeriodic=0
    g63: BSplineCurve PolesCount=4 KnotsCount=2 Degree=3 IsPeriodic=0
    g64: BSplineCurve PolesCount=4 KnotsCount=2 Degree=3 IsPeriodic=0
    g65: BSplineCurve PolesCount=4 KnotsCount=2 Degree=3 IsPeriodic=0
    g66: BSplineCurve PolesCount=4 KnotsCount=2 Degree=3 IsPeriodic=0
    g67: BSplineCurve PolesCount=4 KnotsCount=2 Degree=3 IsPeriodic=0
    g68: BSplineCurve PolesCount=4 KnotsCount=2 Degree=3 IsPeriodic=0
    g69: BSplineCurve PolesCount=4 KnotsCount=2 Degree=3 IsPeriodic=0
    g70: BSplineCurve PolesCount=4 KnotsCount=2 Degree=3 IsPeriodic=0
    g71: BSplineCurve PolesCount=4 KnotsCount=2 Degree=3 IsPeriodic=0
    g72: BSplineCurve PolesCount=4 KnotsCount=2 Degree=3 IsPeriodic=0
    g73: BSplineCurve PolesCount=2 KnotsCount=2 Degree=1 IsPeriodic=0
    g74: BSplineCurve PolesCount=4 KnotsCount=2 Degree=3 IsPeriodic=0
    g75: BSplineCurve PolesCount=4 KnotsCount=2 Degree=3 IsPeriodic=0
    g76: BSplineCurve PolesCount=4 KnotsCount=2 Degree=3 IsPeriodic=0
    g77: BSplineCurve PolesCount=4 KnotsCount=2 Degree=3 IsPeriodic=0
    g78: BSplineCurve PolesCount=4 KnotsCount=2 Degree=3 IsPeriodic=0
    g79: BSplineCurve PolesCount=4 KnotsCount=2 Degree=3 IsPeriodic=0
    g80: BSplineCurve PolesCount=2 KnotsCount=2 Degree=1 IsPeriodic=0
    g81: BSplineCurve PolesCount=4 KnotsCount=2 Degree=3 IsPeriodic=0
    g82: BSplineCurve PolesCount=2 KnotsCount=2 Degree=1 IsPeriodic=0
    g83: BSplineCurve PolesCount=2 KnotsCount=2 Degree=1 IsPeriodic=0
    g84: BSplineCurve PolesCount=2 KnotsCount=2 Degree=1 IsPeriodic=0
    g85: BSplineCurve PolesCount=2 KnotsCount=2 Degree=1 IsPeriodic=0
    g86: BSplineCurve PolesCount=4 KnotsCount=2 Degree=3 IsPeriodic=0
    g87: BSplineCurve PolesCount=4 KnotsCount=2 Degree=3 IsPeriodic=0
    g88: BSplineCurve PolesCount=4 KnotsCount=2 Degree=3 IsPeriodic=0
    g89: BSplineCurve PolesCount=4 KnotsCount=2 Degree=3 IsPeriodic=0
    g90: BSplineCurve PolesCount=4 KnotsCount=2 Degree=3 IsPeriodic=0
    g91: BSplineCurve PolesCount=4 KnotsCount=2 Degree=3 IsPeriodic=0
    g92: BSplineCurve PolesCount=2 KnotsCount=2 Degree=1 IsPeriodic=0
    g93: BSplineCurve PolesCount=4 KnotsCount=2 Degree=3 IsPeriodic=0
    g94: BSplineCurve PolesCount=4 KnotsCount=2 Degree=3 IsPeriodic=0
    g95: BSplineCurve PolesCount=4 KnotsCount=2 Degree=3 IsPeriodic=0
    g96: BSplineCurve PolesCount=4 KnotsCount=2 Degree=3 IsPeriodic=0
    g97: BSplineCurve PolesCount=4 KnotsCount=2 Degree=3 IsPeriodic=0
    g98: BSplineCurve PolesCount=2 KnotsCount=2 Degree=1 IsPeriodic=0
    g99: BSplineCurve PolesCount=2 KnotsCount=2 Degree=1 IsPeriodic=0
    g100: BSplineCurve PolesCount=4 KnotsCount=2 Degree=3 IsPeriodic=0
    g101: BSplineCurve PolesCount=4 KnotsCount=2 Degree=3 IsPeriodic=0
    g102: BSplineCurve PolesCount=4 KnotsCount=2 Degree=3 IsPeriodic=0
    g103: BSplineCurve PolesCount=4 KnotsCount=2 Degree=3 IsPeriodic=0
    g104: BSplineCurve PolesCount=4 KnotsCount=2 Degree=3 IsPeriodic=0
    g105: BSplineCurve PolesCount=4 KnotsCount=2 Degree=3 IsPeriodic=0
    g106: BSplineCurve PolesCount=4 KnotsCount=2 Degree=3 IsPeriodic=0
    g107: BSplineCurve PolesCount=4 KnotsCount=2 Degree=3 IsPeriodic=0
    g108: BSplineCurve PolesCount=4 KnotsCount=2 Degree=3 IsPeriodic=0
    g109: BSplineCurve PolesCount=4 KnotsCount=2 Degree=3 IsPeriodic=0
    g110: BSplineCurve PolesCount=4 KnotsCount=2 Degree=3 IsPeriodic=0
    g111: BSplineCurve PolesCount=4 KnotsCount=2 Degree=3 IsPeriodic=0
    g112: BSplineCurve PolesCount=4 KnotsCount=2 Degree=3 IsPeriodic=0
    g113: BSplineCurve PolesCount=2 KnotsCount=2 Degree=1 IsPeriodic=0
    g114: BSplineCurve PolesCount=2 KnotsCount=2 Degree=1 IsPeriodic=0
    g115: BSplineCurve PolesCount=4 KnotsCount=2 Degree=3 IsPeriodic=0
    g116: BSplineCurve PolesCount=4 KnotsCount=2 Degree=3 IsPeriodic=0
    g117: BSplineCurve PolesCount=4 KnotsCount=2 Degree=3 IsPeriodic=0
    g118: BSplineCurve PolesCount=4 KnotsCount=2 Degree=3 IsPeriodic=0
    g119: BSplineCurve PolesCount=4 KnotsCount=2 Degree=3 IsPeriodic=0
    g120: BSplineCurve PolesCount=4 KnotsCount=2 Degree=3 IsPeriodic=0
    g121: BSplineCurve PolesCount=4 KnotsCount=2 Degree=3 IsPeriodic=0
    g122: BSplineCurve PolesCount=4 KnotsCount=2 Degree=3 IsPeriodic=0
    g123: BSplineCurve PolesCount=4 KnotsCount=2 Degree=3 IsPeriodic=0
    g124: BSplineCurve PolesCount=4 KnotsCount=2 Degree=3 IsPeriodic=0
    g125: BSplineCurve PolesCount=4 KnotsCount=2 Degree=3 IsPeriodic=0
    g126: BSplineCurve PolesCount=4 KnotsCount=2 Degree=3 IsPeriodic=0
    g127: BSplineCurve PolesCount=4 KnotsCount=2 Degree=3 IsPeriodic=0
    g128: BSplineCurve PolesCount=4 KnotsCount=2 Degree=3 IsPeriodic=0
    g129: BSplineCurve PolesCount=4 KnotsCount=2 Degree=3 IsPeriodic=0
    g130: BSplineCurve PolesCount=4 KnotsCount=2 Degree=3 IsPeriodic=0
    g131: BSplineCurve PolesCount=4 KnotsCount=2 Degree=3 IsPeriodic=0
    g132: BSplineCurve PolesCount=4 KnotsCount=2 Degree=3 IsPeriodic=0
    g133: BSplineCurve PolesCount=4 KnotsCount=2 Degree=3 IsPeriodic=0
    g134: BSplineCurve PolesCount=4 KnotsCount=2 Degree=3 IsPeriodic=0
    g135: BSplineCurve PolesCount=4 KnotsCount=2 Degree=3 IsPeriodic=0
    g136: BSplineCurve PolesCount=2 KnotsCount=2 Degree=1 IsPeriodic=0
    g137: BSplineCurve PolesCount=2 KnotsCount=2 Degree=1 IsPeriodic=0
    g138: BSplineCurve PolesCount=4 KnotsCount=2 Degree=3 IsPeriodic=0
    g139: BSplineCurve PolesCount=2 KnotsCount=2 Degree=1 IsPeriodic=0
    g140: BSplineCurve PolesCount=2 KnotsCount=2 Degree=1 IsPeriodic=0
    g141: BSplineCurve PolesCount=4 KnotsCount=2 Degree=3 IsPeriodic=0
    g142: BSplineCurve PolesCount=4 KnotsCount=2 Degree=3 IsPeriodic=0
    g143: BSplineCurve PolesCount=4 KnotsCount=2 Degree=3 IsPeriodic=0
    g144: BSplineCurve PolesCount=4 KnotsCount=2 Degree=3 IsPeriodic=0
    g145: BSplineCurve PolesCount=2 KnotsCount=2 Degree=1 IsPeriodic=0
    g146: BSplineCurve PolesCount=2 KnotsCount=2 Degree=1 IsPeriodic=0
    g147: BSplineCurve PolesCount=4 KnotsCount=2 Degree=3 IsPeriodic=0
    g148: BSplineCurve PolesCount=4 KnotsCount=2 Degree=3 IsPeriodic=0
    g149: BSplineCurve PolesCount=2 KnotsCount=2 Degree=1 IsPeriodic=0
    g150: BSplineCurve PolesCount=2 KnotsCount=2 Degree=1 IsPeriodic=0
    g151: BSplineCurve PolesCount=4 KnotsCount=2 Degree=3 IsPeriodic=0
    g152: BSplineCurve PolesCount=4 KnotsCount=2 Degree=3 IsPeriodic=0
    g153: BSplineCurve PolesCount=4 KnotsCount=2 Degree=3 IsPeriodic=0
    g154: BSplineCurve PolesCount=4 KnotsCount=2 Degree=3 IsPeriodic=0
    g155: BSplineCurve PolesCount=2 KnotsCount=2 Degree=1 IsPeriodic=0
    g156: BSplineCurve PolesCount=2 KnotsCount=2 Degree=1 IsPeriodic=0
    g157: BSplineCurve PolesCount=4 KnotsCount=2 Degree=3 IsPeriodic=0
    g158: BSplineCurve PolesCount=4 KnotsCount=2 Degree=3 IsPeriodic=0
    g159: BSplineCurve PolesCount=4 KnotsCount=2 Degree=3 IsPeriodic=0
    g160: BSplineCurve PolesCount=4 KnotsCount=2 Degree=3 IsPeriodic=0
    g161: BSplineCurve PolesCount=4 KnotsCount=2 Degree=3 IsPeriodic=0
    g162: BSplineCurve PolesCount=4 KnotsCount=2 Degree=3 IsPeriodic=0
    g163: BSplineCurve PolesCount=4 KnotsCount=2 Degree=3 IsPeriodic=0
    g164: BSplineCurve PolesCount=4 KnotsCount=2 Degree=3 IsPeriodic=0
    g165: BSplineCurve PolesCount=4 KnotsCount=2 Degree=3 IsPeriodic=0
    g166: BSplineCurve PolesCount=4 KnotsCount=2 Degree=3 IsPeriodic=0
    g167: BSplineCurve PolesCount=4 KnotsCount=2 Degree=3 IsPeriodic=0
    g168: BSplineCurve PolesCount=4 KnotsCount=2 Degree=3 IsPeriodic=0
    g169: BSplineCurve PolesCount=4 KnotsCount=2 Degree=3 IsPeriodic=0
    g170: BSplineCurve PolesCount=2 KnotsCount=2 Degree=1 IsPeriodic=0
    g171: BSplineCurve PolesCount=2 KnotsCount=2 Degree=1 IsPeriodic=0
    g172: BSplineCurve PolesCount=2 KnotsCount=2 Degree=1 IsPeriodic=0
    g173: BSplineCurve PolesCount=2 KnotsCount=2 Degree=1 IsPeriodic=0
    g174: BSplineCurve PolesCount=4 KnotsCount=2 Degree=3 IsPeriodic=0
    g175: BSplineCurve PolesCount=2 KnotsCount=2 Degree=1 IsPeriodic=0
    g176: BSplineCurve PolesCount=2 KnotsCount=2 Degree=1 IsPeriodic=0
    g177: BSplineCurve PolesCount=2 KnotsCount=2 Degree=1 IsPeriodic=0
    g178: BSplineCurve PolesCount=4 KnotsCount=2 Degree=3 IsPeriodic=0
    g179: BSplineCurve PolesCount=4 KnotsCount=2 Degree=3 IsPeriodic=0
    g180: BSplineCurve PolesCount=4 KnotsCount=2 Degree=3 IsPeriodic=0
    g181: BSplineCurve PolesCount=4 KnotsCount=2 Degree=3 IsPeriodic=0
    g182: BSplineCurve PolesCount=4 KnotsCount=2 Degree=3 IsPeriodic=0
    g183: BSplineCurve PolesCount=4 KnotsCount=2 Degree=3 IsPeriodic=0
    g184: BSplineCurve PolesCount=4 KnotsCount=2 Degree=3 IsPeriodic=0
    g185: BSplineCurve PolesCount=2 KnotsCount=2 Degree=1 IsPeriodic=0
    g186: BSplineCurve PolesCount=2 KnotsCount=2 Degree=1 IsPeriodic=0
    g187: BSplineCurve PolesCount=4 KnotsCount=2 Degree=3 IsPeriodic=0
    g188: BSplineCurve PolesCount=4 KnotsCount=2 Degree=3 IsPeriodic=0
    g189: BSplineCurve PolesCount=2 KnotsCount=2 Degree=1 IsPeriodic=0
    g190: BSplineCurve PolesCount=2 KnotsCount=2 Degree=1 IsPeriodic=0
    g191: BSplineCurve PolesCount=4 KnotsCount=2 Degree=3 IsPeriodic=0
    g192: BSplineCurve PolesCount=4 KnotsCount=2 Degree=3 IsPeriodic=0
    g193: BSplineCurve PolesCount=4 KnotsCount=2 Degree=3 IsPeriodic=0
    g194: BSplineCurve PolesCount=4 KnotsCount=2 Degree=3 IsPeriodic=0
    g195: BSplineCurve PolesCount=4 KnotsCount=2 Degree=3 IsPeriodic=0
    g196: BSplineCurve PolesCount=4 KnotsCount=2 Degree=3 IsPeriodic=0
    g197: BSplineCurve PolesCount=4 KnotsCount=2 Degree=3 IsPeriodic=0
    g198: BSplineCurve PolesCount=4 KnotsCount=2 Degree=3 IsPeriodic=0
    g199: BSplineCurve PolesCount=4 KnotsCount=2 Degree=3 IsPeriodic=0
    g200: BSplineCurve PolesCount=4 KnotsCount=2 Degree=3 IsPeriodic=0
    g201: BSplineCurve PolesCount=4 KnotsCount=2 Degree=3 IsPeriodic=0
    g202: BSplineCurve PolesCount=4 KnotsCount=2 Degree=3 IsPeriodic=0
    g203: BSplineCurve PolesCount=4 KnotsCount=2 Degree=3 IsPeriodic=0
    g204: BSplineCurve PolesCount=4 KnotsCount=2 Degree=3 IsPeriodic=0
    g205: BSplineCurve PolesCount=4 KnotsCount=2 Degree=3 IsPeriodic=0
    g206: BSplineCurve PolesCount=4 KnotsCount=2 Degree=3 IsPeriodic=0
    g207: BSplineCurve PolesCount=4 KnotsCount=2 Degree=3 IsPeriodic=0
    g208: BSplineCurve PolesCount=4 KnotsCount=2 Degree=3 IsPeriodic=0
    g209: BSplineCurve PolesCount=4 KnotsCount=2 Degree=3 IsPeriodic=0
    g210: BSplineCurve PolesCount=4 KnotsCount=2 Degree=3 IsPeriodic=0
    g211: BSplineCurve PolesCount=2 KnotsCount=2 Degree=1 IsPeriodic=0
    g212: BSplineCurve PolesCount=2 KnotsCount=2 Degree=1 IsPeriodic=0
    g213: BSplineCurve PolesCount=4 KnotsCount=2 Degree=3 IsPeriodic=0
    g214: BSplineCurve PolesCount=4 KnotsCount=2 Degree=3 IsPeriodic=0
    g215: BSplineCurve PolesCount=4 KnotsCount=2 Degree=3 IsPeriodic=0
    g216: BSplineCurve PolesCount=4 KnotsCount=2 Degree=3 IsPeriodic=0
    g217: BSplineCurve PolesCount=4 KnotsCount=2 Degree=3 IsPeriodic=0
    g218: BSplineCurve PolesCount=4 KnotsCount=2 Degree=3 IsPeriodic=0
    g219: BSplineCurve PolesCount=4 KnotsCount=2 Degree=3 IsPeriodic=0
    g220: BSplineCurve PolesCount=2 KnotsCount=2 Degree=1 IsPeriodic=0
    g221: BSplineCurve PolesCount=4 KnotsCount=2 Degree=3 IsPeriodic=0
    g222: BSplineCurve PolesCount=2 KnotsCount=2 Degree=1 IsPeriodic=0
    g223: BSplineCurve PolesCount=2 KnotsCount=2 Degree=1 IsPeriodic=0
    g224: BSplineCurve PolesCount=4 KnotsCount=2 Degree=3 IsPeriodic=0
    g225: BSplineCurve PolesCount=4 KnotsCount=2 Degree=3 IsPeriodic=0
    g226: BSplineCurve PolesCount=4 KnotsCount=2 Degree=3 IsPeriodic=0
    g227: BSplineCurve PolesCount=4 KnotsCount=2 Degree=3 IsPeriodic=0
    g228: BSplineCurve PolesCount=4 KnotsCount=2 Degree=3 IsPeriodic=0
    g229: BSplineCurve PolesCount=4 KnotsCount=2 Degree=3 IsPeriodic=0
    g230: BSplineCurve PolesCount=4 KnotsCount=2 Degree=3 IsPeriodic=0
    g231: BSplineCurve PolesCount=4 KnotsCount=2 Degree=3 IsPeriodic=0
    g232: BSplineCurve PolesCount=2 KnotsCount=2 Degree=1 IsPeriodic=0
    g233: BSplineCurve PolesCount=2 KnotsCount=2 Degree=1 IsPeriodic=0
    g234: BSplineCurve PolesCount=4 KnotsCount=2 Degree=3 IsPeriodic=0
    g235: BSplineCurve PolesCount=2 KnotsCount=2 Degree=1 IsPeriodic=0
    g236: BSplineCurve PolesCount=2 KnotsCount=2 Degree=1 IsPeriodic=0
    g237: BSplineCurve PolesCount=2 KnotsCount=2 Degree=1 IsPeriodic=0
    g238: BSplineCurve PolesCount=2 KnotsCount=2 Degree=1 IsPeriodic=0
    g239: BSplineCurve PolesCount=4 KnotsCount=2 Degree=3 IsPeriodic=0
    g240: BSplineCurve PolesCount=4 KnotsCount=2 Degree=3 IsPeriodic=0
    g241: BSplineCurve PolesCount=4 KnotsCount=2 Degree=3 IsPeriodic=0
    g242: BSplineCurve PolesCount=4 KnotsCount=2 Degree=3 IsPeriodic=0
    g243: BSplineCurve PolesCount=4 KnotsCount=2 Degree=3 IsPeriodic=0
    g244: BSplineCurve PolesCount=4 KnotsCount=2 Degree=3 IsPeriodic=0
    g245: BSplineCurve PolesCount=4 KnotsCount=2 Degree=3 IsPeriodic=0
    g246: BSplineCurve PolesCount=4 KnotsCount=2 Degree=3 IsPeriodic=0
    g247: BSplineCurve PolesCount=4 KnotsCount=2 Degree=3 IsPeriodic=0
    g248: BSplineCurve PolesCount=2 KnotsCount=2 Degree=1 IsPeriodic=0
    g249: BSplineCurve PolesCount=2 KnotsCount=2 Degree=1 IsPeriodic=0
    g250: BSplineCurve PolesCount=4 KnotsCount=2 Degree=3 IsPeriodic=0
    g251: BSplineCurve PolesCount=4 KnotsCount=2 Degree=3 IsPeriodic=0
    g252: BSplineCurve PolesCount=4 KnotsCount=2 Degree=3 IsPeriodic=0
    g253: BSplineCurve PolesCount=4 KnotsCount=2 Degree=3 IsPeriodic=0
    g254: BSplineCurve PolesCount=4 KnotsCount=2 Degree=3 IsPeriodic=0
    g255: BSplineCurve PolesCount=4 KnotsCount=2 Degree=3 IsPeriodic=0
    g256: BSplineCurve PolesCount=4 KnotsCount=2 Degree=3 IsPeriodic=0
    g257: BSplineCurve PolesCount=2 KnotsCount=2 Degree=1 IsPeriodic=0
    g258: BSplineCurve PolesCount=2 KnotsCount=2 Degree=1 IsPeriodic=0
    g259: BSplineCurve PolesCount=2 KnotsCount=2 Degree=1 IsPeriodic=0
    g260: BSplineCurve PolesCount=4 KnotsCount=2 Degree=3 IsPeriodic=0
    g261: BSplineCurve PolesCount=4 KnotsCount=2 Degree=3 IsPeriodic=0
    g262: BSplineCurve PolesCount=4 KnotsCount=2 Degree=3 IsPeriodic=0
    g263: BSplineCurve PolesCount=2 KnotsCount=2 Degree=1 IsPeriodic=0
    g264: BSplineCurve PolesCount=2 KnotsCount=2 Degree=1 IsPeriodic=0
    g265: BSplineCurve PolesCount=4 KnotsCount=2 Degree=3 IsPeriodic=0
    g266: BSplineCurve PolesCount=4 KnotsCount=2 Degree=3 IsPeriodic=0
    g267: BSplineCurve PolesCount=2 KnotsCount=2 Degree=1 IsPeriodic=0
    g268: BSplineCurve PolesCount=4 KnotsCount=2 Degree=3 IsPeriodic=0
    g269: BSplineCurve PolesCount=4 KnotsCount=2 Degree=3 IsPeriodic=0
    g270: BSplineCurve PolesCount=4 KnotsCount=2 Degree=3 IsPeriodic=0
    g271: BSplineCurve PolesCount=4 KnotsCount=2 Degree=3 IsPeriodic=0
    g272: BSplineCurve PolesCount=4 KnotsCount=2 Degree=3 IsPeriodic=0
    g273: BSplineCurve PolesCount=4 KnotsCount=2 Degree=3 IsPeriodic=0
    g274: BSplineCurve PolesCount=4 KnotsCount=2 Degree=3 IsPeriodic=0
    g275: BSplineCurve PolesCount=4 KnotsCount=2 Degree=3 IsPeriodic=0
    g276: BSplineCurve PolesCount=2 KnotsCount=2 Degree=1 IsPeriodic=0
    g277: BSplineCurve PolesCount=2 KnotsCount=2 Degree=1 IsPeriodic=0
    g278: BSplineCurve PolesCount=4 KnotsCount=2 Degree=3 IsPeriodic=0
    g279: BSplineCurve PolesCount=4 KnotsCount=2 Degree=3 IsPeriodic=0
    g280: BSplineCurve PolesCount=4 KnotsCount=2 Degree=3 IsPeriodic=0
    g281: BSplineCurve PolesCount=4 KnotsCount=2 Degree=3 IsPeriodic=0
    g282: BSplineCurve PolesCount=4 KnotsCount=2 Degree=3 IsPeriodic=0
    g283: BSplineCurve PolesCount=4 KnotsCount=2 Degree=3 IsPeriodic=0
    g284: BSplineCurve PolesCount=2 KnotsCount=2 Degree=1 IsPeriodic=0
    g285: BSplineCurve PolesCount=4 KnotsCount=2 Degree=3 IsPeriodic=0
    g286: BSplineCurve PolesCount=4 KnotsCount=2 Degree=3 IsPeriodic=0
    g287: BSplineCurve PolesCount=4 KnotsCount=2 Degree=3 IsPeriodic=0
    g288: BSplineCurve PolesCount=4 KnotsCount=2 Degree=3 IsPeriodic=0
    g289: BSplineCurve PolesCount=4 KnotsCount=2 Degree=3 IsPeriodic=0
    g290: BSplineCurve PolesCount=4 KnotsCount=2 Degree=3 IsPeriodic=0
    g291: BSplineCurve PolesCount=2 KnotsCount=2 Degree=1 IsPeriodic=0
    g292: BSplineCurve PolesCount=2 KnotsCount=2 Degree=1 IsPeriodic=0
    g293: BSplineCurve PolesCount=4 KnotsCount=2 Degree=3 IsPeriodic=0
    g294: BSplineCurve PolesCount=4 KnotsCount=2 Degree=3 IsPeriodic=0
    g295: BSplineCurve PolesCount=4 KnotsCount=2 Degree=3 IsPeriodic=0
    g296: BSplineCurve PolesCount=4 KnotsCount=2 Degree=3 IsPeriodic=0
    g297: BSplineCurve PolesCount=4 KnotsCount=2 Degree=3 IsPeriodic=0
    g298: BSplineCurve PolesCount=4 KnotsCount=2 Degree=3 IsPeriodic=0
    g299: BSplineCurve PolesCount=4 KnotsCount=2 Degree=3 IsPeriodic=0
    g300: BSplineCurve PolesCount=4 KnotsCount=2 Degree=3 IsPeriodic=0
    g301: BSplineCurve PolesCount=4 KnotsCount=2 Degree=3 IsPeriodic=0
    g302: BSplineCurve PolesCount=4 KnotsCount=2 Degree=3 IsPeriodic=0
    g303: BSplineCurve PolesCount=4 KnotsCount=2 Degree=3 IsPeriodic=0
    g304: BSplineCurve PolesCount=4 KnotsCount=2 Degree=3 IsPeriodic=0
    g305: BSplineCurve PolesCount=4 KnotsCount=2 Degree=3 IsPeriodic=0
    g306: BSplineCurve PolesCount=4 KnotsCount=2 Degree=3 IsPeriodic=0
    g307: BSplineCurve PolesCount=4 KnotsCount=2 Degree=3 IsPeriodic=0
    g308: BSplineCurve PolesCount=4 KnotsCount=2 Degree=3 IsPeriodic=0
    g309: BSplineCurve PolesCount=4 KnotsCount=2 Degree=3 IsPeriodic=0
    g310: BSplineCurve PolesCount=4 KnotsCount=2 Degree=3 IsPeriodic=0
    g311: BSplineCurve PolesCount=4 KnotsCount=2 Degree=3 IsPeriodic=0
    g312: BSplineCurve PolesCount=4 KnotsCount=2 Degree=3 IsPeriodic=0
    g313: BSplineCurve PolesCount=2 KnotsCount=2 Degree=1 IsPeriodic=0
    g314: BSplineCurve PolesCount=2 KnotsCount=2 Degree=1 IsPeriodic=0
    g315: BSplineCurve PolesCount=4 KnotsCount=2 Degree=3 IsPeriodic=0
    g316: BSplineCurve PolesCount=4 KnotsCount=2 Degree=3 IsPeriodic=0
    g317: BSplineCurve PolesCount=4 KnotsCount=2 Degree=3 IsPeriodic=0
    g318: BSplineCurve PolesCount=2 KnotsCount=2 Degree=1 IsPeriodic=0
    g319: BSplineCurve PolesCount=2 KnotsCount=2 Degree=1 IsPeriodic=0
    g320: BSplineCurve PolesCount=4 KnotsCount=2 Degree=3 IsPeriodic=0
    g321: BSplineCurve PolesCount=4 KnotsCount=2 Degree=3 IsPeriodic=0
    g322: BSplineCurve PolesCount=4 KnotsCount=2 Degree=3 IsPeriodic=0
    g323: BSplineCurve PolesCount=4 KnotsCount=2 Degree=3 IsPeriodic=0
    g324: BSplineCurve PolesCount=4 KnotsCount=2 Degree=3 IsPeriodic=0
    g325: BSplineCurve PolesCount=4 KnotsCount=2 Degree=3 IsPeriodic=0
    g326: BSplineCurve PolesCount=4 KnotsCount=2 Degree=3 IsPeriodic=0
    g327: BSplineCurve PolesCount=2 KnotsCount=2 Degree=1 IsPeriodic=0
    g328: BSplineCurve PolesCount=2 KnotsCount=2 Degree=1 IsPeriodic=0
    g329: BSplineCurve PolesCount=4 KnotsCount=2 Degree=3 IsPeriodic=0
    g330: BSplineCurve PolesCount=4 KnotsCount=2 Degree=3 IsPeriodic=0
    g331: BSplineCurve PolesCount=4 KnotsCount=2 Degree=3 IsPeriodic=0
    g332: BSplineCurve PolesCount=2 KnotsCount=2 Degree=1 IsPeriodic=0
    g333: BSplineCurve PolesCount=4 KnotsCount=2 Degree=3 IsPeriodic=0
    g334: BSplineCurve PolesCount=4 KnotsCount=2 Degree=3 IsPeriodic=0
    g335: BSplineCurve PolesCount=4 KnotsCount=2 Degree=3 IsPeriodic=0
    g336: BSplineCurve PolesCount=4 KnotsCount=2 Degree=3 IsPeriodic=0
    g337: BSplineCurve PolesCount=2 KnotsCount=2 Degree=1 IsPeriodic=0
    g338: BSplineCurve PolesCount=2 KnotsCount=2 Degree=1 IsPeriodic=0
    g339: BSplineCurve PolesCount=2 KnotsCount=2 Degree=1 IsPeriodic=0
    g340: BSplineCurve PolesCount=2 KnotsCount=2 Degree=1 IsPeriodic=0
    g341: BSplineCurve PolesCount=4 KnotsCount=2 Degree=3 IsPeriodic=0
    g342: BSplineCurve PolesCount=4 KnotsCount=2 Degree=3 IsPeriodic=0
    g343: BSplineCurve PolesCount=4 KnotsCount=2 Degree=3 IsPeriodic=0
    g344: BSplineCurve PolesCount=4 KnotsCount=2 Degree=3 IsPeriodic=0
    g345: BSplineCurve PolesCount=4 KnotsCount=2 Degree=3 IsPeriodic=0
    g346: BSplineCurve PolesCount=4 KnotsCount=2 Degree=3 IsPeriodic=0
    g347: BSplineCurve PolesCount=4 KnotsCount=2 Degree=3 IsPeriodic=0
    g348: BSplineCurve PolesCount=2 KnotsCount=2 Degree=1 IsPeriodic=0
    g349: BSplineCurve PolesCount=4 KnotsCount=2 Degree=3 IsPeriodic=0
    g350: BSplineCurve PolesCount=4 KnotsCount=2 Degree=3 IsPeriodic=0
    g351: BSplineCurve PolesCount=4 KnotsCount=2 Degree=3 IsPeriodic=0
    g352: BSplineCurve PolesCount=4 KnotsCount=2 Degree=3 IsPeriodic=0
    g353: BSplineCurve PolesCount=4 KnotsCount=2 Degree=3 IsPeriodic=0
    g354: BSplineCurve PolesCount=4 KnotsCount=2 Degree=3 IsPeriodic=0
    g355: BSplineCurve PolesCount=4 KnotsCount=2 Degree=3 IsPeriodic=0
    g356: BSplineCurve PolesCount=4 KnotsCount=2 Degree=3 IsPeriodic=0
    g357: BSplineCurve PolesCount=4 KnotsCount=2 Degree=3 IsPeriodic=0
    g358: BSplineCurve PolesCount=4 KnotsCount=2 Degree=3 IsPeriodic=0
    g359: BSplineCurve PolesCount=4 KnotsCount=2 Degree=3 IsPeriodic=0
    g360: BSplineCurve PolesCount=4 KnotsCount=2 Degree=3 IsPeriodic=0
    g361: BSplineCurve PolesCount=4 KnotsCount=2 Degree=3 IsPeriodic=0
    g362: BSplineCurve PolesCount=4 KnotsCount=2 Degree=3 IsPeriodic=0
    g363: BSplineCurve PolesCount=4 KnotsCount=2 Degree=3 IsPeriodic=0
    g364: BSplineCurve PolesCount=4 KnotsCount=2 Degree=3 IsPeriodic=0
    g365: BSplineCurve PolesCount=4 KnotsCount=2 Degree=3 IsPeriodic=0
    g366: BSplineCurve PolesCount=4 KnotsCount=2 Degree=3 IsPeriodic=0
    g367: BSplineCurve PolesCount=4 KnotsCount=2 Degree=3 IsPeriodic=0
    g368: BSplineCurve PolesCount=4 KnotsCount=2 Degree=3 IsPeriodic=0
    g369: BSplineCurve PolesCount=4 KnotsCount=2 Degree=3 IsPeriodic=0
    g370: BSplineCurve PolesCount=4 KnotsCount=2 Degree=3 IsPeriodic=0
    g371: BSplineCurve PolesCount=4 KnotsCount=2 Degree=3 IsPeriodic=0
    g372: BSplineCurve PolesCount=2 KnotsCount=2 Degree=1 IsPeriodic=0
    g373: BSplineCurve PolesCount=4 KnotsCount=2 Degree=3 IsPeriodic=0
    g374: BSplineCurve PolesCount=4 KnotsCount=2 Degree=3 IsPeriodic=0
    g375: BSplineCurve PolesCount=4 KnotsCount=2 Degree=3 IsPeriodic=0
    g376: BSplineCurve PolesCount=4 KnotsCount=2 Degree=3 IsPeriodic=0
    g377: BSplineCurve PolesCount=4 KnotsCount=2 Degree=3 IsPeriodic=0
    g378: BSplineCurve PolesCount=4 KnotsCount=2 Degree=3 IsPeriodic=0
    g379: BSplineCurve PolesCount=4 KnotsCount=2 Degree=3 IsPeriodic=0
    g380: BSplineCurve PolesCount=4 KnotsCount=2 Degree=3 IsPeriodic=0
    g381: BSplineCurve PolesCount=4 KnotsCount=2 Degree=3 IsPeriodic=0
    g382: BSplineCurve PolesCount=4 KnotsCount=2 Degree=3 IsPeriodic=0
    g383: BSplineCurve PolesCount=4 KnotsCount=2 Degree=3 IsPeriodic=0
    g384: BSplineCurve PolesCount=4 KnotsCount=2 Degree=3 IsPeriodic=0
    g385: BSplineCurve PolesCount=4 KnotsCount=2 Degree=3 IsPeriodic=0
    g386: BSplineCurve PolesCount=4 KnotsCount=2 Degree=3 IsPeriodic=0
    g387: BSplineCurve PolesCount=4 KnotsCount=2 Degree=3 IsPeriodic=0
    g388: BSplineCurve PolesCount=4 KnotsCount=2 Degree=3 IsPeriodic=0
    g389: BSplineCurve PolesCount=2 KnotsCount=2 Degree=1 IsPeriodic=0
    g390: BSplineCurve PolesCount=2 KnotsCount=2 Degree=1 IsPeriodic=0
    g391: BSplineCurve PolesCount=4 KnotsCount=2 Degree=3 IsPeriodic=0
    g392: BSplineCurve PolesCount=2 KnotsCount=2 Degree=1 IsPeriodic=0
    g393: BSplineCurve PolesCount=4 KnotsCount=2 Degree=3 IsPeriodic=0
    g394: BSplineCurve PolesCount=4 KnotsCount=2 Degree=3 IsPeriodic=0
    g395: BSplineCurve PolesCount=4 KnotsCount=2 Degree=3 IsPeriodic=0
    g396: BSplineCurve PolesCount=4 KnotsCount=2 Degree=3 IsPeriodic=0
    g397: BSplineCurve PolesCount=4 KnotsCount=2 Degree=3 IsPeriodic=0
    g398: BSplineCurve PolesCount=4 KnotsCount=2 Degree=3 IsPeriodic=0
    g399: BSplineCurve PolesCount=4 KnotsCount=2 Degree=3 IsPeriodic=0
    ... +163 more geometry lines
  constraints (576):
    c: Coincident(g0,g1)
    c: Coincident(g1,g2)
    c: Coincident(g2,g3)
    c: Coincident(g3,g4)
    c: Coincident(g4,g5)
    c: Coincident(g5,g6)
    c: Coincident(g6,g7)
    c: Coincident(g7,g8)
    c: Coincident(g8,g9)
    c: Coincident(g9,g10)
    c: Coincident(g10,g11)
    c: Coincident(g11,g12)
    c: Coincident(g12,g13)
    c: Coincident(g13,g14)
    c: Coincident(g14,g15)
    c: Coincident(g15,g16)
    c: Coincident(g16,g17)
    c: Coincident(g17,g18)
    c: Coincident(g18,g19)
    c: Coincident(g19,g20)
    c: Coincident(g20,g21)
    c: Coincident(g21,g22)
    c: Coincident(g22,g23)
    c: Coincident(g23,g24)
    c: Coincident(g24,g25)
    c: Coincident(g25,g26)
    c: Coincident(g26,g27)
    c: Coincident(g27,g28)
    c: Coincident(g28,g29)
    c: Coincident(g29,g30)
    c: Coincident(g30,g31)
    c: Coincident(g31,g32)
    c: Coincident(g32,g33)
    c: Coincident(g33,g34)
    c: Coincident(g34,g35)
    c: Coincident(g35,g36)
    c: Coincident(g36,g37)
    c: Coincident(g37,g38)
    c: Coincident(g38,g39)
    c: Coincident(g39,g40)
    c: Coincident(g40,g41)
    c: Coincident(g41,g42)
    c: Coincident(g42,g43)
    c: Coincident(g43,g44)
    c: Coincident(g44,g45)
    c: Coincident(g45,g46)
    c: Coincident(g46,g47)
    c: Coincident(g47,g48)
    c: Coincident(g48,g49)
    c: Coincident(g49,g50)
    c: Coincident(g50,g51)
    c: Coincident(g51,g52)
    c: Coincident(g52,g53)
    c: Coincident(g53,g54)
    c: Coincident(g54,g55)
    c: Coincident(g55,g56)
    c: Coincident(g56,g57)
    c: Coincident(g57,g58)
    c: Coincident(g58,g59)
    c: Coincident(g59,g60)
    c: Coincident(g60,g61)
    c: Coincident(g61,g62)
    c: Coincident(g62,g63)
    c: Coincident(g63,g64)
    c: Coincident(g64,g65)
    c: Coincident(g65,g66)
    c: Coincident(g66,g67)
    c: Coincident(g67,g68)
    c: Coincident(g68,g69)
    c: Coincident(g69,g70)
    c: Coincident(g70,g71)
    c: Coincident(g71,g72)
    c: Coincident(g72,g73)
    c: Coincident(g73,g0)
    c: Coincident(g74,g75)
    c: Coincident(g75,g76)
    c: Coincident(g76,g77)
    c: Coincident(g77,g78)
    c: Coincident(g78,g79)
    c: Coincident(g79,g74)
    c: Coincident(g80,g81)
    c: Coincident(g81,g82)
    c: Coincident(g82,g83)
    c: Coincident(g83,g84)
    c: Coincident(g84,g85)
    c: Coincident(g85,g86)
    c: Coincident(g86,g87)
    c: Coincident(g87,g88)
    c: Coincident(g88,g89)
    c: Coincident(g89,g90)
    c: Coincident(g90,g91)
    c: Coincident(g91,g80)
    c: Coincident(g92,g93)
    c: Coincident(g93,g94)
    c: Coincident(g94,g95)
    c: Coincident(g95,g92)
    c: Coincident(g96,g97)
    c: Coincident(g97,g98)
    c: Coincident(g98,g99)
    c: Coincident(g99,g100)
    c: Coincident(g100,g101)
    c: Coincident(g101,g102)
    c: Coincident(g102,g96)
    c: Coincident(g103,g104)
    c: Coincident(g104,g105)
    c: Coincident(g105,g106)
    c: Coincident(g106,g107)
    c: Coincident(g107,g108)
    c: Coincident(g108,g103)
    c: Coincident(g109,g110)
    c: Coincident(g110,g111)
    c: Coincident(g111,g112)
    c: Coincident(g112,g113)
    c: Coincident(g113,g114)
    c: Coincident(g114,g115)
    c: Coincident(g115,g116)
    c: Coincident(g116,g117)
    c: Coincident(g117,g118)
    c: Coincident(g118,g119)
    c: Coincident(g119,g120)
    c: Coincident(g120,g109)
    c: Coincident(g121,g122)
    c: Coincident(g122,g123)
    c: Coincident(g123,g124)
    c: Coincident(g124,g125)
    c: Coincident(g125,g126)
    c: Coincident(g126,g127)
    c: Coincident(g127,g128)
    c: Coincident(g128,g129)
    c: Coincident(g129,g130)
    c: Coincident(g130,g131)
    c: Coincident(g131,g132)
    c: Coincident(g132,g133)
    c: Coincident(g133,g134)
    c: Coincident(g134,g121)
    c: Coincident(g135,g136)
    c: Coincident(g136,g137)
    c: Coincident(g137,g138)
    c: Coincident(g138,g139)
    c: Coincident(g139,g140)
    c: Coincident(g140,g141)
    c: Coincident(g141,g142)
    c: Coincident(g142,g143)
    c: Coincident(g143,g144)
    c: Coincident(g144,g145)
    c: Coincident(g145,g146)
    c: Coincident(g146,g147)
    c: Coincident(g147,g148)
    c: Coincident(g148,g149)
    c: Coincident(g149,g150)
    c: Coincident(g150,g151)
    c: Coincident(g151,g152)
    c: Coincident(g152,g135)
    c: Coincident(g153,g154)
    c: Coincident(g154,g155)
    c: Coincident(g155,g156)
    c: Coincident(g156,g157)
    c: Coincident(g157,g158)
    c: Coincident(g158,g159)
    c: Coincident(g159,g160)
    c: Coincident(g160,g161)
    c: Coincident(g161,g162)
    c: Coincident(g162,g163)
    c: Coincident(g163,g164)
    c: Coincident(g164,g165)
    c: Coincident(g165,g166)
    c: Coincident(g166,g167)
    c: Coincident(g167,g168)
    c: Coincident(g168,g169)
    c: Coincident(g169,g170)
    c: Coincident(g170,g171)
    c: Coincident(g171,g172)
    c: Coincident(g172,g173)
    c: Coincident(g173,g174)
    c: Coincident(g174,g175)
    c: Coincident(g175,g176)
    c: Coincident(g176,g153)
    c: Coincident(g177,g178)
    c: Coincident(g178,g179)
    c: Coincident(g179,g180)
    c: Coincident(g180,g181)
    c: Coincident(g181,g182)
    c: Coincident(g182,g183)
    c: Coincident(g183,g184)
    c: Coincident(g184,g185)
    c: Coincident(g185,g186)
    c: Coincident(g186,g187)
    c: Coincident(g187,g188)
    c: Coincident(g188,g189)
    c: Coincident(g189,g190)
    c: Coincident(g190,g191)
    c: Coincident(g191,g192)
    c: Coincident(g192,g193)
    c: Coincident(g193,g194)
    c: Coincident(g194,g195)
    c: Coincident(g195,g196)
    c: Coincident(g196,g197)
    c: Coincident(g197,g198)
    c: Coincident(g198,g199)
    c: Coincident(g199,g200)
    c: Coincident(g200,g201)
    c: Coincident(g201,g202)
    c: Coincident(g202,g203)
    c: Coincident(g203,g204)
    c: Coincident(g204,g205)
    c: Coincident(g205,g206)
    c: Coincident(g206,g207)
    c: Coincident(g207,g208)
    c: Coincident(g208,g209)
    c: Coincident(g209,g210)
    c: Coincident(g210,g211)
    c: Coincident(g211,g212)
    c: Coincident(g212,g213)
    c: Coincident(g213,g214)
    c: Coincident(g214,g215)
    c: Coincident(g215,g216)
    c: Coincident(g216,g217)
    c: Coincident(g217,g218)
    c: Coincident(g218,g219)
    c: Coincident(g219,g177)
    c: Coincident(g220,g221)
    c: Coincident(g221,g222)
    c: Coincident(g222,g223)
    c: Coincident(g223,g224)
    c: Coincident(g224,g225)
    c: Coincident(g225,g220)
    c: Coincident(g226,g227)
    c: Coincident(g227,g228)
    c: Coincident(g228,g229)
    c: Coincident(g229,g230)
    c: Coincident(g230,g226)
    c: Coincident(g231,g232)
    c: Coincident(g232,g233)
    c: Coincident(g233,g234)
    c: Coincident(g234,g235)
    c: Coincident(g235,g236)
    c: Coincident(g236,g237)
    c: Coincident(g237,g238)
    c: Coincident(g238,g231)
    c: Coincident(g239,g240)
    c: Coincident(g240,g241)
    c: Coincident(g241,g242)
    c: Coincident(g242,g243)
    c: Coincident(g243,g244)
    c: Coincident(g244,g245)
    c: Coincident(g245,g246)
    c: Coincident(g246,g247)
    c: Coincident(g247,g248)
    c: Coincident(g248,g249)
    c: Coincident(g249,g250)
    c: Coincident(g250,g251)
    c: Coincident(g251,g239)
    c: Coincident(g252,g253)
    c: Coincident(g253,g254)
    c: Coincident(g254,g255)
    c: Coincident(g255,g256)
    c: Coincident(g256,g252)
    c: Coincident(g257,g258)
    c: Coincident(g258,g259)
    c: Coincident(g259,g260)
    c: Coincident(g260,g261)
    c: Coincident(g261,g262)
    c: Coincident(g262,g263)
    c: Coincident(g263,g264)
    c: Coincident(g264,g265)
    c: Coincident(g265,g266)
    c: Coincident(g266,g257)
    c: Coincident(g267,g268)
    c: Coincident(g268,g269)
    c: Coincident(g269,g270)
    c: Coincident(g270,g271)
    c: Coincident(g271,g272)
    c: Coincident(g272,g273)
    c: Coincident(g273,g274)
    c: Coincident(g274,g275)
    c: Coincident(g275,g276)
    c: Coincident(g276,g277)
    c: Coincident(g277,g278)
    c: Coincident(g278,g279)
    c: Coincident(g279,g280)
    c: Coincident(g280,g281)
    c: Coincident(g281,g282)
    c: Coincident(g282,g283)
    c: Coincident(g283,g267)
    c: Coincident(g284,g285)
    c: Coincident(g285,g286)
    c: Coincident(g286,g287)
    c: Coincident(g287,g288)
    c: Coincident(g288,g289)
    c: Coincident(g289,g290)
    c: Coincident(g290,g291)
    c: Coincident(g291,g292)
    c: Coincident(g292,g293)
    c: Coincident(g293,g294)
    c: Coincident(g294,g295)
    c: Coincident(g295,g296)
    c: Coincident(g296,g297)
    c: Coincident(g297,g298)
    c: Coincident(g298,g299)
    c: Coincident(g299,g300)
    c: Coincident(g300,g301)
    c: Coincident(g301,g302)
    c: Coincident(g302,g303)
    c: Coincident(g303,g304)
    c: Coincident(g304,g305)
    c: Coincident(g305,g306)
    c: Coincident(g306,g307)
    c: Coincident(g307,g308)
    c: Coincident(g308,g309)
    c: Coincident(g309,g310)
    c: Coincident(g310,g311)
    c: Coincident(g311,g312)
    c: Coincident(g312,g313)
    c: Coincident(g313,g314)
    c: Coincident(g314,g315)
    c: Coincident(g315,g316)
    c: Coincident(g316,g317)
    c: Coincident(g317,g318)
    c: Coincident(g318,g319)
    c: Coincident(g319,g320)
    c: Coincident(g320,g321)
    c: Coincident(g321,g322)
    c: Coincident(g322,g323)
    c: Coincident(g323,g324)
    c: Coincident(g324,g325)
    c: Coincident(g325,g326)
    c: Coincident(g326,g327)
    c: Coincident(g327,g328)
    c: Coincident(g328,g329)
    c: Coincident(g329,g330)
    c: Coincident(g330,g331)
    c: Coincident(g331,g284)
    c: Coincident(g332,g333)
    c: Coincident(g333,g334)
    c: Coincident(g334,g335)
    c: Coincident(g335,g336)
    c: Coincident(g336,g337)
    c: Coincident(g337,g338)
    c: Coincident(g338,g339)
    c: Coincident(g339,g340)
    c: Coincident(g340,g341)
    c: Coincident(g341,g342)
    c: Coincident(g342,g343)
    c: Coincident(g343,g344)
    c: Coincident(g344,g345)
    c: Coincident(g345,g346)
    c: Coincident(g346,g347)
    c: Coincident(g347,g332)
    c: Coincident(g348,g349)
    c: Coincident(g349,g350)
    c: Coincident(g350,g351)
    c: Coincident(g351,g352)
    c: Coincident(g352,g353)
    c: Coincident(g353,g354)
    c: Coincident(g354,g355)
    c: Coincident(g355,g356)
    c: Coincident(g356,g357)
    c: Coincident(g357,g358)
    c: Coincident(g358,g359)
    c: Coincident(g359,g360)
    c: Coincident(g360,g361)
    c: Coincident(g361,g362)
    c: Coincident(g362,g363)
    c: Coincident(g363,g364)
    c: Coincident(g364,g365)
    c: Coincident(g365,g366)
    c: Coincident(g366,g367)
    c: Coincident(g367,g368)
    c: Coincident(g368,g369)
    c: Coincident(g369,g370)
    c: Coincident(g370,g371)
    c: Coincident(g371,g348)
    c: Coincident(g372,g373)
    c: Coincident(g373,g374)
    c: Coincident(g374,g375)
    c: Coincident(g375,g376)
    c: Coincident(g376,g377)
    c: Coincident(g377,g378)
    c: Coincident(g378,g379)
    c: Coincident(g379,g380)
    c: Coincident(g380,g381)
    c: Coincident(g381,g382)
    c: Coincident(g382,g383)
    c: Coincident(g383,g384)
    c: Coincident(g384,g385)
    c: Coincident(g385,g386)
    c: Coincident(g386,g387)
    c: Coincident(g387,g388)
    c: Coincident(g388,g389)
    c: Coincident(g389,g390)
    c: Coincident(g390,g391)
    c: Coincident(g391,g372)
    c: Coincident(g392,g393)
    c: Coincident(g393,g394)
    c: Coincident(g394,g395)
    c: Coincident(g395,g396)
    c: Coincident(g396,g397)
    c: Coincident(g397,g398)
    c: Coincident(g398,g399)
    c: Coincident(g399,g400)
    c: Coincident(g400,g401)
    c: Coincident(g401,g402)
    c: Coincident(g402,g403)
    c: Coincident(g403,g404)
    c: Coincident(g404,g405)
    c: Coincident(g405,g406)
    c: Coincident(g406,g407)
    c: Coincident(g407,g408)
    c: Coincident(g408,g409)
    c: Coincident(g409,g410)
    c: Coincident(g410,g411)
    c: Coincident(g411,g412)
    c: Coincident(g412,g413)
    c: Coincident(g413,g414)
    c: Coincident(g414,g415)
    c: Coincident(g415,g416)
    c: Coincident(g416,g417)
    c: Coincident(g417,g418)
    c: Coincident(g418,g419)
    c: Coincident(g419,g420)
    c: Coincident(g420,g421)
    c: Coincident(g421,g422)
    c: Coincident(g422,g423)
    c: Coincident(g423,g424)
    c: Coincident(g424,g425)
    c: Coincident(g425,g426)
    c: Coincident(g426,g427)
    c: Coincident(g427,g428)
    c: Coincident(g428,g429)
    c: Coincident(g429,g392)
    c: Coincident(g430,g431)
    c: Coincident(g431,g432)
    c: Coincident(g432,g433)
    c: Coincident(g433,g434)
    c: Coincident(g434,g435)
    c: Coincident(g435,g436)
    c: Coincident(g436,g437)
    c: Coincident(g437,g438)
    c: Coincident(g438,g439)
    c: Coincident(g439,g440)
    c: Coincident(g440,g441)
    c: Coincident(g441,g442)
    c: Coincident(g442,g430)
    c: Coincident(g443,g444)
    c: Coincident(g444,g445)
    c: Coincident(g445,g446)
    c: Coincident(g446,g447)
    c: Coincident(g447,g448)
    c: Coincident(g448,g449)
    c: Coincident(g449,g450)
    c: Coincident(g450,g451)
    c: Coincident(g451,g452)
    c: Coincident(g452,g453)
    c: Coincident(g453,g454)
    c: Coincident(g454,g455)
    c: Coincident(g455,g456)
    c: Coincident(g456,g457)
    c: Coincident(g457,g458)
    c: Coincident(g458,g459)
    c: Coincident(g459,g460)
    c: Coincident(g460,g461)
    c: Coincident(g461,g462)
    c: Coincident(g462,g463)
    c: Coincident(g463,g464)
    c: Coincident(g464,g443)
    c: Coincident(g465,g466)
    c: Coincident(g466,g467)
    c: Coincident(g467,g468)
    c: Coincident(g468,g469)
    c: Coincident(g469,g470)
    c: Coincident(g470,g465)
    c: Coincident(g471,g472)
    c: Coincident(g472,g473)
    c: Coincident(g473,g474)
    c: Coincident(g474,g475)
    c: Coincident(g475,g476)
    c: Coincident(g476,g477)
    c: Coincident(g477,g478)
    c: Coincident(g478,g479)
    c: Coincident(g479,g480)
    c: Coincident(g480,g481)
    c: Coincident(g481,g482)
    c: Coincident(g482,g483)
    c: Coincident(g483,g484)
    c: Coincident(g484,g485)
    c: Coincident(g485,g486)
    c: Coincident(g486,g487)
    c: Coincident(g487,g488)
    c: Coincident(g488,g489)
    c: Coincident(g489,g490)
    c: Coincident(g490,g471)
    c: Coincident(g491,g492)
    c: Coincident(g492,g493)
    c: Coincident(g493,g494)
    c: Coincident(g494,g495)
    c: Coincident(g495,g496)
    c: Coincident(g496,g497)
    c: Coincident(g497,g498)
    c: Coincident(g498,g499)
    c: Coincident(g499,g500)
    c: Coincident(g500,g501)
    c: Coincident(g501,g502)
    c: Coincident(g502,g503)
    c: Coincident(g503,g504)
    c: Coincident(g504,g505)
    c: Coincident(g505,g506)
    c: Coincident(g506,g507)
    c: Coincident(g507,g508)
    c: Coincident(g508,g509)
    c: Coincident(g509,g510)
    c: Coincident(g510,g511)
    c: Coincident(g511,g512)
    c: Coincident(g512,g513)
    c: Coincident(g513,g514)
    c: Coincident(g514,g515)
    c: Coincident(g515,g516)
    c: Coincident(g516,g517)
    c: Coincident(g517,g518)
    c: Coincident(g518,g519)
    c: Coincident(g519,g520)
    c: Coincident(g520,g521)
    c: Coincident(g521,g522)
    c: Coincident(g522,g523)
    c: Coincident(g523,g524)
    c: Coincident(g524,g491)
    c: Coincident(g525,g526)
    c: Coincident(g526,g527)
    c: Coincident(g527,g528)
    c: Coincident(g528,g529)
    c: Coincident(g529,g530)
    c: Coincident(g530,g531)
    c: Coincident(g531,g532)
    c: Coincident(g532,g533)
    c: Coincident(g533,g534)
    c: Coincident(g534,g535)
    c: Coincident(g535,g536)
    c: Coincident(g536,g537)
    c: Coincident(g537,g538)
    c: Coincident(g538,g539)
    c: Coincident(g539,g540)
    c: Coincident(g540,g541)
    c: Coincident(g541,g542)
    c: Coincident(g542,g525)
    c: Coincident(g543,g544)
    c: Coincident(g544,g545)
    c: Coincident(g545,g546)
    c: Coincident(g546,g547)
    c: Coincident(g547,g548)
    c: Coincident(g548,g549)
    c: Coincident(g549,g550)
    c: Coincident(g550,g551)
    c: Coincident(g551,g552)
    c: Coincident(g552,g553)
    c: Coincident(g553,g554)
    c: Coincident(g554,g555)
    c: Coincident(g555,g556)
    c: Coincident(g556,g543)
    c: Coincident(g557,g558)
    c: Coincident(g558,g559)
    c: Coincident(g559,g560)
    c: Coincident(g560,g561)
    c: Coincident(g561,g562)
    c: Coincident(g562,g557)
    c: Coincident(g557,g557)
    c: Coincident(g332,g332)
    c: Coincident(g257,g257)
    c: Coincident(g348,g348)
    c: Coincident(g267,g267)
    c: Coincident(g72,g0)
    c: Coincident(g284,g284)
    c: Coincident(g220,g220)
    c: Coincident(g177,g177)
    c: Coincident(g392,g392)
    c: Coincident(g92,g92)
    c: Coincident(g372,g372)
    c: Coincident(g80,g80)
FEATURE [Sketcher::SketchObject] Sketch015  label="Scarlet_Woman-Sketch"
  ArcFitTolerance = 1e-06
  FullyConstrained = false
  MakeInternals = false
  sketch-geometry (294):
    g0: BSplineCurve PolesCount=4 KnotsCount=2 Degree=3 IsPeriodic=0
    g1: BSplineCurve PolesCount=4 KnotsCount=2 Degree=3 IsPeriodic=0
    g2: BSplineCurve PolesCount=4 KnotsCount=2 Degree=3 IsPeriodic=0
    g3: BSplineCurve PolesCount=4 KnotsCount=2 Degree=3 IsPeriodic=0
    g4: BSplineCurve PolesCount=4 KnotsCount=2 Degree=3 IsPeriodic=0
    g5: BSplineCurve PolesCount=4 KnotsCount=2 Degree=3 IsPeriodic=0
    g6: BSplineCurve PolesCount=4 KnotsCount=2 Degree=3 IsPeriodic=0
    g7: BSplineCurve PolesCount=4 KnotsCount=2 Degree=3 IsPeriodic=0
    g8: BSplineCurve PolesCount=2 KnotsCount=2 Degree=1 IsPeriodic=0
    g9: BSplineCurve PolesCount=2 KnotsCount=2 Degree=1 IsPeriodic=0
    g10: BSplineCurve PolesCount=4 KnotsCount=2 Degree=3 IsPeriodic=0
    g11: BSplineCurve PolesCount=4 KnotsCount=2 Degree=3 IsPeriodic=0
    g12: BSplineCurve PolesCount=4 KnotsCount=2 Degree=3 IsPeriodic=0
    g13: BSplineCurve PolesCount=4 KnotsCount=2 Degree=3 IsPeriodic=0
    g14: BSplineCurve PolesCount=4 KnotsCount=2 Degree=3 IsPeriodic=0
    g15: BSplineCurve PolesCount=4 KnotsCount=2 Degree=3 IsPeriodic=0
    g16: BSplineCurve PolesCount=4 KnotsCount=2 Degree=3 IsPeriodic=0
    g17: BSplineCurve PolesCount=4 KnotsCount=2 Degree=3 IsPeriodic=0
    g18: BSplineCurve PolesCount=4 KnotsCount=2 Degree=3 IsPeriodic=0
    g19: BSplineCurve PolesCount=4 KnotsCount=2 Degree=3 IsPeriodic=0
    g20: BSplineCurve PolesCount=4 KnotsCount=2 Degree=3 IsPeriodic=0
    g21: BSplineCurve PolesCount=4 KnotsCount=2 Degree=3 IsPeriodic=0
    g22: BSplineCurve PolesCount=4 KnotsCount=2 Degree=3 IsPeriodic=0
    g23: BSplineCurve PolesCount=4 KnotsCount=2 Degree=3 IsPeriodic=0
    g24: BSplineCurve PolesCount=4 KnotsCount=2 Degree=3 IsPeriodic=0
    g25: BSplineCurve PolesCount=4 KnotsCount=2 Degree=3 IsPeriodic=0
    g26: BSplineCurve PolesCount=4 KnotsCount=2 Degree=3 IsPeriodic=0
    g27: BSplineCurve PolesCount=4 KnotsCount=2 Degree=3 IsPeriodic=0
    g28: BSplineCurve PolesCount=4 KnotsCount=2 Degree=3 IsPeriodic=0
    g29: BSplineCurve PolesCount=4 KnotsCount=2 Degree=3 IsPeriodic=0
    g30: BSplineCurve PolesCount=4 KnotsCount=2 Degree=3 IsPeriodic=0
    g31: BSplineCurve PolesCount=4 KnotsCount=2 Degree=3 IsPeriodic=0
    g32: BSplineCurve PolesCount=4 KnotsCount=2 Degree=3 IsPeriodic=0
    g33: BSplineCurve PolesCount=4 KnotsCount=2 Degree=3 IsPeriodic=0
    g34: BSplineCurve PolesCount=4 KnotsCount=2 Degree=3 IsPeriodic=0
    g35: BSplineCurve PolesCount=4 KnotsCount=2 Degree=3 IsPeriodic=0
    g36: BSplineCurve PolesCount=4 KnotsCount=2 Degree=3 IsPeriodic=0
    g37: BSplineCurve PolesCount=2 KnotsCount=2 Degree=1 IsPeriodic=0
    g38: BSplineCurve PolesCount=2 KnotsCount=2 Degree=1 IsPeriodic=0
    g39: BSplineCurve PolesCount=4 KnotsCount=2 Degree=3 IsPeriodic=0
    g40: BSplineCurve PolesCount=4 KnotsCount=2 Degree=3 IsPeriodic=0
    g41: BSplineCurve PolesCount=4 KnotsCount=2 Degree=3 IsPeriodic=0
    g42: BSplineCurve PolesCount=4 KnotsCount=2 Degree=3 IsPeriodic=0
    g43: BSplineCurve PolesCount=4 KnotsCount=2 Degree=3 IsPeriodic=0
    g44: BSplineCurve PolesCount=4 KnotsCount=2 Degree=3 IsPeriodic=0
    g45: BSplineCurve PolesCount=4 KnotsCount=2 Degree=3 IsPeriodic=0
    g46: BSplineCurve PolesCount=4 KnotsCount=2 Degree=3 IsPeriodic=0
    g47: BSplineCurve PolesCount=4 KnotsCount=2 Degree=3 IsPeriodic=0
    g48: BSplineCurve PolesCount=4 KnotsCount=2 Degree=3 IsPeriodic=0
    g49: BSplineCurve PolesCount=4 KnotsCount=2 Degree=3 IsPeriodic=0
    g50: BSplineCurve PolesCount=4 KnotsCount=2 Degree=3 IsPeriodic=0
    g51: BSplineCurve PolesCount=4 KnotsCount=2 Degree=3 IsPeriodic=0
    g52: BSplineCurve PolesCount=4 KnotsCount=2 Degree=3 IsPeriodic=0
    g53: BSplineCurve PolesCount=4 KnotsCount=2 Degree=3 IsPeriodic=0
    g54: BSplineCurve PolesCount=4 KnotsCount=2 Degree=3 IsPeriodic=0
    g55: BSplineCurve PolesCount=4 KnotsCount=2 Degree=3 IsPeriodic=0
    g56: BSplineCurve PolesCount=4 KnotsCount=2 Degree=3 IsPeriodic=0
    g57: BSplineCurve PolesCount=4 KnotsCount=2 Degree=3 IsPeriodic=0
    g58: BSplineCurve PolesCount=4 KnotsCount=2 Degree=3 IsPeriodic=0
    g59: BSplineCurve PolesCount=4 KnotsCount=2 Degree=3 IsPeriodic=0
    g60: BSplineCurve PolesCount=4 KnotsCount=2 Degree=3 IsPeriodic=0
    g61: BSplineCurve PolesCount=4 KnotsCount=2 Degree=3 IsPeriodic=0
    g62: BSplineCurve PolesCount=4 KnotsCount=2 Degree=3 IsPeriodic=0
    g63: BSplineCurve PolesCount=4 KnotsCount=2 Degree=3 IsPeriodic=0
    g64: BSplineCurve PolesCount=2 KnotsCount=2 Degree=1 IsPeriodic=0
    g65: BSplineCurve PolesCount=2 KnotsCount=2 Degree=1 IsPeriodic=0
    g66: BSplineCurve PolesCount=4 KnotsCount=2 Degree=3 IsPeriodic=0
    g67: BSplineCurve PolesCount=4 KnotsCount=2 Degree=3 IsPeriodic=0
    g68: BSplineCurve PolesCount=4 KnotsCount=2 Degree=3 IsPeriodic=0
    g69: BSplineCurve PolesCount=4 KnotsCount=2 Degree=3 IsPeriodic=0
    g70: BSplineCurve PolesCount=4 KnotsCount=2 Degree=3 IsPeriodic=0
    g71: BSplineCurve PolesCount=4 KnotsCount=2 Degree=3 IsPeriodic=0
    g72: BSplineCurve PolesCount=4 KnotsCount=2 Degree=3 IsPeriodic=0
    g73: BSplineCurve PolesCount=4 KnotsCount=2 Degree=3 IsPeriodic=0
    g74: BSplineCurve PolesCount=4 KnotsCount=2 Degree=3 IsPeriodic=0
    g75: BSplineCurve PolesCount=4 KnotsCount=2 Degree=3 IsPeriodic=0
    g76: BSplineCurve PolesCount=4 KnotsCount=2 Degree=3 IsPeriodic=0
    g77: BSplineCurve PolesCount=4 KnotsCount=2 Degree=3 IsPeriodic=0
    g78: BSplineCurve PolesCount=4 KnotsCount=2 Degree=3 IsPeriodic=0
    g79: BSplineCurve PolesCount=4 KnotsCount=2 Degree=3 IsPeriodic=0
    g80: BSplineCurve PolesCount=4 KnotsCount=2 Degree=3 IsPeriodic=0
    g81: BSplineCurve PolesCount=4 KnotsCount=2 Degree=3 IsPeriodic=0
    g82: BSplineCurve PolesCount=4 KnotsCount=2 Degree=3 IsPeriodic=0
    g83: BSplineCurve PolesCount=4 KnotsCount=2 Degree=3 IsPeriodic=0
    g84: BSplineCurve PolesCount=4 KnotsCount=2 Degree=3 IsPeriodic=0
    g85: BSplineCurve PolesCount=4 KnotsCount=2 Degree=3 IsPeriodic=0
    g86: BSplineCurve PolesCount=4 KnotsCount=2 Degree=3 IsPeriodic=0
    g87: BSplineCurve PolesCount=2 KnotsCount=2 Degree=1 IsPeriodic=0
    g88: BSplineCurve PolesCount=2 KnotsCount=2 Degree=1 IsPeriodic=0
    g89: BSplineCurve PolesCount=4 KnotsCount=2 Degree=3 IsPeriodic=0
    g90: BSplineCurve PolesCount=4 KnotsCount=2 Degree=3 IsPeriodic=0
    g91: BSplineCurve PolesCount=4 KnotsCount=2 Degree=3 IsPeriodic=0
    g92: BSplineCurve PolesCount=4 KnotsCount=2 Degree=3 IsPeriodic=0
    g93: BSplineCurve PolesCount=4 KnotsCount=2 Degree=3 IsPeriodic=0
    g94: BSplineCurve PolesCount=4 KnotsCount=2 Degree=3 IsPeriodic=0
    g95: BSplineCurve PolesCount=4 KnotsCount=2 Degree=3 IsPeriodic=0
    g96: BSplineCurve PolesCount=4 KnotsCount=2 Degree=3 IsPeriodic=0
    g97: BSplineCurve PolesCount=4 KnotsCount=2 Degree=3 IsPeriodic=0
    g98: BSplineCurve PolesCount=4 KnotsCount=2 Degree=3 IsPeriodic=0
    g99: BSplineCurve PolesCount=4 KnotsCount=2 Degree=3 IsPeriodic=0
    g100: BSplineCurve PolesCount=4 KnotsCount=2 Degree=3 IsPeriodic=0
    g101: BSplineCurve PolesCount=4 KnotsCount=2 Degree=3 IsPeriodic=0
    g102: BSplineCurve PolesCount=2 KnotsCount=2 Degree=1 IsPeriodic=0
    g103: BSplineCurve PolesCount=4 KnotsCount=2 Degree=3 IsPeriodic=0
    g104: BSplineCurve PolesCount=4 KnotsCount=2 Degree=3 IsPeriodic=0
    g105: BSplineCurve PolesCount=4 KnotsCount=2 Degree=3 IsPeriodic=0
    g106: BSplineCurve PolesCount=4 KnotsCount=2 Degree=3 IsPeriodic=0
    g107: BSplineCurve PolesCount=4 KnotsCount=2 Degree=3 IsPeriodic=0
    g108: BSplineCurve PolesCount=4 KnotsCount=2 Degree=3 IsPeriodic=0
    g109: BSplineCurve PolesCount=4 KnotsCount=2 Degree=3 IsPeriodic=0
    g110: BSplineCurve PolesCount=4 KnotsCount=2 Degree=3 IsPeriodic=0
    g111: BSplineCurve PolesCount=4 KnotsCount=2 Degree=3 IsPeriodic=0
    g112: BSplineCurve PolesCount=4 KnotsCount=2 Degree=3 IsPeriodic=0
    g113: BSplineCurve PolesCount=2 KnotsCount=2 Degree=1 IsPeriodic=0
    g114: BSplineCurve PolesCount=4 KnotsCount=2 Degree=3 IsPeriodic=0
    g115: BSplineCurve PolesCount=4 KnotsCount=2 Degree=3 IsPeriodic=0
    g116: BSplineCurve PolesCount=2 KnotsCount=2 Degree=1 IsPeriodic=0
    g117: BSplineCurve PolesCount=2 KnotsCount=2 Degree=1 IsPeriodic=0
    g118: BSplineCurve PolesCount=4 KnotsCount=2 Degree=3 IsPeriodic=0
    g119: BSplineCurve PolesCount=4 KnotsCount=2 Degree=3 IsPeriodic=0
    g120: BSplineCurve PolesCount=4 KnotsCount=2 Degree=3 IsPeriodic=0
    g121: BSplineCurve PolesCount=4 KnotsCount=2 Degree=3 IsPeriodic=0
    g122: BSplineCurve PolesCount=4 KnotsCount=2 Degree=3 IsPeriodic=0
    g123: BSplineCurve PolesCount=4 KnotsCount=2 Degree=3 IsPeriodic=0
    g124: BSplineCurve PolesCount=4 KnotsCount=2 Degree=3 IsPeriodic=0
    g125: BSplineCurve PolesCount=2 KnotsCount=2 Degree=1 IsPeriodic=0
    g126: BSplineCurve PolesCount=4 KnotsCount=2 Degree=3 IsPeriodic=0
    g127: BSplineCurve PolesCount=4 KnotsCount=2 Degree=3 IsPeriodic=0
    g128: BSplineCurve PolesCount=4 KnotsCount=2 Degree=3 IsPeriodic=0
    g129: BSplineCurve PolesCount=4 KnotsCount=2 Degree=3 IsPeriodic=0
    g130: BSplineCurve PolesCount=4 KnotsCount=2 Degree=3 IsPeriodic=0
    g131: BSplineCurve PolesCount=4 KnotsCount=2 Degree=3 IsPeriodic=0
    g132: BSplineCurve PolesCount=4 KnotsCount=2 Degree=3 IsPeriodic=0
    g133: BSplineCurve PolesCount=4 KnotsCount=2 Degree=3 IsPeriodic=0
    g134: BSplineCurve PolesCount=4 KnotsCount=2 Degree=3 IsPeriodic=0
    g135: BSplineCurve PolesCount=4 KnotsCount=2 Degree=3 IsPeriodic=0
    g136: BSplineCurve PolesCount=4 KnotsCount=2 Degree=3 IsPeriodic=0
    g137: BSplineCurve PolesCount=4 KnotsCount=2 Degree=3 IsPeriodic=0
    g138: BSplineCurve PolesCount=4 KnotsCount=2 Degree=3 IsPeriodic=0
    g139: BSplineCurve PolesCount=4 KnotsCount=2 Degree=3 IsPeriodic=0
    g140: BSplineCurve PolesCount=4 KnotsCount=2 Degree=3 IsPeriodic=0
    g141: BSplineCurve PolesCount=4 KnotsCount=2 Degree=3 IsPeriodic=0
    g142: BSplineCurve PolesCount=4 KnotsCount=2 Degree=3 IsPeriodic=0
    g143: BSplineCurve PolesCount=4 KnotsCount=2 Degree=3 IsPeriodic=0
    g144: BSplineCurve PolesCount=4 KnotsCount=2 Degree=3 IsPeriodic=0
    g145: BSplineCurve PolesCount=4 KnotsCount=2 Degree=3 IsPeriodic=0
    g146: BSplineCurve PolesCount=4 KnotsCount=2 Degree=3 IsPeriodic=0
    g147: BSplineCurve PolesCount=4 KnotsCount=2 Degree=3 IsPeriodic=0
    g148: BSplineCurve PolesCount=4 KnotsCount=2 Degree=3 IsPeriodic=0
    g149: BSplineCurve PolesCount=4 KnotsCount=2 Degree=3 IsPeriodic=0
    g150: BSplineCurve PolesCount=4 KnotsCount=2 Degree=3 IsPeriodic=0
    g151: BSplineCurve PolesCount=4 KnotsCount=2 Degree=3 IsPeriodic=0
    g152: BSplineCurve PolesCount=4 KnotsCount=2 Degree=3 IsPeriodic=0
    g153: BSplineCurve PolesCount=4 KnotsCount=2 Degree=3 IsPeriodic=0
    g154: BSplineCurve PolesCount=2 KnotsCount=2 Degree=1 IsPeriodic=0
    g155: BSplineCurve PolesCount=4 KnotsCount=2 Degree=3 IsPeriodic=0
    g156: BSplineCurve PolesCount=4 KnotsCount=2 Degree=3 IsPeriodic=0
    g157: BSplineCurve PolesCount=4 KnotsCount=2 Degree=3 IsPeriodic=0
    g158: BSplineCurve PolesCount=2 KnotsCount=2 Degree=1 IsPeriodic=0
    g159: BSplineCurve PolesCount=2 KnotsCount=2 Degree=1 IsPeriodic=0
    g160: BSplineCurve PolesCount=4 KnotsCount=2 Degree=3 IsPeriodic=0
    g161: BSplineCurve PolesCount=4 KnotsCount=2 Degree=3 IsPeriodic=0
    g162: BSplineCurve PolesCount=4 KnotsCount=2 Degree=3 IsPeriodic=0
    g163: BSplineCurve PolesCount=4 KnotsCount=2 Degree=3 IsPeriodic=0
    g164: BSplineCurve PolesCount=4 KnotsCount=2 Degree=3 IsPeriodic=0
    g165: BSplineCurve PolesCount=4 KnotsCount=2 Degree=3 IsPeriodic=0
    g166: BSplineCurve PolesCount=4 KnotsCount=2 Degree=3 IsPeriodic=0
    g167: BSplineCurve PolesCount=2 KnotsCount=2 Degree=1 IsPeriodic=0
    g168: BSplineCurve PolesCount=2 KnotsCount=2 Degree=1 IsPeriodic=0
    g169: BSplineCurve PolesCount=4 KnotsCount=2 Degree=3 IsPeriodic=0
    g170: BSplineCurve PolesCount=4 KnotsCount=2 Degree=3 IsPeriodic=0
    g171: BSplineCurve PolesCount=4 KnotsCount=2 Degree=3 IsPeriodic=0
    g172: BSplineCurve PolesCount=4 KnotsCount=2 Degree=3 IsPeriodic=0
    g173: BSplineCurve PolesCount=4 KnotsCount=2 Degree=3 IsPeriodic=0
    g174: BSplineCurve PolesCount=4 KnotsCount=2 Degree=3 IsPeriodic=0
    g175: BSplineCurve PolesCount=2 KnotsCount=2 Degree=1 IsPeriodic=0
    g176: BSplineCurve PolesCount=4 KnotsCount=2 Degree=3 IsPeriodic=0
    g177: BSplineCurve PolesCount=4 KnotsCount=2 Degree=3 IsPeriodic=0
    g178: BSplineCurve PolesCount=4 KnotsCount=2 Degree=3 IsPeriodic=0
    g179: BSplineCurve PolesCount=4 KnotsCount=2 Degree=3 IsPeriodic=0
    g180: BSplineCurve PolesCount=4 KnotsCount=2 Degree=3 IsPeriodic=0
    g181: BSplineCurve PolesCount=4 KnotsCount=2 Degree=3 IsPeriodic=0
    g182: BSplineCurve PolesCount=2 KnotsCount=2 Degree=1 IsPeriodic=0
    g183: BSplineCurve PolesCount=4 KnotsCount=2 Degree=3 IsPeriodic=0
    g184: BSplineCurve PolesCount=4 KnotsCount=2 Degree=3 IsPeriodic=0
    g185: BSplineCurve PolesCount=4 KnotsCount=2 Degree=3 IsPeriodic=0
    g186: BSplineCurve PolesCount=4 KnotsCount=2 Degree=3 IsPeriodic=0
    g187: BSplineCurve PolesCount=4 KnotsCount=2 Degree=3 IsPeriodic=0
    g188: BSplineCurve PolesCount=4 KnotsCount=2 Degree=3 IsPeriodic=0
    g189: BSplineCurve PolesCount=4 KnotsCount=2 Degree=3 IsPeriodic=0
    g190: BSplineCurve PolesCount=4 KnotsCount=2 Degree=3 IsPeriodic=0
    g191: BSplineCurve PolesCount=4 KnotsCount=2 Degree=3 IsPeriodic=0
    g192: BSplineCurve PolesCount=4 KnotsCount=2 Degree=3 IsPeriodic=0
    g193: BSplineCurve PolesCount=2 KnotsCount=2 Degree=1 IsPeriodic=0
    g194: BSplineCurve PolesCount=4 KnotsCount=2 Degree=3 IsPeriodic=0
    g195: BSplineCurve PolesCount=4 KnotsCount=2 Degree=3 IsPeriodic=0
    g196: BSplineCurve PolesCount=4 KnotsCount=2 Degree=3 IsPeriodic=0
    g197: BSplineCurve PolesCount=4 KnotsCount=2 Degree=3 IsPeriodic=0
    g198: BSplineCurve PolesCount=4 KnotsCount=2 Degree=3 IsPeriodic=0
    g199: BSplineCurve PolesCount=4 KnotsCount=2 Degree=3 IsPeriodic=0
    g200: BSplineCurve PolesCount=2 KnotsCount=2 Degree=1 IsPeriodic=0
    g201: BSplineCurve PolesCount=2 KnotsCount=2 Degree=1 IsPeriodic=0
    g202: BSplineCurve PolesCount=4 KnotsCount=2 Degree=3 IsPeriodic=0
    g203: BSplineCurve PolesCount=4 KnotsCount=2 Degree=3 IsPeriodic=0
    g204: BSplineCurve PolesCount=4 KnotsCount=2 Degree=3 IsPeriodic=0
    g205: BSplineCurve PolesCount=4 KnotsCount=2 Degree=3 IsPeriodic=0
    g206: BSplineCurve PolesCount=4 KnotsCount=2 Degree=3 IsPeriodic=0
    g207: BSplineCurve PolesCount=2 KnotsCount=2 Degree=1 IsPeriodic=0
    g208: BSplineCurve PolesCount=2 KnotsCount=2 Degree=1 IsPeriodic=0
    g209: BSplineCurve PolesCount=2 KnotsCount=2 Degree=1 IsPeriodic=0
    g210: BSplineCurve PolesCount=2 KnotsCount=2 Degree=1 IsPeriodic=0
    g211: BSplineCurve PolesCount=4 KnotsCount=2 Degree=3 IsPeriodic=0
    g212: BSplineCurve PolesCount=4 KnotsCount=2 Degree=3 IsPeriodic=0
    g213: BSplineCurve PolesCount=4 KnotsCount=2 Degree=3 IsPeriodic=0
    g214: BSplineCurve PolesCount=4 KnotsCount=2 Degree=3 IsPeriodic=0
    g215: BSplineCurve PolesCount=4 KnotsCount=2 Degree=3 IsPeriodic=0
    g216: BSplineCurve PolesCount=4 KnotsCount=2 Degree=3 IsPeriodic=0
    g217: BSplineCurve PolesCount=4 KnotsCount=2 Degree=3 IsPeriodic=0
    g218: BSplineCurve PolesCount=4 KnotsCount=2 Degree=3 IsPeriodic=0
    g219: BSplineCurve PolesCount=4 KnotsCount=2 Degree=3 IsPeriodic=0
    g220: BSplineCurve PolesCount=4 KnotsCount=2 Degree=3 IsPeriodic=0
    g221: BSplineCurve PolesCount=4 KnotsCount=2 Degree=3 IsPeriodic=0
    g222: BSplineCurve PolesCount=4 KnotsCount=2 Degree=3 IsPeriodic=0
    g223: BSplineCurve PolesCount=4 KnotsCount=2 Degree=3 IsPeriodic=0
    g224: BSplineCurve PolesCount=4 KnotsCount=2 Degree=3 IsPeriodic=0
    g225: BSplineCurve PolesCount=4 KnotsCount=2 Degree=3 IsPeriodic=0
    g226: BSplineCurve PolesCount=4 KnotsCount=2 Degree=3 IsPeriodic=0
    g227: BSplineCurve PolesCount=4 KnotsCount=2 Degree=3 IsPeriodic=0
    g228: BSplineCurve PolesCount=4 KnotsCount=2 Degree=3 IsPeriodic=0
    g229: BSplineCurve PolesCount=4 KnotsCount=2 Degree=3 IsPeriodic=0
    g230: BSplineCurve PolesCount=4 KnotsCount=2 Degree=3 IsPeriodic=0
    g231: BSplineCurve PolesCount=4 KnotsCount=2 Degree=3 IsPeriodic=0
    g232: BSplineCurve PolesCount=4 KnotsCount=2 Degree=3 IsPeriodic=0
    g233: BSplineCurve PolesCount=4 KnotsCount=2 Degree=3 IsPeriodic=0
    g234: BSplineCurve PolesCount=2 KnotsCount=2 Degree=1 IsPeriodic=0
    g235: BSplineCurve PolesCount=2 KnotsCount=2 Degree=1 IsPeriodic=0
    g236: BSplineCurve PolesCount=4 KnotsCount=2 Degree=3 IsPeriodic=0
    g237: BSplineCurve PolesCount=4 KnotsCount=2 Degree=3 IsPeriodic=0
    g238: BSplineCurve PolesCount=4 KnotsCount=2 Degree=3 IsPeriodic=0
    g239: BSplineCurve PolesCount=2 KnotsCount=2 Degree=1 IsPeriodic=0
    g240: BSplineCurve PolesCount=2 KnotsCount=2 Degree=1 IsPeriodic=0
    g241: BSplineCurve PolesCount=4 KnotsCount=2 Degree=3 IsPeriodic=0
    g242: BSplineCurve PolesCount=4 KnotsCount=2 Degree=3 IsPeriodic=0
    g243: BSplineCurve PolesCount=4 KnotsCount=2 Degree=3 IsPeriodic=0
    g244: BSplineCurve PolesCount=4 KnotsCount=2 Degree=3 IsPeriodic=0
    g245: BSplineCurve PolesCount=4 KnotsCount=2 Degree=3 IsPeriodic=0
    g246: BSplineCurve PolesCount=4 KnotsCount=2 Degree=3 IsPeriodic=0
    g247: BSplineCurve PolesCount=4 KnotsCount=2 Degree=3 IsPeriodic=0
    g248: BSplineCurve PolesCount=4 KnotsCount=2 Degree=3 IsPeriodic=0
    g249: BSplineCurve PolesCount=2 KnotsCount=2 Degree=1 IsPeriodic=0
    g250: BSplineCurve PolesCount=2 KnotsCount=2 Degree=1 IsPeriodic=0
    g251: BSplineCurve PolesCount=4 KnotsCount=2 Degree=3 IsPeriodic=0
    g252: BSplineCurve PolesCount=4 KnotsCount=2 Degree=3 IsPeriodic=0
    g253: BSplineCurve PolesCount=4 KnotsCount=2 Degree=3 IsPeriodic=0
    g254: BSplineCurve PolesCount=4 KnotsCount=2 Degree=3 IsPeriodic=0
    g255: BSplineCurve PolesCount=4 KnotsCount=2 Degree=3 IsPeriodic=0
    g256: BSplineCurve PolesCount=4 KnotsCount=2 Degree=3 IsPeriodic=0
    g257: BSplineCurve PolesCount=4 KnotsCount=2 Degree=3 IsPeriodic=0
    g258: BSplineCurve PolesCount=4 KnotsCount=2 Degree=3 IsPeriodic=0
    g259: BSplineCurve PolesCount=4 KnotsCount=2 Degree=3 IsPeriodic=0
    g260: BSplineCurve PolesCount=4 KnotsCount=2 Degree=3 IsPeriodic=0
    g261: BSplineCurve PolesCount=4 KnotsCount=2 Degree=3 IsPeriodic=0
    g262: BSplineCurve PolesCount=4 KnotsCount=2 Degree=3 IsPeriodic=0
    g263: BSplineCurve PolesCount=4 KnotsCount=2 Degree=3 IsPeriodic=0
    g264: BSplineCurve PolesCount=4 KnotsCount=2 Degree=3 IsPeriodic=0
    g265: BSplineCurve PolesCount=4 KnotsCount=2 Degree=3 IsPeriodic=0
    g266: BSplineCurve PolesCount=4 KnotsCount=2 Degree=3 IsPeriodic=0
    g267: BSplineCurve PolesCount=4 KnotsCount=2 Degree=3 IsPeriodic=0
    g268: BSplineCurve PolesCount=4 KnotsCount=2 Degree=3 IsPeriodic=0
    g269: BSplineCurve PolesCount=4 KnotsCount=2 Degree=3 IsPeriodic=0
    g270: BSplineCurve PolesCount=2 KnotsCount=2 Degree=1 IsPeriodic=0
    g271: BSplineCurve PolesCount=2 KnotsCount=2 Degree=1 IsPeriodic=0
    g272: BSplineCurve PolesCount=4 KnotsCount=2 Degree=3 IsPeriodic=0
    g273: BSplineCurve PolesCount=4 KnotsCount=2 Degree=3 IsPeriodic=0
    g274: BSplineCurve PolesCount=4 KnotsCount=2 Degree=3 IsPeriodic=0
    g275: BSplineCurve PolesCount=4 KnotsCount=2 Degree=3 IsPeriodic=0
    g276: BSplineCurve PolesCount=4 KnotsCount=2 Degree=3 IsPeriodic=0
    g277: BSplineCurve PolesCount=4 KnotsCount=2 Degree=3 IsPeriodic=0
    g278: BSplineCurve PolesCount=4 KnotsCount=2 Degree=3 IsPeriodic=0
    g279: BSplineCurve PolesCount=4 KnotsCount=2 Degree=3 IsPeriodic=0
    g280: BSplineCurve PolesCount=4 KnotsCount=2 Degree=3 IsPeriodic=0
    g281: BSplineCurve PolesCount=2 KnotsCount=2 Degree=1 IsPeriodic=0
    g282: BSplineCurve PolesCount=2 KnotsCount=2 Degree=1 IsPeriodic=0
    g283: BSplineCurve PolesCount=4 KnotsCount=2 Degree=3 IsPeriodic=0
    g284: BSplineCurve PolesCount=4 KnotsCount=2 Degree=3 IsPeriodic=0
    g285: BSplineCurve PolesCount=4 KnotsCount=2 Degree=3 IsPeriodic=0
    g286: BSplineCurve PolesCount=4 KnotsCount=2 Degree=3 IsPeriodic=0
    g287: BSplineCurve PolesCount=4 KnotsCount=2 Degree=3 IsPeriodic=0
    g288: BSplineCurve PolesCount=4 KnotsCount=2 Degree=3 IsPeriodic=0
    g289: BSplineCurve PolesCount=4 KnotsCount=2 Degree=3 IsPeriodic=0
    g290: BSplineCurve PolesCount=4 KnotsCount=2 Degree=3 IsPeriodic=0
    g291: BSplineCurve PolesCount=4 KnotsCount=2 Degree=3 IsPeriodic=0
    g292: BSplineCurve PolesCount=4 KnotsCount=2 Degree=3 IsPeriodic=0
    g293: BSplineCurve PolesCount=4 KnotsCount=2 Degree=3 IsPeriodic=0
  constraints (302):
    c: Coincident(g0,g1)
    c: Coincident(g1,g2)
    c: Coincident(g2,g3)
    c: Coincident(g3,g4)
    c: Coincident(g4,g5)
    c: Coincident(g5,g6)
    c: Coincident(g6,g7)
    c: Coincident(g7,g8)
    c: Coincident(g8,g9)
    c: Coincident(g9,g10)
    c: Coincident(g10,g11)
    c: Coincident(g11,g12)
    c: Coincident(g12,g13)
    c: Coincident(g13,g14)
    c: Coincident(g14,g15)
    c: Coincident(g15,g16)
    c: Coincident(g16,g17)
    c: Coincident(g17,g18)
    c: Coincident(g18,g19)
    c: Coincident(g19,g20)
    c: Coincident(g20,g21)
    c: Coincident(g21,g22)
    c: Coincident(g22,g23)
    c: Coincident(g23,g24)
    c: Coincident(g24,g25)
    c: Coincident(g25,g26)
    c: Coincident(g26,g27)
    c: Coincident(g27,g28)
    c: Coincident(g28,g29)
    c: Coincident(g29,g30)
    c: Coincident(g30,g31)
    c: Coincident(g31,g32)
    c: Coincident(g32,g33)
    c: Coincident(g33,g34)
    c: Coincident(g34,g35)
    c: Coincident(g35,g36)
    c: Coincident(g36,g37)
    c: Coincident(g37,g38)
    c: Coincident(g38,g39)
    c: Coincident(g39,g40)
    c: Coincident(g40,g41)
    c: Coincident(g41,g42)
    c: Coincident(g42,g43)
    c: Coincident(g43,g44)
    c: Coincident(g44,g45)
    c: Coincident(g45,g46)
    c: Coincident(g46,g47)
    c: Coincident(g47,g48)
    c: Coincident(g48,g49)
    c: Coincident(g49,g50)
    c: Coincident(g50,g51)
    c: Coincident(g51,g52)
    c: Coincident(g52,g53)
    c: Coincident(g53,g54)
    c: Coincident(g54,g55)
    c: Coincident(g55,g56)
    c: Coincident(g56,g57)
    c: Coincident(g57,g58)
    c: Coincident(g58,g59)
    c: Coincident(g59,g60)
    c: Coincident(g60,g61)
    c: Coincident(g61,g62)
    c: Coincident(g62,g63)
    c: Coincident(g63,g64)
    c: Coincident(g64,g65)
    c: Coincident(g65,g66)
    c: Coincident(g66,g67)
    c: Coincident(g67,g68)
    c: Coincident(g68,g69)
    c: Coincident(g69,g70)
    c: Coincident(g70,g71)
    c: Coincident(g71,g72)
    c: Coincident(g72,g73)
    c: Coincident(g73,g74)
    c: Coincident(g74,g75)
    c: Coincident(g75,g76)
    c: Coincident(g76,g77)
    c: Coincident(g77,g78)
    c: Coincident(g78,g79)
    c: Coincident(g79,g80)
    c: Coincident(g80,g81)
    c: Coincident(g81,g82)
    c: Coincident(g82,g83)
    c: Coincident(g83,g84)
    c: Coincident(g84,g85)
    c: Coincident(g85,g86)
    c: Coincident(g86,g87)
    c: Coincident(g87,g0)
    c: Coincident(g88,g89)
    c: Coincident(g89,g90)
    c: Coincident(g90,g91)
    c: Coincident(g91,g88)
    c: Coincident(g92,g93)
    c: Coincident(g93,g94)
    c: Coincident(g94,g92)
    c: Coincident(g95,g96)
    c: Coincident(g96,g97)
    c: Coincident(g97,g95)
    c: Coincident(g98,g99)
    c: Coincident(g99,g100)
    c: Coincident(g100,g101)
    c: Coincident(g101,g98)
    c: Coincident(g102,g103)
    c: Coincident(g103,g104)
    c: Coincident(g104,g105)
    c: Coincident(g105,g106)
    c: Coincident(g106,g107)
    c: Coincident(g107,g108)
    c: Coincident(g108,g102)
    c: Coincident(g109,g110)
    c: Coincident(g110,g111)
    c: Coincident(g111,g112)
    c: Coincident(g112,g109)
    c: Coincident(g113,g114)
    c: Coincident(g114,g115)
    c: Coincident(g115,g116)
    c: Coincident(g116,g117)
    c: Coincident(g117,g118)
    c: Coincident(g118,g119)
    c: Coincident(g119,g120)
    c: Coincident(g120,g113)
    c: Coincident(g121,g122)
    c: Coincident(g122,g123)
    c: Coincident(g123,g124)
    c: Coincident(g124,g121)
    c: Coincident(g125,g126)
    c: Coincident(g126,g127)
    c: Coincident(g127,g128)
    c: Coincident(g128,g129)
    c: Coincident(g129,g130)
    c: Coincident(g130,g131)
    c: Coincident(g131,g125)
    c: Coincident(g132,g133)
    c: Coincident(g133,g134)
    c: Coincident(g134,g132)
    c: Coincident(g135,g136)
    c: Coincident(g136,g137)
    c: Coincident(g137,g138)
    c: Coincident(g138,g139)
    c: Coincident(g139,g140)
    c: Coincident(g140,g141)
    c: Coincident(g141,g135)
    c: Coincident(g142,g143)
    c: Coincident(g143,g144)
    c: Coincident(g144,g142)
    c: Coincident(g145,g146)
    c: Coincident(g146,g147)
    c: Coincident(g147,g148)
    c: Coincident(g148,g149)
    c: Coincident(g149,g150)
    c: Coincident(g150,g145)
    c: Coincident(g151,g152)
    c: Coincident(g152,g153)
    c: Coincident(g153,g151)
    c: Coincident(g154,g155)
    c: Coincident(g155,g156)
    c: Coincident(g156,g157)
    c: Coincident(g157,g158)
    c: Coincident(g158,g159)
    c: Coincident(g159,g160)
    c: Coincident(g160,g161)
    c: Coincident(g161,g162)
    c: Coincident(g162,g163)
    c: Coincident(g163,g164)
    c: Coincident(g164,g165)
    c: Coincident(g165,g154)
    c: Coincident(g166,g167)
    c: Coincident(g167,g168)
    c: Coincident(g168,g169)
    c: Coincident(g169,g166)
    c: Coincident(g170,g171)
    c: Coincident(g171,g172)
    c: Coincident(g172,g173)
    c: Coincident(g173,g174)
    c: Coincident(g174,g170)
    c: Coincident(g175,g176)
    c: Coincident(g176,g177)
    c: Coincident(g177,g178)
    c: Coincident(g178,g179)
    c: Coincident(g179,g180)
    c: Coincident(g180,g181)
    c: Coincident(g181,g175)
    c: Coincident(g182,g183)
    c: Coincident(g183,g184)
    c: Coincident(g184,g185)
    c: Coincident(g185,g186)
    c: Coincident(g186,g182)
    c: Coincident(g187,g188)
    c: Coincident(g188,g189)
    c: Coincident(g189,g190)
    c: Coincident(g190,g191)
    c: Coincident(g191,g192)
    c: Coincident(g192,g187)
    c: Coincident(g193,g194)
    c: Coincident(g194,g195)
    c: Coincident(g195,g196)
    c: Coincident(g196,g197)
    c: Coincident(g197,g198)
    c: Coincident(g198,g199)
    c: Coincident(g199,g200)
    c: Coincident(g200,g201)
    c: Coincident(g201,g202)
    c: Coincident(g202,g203)
    c: Coincident(g203,g204)
    c: Coincident(g204,g205)
    c: Coincident(g205,g206)
    c: Coincident(g206,g207)
    c: Coincident(g207,g208)
    c: Coincident(g208,g209)
    c: Coincident(g209,g210)
    c: Coincident(g210,g211)
    c: Coincident(g211,g212)
    c: Coincident(g212,g213)
    c: Coincident(g213,g214)
    c: Coincident(g214,g215)
    c: Coincident(g215,g216)
    c: Coincident(g216,g217)
    c: Coincident(g217,g218)
    c: Coincident(g218,g219)
    c: Coincident(g219,g220)
    c: Coincident(g220,g221)
    c: Coincident(g221,g222)
    c: Coincident(g222,g223)
    c: Coincident(g223,g224)
    c: Coincident(g224,g225)
    c: Coincident(g225,g226)
    c: Coincident(g226,g227)
    c: Coincident(g227,g228)
    c: Coincident(g228,g229)
    c: Coincident(g229,g230)
    c: Coincident(g230,g231)
    c: Coincident(g231,g232)
    c: Coincident(g232,g233)
    c: Coincident(g233,g234)
    c: Coincident(g234,g235)
    c: Coincident(g235,g236)
    c: Coincident(g236,g237)
    c: Coincident(g237,g238)
    c: Coincident(g238,g239)
    c: Coincident(g239,g240)
    c: Coincident(g240,g241)
    c: Coincident(g241,g242)
    c: Coincident(g242,g243)
    c: Coincident(g243,g244)
    c: Coincident(g244,g245)
    c: Coincident(g245,g193)
    c: Coincident(g246,g247)
    c: Coincident(g247,g248)
    c: Coincident(g248,g249)
    c: Coincident(g249,g250)
    c: Coincident(g250,g246)
    c: Coincident(g251,g252)
    c: Coincident(g252,g253)
    c: Coincident(g253,g254)
    c: Coincident(g254,g255)
    c: Coincident(g255,g251)
    c: Coincident(g256,g257)
    c: Coincident(g257,g258)
    c: Coincident(g258,g256)
    c: Coincident(g259,g260)
    c: Coincident(g260,g261)
    c: Coincident(g261,g259)
    c: Coincident(g262,g263)
    c: Coincident(g263,g264)
    c: Coincident(g264,g262)
    c: Coincident(g265,g266)
    c: Coincident(g266,g267)
    c: Coincident(g267,g265)
    c: Coincident(g268,g269)
    c: Coincident(g269,g270)
    c: Coincident(g270,g271)
    c: Coincident(g271,g272)
    c: Coincident(g272,g268)
    c: Coincident(g273,g274)
    c: Coincident(g274,g275)
    c: Coincident(g275,g276)
    c: Coincident(g276,g277)
    c: Coincident(g277,g273)
    c: Coincident(g278,g279)
    c: Coincident(g279,g280)
    c: Coincident(g280,g281)
    c: Coincident(g281,g282)
    c: Coincident(g282,g278)
    c: Coincident(g283,g284)
    c: Coincident(g284,g285)
    c: Coincident(g285,g286)
    c: Coincident(g286,g287)
    c: Coincident(g287,g288)
    c: Coincident(g288,g289)
    c: Coincident(g289,g283)
    c: Coincident(g290,g291)
    c: Coincident(g291,g292)
    c: Coincident(g292,g293)
    c: Coincident(g293,g290)
    c: Coincident(g175,g175)
    c: Coincident(g154,g154)
    c: Coincident(g102,g102)
    c: Coincident(g86,g0)
    c: Coincident(g125,g125)
    c: Coincident(g113,g113)
    c: Coincident(g88,g88)
    c: Coincident(g182,g182)
FEATURE [Sketcher::SketchObject] Sketch016  label="Slayer-Sketch"
  ArcFitTolerance = 1e-06
  FullyConstrained = false
  MakeInternals = false
  sketch-geometry (160):
    g0: BSplineCurve PolesCount=4 KnotsCount=2 Degree=3 IsPeriodic=0
    g1: BSplineCurve PolesCount=4 KnotsCount=2 Degree=3 IsPeriodic=0
    g2: BSplineCurve PolesCount=4 KnotsCount=2 Degree=3 IsPeriodic=0
    g3: BSplineCurve PolesCount=4 KnotsCount=2 Degree=3 IsPeriodic=0
    g4: BSplineCurve PolesCount=4 KnotsCount=2 Degree=3 IsPeriodic=0
    g5: BSplineCurve PolesCount=4 KnotsCount=2 Degree=3 IsPeriodic=0
    g6: BSplineCurve PolesCount=4 KnotsCount=2 Degree=3 IsPeriodic=0
    g7: BSplineCurve PolesCount=4 KnotsCount=2 Degree=3 IsPeriodic=0
    g8: BSplineCurve PolesCount=4 KnotsCount=2 Degree=3 IsPeriodic=0
    g9: BSplineCurve PolesCount=4 KnotsCount=2 Degree=3 IsPeriodic=0
    g10: BSplineCurve PolesCount=4 KnotsCount=2 Degree=3 IsPeriodic=0
    g11: BSplineCurve PolesCount=2 KnotsCount=2 Degree=1 IsPeriodic=0
    g12: BSplineCurve PolesCount=2 KnotsCount=2 Degree=1 IsPeriodic=0
    g13: BSplineCurve PolesCount=2 KnotsCount=2 Degree=1 IsPeriodic=0
    g14: BSplineCurve PolesCount=2 KnotsCount=2 Degree=1 IsPeriodic=0
    g15: BSplineCurve PolesCount=4 KnotsCount=2 Degree=3 IsPeriodic=0
    g16: BSplineCurve PolesCount=4 KnotsCount=2 Degree=3 IsPeriodic=0
    g17: BSplineCurve PolesCount=4 KnotsCount=2 Degree=3 IsPeriodic=0
    g18: BSplineCurve PolesCount=4 KnotsCount=2 Degree=3 IsPeriodic=0
    g19: BSplineCurve PolesCount=4 KnotsCount=2 Degree=3 IsPeriodic=0
    g20: BSplineCurve PolesCount=4 KnotsCount=2 Degree=3 IsPeriodic=0
    g21: BSplineCurve PolesCount=4 KnotsCount=2 Degree=3 IsPeriodic=0
    g22: BSplineCurve PolesCount=4 KnotsCount=2 Degree=3 IsPeriodic=0
    g23: BSplineCurve PolesCount=4 KnotsCount=2 Degree=3 IsPeriodic=0
    g24: BSplineCurve PolesCount=4 KnotsCount=2 Degree=3 IsPeriodic=0
    g25: BSplineCurve PolesCount=4 KnotsCount=2 Degree=3 IsPeriodic=0
    g26: BSplineCurve PolesCount=4 KnotsCount=2 Degree=3 IsPeriodic=0
    g27: BSplineCurve PolesCount=4 KnotsCount=2 Degree=3 IsPeriodic=0
    g28: BSplineCurve PolesCount=4 KnotsCount=2 Degree=3 IsPeriodic=0
    g29: BSplineCurve PolesCount=4 KnotsCount=2 Degree=3 IsPeriodic=0
    g30: BSplineCurve PolesCount=4 KnotsCount=2 Degree=3 IsPeriodic=0
    g31: BSplineCurve PolesCount=4 KnotsCount=2 Degree=3 IsPeriodic=0
    g32: BSplineCurve PolesCount=4 KnotsCount=2 Degree=3 IsPeriodic=0
    g33: BSplineCurve PolesCount=4 KnotsCount=2 Degree=3 IsPeriodic=0
    g34: BSplineCurve PolesCount=4 KnotsCount=2 Degree=3 IsPeriodic=0
    g35: BSplineCurve PolesCount=4 KnotsCount=2 Degree=3 IsPeriodic=0
    g36: BSplineCurve PolesCount=4 KnotsCount=2 Degree=3 IsPeriodic=0
    g37: BSplineCurve PolesCount=4 KnotsCount=2 Degree=3 IsPeriodic=0
    g38: BSplineCurve PolesCount=4 KnotsCount=2 Degree=3 IsPeriodic=0
    g39: BSplineCurve PolesCount=4 KnotsCount=2 Degree=3 IsPeriodic=0
    g40: BSplineCurve PolesCount=4 KnotsCount=2 Degree=3 IsPeriodic=0
    g41: BSplineCurve PolesCount=4 KnotsCount=2 Degree=3 IsPeriodic=0
    g42: BSplineCurve PolesCount=4 KnotsCount=2 Degree=3 IsPeriodic=0
    g43: BSplineCurve PolesCount=4 KnotsCount=2 Degree=3 IsPeriodic=0
    g44: BSplineCurve PolesCount=4 KnotsCount=2 Degree=3 IsPeriodic=0
    g45: BSplineCurve PolesCount=4 KnotsCount=2 Degree=3 IsPeriodic=0
    g46: BSplineCurve PolesCount=4 KnotsCount=2 Degree=3 IsPeriodic=0
    g47: BSplineCurve PolesCount=4 KnotsCount=2 Degree=3 IsPeriodic=0
    g48: BSplineCurve PolesCount=4 KnotsCount=2 Degree=3 IsPeriodic=0
    g49: BSplineCurve PolesCount=4 KnotsCount=2 Degree=3 IsPeriodic=0
    g50: BSplineCurve PolesCount=4 KnotsCount=2 Degree=3 IsPeriodic=0
    g51: BSplineCurve PolesCount=4 KnotsCount=2 Degree=3 IsPeriodic=0
    g52: BSplineCurve PolesCount=4 KnotsCount=2 Degree=3 IsPeriodic=0
    g53: BSplineCurve PolesCount=4 KnotsCount=2 Degree=3 IsPeriodic=0
    g54: BSplineCurve PolesCount=4 KnotsCount=2 Degree=3 IsPeriodic=0
    g55: BSplineCurve PolesCount=4 KnotsCount=2 Degree=3 IsPeriodic=0
    g56: BSplineCurve PolesCount=4 KnotsCount=2 Degree=3 IsPeriodic=0
    g57: BSplineCurve PolesCount=4 KnotsCount=2 Degree=3 IsPeriodic=0
    g58: BSplineCurve PolesCount=4 KnotsCount=2 Degree=3 IsPeriodic=0
    g59: BSplineCurve PolesCount=4 KnotsCount=2 Degree=3 IsPeriodic=0
    g60: BSplineCurve PolesCount=4 KnotsCount=2 Degree=3 IsPeriodic=0
    g61: BSplineCurve PolesCount=4 KnotsCount=2 Degree=3 IsPeriodic=0
    g62: BSplineCurve PolesCount=4 KnotsCount=2 Degree=3 IsPeriodic=0
    g63: BSplineCurve PolesCount=4 KnotsCount=2 Degree=3 IsPeriodic=0
    g64: BSplineCurve PolesCount=4 KnotsCount=2 Degree=3 IsPeriodic=0
    g65: BSplineCurve PolesCount=2 KnotsCount=2 Degree=1 IsPeriodic=0
    g66: BSplineCurve PolesCount=2 KnotsCount=2 Degree=1 IsPeriodic=0
    g67: BSplineCurve PolesCount=4 KnotsCount=2 Degree=3 IsPeriodic=0
    g68: BSplineCurve PolesCount=4 KnotsCount=2 Degree=3 IsPeriodic=0
    g69: BSplineCurve PolesCount=4 KnotsCount=2 Degree=3 IsPeriodic=0
    g70: BSplineCurve PolesCount=4 KnotsCount=2 Degree=3 IsPeriodic=0
    g71: BSplineCurve PolesCount=2 KnotsCount=2 Degree=1 IsPeriodic=0
    g72: BSplineCurve PolesCount=4 KnotsCount=2 Degree=3 IsPeriodic=0
    g73: BSplineCurve PolesCount=2 KnotsCount=2 Degree=1 IsPeriodic=0
    g74: BSplineCurve PolesCount=2 KnotsCount=2 Degree=1 IsPeriodic=0
    g75: BSplineCurve PolesCount=4 KnotsCount=2 Degree=3 IsPeriodic=0
    g76: BSplineCurve PolesCount=4 KnotsCount=2 Degree=3 IsPeriodic=0
    g77: BSplineCurve PolesCount=4 KnotsCount=2 Degree=3 IsPeriodic=0
    g78: BSplineCurve PolesCount=4 KnotsCount=2 Degree=3 IsPeriodic=0
    g79: BSplineCurve PolesCount=4 KnotsCount=2 Degree=3 IsPeriodic=0
    g80: BSplineCurve PolesCount=2 KnotsCount=2 Degree=1 IsPeriodic=0
    g81: BSplineCurve PolesCount=2 KnotsCount=2 Degree=1 IsPeriodic=0
    g82: BSplineCurve PolesCount=4 KnotsCount=2 Degree=3 IsPeriodic=0
    g83: BSplineCurve PolesCount=4 KnotsCount=2 Degree=3 IsPeriodic=0
    g84: BSplineCurve PolesCount=4 KnotsCount=2 Degree=3 IsPeriodic=0
    g85: BSplineCurve PolesCount=2 KnotsCount=2 Degree=1 IsPeriodic=0
    g86: BSplineCurve PolesCount=4 KnotsCount=2 Degree=3 IsPeriodic=0
    g87: BSplineCurve PolesCount=4 KnotsCount=2 Degree=3 IsPeriodic=0
    g88: BSplineCurve PolesCount=4 KnotsCount=2 Degree=3 IsPeriodic=0
    g89: BSplineCurve PolesCount=4 KnotsCount=2 Degree=3 IsPeriodic=0
    g90: BSplineCurve PolesCount=2 KnotsCount=2 Degree=1 IsPeriodic=0
    g91: BSplineCurve PolesCount=2 KnotsCount=2 Degree=1 IsPeriodic=0
    g92: BSplineCurve PolesCount=4 KnotsCount=2 Degree=3 IsPeriodic=0
    g93: BSplineCurve PolesCount=4 KnotsCount=2 Degree=3 IsPeriodic=0
    g94: BSplineCurve PolesCount=4 KnotsCount=2 Degree=3 IsPeriodic=0
    g95: BSplineCurve PolesCount=4 KnotsCount=2 Degree=3 IsPeriodic=0
    g96: BSplineCurve PolesCount=4 KnotsCount=2 Degree=3 IsPeriodic=0
    g97: BSplineCurve PolesCount=4 KnotsCount=2 Degree=3 IsPeriodic=0
    g98: BSplineCurve PolesCount=4 KnotsCount=2 Degree=3 IsPeriodic=0
    g99: BSplineCurve PolesCount=4 KnotsCount=2 Degree=3 IsPeriodic=0
    g100: BSplineCurve PolesCount=4 KnotsCount=2 Degree=3 IsPeriodic=0
    g101: BSplineCurve PolesCount=4 KnotsCount=2 Degree=3 IsPeriodic=0
    g102: BSplineCurve PolesCount=4 KnotsCount=2 Degree=3 IsPeriodic=0
    g103: BSplineCurve PolesCount=4 KnotsCount=2 Degree=3 IsPeriodic=0
    g104: BSplineCurve PolesCount=4 KnotsCount=2 Degree=3 IsPeriodic=0
    g105: BSplineCurve PolesCount=4 KnotsCount=2 Degree=3 IsPeriodic=0
    g106: BSplineCurve PolesCount=4 KnotsCount=2 Degree=3 IsPeriodic=0
    g107: BSplineCurve PolesCount=4 KnotsCount=2 Degree=3 IsPeriodic=0
    g108: BSplineCurve PolesCount=4 KnotsCount=2 Degree=3 IsPeriodic=0
    g109: BSplineCurve PolesCount=4 KnotsCount=2 Degree=3 IsPeriodic=0
    g110: BSplineCurve PolesCount=4 KnotsCount=2 Degree=3 IsPeriodic=0
    g111: BSplineCurve PolesCount=4 KnotsCount=2 Degree=3 IsPeriodic=0
    g112: BSplineCurve PolesCount=4 KnotsCount=2 Degree=3 IsPeriodic=0
    g113: BSplineCurve PolesCount=4 KnotsCount=2 Degree=3 IsPeriodic=0
    g114: BSplineCurve PolesCount=4 KnotsCount=2 Degree=3 IsPeriodic=0
    g115: BSplineCurve PolesCount=4 KnotsCount=2 Degree=3 IsPeriodic=0
    g116: BSplineCurve PolesCount=4 KnotsCount=2 Degree=3 IsPeriodic=0
    g117: BSplineCurve PolesCount=4 KnotsCount=2 Degree=3 IsPeriodic=0
    g118: BSplineCurve PolesCount=2 KnotsCount=2 Degree=1 IsPeriodic=0
    g119: BSplineCurve PolesCount=4 KnotsCount=2 Degree=3 IsPeriodic=0
    g120: BSplineCurve PolesCount=4 KnotsCount=2 Degree=3 IsPeriodic=0
    g121: BSplineCurve PolesCount=4 KnotsCount=2 Degree=3 IsPeriodic=0
    g122: BSplineCurve PolesCount=4 KnotsCount=2 Degree=3 IsPeriodic=0
    g123: BSplineCurve PolesCount=4 KnotsCount=2 Degree=3 IsPeriodic=0
    g124: BSplineCurve PolesCount=4 KnotsCount=2 Degree=3 IsPeriodic=0
    g125: BSplineCurve PolesCount=2 KnotsCount=2 Degree=1 IsPeriodic=0
    g126: BSplineCurve PolesCount=2 KnotsCount=2 Degree=1 IsPeriodic=0
    g127: BSplineCurve PolesCount=4 KnotsCount=2 Degree=3 IsPeriodic=0
    g128: BSplineCurve PolesCount=4 KnotsCount=2 Degree=3 IsPeriodic=0
    g129: BSplineCurve PolesCount=4 KnotsCount=2 Degree=3 IsPeriodic=0
    g130: BSplineCurve PolesCount=4 KnotsCount=2 Degree=3 IsPeriodic=0
    g131: BSplineCurve PolesCount=4 KnotsCount=2 Degree=3 IsPeriodic=0
    g132: BSplineCurve PolesCount=4 KnotsCount=2 Degree=3 IsPeriodic=0
    g133: BSplineCurve PolesCount=4 KnotsCount=2 Degree=3 IsPeriodic=0
    g134: BSplineCurve PolesCount=4 KnotsCount=2 Degree=3 IsPeriodic=0
    g135: BSplineCurve PolesCount=4 KnotsCount=2 Degree=3 IsPeriodic=0
    g136: BSplineCurve PolesCount=4 KnotsCount=2 Degree=3 IsPeriodic=0
    g137: BSplineCurve PolesCount=4 KnotsCount=2 Degree=3 IsPeriodic=0
    g138: BSplineCurve PolesCount=4 KnotsCount=2 Degree=3 IsPeriodic=0
    g139: BSplineCurve PolesCount=4 KnotsCount=2 Degree=3 IsPeriodic=0
    g140: BSplineCurve PolesCount=4 KnotsCount=2 Degree=3 IsPeriodic=0
    g141: BSplineCurve PolesCount=4 KnotsCount=2 Degree=3 IsPeriodic=0
    g142: BSplineCurve PolesCount=4 KnotsCount=2 Degree=3 IsPeriodic=0
    g143: BSplineCurve PolesCount=4 KnotsCount=2 Degree=3 IsPeriodic=0
    g144: BSplineCurve PolesCount=4 KnotsCount=2 Degree=3 IsPeriodic=0
    g145: BSplineCurve PolesCount=4 KnotsCount=2 Degree=3 IsPeriodic=0
    g146: BSplineCurve PolesCount=2 KnotsCount=2 Degree=1 IsPeriodic=0
    g147: BSplineCurve PolesCount=2 KnotsCount=2 Degree=1 IsPeriodic=0
    g148: BSplineCurve PolesCount=4 KnotsCount=2 Degree=3 IsPeriodic=0
    g149: BSplineCurve PolesCount=4 KnotsCount=2 Degree=3 IsPeriodic=0
    g150: BSplineCurve PolesCount=4 KnotsCount=2 Degree=3 IsPeriodic=0
    g151: BSplineCurve PolesCount=4 KnotsCount=2 Degree=3 IsPeriodic=0
    g152: BSplineCurve PolesCount=2 KnotsCount=2 Degree=1 IsPeriodic=0
    g153: BSplineCurve PolesCount=4 KnotsCount=2 Degree=3 IsPeriodic=0
    g154: BSplineCurve PolesCount=4 KnotsCount=2 Degree=3 IsPeriodic=0
    g155: BSplineCurve PolesCount=4 KnotsCount=2 Degree=3 IsPeriodic=0
    g156: BSplineCurve PolesCount=4 KnotsCount=2 Degree=3 IsPeriodic=0
    g157: BSplineCurve PolesCount=4 KnotsCount=2 Degree=3 IsPeriodic=0
    g158: BSplineCurve PolesCount=4 KnotsCount=2 Degree=3 IsPeriodic=0
    g159: BSplineCurve PolesCount=4 KnotsCount=2 Degree=3 IsPeriodic=0
  constraints (162):
    c: Coincident(g0,g1)
    c: Coincident(g1,g2)
    c: Coincident(g2,g3)
    c: Coincident(g3,g4)
    c: Coincident(g4,g5)
    c: Coincident(g5,g6)
    c: Coincident(g6,g7)
    c: Coincident(g7,g8)
    c: Coincident(g8,g9)
    c: Coincident(g9,g10)
    c: Coincident(g10,g11)
    c: Coincident(g11,g12)
    c: Coincident(g12,g13)
    c: Coincident(g13,g14)
    c: Coincident(g14,g15)
    c: Coincident(g15,g16)
    c: Coincident(g16,g17)
    c: Coincident(g17,g18)
    c: Coincident(g18,g19)
    c: Coincident(g19,g20)
    c: Coincident(g20,g21)
    c: Coincident(g21,g22)
    c: Coincident(g22,g23)
    c: Coincident(g23,g24)
    c: Coincident(g24,g25)
    c: Coincident(g25,g26)
    c: Coincident(g26,g27)
    c: Coincident(g27,g28)
    c: Coincident(g28,g29)
    c: Coincident(g29,g30)
    c: Coincident(g30,g31)
    c: Coincident(g31,g32)
    c: Coincident(g32,g33)
    c: Coincident(g33,g34)
    c: Coincident(g34,g35)
    c: Coincident(g35,g36)
    c: Coincident(g36,g37)
    c: Coincident(g37,g38)
    c: Coincident(g38,g39)
    c: Coincident(g39,g40)
    c: Coincident(g40,g41)
    c: Coincident(g41,g42)
    c: Coincident(g42,g43)
    c: Coincident(g43,g44)
    c: Coincident(g44,g45)
    c: Coincident(g45,g46)
    c: Coincident(g46,g47)
    c: Coincident(g47,g48)
    c: Coincident(g48,g49)
    c: Coincident(g49,g50)
    c: Coincident(g50,g51)
    c: Coincident(g51,g52)
    c: Coincident(g52,g53)
    c: Coincident(g53,g54)
    c: Coincident(g54,g55)
    c: Coincident(g55,g56)
    c: Coincident(g56,g57)
    c: Coincident(g57,g58)
    c: Coincident(g58,g59)
    c: Coincident(g59,g60)
    c: Coincident(g60,g61)
    c: Coincident(g61,g62)
    c: Coincident(g62,g63)
    c: Coincident(g63,g64)
    c: Coincident(g64,g65)
    c: Coincident(g65,g66)
    c: Coincident(g66,g0)
    c: Coincident(g67,g68)
    c: Coincident(g68,g69)
    c: Coincident(g69,g70)
    c: Coincident(g70,g67)
    c: Coincident(g71,g72)
    c: Coincident(g72,g73)
    c: Coincident(g73,g74)
    c: Coincident(g74,g75)
    c: Coincident(g75,g76)
    c: Coincident(g76,g77)
    c: Coincident(g77,g78)
    c: Coincident(g78,g79)
    c: Coincident(g79,g80)
    c: Coincident(g80,g81)
    c: Coincident(g81,g82)
    c: Coincident(g82,g83)
    c: Coincident(g83,g84)
    c: Coincident(g84,g85)
    c: Coincident(g85,g71)
    c: Coincident(g86,g87)
    c: Coincident(g87,g88)
    c: Coincident(g88,g89)
    c: Coincident(g89,g90)
    c: Coincident(g90,g91)
    c: Coincident(g91,g86)
    c: Coincident(g92,g93)
    c: Coincident(g93,g94)
    c: Coincident(g94,g95)
    c: Coincident(g95,g96)
    c: Coincident(g96,g97)
    c: Coincident(g97,g98)
    c: Coincident(g98,g99)
    c: Coincident(g99,g100)
    c: Coincident(g100,g92)
    c: Coincident(g101,g102)
    c: Coincident(g102,g103)
    c: Coincident(g103,g104)
    c: Coincident(g104,g105)
    c: Coincident(g105,g106)
    c: Coincident(g106,g107)
    c: Coincident(g107,g101)
    c: Coincident(g108,g109)
    c: Coincident(g109,g110)
    c: Coincident(g110,g111)
    c: Coincident(g111,g112)
    c: Coincident(g112,g108)
    c: Coincident(g113,g114)
    c: Coincident(g114,g115)
    c: Coincident(g115,g116)
    c: Coincident(g116,g117)
    c: Coincident(g117,g113)
    c: Coincident(g118,g119)
    c: Coincident(g119,g120)
    c: Coincident(g120,g121)
    c: Coincident(g121,g122)
    c: Coincident(g122,g123)
    c: Coincident(g123,g124)
    c: Coincident(g124,g125)
    c: Coincident(g125,g126)
    c: Coincident(g126,g127)
    c: Coincident(g127,g128)
    c: Coincident(g128,g129)
    c: Coincident(g129,g130)
    c: Coincident(g130,g131)
    c: Coincident(g131,g132)
    c: Coincident(g132,g133)
    c: Coincident(g133,g118)
    c: Coincident(g134,g135)
    c: Coincident(g135,g136)
    c: Coincident(g136,g134)
    c: Coincident(g137,g138)
    c: Coincident(g138,g139)
    c: Coincident(g139,g140)
    c: Coincident(g140,g137)
    c: Coincident(g141,g142)
    c: Coincident(g142,g143)
    c: Coincident(g143,g144)
    c: Coincident(g144,g145)
    c: Coincident(g145,g146)
    c: Coincident(g146,g147)
    c: Coincident(g147,g148)
    c: Coincident(g148,g149)
    c: Coincident(g149,g150)
    c: Coincident(g150,g151)
    c: Coincident(g151,g141)
    c: Coincident(g152,g153)
    c: Coincident(g153,g154)
    c: Coincident(g154,g155)
    c: Coincident(g155,g156)
    c: Coincident(g156,g157)
    c: Coincident(g157,g158)
    c: Coincident(g158,g159)
    c: Coincident(g159,g152)
    c: Coincident(g152,g152)
    c: Coincident(g118,g118)
FEATURE [Sketcher::SketchObject] Sketch017  label="Soldier-Sketch"
  ArcFitTolerance = 1e-06
  FullyConstrained = false
  MakeInternals = false
  sketch-geometry (256):
    g0: BSplineCurve PolesCount=4 KnotsCount=2 Degree=3 IsPeriodic=0
    g1: BSplineCurve PolesCount=4 KnotsCount=2 Degree=3 IsPeriodic=0
    g2: BSplineCurve PolesCount=4 KnotsCount=2 Degree=3 IsPeriodic=0
    g3: BSplineCurve PolesCount=4 KnotsCount=2 Degree=3 IsPeriodic=0
    g4: BSplineCurve PolesCount=4 KnotsCount=2 Degree=3 IsPeriodic=0
    g5: BSplineCurve PolesCount=4 KnotsCount=2 Degree=3 IsPeriodic=0
    g6: BSplineCurve PolesCount=4 KnotsCount=2 Degree=3 IsPeriodic=0
    g7: BSplineCurve PolesCount=2 KnotsCount=2 Degree=1 IsPeriodic=0
    g8: BSplineCurve PolesCount=2 KnotsCount=2 Degree=1 IsPeriodic=0
    g9: BSplineCurve PolesCount=4 KnotsCount=2 Degree=3 IsPeriodic=0
    g10: BSplineCurve PolesCount=4 KnotsCount=2 Degree=3 IsPeriodic=0
    g11: BSplineCurve PolesCount=2 KnotsCount=2 Degree=1 IsPeriodic=0
    g12: BSplineCurve PolesCount=2 KnotsCount=2 Degree=1 IsPeriodic=0
    g13: BSplineCurve PolesCount=2 KnotsCount=2 Degree=1 IsPeriodic=0
    g14: BSplineCurve PolesCount=2 KnotsCount=2 Degree=1 IsPeriodic=0
    g15: BSplineCurve PolesCount=4 KnotsCount=2 Degree=3 IsPeriodic=0
    g16: BSplineCurve PolesCount=4 KnotsCount=2 Degree=3 IsPeriodic=0
    g17: BSplineCurve PolesCount=4 KnotsCount=2 Degree=3 IsPeriodic=0
    g18: BSplineCurve PolesCount=4 KnotsCount=2 Degree=3 IsPeriodic=0
    g19: BSplineCurve PolesCount=4 KnotsCount=2 Degree=3 IsPeriodic=0
    g20: BSplineCurve PolesCount=4 KnotsCount=2 Degree=3 IsPeriodic=0
    g21: BSplineCurve PolesCount=4 KnotsCount=2 Degree=3 IsPeriodic=0
    g22: BSplineCurve PolesCount=4 KnotsCount=2 Degree=3 IsPeriodic=0
    g23: BSplineCurve PolesCount=4 KnotsCount=2 Degree=3 IsPeriodic=0
    g24: BSplineCurve PolesCount=4 KnotsCount=2 Degree=3 IsPeriodic=0
    g25: BSplineCurve PolesCount=4 KnotsCount=2 Degree=3 IsPeriodic=0
    g26: BSplineCurve PolesCount=4 KnotsCount=2 Degree=3 IsPeriodic=0
    g27: BSplineCurve PolesCount=4 KnotsCount=2 Degree=3 IsPeriodic=0
    g28: BSplineCurve PolesCount=4 KnotsCount=2 Degree=3 IsPeriodic=0
    g29: BSplineCurve PolesCount=4 KnotsCount=2 Degree=3 IsPeriodic=0
    g30: BSplineCurve PolesCount=4 KnotsCount=2 Degree=3 IsPeriodic=0
    g31: BSplineCurve PolesCount=4 KnotsCount=2 Degree=3 IsPeriodic=0
    g32: BSplineCurve PolesCount=4 KnotsCount=2 Degree=3 IsPeriodic=0
    g33: BSplineCurve PolesCount=4 KnotsCount=2 Degree=3 IsPeriodic=0
    g34: BSplineCurve PolesCount=4 KnotsCount=2 Degree=3 IsPeriodic=0
    g35: BSplineCurve PolesCount=2 KnotsCount=2 Degree=1 IsPeriodic=0
    g36: BSplineCurve PolesCount=2 KnotsCount=2 Degree=1 IsPeriodic=0
    g37: BSplineCurve PolesCount=4 KnotsCount=2 Degree=3 IsPeriodic=0
    g38: BSplineCurve PolesCount=4 KnotsCount=2 Degree=3 IsPeriodic=0
    g39: BSplineCurve PolesCount=4 KnotsCount=2 Degree=3 IsPeriodic=0
    g40: BSplineCurve PolesCount=4 KnotsCount=2 Degree=3 IsPeriodic=0
    g41: BSplineCurve PolesCount=4 KnotsCount=2 Degree=3 IsPeriodic=0
    g42: BSplineCurve PolesCount=4 KnotsCount=2 Degree=3 IsPeriodic=0
    g43: BSplineCurve PolesCount=4 KnotsCount=2 Degree=3 IsPeriodic=0
    g44: BSplineCurve PolesCount=4 KnotsCount=2 Degree=3 IsPeriodic=0
    g45: BSplineCurve PolesCount=2 KnotsCount=2 Degree=1 IsPeriodic=0
    g46: BSplineCurve PolesCount=2 KnotsCount=2 Degree=1 IsPeriodic=0
    g47: BSplineCurve PolesCount=4 KnotsCount=2 Degree=3 IsPeriodic=0
    g48: BSplineCurve PolesCount=4 KnotsCount=2 Degree=3 IsPeriodic=0
    g49: BSplineCurve PolesCount=4 KnotsCount=2 Degree=3 IsPeriodic=0
    g50: BSplineCurve PolesCount=4 KnotsCount=2 Degree=3 IsPeriodic=0
    g51: BSplineCurve PolesCount=4 KnotsCount=2 Degree=3 IsPeriodic=0
    g52: BSplineCurve PolesCount=4 KnotsCount=2 Degree=3 IsPeriodic=0
    g53: BSplineCurve PolesCount=4 KnotsCount=2 Degree=3 IsPeriodic=0
    g54: BSplineCurve PolesCount=4 KnotsCount=2 Degree=3 IsPeriodic=0
    g55: BSplineCurve PolesCount=4 KnotsCount=2 Degree=3 IsPeriodic=0
    g56: BSplineCurve PolesCount=4 KnotsCount=2 Degree=3 IsPeriodic=0
    g57: BSplineCurve PolesCount=2 KnotsCount=2 Degree=1 IsPeriodic=0
    g58: BSplineCurve PolesCount=2 KnotsCount=2 Degree=1 IsPeriodic=0
    g59: BSplineCurve PolesCount=2 KnotsCount=2 Degree=1 IsPeriodic=0
    g60: BSplineCurve PolesCount=4 KnotsCount=2 Degree=3 IsPeriodic=0
    g61: BSplineCurve PolesCount=2 KnotsCount=2 Degree=1 IsPeriodic=0
    g62: BSplineCurve PolesCount=2 KnotsCount=2 Degree=1 IsPeriodic=0
    g63: BSplineCurve PolesCount=2 KnotsCount=2 Degree=1 IsPeriodic=0
    g64: BSplineCurve PolesCount=2 KnotsCount=2 Degree=1 IsPeriodic=0
    g65: BSplineCurve PolesCount=4 KnotsCount=2 Degree=3 IsPeriodic=0
    g66: BSplineCurve PolesCount=4 KnotsCount=2 Degree=3 IsPeriodic=0
    g67: BSplineCurve PolesCount=4 KnotsCount=2 Degree=3 IsPeriodic=0
    g68: BSplineCurve PolesCount=4 KnotsCount=2 Degree=3 IsPeriodic=0
    g69: BSplineCurve PolesCount=4 KnotsCount=2 Degree=3 IsPeriodic=0
    g70: BSplineCurve PolesCount=4 KnotsCount=2 Degree=3 IsPeriodic=0
    g71: BSplineCurve PolesCount=4 KnotsCount=2 Degree=3 IsPeriodic=0
    g72: BSplineCurve PolesCount=2 KnotsCount=2 Degree=1 IsPeriodic=0
    g73: BSplineCurve PolesCount=2 KnotsCount=2 Degree=1 IsPeriodic=0
    g74: BSplineCurve PolesCount=4 KnotsCount=2 Degree=3 IsPeriodic=0
    g75: BSplineCurve PolesCount=4 KnotsCount=2 Degree=3 IsPeriodic=0
    g76: BSplineCurve PolesCount=4 KnotsCount=2 Degree=3 IsPeriodic=0
    g77: BSplineCurve PolesCount=2 KnotsCount=2 Degree=1 IsPeriodic=0
    g78: BSplineCurve PolesCount=2 KnotsCount=2 Degree=1 IsPeriodic=0
    g79: BSplineCurve PolesCount=4 KnotsCount=2 Degree=3 IsPeriodic=0
    g80: BSplineCurve PolesCount=2 KnotsCount=2 Degree=1 IsPeriodic=0
    g81: BSplineCurve PolesCount=2 KnotsCount=2 Degree=1 IsPeriodic=0
    g82: BSplineCurve PolesCount=4 KnotsCount=2 Degree=3 IsPeriodic=0
    g83: BSplineCurve PolesCount=4 KnotsCount=2 Degree=3 IsPeriodic=0
    g84: BSplineCurve PolesCount=4 KnotsCount=2 Degree=3 IsPeriodic=0
    g85: BSplineCurve PolesCount=4 KnotsCount=2 Degree=3 IsPeriodic=0
    g86: BSplineCurve PolesCount=4 KnotsCount=2 Degree=3 IsPeriodic=0
    g87: BSplineCurve PolesCount=4 KnotsCount=2 Degree=3 IsPeriodic=0
    g88: BSplineCurve PolesCount=4 KnotsCount=2 Degree=3 IsPeriodic=0
    g89: BSplineCurve PolesCount=4 KnotsCount=2 Degree=3 IsPeriodic=0
    g90: BSplineCurve PolesCount=4 KnotsCount=2 Degree=3 IsPeriodic=0
    g91: BSplineCurve PolesCount=4 KnotsCount=2 Degree=3 IsPeriodic=0
    g92: BSplineCurve PolesCount=4 KnotsCount=2 Degree=3 IsPeriodic=0
    g93: BSplineCurve PolesCount=4 KnotsCount=2 Degree=3 IsPeriodic=0
    g94: BSplineCurve PolesCount=2 KnotsCount=2 Degree=1 IsPeriodic=0
    g95: BSplineCurve PolesCount=2 KnotsCount=2 Degree=1 IsPeriodic=0
    g96: BSplineCurve PolesCount=4 KnotsCount=2 Degree=3 IsPeriodic=0
    g97: BSplineCurve PolesCount=4 KnotsCount=2 Degree=3 IsPeriodic=0
    g98: BSplineCurve PolesCount=4 KnotsCount=2 Degree=3 IsPeriodic=0
    g99: BSplineCurve PolesCount=4 KnotsCount=2 Degree=3 IsPeriodic=0
    g100: BSplineCurve PolesCount=4 KnotsCount=2 Degree=3 IsPeriodic=0
    g101: BSplineCurve PolesCount=4 KnotsCount=2 Degree=3 IsPeriodic=0
    g102: BSplineCurve PolesCount=4 KnotsCount=2 Degree=3 IsPeriodic=0
    g103: BSplineCurve PolesCount=4 KnotsCount=2 Degree=3 IsPeriodic=0
    g104: BSplineCurve PolesCount=4 KnotsCount=2 Degree=3 IsPeriodic=0
    g105: BSplineCurve PolesCount=4 KnotsCount=2 Degree=3 IsPeriodic=0
    g106: BSplineCurve PolesCount=2 KnotsCount=2 Degree=1 IsPeriodic=0
    g107: BSplineCurve PolesCount=2 KnotsCount=2 Degree=1 IsPeriodic=0
    g108: BSplineCurve PolesCount=4 KnotsCount=2 Degree=3 IsPeriodic=0
    g109: BSplineCurve PolesCount=4 KnotsCount=2 Degree=3 IsPeriodic=0
    g110: BSplineCurve PolesCount=4 KnotsCount=2 Degree=3 IsPeriodic=0
    g111: BSplineCurve PolesCount=4 KnotsCount=2 Degree=3 IsPeriodic=0
    g112: BSplineCurve PolesCount=4 KnotsCount=2 Degree=3 IsPeriodic=0
    g113: BSplineCurve PolesCount=4 KnotsCount=2 Degree=3 IsPeriodic=0
    g114: BSplineCurve PolesCount=2 KnotsCount=2 Degree=1 IsPeriodic=0
    g115: BSplineCurve PolesCount=2 KnotsCount=2 Degree=1 IsPeriodic=0
    g116: BSplineCurve PolesCount=4 KnotsCount=2 Degree=3 IsPeriodic=0
    g117: BSplineCurve PolesCount=4 KnotsCount=2 Degree=3 IsPeriodic=0
    g118: BSplineCurve PolesCount=4 KnotsCount=2 Degree=3 IsPeriodic=0
    g119: BSplineCurve PolesCount=4 KnotsCount=2 Degree=3 IsPeriodic=0
    g120: BSplineCurve PolesCount=4 KnotsCount=2 Degree=3 IsPeriodic=0
    g121: BSplineCurve PolesCount=4 KnotsCount=2 Degree=3 IsPeriodic=0
    g122: BSplineCurve PolesCount=4 KnotsCount=2 Degree=3 IsPeriodic=0
    g123: BSplineCurve PolesCount=4 KnotsCount=2 Degree=3 IsPeriodic=0
    g124: BSplineCurve PolesCount=4 KnotsCount=2 Degree=3 IsPeriodic=0
    g125: BSplineCurve PolesCount=4 KnotsCount=2 Degree=3 IsPeriodic=0
    g126: BSplineCurve PolesCount=4 KnotsCount=2 Degree=3 IsPeriodic=0
    g127: BSplineCurve PolesCount=4 KnotsCount=2 Degree=3 IsPeriodic=0
    g128: BSplineCurve PolesCount=4 KnotsCount=2 Degree=3 IsPeriodic=0
    g129: BSplineCurve PolesCount=4 KnotsCount=2 Degree=3 IsPeriodic=0
    g130: BSplineCurve PolesCount=2 KnotsCount=2 Degree=1 IsPeriodic=0
    g131: BSplineCurve PolesCount=4 KnotsCount=2 Degree=3 IsPeriodic=0
    g132: BSplineCurve PolesCount=4 KnotsCount=2 Degree=3 IsPeriodic=0
    g133: BSplineCurve PolesCount=4 KnotsCount=2 Degree=3 IsPeriodic=0
    g134: BSplineCurve PolesCount=4 KnotsCount=2 Degree=3 IsPeriodic=0
    g135: BSplineCurve PolesCount=4 KnotsCount=2 Degree=3 IsPeriodic=0
    g136: BSplineCurve PolesCount=4 KnotsCount=2 Degree=3 IsPeriodic=0
    g137: BSplineCurve PolesCount=4 KnotsCount=2 Degree=3 IsPeriodic=0
    g138: BSplineCurve PolesCount=4 KnotsCount=2 Degree=3 IsPeriodic=0
    g139: BSplineCurve PolesCount=4 KnotsCount=2 Degree=3 IsPeriodic=0
    g140: BSplineCurve PolesCount=4 KnotsCount=2 Degree=3 IsPeriodic=0
    g141: BSplineCurve PolesCount=4 KnotsCount=2 Degree=3 IsPeriodic=0
    g142: BSplineCurve PolesCount=4 KnotsCount=2 Degree=3 IsPeriodic=0
    g143: BSplineCurve PolesCount=4 KnotsCount=2 Degree=3 IsPeriodic=0
    g144: BSplineCurve PolesCount=4 KnotsCount=2 Degree=3 IsPeriodic=0
    g145: BSplineCurve PolesCount=4 KnotsCount=2 Degree=3 IsPeriodic=0
    g146: BSplineCurve PolesCount=4 KnotsCount=2 Degree=3 IsPeriodic=0
    g147: BSplineCurve PolesCount=4 KnotsCount=2 Degree=3 IsPeriodic=0
    g148: BSplineCurve PolesCount=4 KnotsCount=2 Degree=3 IsPeriodic=0
    g149: BSplineCurve PolesCount=4 KnotsCount=2 Degree=3 IsPeriodic=0
    g150: BSplineCurve PolesCount=2 KnotsCount=2 Degree=1 IsPeriodic=0
    g151: BSplineCurve PolesCount=2 KnotsCount=2 Degree=1 IsPeriodic=0
    g152: BSplineCurve PolesCount=2 KnotsCount=2 Degree=1 IsPeriodic=0
    g153: BSplineCurve PolesCount=2 KnotsCount=2 Degree=1 IsPeriodic=0
    g154: BSplineCurve PolesCount=4 KnotsCount=2 Degree=3 IsPeriodic=0
    g155: BSplineCurve PolesCount=2 KnotsCount=2 Degree=1 IsPeriodic=0
    g156: BSplineCurve PolesCount=2 KnotsCount=2 Degree=1 IsPeriodic=0
    g157: BSplineCurve PolesCount=4 KnotsCount=2 Degree=3 IsPeriodic=0
    g158: BSplineCurve PolesCount=4 KnotsCount=2 Degree=3 IsPeriodic=0
    g159: BSplineCurve PolesCount=4 KnotsCount=2 Degree=3 IsPeriodic=0
    g160: BSplineCurve PolesCount=2 KnotsCount=2 Degree=1 IsPeriodic=0
    g161: BSplineCurve PolesCount=2 KnotsCount=2 Degree=1 IsPeriodic=0
    g162: BSplineCurve PolesCount=4 KnotsCount=2 Degree=3 IsPeriodic=0
    g163: BSplineCurve PolesCount=4 KnotsCount=2 Degree=3 IsPeriodic=0
    g164: BSplineCurve PolesCount=4 KnotsCount=2 Degree=3 IsPeriodic=0
    g165: BSplineCurve PolesCount=4 KnotsCount=2 Degree=3 IsPeriodic=0
    g166: BSplineCurve PolesCount=4 KnotsCount=2 Degree=3 IsPeriodic=0
    g167: BSplineCurve PolesCount=4 KnotsCount=2 Degree=3 IsPeriodic=0
    g168: BSplineCurve PolesCount=2 KnotsCount=2 Degree=1 IsPeriodic=0
    g169: BSplineCurve PolesCount=2 KnotsCount=2 Degree=1 IsPeriodic=0
    g170: BSplineCurve PolesCount=2 KnotsCount=2 Degree=1 IsPeriodic=0
    g171: BSplineCurve PolesCount=2 KnotsCount=2 Degree=1 IsPeriodic=0
    g172: BSplineCurve PolesCount=4 KnotsCount=2 Degree=3 IsPeriodic=0
    g173: BSplineCurve PolesCount=4 KnotsCount=2 Degree=3 IsPeriodic=0
    g174: BSplineCurve PolesCount=4 KnotsCount=2 Degree=3 IsPeriodic=0
    g175: BSplineCurve PolesCount=2 KnotsCount=2 Degree=1 IsPeriodic=0
    g176: BSplineCurve PolesCount=2 KnotsCount=2 Degree=1 IsPeriodic=0
    g177: BSplineCurve PolesCount=4 KnotsCount=2 Degree=3 IsPeriodic=0
    g178: BSplineCurve PolesCount=4 KnotsCount=2 Degree=3 IsPeriodic=0
    g179: BSplineCurve PolesCount=2 KnotsCount=2 Degree=1 IsPeriodic=0
    g180: BSplineCurve PolesCount=4 KnotsCount=2 Degree=3 IsPeriodic=0
    g181: BSplineCurve PolesCount=4 KnotsCount=2 Degree=3 IsPeriodic=0
    g182: BSplineCurve PolesCount=4 KnotsCount=2 Degree=3 IsPeriodic=0
    g183: BSplineCurve PolesCount=4 KnotsCount=2 Degree=3 IsPeriodic=0
    g184: BSplineCurve PolesCount=4 KnotsCount=2 Degree=3 IsPeriodic=0
    g185: BSplineCurve PolesCount=2 KnotsCount=2 Degree=1 IsPeriodic=0
    g186: BSplineCurve PolesCount=2 KnotsCount=2 Degree=1 IsPeriodic=0
    g187: BSplineCurve PolesCount=4 KnotsCount=2 Degree=3 IsPeriodic=0
    g188: BSplineCurve PolesCount=4 KnotsCount=2 Degree=3 IsPeriodic=0
    g189: BSplineCurve PolesCount=4 KnotsCount=2 Degree=3 IsPeriodic=0
    g190: BSplineCurve PolesCount=4 KnotsCount=2 Degree=3 IsPeriodic=0
    g191: BSplineCurve PolesCount=4 KnotsCount=2 Degree=3 IsPeriodic=0
    g192: BSplineCurve PolesCount=4 KnotsCount=2 Degree=3 IsPeriodic=0
    g193: BSplineCurve PolesCount=4 KnotsCount=2 Degree=3 IsPeriodic=0
    g194: BSplineCurve PolesCount=2 KnotsCount=2 Degree=1 IsPeriodic=0
    g195: BSplineCurve PolesCount=2 KnotsCount=2 Degree=1 IsPeriodic=0
    g196: BSplineCurve PolesCount=2 KnotsCount=2 Degree=1 IsPeriodic=0
    g197: BSplineCurve PolesCount=4 KnotsCount=2 Degree=3 IsPeriodic=0
    g198: BSplineCurve PolesCount=4 KnotsCount=2 Degree=3 IsPeriodic=0
    g199: BSplineCurve PolesCount=4 KnotsCount=2 Degree=3 IsPeriodic=0
    g200: BSplineCurve PolesCount=4 KnotsCount=2 Degree=3 IsPeriodic=0
    g201: BSplineCurve PolesCount=4 KnotsCount=2 Degree=3 IsPeriodic=0
    g202: BSplineCurve PolesCount=4 KnotsCount=2 Degree=3 IsPeriodic=0
    g203: BSplineCurve PolesCount=4 KnotsCount=2 Degree=3 IsPeriodic=0
    g204: BSplineCurve PolesCount=4 KnotsCount=2 Degree=3 IsPeriodic=0
    g205: BSplineCurve PolesCount=2 KnotsCount=2 Degree=1 IsPeriodic=0
    g206: BSplineCurve PolesCount=2 KnotsCount=2 Degree=1 IsPeriodic=0
    g207: BSplineCurve PolesCount=4 KnotsCount=2 Degree=3 IsPeriodic=0
    g208: BSplineCurve PolesCount=4 KnotsCount=2 Degree=3 IsPeriodic=0
    g209: BSplineCurve PolesCount=4 KnotsCount=2 Degree=3 IsPeriodic=0
    g210: BSplineCurve PolesCount=4 KnotsCount=2 Degree=3 IsPeriodic=0
    g211: BSplineCurve PolesCount=4 KnotsCount=2 Degree=3 IsPeriodic=0
    g212: BSplineCurve PolesCount=4 KnotsCount=2 Degree=3 IsPeriodic=0
    g213: BSplineCurve PolesCount=4 KnotsCount=2 Degree=3 IsPeriodic=0
    g214: BSplineCurve PolesCount=2 KnotsCount=2 Degree=1 IsPeriodic=0
    g215: BSplineCurve PolesCount=2 KnotsCount=2 Degree=1 IsPeriodic=0
    g216: BSplineCurve PolesCount=4 KnotsCount=2 Degree=3 IsPeriodic=0
    g217: BSplineCurve PolesCount=4 KnotsCount=2 Degree=3 IsPeriodic=0
    g218: BSplineCurve PolesCount=4 KnotsCount=2 Degree=3 IsPeriodic=0
    g219: BSplineCurve PolesCount=4 KnotsCount=2 Degree=3 IsPeriodic=0
    g220: BSplineCurve PolesCount=4 KnotsCount=2 Degree=3 IsPeriodic=0
    g221: BSplineCurve PolesCount=4 KnotsCount=2 Degree=3 IsPeriodic=0
    g222: BSplineCurve PolesCount=4 KnotsCount=2 Degree=3 IsPeriodic=0
    g223: BSplineCurve PolesCount=4 KnotsCount=2 Degree=3 IsPeriodic=0
    g224: BSplineCurve PolesCount=2 KnotsCount=2 Degree=1 IsPeriodic=0
    g225: BSplineCurve PolesCount=2 KnotsCount=2 Degree=1 IsPeriodic=0
    g226: BSplineCurve PolesCount=4 KnotsCount=2 Degree=3 IsPeriodic=0
    g227: BSplineCurve PolesCount=4 KnotsCount=2 Degree=3 IsPeriodic=0
    g228: BSplineCurve PolesCount=4 KnotsCount=2 Degree=3 IsPeriodic=0
    g229: BSplineCurve PolesCount=2 KnotsCount=2 Degree=1 IsPeriodic=0
    g230: BSplineCurve PolesCount=2 KnotsCount=2 Degree=1 IsPeriodic=0
    g231: BSplineCurve PolesCount=4 KnotsCount=2 Degree=3 IsPeriodic=0
    g232: BSplineCurve PolesCount=4 KnotsCount=2 Degree=3 IsPeriodic=0
    g233: BSplineCurve PolesCount=4 KnotsCount=2 Degree=3 IsPeriodic=0
    g234: BSplineCurve PolesCount=4 KnotsCount=2 Degree=3 IsPeriodic=0
    g235: BSplineCurve PolesCount=2 KnotsCount=2 Degree=1 IsPeriodic=0
    g236: BSplineCurve PolesCount=2 KnotsCount=2 Degree=1 IsPeriodic=0
    g237: BSplineCurve PolesCount=4 KnotsCount=2 Degree=3 IsPeriodic=0
    g238: BSplineCurve PolesCount=4 KnotsCount=2 Degree=3 IsPeriodic=0
    g239: BSplineCurve PolesCount=4 KnotsCount=2 Degree=3 IsPeriodic=0
    g240: BSplineCurve PolesCount=4 KnotsCount=2 Degree=3 IsPeriodic=0
    g241: BSplineCurve PolesCount=2 KnotsCount=2 Degree=1 IsPeriodic=0
    g242: BSplineCurve PolesCount=2 KnotsCount=2 Degree=1 IsPeriodic=0
    g243: BSplineCurve PolesCount=4 KnotsCount=2 Degree=3 IsPeriodic=0
    g244: BSplineCurve PolesCount=4 KnotsCount=2 Degree=3 IsPeriodic=0
    g245: BSplineCurve PolesCount=4 KnotsCount=2 Degree=3 IsPeriodic=0
    g246: BSplineCurve PolesCount=4 KnotsCount=2 Degree=3 IsPeriodic=0
    g247: BSplineCurve PolesCount=4 KnotsCount=2 Degree=3 IsPeriodic=0
    g248: BSplineCurve PolesCount=2 KnotsCount=2 Degree=1 IsPeriodic=0
    g249: BSplineCurve PolesCount=4 KnotsCount=2 Degree=3 IsPeriodic=0
    g250: BSplineCurve PolesCount=4 KnotsCount=2 Degree=3 IsPeriodic=0
    g251: BSplineCurve PolesCount=2 KnotsCount=2 Degree=1 IsPeriodic=0
    g252: BSplineCurve PolesCount=2 KnotsCount=2 Degree=1 IsPeriodic=0
    g253: BSplineCurve PolesCount=2 KnotsCount=2 Degree=1 IsPeriodic=0
    g254: BSplineCurve PolesCount=2 KnotsCount=2 Degree=1 IsPeriodic=0
    g255: BSplineCurve PolesCount=4 KnotsCount=2 Degree=3 IsPeriodic=0
  constraints (260):
    c: Coincident(g0,g1)
    c: Coincident(g1,g2)
    c: Coincident(g2,g3)
    c: Coincident(g3,g4)
    c: Coincident(g4,g5)
    c: Coincident(g5,g6)
    c: Coincident(g6,g7)
    c: Coincident(g7,g8)
    c: Coincident(g8,g9)
    c: Coincident(g9,g10)
    c: Coincident(g10,g11)
    c: Coincident(g11,g12)
    c: Coincident(g12,g13)
    c: Coincident(g13,g14)
    c: Coincident(g14,g15)
    c: Coincident(g15,g16)
    c: Coincident(g16,g17)
    c: Coincident(g17,g18)
    c: Coincident(g18,g19)
    c: Coincident(g19,g20)
    c: Coincident(g20,g21)
    c: Coincident(g21,g22)
    c: Coincident(g22,g23)
    c: Coincident(g23,g24)
    c: Coincident(g24,g25)
    c: Coincident(g25,g26)
    c: Coincident(g26,g27)
    c: Coincident(g27,g28)
    c: Coincident(g28,g29)
    c: Coincident(g29,g30)
    c: Coincident(g30,g31)
    c: Coincident(g31,g0)
    c: Coincident(g32,g33)
    c: Coincident(g33,g34)
    c: Coincident(g34,g35)
    c: Coincident(g35,g36)
    c: Coincident(g36,g37)
    c: Coincident(g37,g38)
    c: Coincident(g38,g39)
    c: Coincident(g39,g32)
    c: Coincident(g40,g41)
    c: Coincident(g41,g42)
    c: Coincident(g42,g43)
    c: Coincident(g43,g44)
    c: Coincident(g44,g45)
    c: Coincident(g45,g46)
    c: Coincident(g46,g47)
    c: Coincident(g47,g48)
    c: Coincident(g48,g49)
    c: Coincident(g49,g40)
    c: Coincident(g50,g51)
    c: Coincident(g51,g52)
    c: Coincident(g52,g53)
    c: Coincident(g53,g54)
    c: Coincident(g54,g55)
    c: Coincident(g55,g56)
    c: Coincident(g56,g50)
    c: Coincident(g57,g58)
    c: Coincident(g58,g59)
    c: Coincident(g59,g60)
    c: Coincident(g60,g61)
    c: Coincident(g61,g62)
    c: Coincident(g62,g63)
    c: Coincident(g63,g64)
    c: Coincident(g64,g65)
    c: Coincident(g65,g66)
    c: Coincident(g66,g67)
    c: Coincident(g67,g68)
    c: Coincident(g68,g69)
    c: Coincident(g69,g70)
    c: Coincident(g70,g71)
    c: Coincident(g71,g72)
    c: Coincident(g72,g73)
    c: Coincident(g73,g74)
    c: Coincident(g74,g75)
    c: Coincident(g75,g76)
    c: Coincident(g76,g77)
    c: Coincident(g77,g78)
    c: Coincident(g78,g79)
    c: Coincident(g79,g80)
    c: Coincident(g80,g81)
    c: Coincident(g81,g82)
    c: Coincident(g82,g57)
    c: Coincident(g83,g84)
    c: Coincident(g84,g85)
    c: Coincident(g85,g86)
    c: Coincident(g86,g87)
    c: Coincident(g87,g83)
    c: Coincident(g88,g89)
    c: Coincident(g89,g90)
    c: Coincident(g90,g91)
    c: Coincident(g91,g92)
    c: Coincident(g92,g93)
    c: Coincident(g93,g94)
    c: Coincident(g94,g95)
    c: Coincident(g95,g96)
    c: Coincident(g96,g97)
    c: Coincident(g97,g98)
    c: Coincident(g98,g99)
    c: Coincident(g99,g100)
    c: Coincident(g100,g101)
    c: Coincident(g101,g102)
    c: Coincident(g102,g103)
    c: Coincident(g103,g104)
    c: Coincident(g104,g105)
    c: Coincident(g105,g106)
    c: Coincident(g106,g107)
    c: Coincident(g107,g108)
    c: Coincident(g108,g109)
    c: Coincident(g109,g110)
    c: Coincident(g110,g111)
    c: Coincident(g111,g112)
    c: Coincident(g112,g113)
    c: Coincident(g113,g114)
    c: Coincident(g114,g115)
    c: Coincident(g115,g116)
    c: Coincident(g116,g117)
    c: Coincident(g117,g118)
    c: Coincident(g118,g119)
    c: Coincident(g119,g120)
    c: Coincident(g120,g121)
    c: Coincident(g121,g122)
    c: Coincident(g122,g123)
    c: Coincident(g123,g124)
    c: Coincident(g124,g88)
    c: Coincident(g125,g126)
    c: Coincident(g126,g127)
    c: Coincident(g127,g128)
    c: Coincident(g128,g129)
    c: Coincident(g129,g125)
    c: Coincident(g130,g131)
    c: Coincident(g131,g132)
    c: Coincident(g132,g133)
    c: Coincident(g133,g134)
    c: Coincident(g134,g135)
    c: Coincident(g135,g136)
    c: Coincident(g136,g137)
    c: Coincident(g137,g138)
    c: Coincident(g138,g139)
    c: Coincident(g139,g140)
    c: Coincident(g140,g141)
    c: Coincident(g141,g142)
    c: Coincident(g142,g143)
    c: Coincident(g143,g144)
    c: Coincident(g144,g145)
    c: Coincident(g145,g146)
    c: Coincident(g146,g147)
    c: Coincident(g147,g148)
    c: Coincident(g148,g149)
    c: Coincident(g149,g150)
    c: Coincident(g150,g151)
    c: Coincident(g151,g152)
    c: Coincident(g152,g153)
    c: Coincident(g153,g154)
    c: Coincident(g154,g155)
    c: Coincident(g155,g156)
    c: Coincident(g156,g157)
    c: Coincident(g157,g158)
    c: Coincident(g158,g159)
    c: Coincident(g159,g160)
    c: Coincident(g160,g161)
    c: Coincident(g161,g162)
    c: Coincident(g162,g163)
    c: Coincident(g163,g164)
    c: Coincident(g164,g165)
    c: Coincident(g165,g166)
    c: Coincident(g166,g167)
    c: Coincident(g167,g168)
    c: Coincident(g168,g169)
    c: Coincident(g169,g170)
    c: Coincident(g170,g171)
    c: Coincident(g171,g172)
    c: Coincident(g172,g173)
    c: Coincident(g173,g130)
    c: Coincident(g174,g175)
    c: Coincident(g175,g176)
    c: Coincident(g176,g177)
    c: Coincident(g177,g178)
    c: Coincident(g178,g174)
    c: Coincident(g179,g180)
    c: Coincident(g180,g181)
    c: Coincident(g181,g182)
    c: Coincident(g182,g183)
    c: Coincident(g183,g184)
    c: Coincident(g184,g185)
    c: Coincident(g185,g186)
    c: Coincident(g186,g187)
    c: Coincident(g187,g188)
    c: Coincident(g188,g189)
    c: Coincident(g189,g190)
    c: Coincident(g190,g191)
    c: Coincident(g191,g192)
    c: Coincident(g192,g193)
    c: Coincident(g193,g179)
    c: Coincident(g194,g195)
    c: Coincident(g195,g196)
    c: Coincident(g196,g197)
    c: Coincident(g197,g198)
    c: Coincident(g198,g199)
    c: Coincident(g199,g194)
    c: Coincident(g200,g201)
    c: Coincident(g201,g202)
    c: Coincident(g202,g203)
    c: Coincident(g203,g204)
    c: Coincident(g204,g205)
    c: Coincident(g205,g206)
    c: Coincident(g206,g200)
    c: Coincident(g207,g208)
    c: Coincident(g208,g209)
    c: Coincident(g209,g210)
    c: Coincident(g210,g211)
    c: Coincident(g211,g207)
    c: Coincident(g212,g213)
    c: Coincident(g213,g214)
    c: Coincident(g214,g215)
    c: Coincident(g215,g216)
    c: Coincident(g216,g217)
    c: Coincident(g217,g212)
    c: Coincident(g218,g219)
    c: Coincident(g219,g220)
    c: Coincident(g220,g221)
    c: Coincident(g221,g222)
    c: Coincident(g222,g223)
    c: Coincident(g223,g224)
    c: Coincident(g224,g225)
    c: Coincident(g225,g226)
    c: Coincident(g226,g227)
    c: Coincident(g227,g228)
    c: Coincident(g228,g229)
    c: Coincident(g229,g230)
    c: Coincident(g230,g231)
    c: Coincident(g231,g232)
    c: Coincident(g232,g233)
    c: Coincident(g233,g234)
    c: Coincident(g234,g235)
    c: Coincident(g235,g236)
    c: Coincident(g236,g237)
    c: Coincident(g237,g238)
    c: Coincident(g238,g239)
    c: Coincident(g239,g240)
    c: Coincident(g240,g241)
    c: Coincident(g241,g242)
    c: Coincident(g242,g243)
    c: Coincident(g243,g244)
    c: Coincident(g244,g245)
    c: Coincident(g245,g246)
    c: Coincident(g246,g218)
    c: Coincident(g247,g248)
    c: Coincident(g248,g249)
    c: Coincident(g249,g250)
    c: Coincident(g250,g251)
    c: Coincident(g251,g252)
    c: Coincident(g252,g253)
    c: Coincident(g253,g254)
    c: Coincident(g254,g255)
    c: Coincident(g255,g247)
    c: Coincident(g194,g194)
    c: Coincident(g179,g179)
    c: Coincident(g57,g57)
    c: Coincident(g247,g248)
FEATURE [Sketcher::SketchObject] Sketch018  label="Spy-Sketch"
  ArcFitTolerance = 1e-06
  FullyConstrained = false
  MakeInternals = false
  sketch-geometry (151):
    g0: BSplineCurve PolesCount=4 KnotsCount=2 Degree=3 IsPeriodic=0
    g1: BSplineCurve PolesCount=4 KnotsCount=2 Degree=3 IsPeriodic=0
    g2: BSplineCurve PolesCount=4 KnotsCount=2 Degree=3 IsPeriodic=0
    g3: BSplineCurve PolesCount=2 KnotsCount=2 Degree=1 IsPeriodic=0
    g4: BSplineCurve PolesCount=2 KnotsCount=2 Degree=1 IsPeriodic=0
    g5: BSplineCurve PolesCount=4 KnotsCount=2 Degree=3 IsPeriodic=0
    g6: BSplineCurve PolesCount=4 KnotsCount=2 Degree=3 IsPeriodic=0
    g7: BSplineCurve PolesCount=4 KnotsCount=2 Degree=3 IsPeriodic=0
    g8: BSplineCurve PolesCount=4 KnotsCount=2 Degree=3 IsPeriodic=0
    g9: BSplineCurve PolesCount=4 KnotsCount=2 Degree=3 IsPeriodic=0
    g10: BSplineCurve PolesCount=4 KnotsCount=2 Degree=3 IsPeriodic=0
    g11: BSplineCurve PolesCount=4 KnotsCount=2 Degree=3 IsPeriodic=0
    g12: BSplineCurve PolesCount=4 KnotsCount=2 Degree=3 IsPeriodic=0
    g13: BSplineCurve PolesCount=4 KnotsCount=2 Degree=3 IsPeriodic=0
    g14: BSplineCurve PolesCount=4 KnotsCount=2 Degree=3 IsPeriodic=0
    g15: BSplineCurve PolesCount=4 KnotsCount=2 Degree=3 IsPeriodic=0
    g16: BSplineCurve PolesCount=2 KnotsCount=2 Degree=1 IsPeriodic=0
    g17: BSplineCurve PolesCount=2 KnotsCount=2 Degree=1 IsPeriodic=0
    g18: BSplineCurve PolesCount=2 KnotsCount=2 Degree=1 IsPeriodic=0
    g19: BSplineCurve PolesCount=2 KnotsCount=2 Degree=1 IsPeriodic=0
    g20: BSplineCurve PolesCount=2 KnotsCount=2 Degree=1 IsPeriodic=0
    g21: BSplineCurve PolesCount=2 KnotsCount=2 Degree=1 IsPeriodic=0
    g22: BSplineCurve PolesCount=4 KnotsCount=2 Degree=3 IsPeriodic=0
    g23: BSplineCurve PolesCount=4 KnotsCount=2 Degree=3 IsPeriodic=0
    g24: BSplineCurve PolesCount=4 KnotsCount=2 Degree=3 IsPeriodic=0
    g25: BSplineCurve PolesCount=4 KnotsCount=2 Degree=3 IsPeriodic=0
    g26: BSplineCurve PolesCount=4 KnotsCount=2 Degree=3 IsPeriodic=0
    g27: BSplineCurve PolesCount=4 KnotsCount=2 Degree=3 IsPeriodic=0
    g28: BSplineCurve PolesCount=2 KnotsCount=2 Degree=1 IsPeriodic=0
    g29: BSplineCurve PolesCount=2 KnotsCount=2 Degree=1 IsPeriodic=0
    g30: BSplineCurve PolesCount=4 KnotsCount=2 Degree=3 IsPeriodic=0
    g31: BSplineCurve PolesCount=4 KnotsCount=2 Degree=3 IsPeriodic=0
    g32: BSplineCurve PolesCount=4 KnotsCount=2 Degree=3 IsPeriodic=0
    g33: BSplineCurve PolesCount=4 KnotsCount=2 Degree=3 IsPeriodic=0
    g34: BSplineCurve PolesCount=4 KnotsCount=2 Degree=3 IsPeriodic=0
    g35: BSplineCurve PolesCount=4 KnotsCount=2 Degree=3 IsPeriodic=0
    g36: BSplineCurve PolesCount=4 KnotsCount=2 Degree=3 IsPeriodic=0
    g37: BSplineCurve PolesCount=4 KnotsCount=2 Degree=3 IsPeriodic=0
    g38: BSplineCurve PolesCount=4 KnotsCount=2 Degree=3 IsPeriodic=0
    g39: BSplineCurve PolesCount=4 KnotsCount=2 Degree=3 IsPeriodic=0
    g40: BSplineCurve PolesCount=2 KnotsCount=2 Degree=1 IsPeriodic=0
    g41: BSplineCurve PolesCount=2 KnotsCount=2 Degree=1 IsPeriodic=0
    g42: BSplineCurve PolesCount=4 KnotsCount=2 Degree=3 IsPeriodic=0
    g43: BSplineCurve PolesCount=2 KnotsCount=2 Degree=1 IsPeriodic=0
    g44: BSplineCurve PolesCount=2 KnotsCount=2 Degree=1 IsPeriodic=0
    g45: BSplineCurve PolesCount=2 KnotsCount=2 Degree=1 IsPeriodic=0
    g46: BSplineCurve PolesCount=2 KnotsCount=2 Degree=1 IsPeriodic=0
    g47: BSplineCurve PolesCount=4 KnotsCount=2 Degree=3 IsPeriodic=0
    g48: BSplineCurve PolesCount=4 KnotsCount=2 Degree=3 IsPeriodic=0
    g49: BSplineCurve PolesCount=4 KnotsCount=2 Degree=3 IsPeriodic=0
    g50: BSplineCurve PolesCount=4 KnotsCount=2 Degree=3 IsPeriodic=0
    g51: BSplineCurve PolesCount=4 KnotsCount=2 Degree=3 IsPeriodic=0
    g52: BSplineCurve PolesCount=4 KnotsCount=2 Degree=3 IsPeriodic=0
    g53: BSplineCurve PolesCount=4 KnotsCount=2 Degree=3 IsPeriodic=0
    g54: BSplineCurve PolesCount=4 KnotsCount=2 Degree=3 IsPeriodic=0
    g55: BSplineCurve PolesCount=4 KnotsCount=2 Degree=3 IsPeriodic=0
    g56: BSplineCurve PolesCount=2 KnotsCount=2 Degree=1 IsPeriodic=0
    g57: BSplineCurve PolesCount=4 KnotsCount=2 Degree=3 IsPeriodic=0
    g58: BSplineCurve PolesCount=4 KnotsCount=2 Degree=3 IsPeriodic=0
    g59: BSplineCurve PolesCount=4 KnotsCount=2 Degree=3 IsPeriodic=0
    g60: BSplineCurve PolesCount=4 KnotsCount=2 Degree=3 IsPeriodic=0
    g61: BSplineCurve PolesCount=4 KnotsCount=2 Degree=3 IsPeriodic=0
    g62: BSplineCurve PolesCount=4 KnotsCount=2 Degree=3 IsPeriodic=0
    g63: BSplineCurve PolesCount=4 KnotsCount=2 Degree=3 IsPeriodic=0
    g64: BSplineCurve PolesCount=4 KnotsCount=2 Degree=3 IsPeriodic=0
    g65: BSplineCurve PolesCount=4 KnotsCount=2 Degree=3 IsPeriodic=0
    g66: BSplineCurve PolesCount=2 KnotsCount=2 Degree=1 IsPeriodic=0
    g67: BSplineCurve PolesCount=2 KnotsCount=2 Degree=1 IsPeriodic=0
    g68: BSplineCurve PolesCount=4 KnotsCount=2 Degree=3 IsPeriodic=0
    g69: BSplineCurve PolesCount=2 KnotsCount=2 Degree=1 IsPeriodic=0
    g70: BSplineCurve PolesCount=2 KnotsCount=2 Degree=1 IsPeriodic=0
    g71: BSplineCurve PolesCount=4 KnotsCount=2 Degree=3 IsPeriodic=0
    g72: BSplineCurve PolesCount=4 KnotsCount=2 Degree=3 IsPeriodic=0
    g73: BSplineCurve PolesCount=4 KnotsCount=2 Degree=3 IsPeriodic=0
    g74: BSplineCurve PolesCount=4 KnotsCount=2 Degree=3 IsPeriodic=0
    g75: BSplineCurve PolesCount=4 KnotsCount=2 Degree=3 IsPeriodic=0
    g76: BSplineCurve PolesCount=4 KnotsCount=2 Degree=3 IsPeriodic=0
    g77: BSplineCurve PolesCount=4 KnotsCount=2 Degree=3 IsPeriodic=0
    g78: BSplineCurve PolesCount=4 KnotsCount=2 Degree=3 IsPeriodic=0
    g79: BSplineCurve PolesCount=4 KnotsCount=2 Degree=3 IsPeriodic=0
    g80: BSplineCurve PolesCount=4 KnotsCount=2 Degree=3 IsPeriodic=0
    g81: BSplineCurve PolesCount=4 KnotsCount=2 Degree=3 IsPeriodic=0
    g82: BSplineCurve PolesCount=4 KnotsCount=2 Degree=3 IsPeriodic=0
    g83: BSplineCurve PolesCount=4 KnotsCount=2 Degree=3 IsPeriodic=0
    g84: BSplineCurve PolesCount=4 KnotsCount=2 Degree=3 IsPeriodic=0
    g85: BSplineCurve PolesCount=2 KnotsCount=2 Degree=1 IsPeriodic=0
    g86: BSplineCurve PolesCount=2 KnotsCount=2 Degree=1 IsPeriodic=0
    g87: BSplineCurve PolesCount=4 KnotsCount=2 Degree=3 IsPeriodic=0
    g88: BSplineCurve PolesCount=4 KnotsCount=2 Degree=3 IsPeriodic=0
    g89: BSplineCurve PolesCount=4 KnotsCount=2 Degree=3 IsPeriodic=0
    g90: BSplineCurve PolesCount=4 KnotsCount=2 Degree=3 IsPeriodic=0
    g91: BSplineCurve PolesCount=4 KnotsCount=2 Degree=3 IsPeriodic=0
    g92: BSplineCurve PolesCount=4 KnotsCount=2 Degree=3 IsPeriodic=0
    g93: BSplineCurve PolesCount=4 KnotsCount=2 Degree=3 IsPeriodic=0
    g94: BSplineCurve PolesCount=4 KnotsCount=2 Degree=3 IsPeriodic=0
    g95: BSplineCurve PolesCount=4 KnotsCount=2 Degree=3 IsPeriodic=0
    g96: BSplineCurve PolesCount=4 KnotsCount=2 Degree=3 IsPeriodic=0
    g97: BSplineCurve PolesCount=4 KnotsCount=2 Degree=3 IsPeriodic=0
    g98: BSplineCurve PolesCount=4 KnotsCount=2 Degree=3 IsPeriodic=0
    g99: BSplineCurve PolesCount=4 KnotsCount=2 Degree=3 IsPeriodic=0
    g100: BSplineCurve PolesCount=4 KnotsCount=2 Degree=3 IsPeriodic=0
    g101: BSplineCurve PolesCount=4 KnotsCount=2 Degree=3 IsPeriodic=0
    g102: BSplineCurve PolesCount=4 KnotsCount=2 Degree=3 IsPeriodic=0
    g103: BSplineCurve PolesCount=4 KnotsCount=2 Degree=3 IsPeriodic=0
    g104: BSplineCurve PolesCount=4 KnotsCount=2 Degree=3 IsPeriodic=0
    g105: BSplineCurve PolesCount=4 KnotsCount=2 Degree=3 IsPeriodic=0
    g106: BSplineCurve PolesCount=2 KnotsCount=2 Degree=1 IsPeriodic=0
    g107: BSplineCurve PolesCount=2 KnotsCount=2 Degree=1 IsPeriodic=0
    g108: BSplineCurve PolesCount=4 KnotsCount=2 Degree=3 IsPeriodic=0
    g109: BSplineCurve PolesCount=4 KnotsCount=2 Degree=3 IsPeriodic=0
    g110: BSplineCurve PolesCount=4 KnotsCount=2 Degree=3 IsPeriodic=0
    g111: BSplineCurve PolesCount=4 KnotsCount=2 Degree=3 IsPeriodic=0
    g112: BSplineCurve PolesCount=4 KnotsCount=2 Degree=3 IsPeriodic=0
    g113: BSplineCurve PolesCount=4 KnotsCount=2 Degree=3 IsPeriodic=0
    g114: BSplineCurve PolesCount=4 KnotsCount=2 Degree=3 IsPeriodic=0
    g115: BSplineCurve PolesCount=2 KnotsCount=2 Degree=1 IsPeriodic=0
    g116: BSplineCurve PolesCount=2 KnotsCount=2 Degree=1 IsPeriodic=0
    g117: BSplineCurve PolesCount=4 KnotsCount=2 Degree=3 IsPeriodic=0
    g118: BSplineCurve PolesCount=2 KnotsCount=2 Degree=1 IsPeriodic=0
    g119: BSplineCurve PolesCount=2 KnotsCount=2 Degree=1 IsPeriodic=0
    g120: BSplineCurve PolesCount=4 KnotsCount=2 Degree=3 IsPeriodic=0
    g121: BSplineCurve PolesCount=2 KnotsCount=2 Degree=1 IsPeriodic=0
    g122: BSplineCurve PolesCount=2 KnotsCount=2 Degree=1 IsPeriodic=0
    g123: BSplineCurve PolesCount=4 KnotsCount=2 Degree=3 IsPeriodic=0
    g124: BSplineCurve PolesCount=4 KnotsCount=2 Degree=3 IsPeriodic=0
    g125: BSplineCurve PolesCount=4 KnotsCount=2 Degree=3 IsPeriodic=0
    g126: BSplineCurve PolesCount=4 KnotsCount=2 Degree=3 IsPeriodic=0
    g127: BSplineCurve PolesCount=4 KnotsCount=2 Degree=3 IsPeriodic=0
    g128: BSplineCurve PolesCount=4 KnotsCount=2 Degree=3 IsPeriodic=0
    g129: BSplineCurve PolesCount=4 KnotsCount=2 Degree=3 IsPeriodic=0
    g130: BSplineCurve PolesCount=4 KnotsCount=2 Degree=3 IsPeriodic=0
    g131: BSplineCurve PolesCount=4 KnotsCount=2 Degree=3 IsPeriodic=0
    g132: BSplineCurve PolesCount=4 KnotsCount=2 Degree=3 IsPeriodic=0
    g133: BSplineCurve PolesCount=4 KnotsCount=2 Degree=3 IsPeriodic=0
    g134: BSplineCurve PolesCount=4 KnotsCount=2 Degree=3 IsPeriodic=0
    g135: BSplineCurve PolesCount=4 KnotsCount=2 Degree=3 IsPeriodic=0
    g136: BSplineCurve PolesCount=4 KnotsCount=2 Degree=3 IsPeriodic=0
    g137: BSplineCurve PolesCount=4 KnotsCount=2 Degree=3 IsPeriodic=0
    g138: BSplineCurve PolesCount=4 KnotsCount=2 Degree=3 IsPeriodic=0
    g139: BSplineCurve PolesCount=4 KnotsCount=2 Degree=3 IsPeriodic=0
    g140: BSplineCurve PolesCount=4 KnotsCount=2 Degree=3 IsPeriodic=0
    g141: BSplineCurve PolesCount=4 KnotsCount=2 Degree=3 IsPeriodic=0
    g142: BSplineCurve PolesCount=4 KnotsCount=2 Degree=3 IsPeriodic=0
    g143: BSplineCurve PolesCount=4 KnotsCount=2 Degree=3 IsPeriodic=0
    g144: BSplineCurve PolesCount=4 KnotsCount=2 Degree=3 IsPeriodic=0
    g145: BSplineCurve PolesCount=2 KnotsCount=2 Degree=1 IsPeriodic=0
    g146: BSplineCurve PolesCount=2 KnotsCount=2 Degree=1 IsPeriodic=0
    g147: BSplineCurve PolesCount=4 KnotsCount=2 Degree=3 IsPeriodic=0
    g148: BSplineCurve PolesCount=4 KnotsCount=2 Degree=3 IsPeriodic=0
    g149: BSplineCurve PolesCount=4 KnotsCount=2 Degree=3 IsPeriodic=0
    g150: BSplineCurve PolesCount=4 KnotsCount=2 Degree=3 IsPeriodic=0
  constraints (152):
    c: Coincident(g0,g1)
    c: Coincident(g1,g2)
    c: Coincident(g2,g3)
    c: Coincident(g3,g4)
    c: Coincident(g4,g5)
    c: Coincident(g5,g6)
    c: Coincident(g6,g7)
    c: Coincident(g7,g8)
    c: Coincident(g8,g9)
    c: Coincident(g9,g10)
    c: Coincident(g10,g11)
    c: Coincident(g11,g12)
    c: Coincident(g12,g13)
    c: Coincident(g13,g14)
    c: Coincident(g14,g15)
    c: Coincident(g15,g16)
    c: Coincident(g16,g17)
    c: Coincident(g17,g18)
    c: Coincident(g18,g19)
    c: Coincident(g19,g20)
    c: Coincident(g20,g21)
    c: Coincident(g21,g22)
    c: Coincident(g22,g23)
    c: Coincident(g23,g24)
    c: Coincident(g24,g25)
    c: Coincident(g25,g26)
    c: Coincident(g26,g27)
    c: Coincident(g27,g28)
    c: Coincident(g28,g29)
    c: Coincident(g29,g30)
    c: Coincident(g30,g31)
    c: Coincident(g31,g0)
    c: Coincident(g32,g33)
    c: Coincident(g33,g34)
    c: Coincident(g34,g35)
    c: Coincident(g35,g36)
    c: Coincident(g36,g37)
    c: Coincident(g37,g38)
    c: Coincident(g38,g39)
    c: Coincident(g39,g40)
    c: Coincident(g40,g41)
    c: Coincident(g41,g42)
    c: Coincident(g42,g43)
    c: Coincident(g43,g44)
    c: Coincident(g44,g45)
    c: Coincident(g45,g46)
    c: Coincident(g46,g47)
    c: Coincident(g47,g48)
    c: Coincident(g48,g49)
    c: Coincident(g49,g50)
    c: Coincident(g50,g51)
    c: Coincident(g51,g32)
    c: Coincident(g52,g53)
    c: Coincident(g53,g54)
    c: Coincident(g54,g55)
    c: Coincident(g55,g52)
    c: Coincident(g56,g57)
    c: Coincident(g57,g58)
    c: Coincident(g58,g59)
    c: Coincident(g59,g60)
    c: Coincident(g60,g61)
    c: Coincident(g61,g62)
    c: Coincident(g62,g63)
    c: Coincident(g63,g64)
    c: Coincident(g64,g65)
    c: Coincident(g65,g66)
    c: Coincident(g66,g67)
    c: Coincident(g67,g68)
    c: Coincident(g68,g69)
    c: Coincident(g69,g70)
    c: Coincident(g70,g71)
    c: Coincident(g71,g72)
    c: Coincident(g72,g73)
    c: Coincident(g73,g74)
    c: Coincident(g74,g75)
    c: Coincident(g75,g76)
    c: Coincident(g76,g77)
    c: Coincident(g77,g78)
    c: Coincident(g78,g79)
    c: Coincident(g79,g80)
    c: Coincident(g80,g81)
    c: Coincident(g81,g82)
    c: Coincident(g82,g83)
    c: Coincident(g83,g84)
    c: Coincident(g84,g85)
    c: Coincident(g85,g86)
    c: Coincident(g86,g87)
    c: Coincident(g87,g88)
    c: Coincident(g88,g89)
    c: Coincident(g89,g90)
    c: Coincident(g90,g91)
    c: Coincident(g91,g92)
    c: Coincident(g92,g93)
    c: Coincident(g93,g94)
    c: Coincident(g94,g95)
    c: Coincident(g95,g96)
    c: Coincident(g96,g97)
    c: Coincident(g97,g98)
    c: Coincident(g98,g99)
    c: Coincident(g99,g100)
    c: Coincident(g100,g101)
    c: Coincident(g101,g56)
    c: Coincident(g102,g103)
    c: Coincident(g103,g104)
    c: Coincident(g104,g105)
    c: Coincident(g105,g102)
    c: Coincident(g106,g107)
    c: Coincident(g107,g108)
    c: Coincident(g108,g109)
    c: Coincident(g109,g110)
    c: Coincident(g110,g111)
    c: Coincident(g111,g112)
    c: Coincident(g112,g113)
    c: Coincident(g113,g114)
    c: Coincident(g114,g115)
    c: Coincident(g115,g116)
    c: Coincident(g116,g117)
    c: Coincident(g117,g118)
    c: Coincident(g118,g119)
    c: Coincident(g119,g120)
    c: Coincident(g120,g121)
    c: Coincident(g121,g122)
    c: Coincident(g122,g123)
    c: Coincident(g123,g106)
    c: Coincident(g124,g125)
    c: Coincident(g125,g126)
    c: Coincident(g126,g127)
    c: Coincident(g127,g128)
    c: Coincident(g128,g124)
    c: Coincident(g129,g130)
    c: Coincident(g130,g131)
    c: Coincident(g131,g132)
    c: Coincident(g132,g133)
    c: Coincident(g133,g129)
    c: Coincident(g134,g135)
    c: Coincident(g135,g136)
    c: Coincident(g136,g134)
    c: Coincident(g137,g138)
    c: Coincident(g138,g139)
    c: Coincident(g139,g140)
    c: Coincident(g140,g137)
    c: Coincident(g141,g142)
    c: Coincident(g142,g143)
    c: Coincident(g143,g144)
    c: Coincident(g144,g145)
    c: Coincident(g145,g146)
    c: Coincident(g146,g141)
    c: Coincident(g147,g148)
    c: Coincident(g148,g149)
    c: Coincident(g149,g150)
    c: Coincident(g150,g147)
    c: Coincident(g56,g56)
FEATURE [Sketcher::SketchObject] Sketch019  label="Undertaker-Sketch"
  ArcFitTolerance = 1e-06
  FullyConstrained = false
  MakeInternals = false
  sketch-geometry (89):
    g0: BSplineCurve PolesCount=4 KnotsCount=2 Degree=3 IsPeriodic=0
    g1: BSplineCurve PolesCount=4 KnotsCount=2 Degree=3 IsPeriodic=0
    g2: BSplineCurve PolesCount=4 KnotsCount=2 Degree=3 IsPeriodic=0
    g3: BSplineCurve PolesCount=4 KnotsCount=2 Degree=3 IsPeriodic=0
    g4: BSplineCurve PolesCount=4 KnotsCount=2 Degree=3 IsPeriodic=0
    g5: BSplineCurve PolesCount=4 KnotsCount=2 Degree=3 IsPeriodic=0
    g6: BSplineCurve PolesCount=4 KnotsCount=2 Degree=3 IsPeriodic=0
    g7: BSplineCurve PolesCount=4 KnotsCount=2 Degree=3 IsPeriodic=0
    g8: BSplineCurve PolesCount=4 KnotsCount=2 Degree=3 IsPeriodic=0
    g9: BSplineCurve PolesCount=4 KnotsCount=2 Degree=3 IsPeriodic=0
    g10: BSplineCurve PolesCount=4 KnotsCount=2 Degree=3 IsPeriodic=0
    g11: BSplineCurve PolesCount=4 KnotsCount=2 Degree=3 IsPeriodic=0
    g12: BSplineCurve PolesCount=4 KnotsCount=2 Degree=3 IsPeriodic=0
    g13: BSplineCurve PolesCount=2 KnotsCount=2 Degree=1 IsPeriodic=0
    g14: BSplineCurve PolesCount=2 KnotsCount=2 Degree=1 IsPeriodic=0
    g15: BSplineCurve PolesCount=4 KnotsCount=2 Degree=3 IsPeriodic=0
    g16: BSplineCurve PolesCount=4 KnotsCount=2 Degree=3 IsPeriodic=0
    g17: BSplineCurve PolesCount=2 KnotsCount=2 Degree=1 IsPeriodic=0
    g18: BSplineCurve PolesCount=2 KnotsCount=2 Degree=1 IsPeriodic=0
    g19: BSplineCurve PolesCount=4 KnotsCount=2 Degree=3 IsPeriodic=0
    g20: BSplineCurve PolesCount=4 KnotsCount=2 Degree=3 IsPeriodic=0
    g21: BSplineCurve PolesCount=4 KnotsCount=2 Degree=3 IsPeriodic=0
    g22: BSplineCurve PolesCount=4 KnotsCount=2 Degree=3 IsPeriodic=0
    g23: BSplineCurve PolesCount=4 KnotsCount=2 Degree=3 IsPeriodic=0
    g24: BSplineCurve PolesCount=4 KnotsCount=2 Degree=3 IsPeriodic=0
    g25: BSplineCurve PolesCount=4 KnotsCount=2 Degree=3 IsPeriodic=0
    g26: BSplineCurve PolesCount=4 KnotsCount=2 Degree=3 IsPeriodic=0
    g27: BSplineCurve PolesCount=4 KnotsCount=2 Degree=3 IsPeriodic=0
    g28: BSplineCurve PolesCount=4 KnotsCount=2 Degree=3 IsPeriodic=0
    g29: BSplineCurve PolesCount=2 KnotsCount=2 Degree=1 IsPeriodic=0
    g30: BSplineCurve PolesCount=4 KnotsCount=2 Degree=3 IsPeriodic=0
    g31: BSplineCurve PolesCount=4 KnotsCount=2 Degree=3 IsPeriodic=0
    g32: BSplineCurve PolesCount=4 KnotsCount=2 Degree=3 IsPeriodic=0
    g33: BSplineCurve PolesCount=4 KnotsCount=2 Degree=3 IsPeriodic=0
    g34: BSplineCurve PolesCount=4 KnotsCount=2 Degree=3 IsPeriodic=0
    g35: BSplineCurve PolesCount=2 KnotsCount=2 Degree=1 IsPeriodic=0
    g36: BSplineCurve PolesCount=4 KnotsCount=2 Degree=3 IsPeriodic=0
    g37: BSplineCurve PolesCount=4 KnotsCount=2 Degree=3 IsPeriodic=0
    g38: BSplineCurve PolesCount=4 KnotsCount=2 Degree=3 IsPeriodic=0
    g39: BSplineCurve PolesCount=4 KnotsCount=2 Degree=3 IsPeriodic=0
    g40: BSplineCurve PolesCount=4 KnotsCount=2 Degree=3 IsPeriodic=0
    g41: BSplineCurve PolesCount=2 KnotsCount=2 Degree=1 IsPeriodic=0
    g42: BSplineCurve PolesCount=2 KnotsCount=2 Degree=1 IsPeriodic=0
    g43: BSplineCurve PolesCount=4 KnotsCount=2 Degree=3 IsPeriodic=0
    g44: BSplineCurve PolesCount=4 KnotsCount=2 Degree=3 IsPeriodic=0
    g45: BSplineCurve PolesCount=4 KnotsCount=2 Degree=3 IsPeriodic=0
    g46: BSplineCurve PolesCount=4 KnotsCount=2 Degree=3 IsPeriodic=0
    g47: BSplineCurve PolesCount=4 KnotsCount=2 Degree=3 IsPeriodic=0
    g48: BSplineCurve PolesCount=4 KnotsCount=2 Degree=3 IsPeriodic=0
    g49: BSplineCurve PolesCount=4 KnotsCount=2 Degree=3 IsPeriodic=0
    g50: BSplineCurve PolesCount=4 KnotsCount=2 Degree=3 IsPeriodic=0
    g51: BSplineCurve PolesCount=4 KnotsCount=2 Degree=3 IsPeriodic=0
    g52: BSplineCurve PolesCount=4 KnotsCount=2 Degree=3 IsPeriodic=0
    g53: BSplineCurve PolesCount=4 KnotsCount=2 Degree=3 IsPeriodic=0
    g54: BSplineCurve PolesCount=4 KnotsCount=2 Degree=3 IsPeriodic=0
    g55: BSplineCurve PolesCount=2 KnotsCount=2 Degree=1 IsPeriodic=0
    g56: BSplineCurve PolesCount=2 KnotsCount=2 Degree=1 IsPeriodic=0
    g57: BSplineCurve PolesCount=4 KnotsCount=2 Degree=3 IsPeriodic=0
    g58: BSplineCurve PolesCount=4 KnotsCount=2 Degree=3 IsPeriodic=0
    g59: BSplineCurve PolesCount=4 KnotsCount=2 Degree=3 IsPeriodic=0
    g60: BSplineCurve PolesCount=2 KnotsCount=2 Degree=1 IsPeriodic=0
    g61: BSplineCurve PolesCount=2 KnotsCount=2 Degree=1 IsPeriodic=0
    g62: BSplineCurve PolesCount=4 KnotsCount=2 Degree=3 IsPeriodic=0
    g63: BSplineCurve PolesCount=4 KnotsCount=2 Degree=3 IsPeriodic=0
    g64: BSplineCurve PolesCount=4 KnotsCount=2 Degree=3 IsPeriodic=0
    g65: BSplineCurve PolesCount=4 KnotsCount=2 Degree=3 IsPeriodic=0
    g66: BSplineCurve PolesCount=4 KnotsCount=2 Degree=3 IsPeriodic=0
    g67: BSplineCurve PolesCount=4 KnotsCount=2 Degree=3 IsPeriodic=0
    g68: BSplineCurve PolesCount=4 KnotsCount=2 Degree=3 IsPeriodic=0
    g69: BSplineCurve PolesCount=4 KnotsCount=2 Degree=3 IsPeriodic=0
    g70: BSplineCurve PolesCount=4 KnotsCount=2 Degree=3 IsPeriodic=0
    g71: BSplineCurve PolesCount=4 KnotsCount=2 Degree=3 IsPeriodic=0
    g72: BSplineCurve PolesCount=4 KnotsCount=2 Degree=3 IsPeriodic=0
    g73: BSplineCurve PolesCount=4 KnotsCount=2 Degree=3 IsPeriodic=0
    g74: BSplineCurve PolesCount=4 KnotsCount=2 Degree=3 IsPeriodic=0
    g75: BSplineCurve PolesCount=4 KnotsCount=2 Degree=3 IsPeriodic=0
    g76: BSplineCurve PolesCount=4 KnotsCount=2 Degree=3 IsPeriodic=0
    g77: BSplineCurve PolesCount=4 KnotsCount=2 Degree=3 IsPeriodic=0
    g78: BSplineCurve PolesCount=4 KnotsCount=2 Degree=3 IsPeriodic=0
    g79: BSplineCurve PolesCount=4 KnotsCount=2 Degree=3 IsPeriodic=0
    g80: BSplineCurve PolesCount=2 KnotsCount=2 Degree=1 IsPeriodic=0
    g81: BSplineCurve PolesCount=4 KnotsCount=2 Degree=3 IsPeriodic=0
    g82: BSplineCurve PolesCount=2 KnotsCount=2 Degree=1 IsPeriodic=0
    g83: BSplineCurve PolesCount=2 KnotsCount=2 Degree=1 IsPeriodic=0
    g84: BSplineCurve PolesCount=4 KnotsCount=2 Degree=3 IsPeriodic=0
    g85: BSplineCurve PolesCount=4 KnotsCount=2 Degree=3 IsPeriodic=0
    g86: BSplineCurve PolesCount=4 KnotsCount=2 Degree=3 IsPeriodic=0
    g87: BSplineCurve PolesCount=4 KnotsCount=2 Degree=3 IsPeriodic=0
    g88: BSplineCurve PolesCount=4 KnotsCount=2 Degree=3 IsPeriodic=0
  constraints (92):
    c: Coincident(g0,g1)
    c: Coincident(g1,g2)
    c: Coincident(g2,g3)
    c: Coincident(g3,g4)
    c: Coincident(g4,g5)
    c: Coincident(g5,g6)
    c: Coincident(g6,g7)
    c: Coincident(g7,g8)
    c: Coincident(g8,g9)
    c: Coincident(g9,g10)
    c: Coincident(g10,g11)
    c: Coincident(g11,g12)
    c: Coincident(g12,g13)
    c: Coincident(g13,g14)
    c: Coincident(g14,g15)
    c: Coincident(g15,g16)
    c: Coincident(g16,g17)
    c: Coincident(g17,g18)
    c: Coincident(g18,g19)
    c: Coincident(g19,g20)
    c: Coincident(g20,g21)
    c: Coincident(g21,g22)
    c: Coincident(g22,g23)
    c: Coincident(g23,g24)
    c: Coincident(g24,g25)
    c: Coincident(g25,g26)
    c: Coincident(g26,g27)
    c: Coincident(g27,g28)
    c: Coincident(g28,g29)
    c: Coincident(g29,g0)
    c: Coincident(g30,g31)
    c: Coincident(g31,g32)
    c: Coincident(g32,g33)
    c: Coincident(g33,g34)
    c: Coincident(g34,g30)
    c: Coincident(g35,g36)
    c: Coincident(g36,g37)
    c: Coincident(g37,g38)
    c: Coincident(g38,g39)
    c: Coincident(g39,g40)
    c: Coincident(g40,g41)
    c: Coincident(g41,g42)
    c: Coincident(g42,g43)
    c: Coincident(g43,g44)
    c: Coincident(g44,g45)
    c: Coincident(g45,g46)
    c: Coincident(g46,g47)
    c: Coincident(g47,g48)
    c: Coincident(g48,g35)
    c: Coincident(g49,g50)
    c: Coincident(g50,g51)
    c: Coincident(g51,g49)
    c: Coincident(g52,g53)
    c: Coincident(g53,g54)
    c: Coincident(g54,g55)
    c: Coincident(g55,g56)
    c: Coincident(g56,g57)
    c: Coincident(g57,g58)
    c: Coincident(g58,g59)
    c: Coincident(g59,g60)
    c: Coincident(g60,g61)
    c: Coincident(g61,g62)
    c: Coincident(g62,g63)
    c: Coincident(g63,g64)
    c: Coincident(g64,g52)
    c: Coincident(g65,g66)
    c: Coincident(g66,g67)
    c: Coincident(g67,g68)
    c: Coincident(g68,g69)
    c: Coincident(g69,g65)
    c: Coincident(g70,g71)
    c: Coincident(g71,g72)
    c: Coincident(g72,g73)
    c: Coincident(g73,g70)
    c: Coincident(g74,g75)
    c: Coincident(g75,g76)
    c: Coincident(g76,g74)
    c: Coincident(g77,g78)
    c: Coincident(g78,g79)
    c: Coincident(g79,g77)
    c: Coincident(g80,g81)
    c: Coincident(g81,g82)
    c: Coincident(g82,g83)
    c: Coincident(g83,g84)
    c: Coincident(g84,g80)
    c: Coincident(g85,g86)
    c: Coincident(g86,g87)
    c: Coincident(g87,g88)
    c: Coincident(g88,g85)
    c: Coincident(g28,g0)
    c: Coincident(g35,g35)
    c: Coincident(g80,g80)
FEATURE [Sketcher::SketchObject] Sketch020  label="Virgin-Sketch"
  ArcFitTolerance = 1e-06
  FullyConstrained = false
  MakeInternals = false
  sketch-geometry (180):
    g0: BSplineCurve PolesCount=4 KnotsCount=2 Degree=3 IsPeriodic=0
    g1: BSplineCurve PolesCount=4 KnotsCount=2 Degree=3 IsPeriodic=0
    g2: BSplineCurve PolesCount=2 KnotsCount=2 Degree=1 IsPeriodic=0
    g3: BSplineCurve PolesCount=2 KnotsCount=2 Degree=1 IsPeriodic=0
    g4: BSplineCurve PolesCount=4 KnotsCount=2 Degree=3 IsPeriodic=0
    g5: BSplineCurve PolesCount=4 KnotsCount=2 Degree=3 IsPeriodic=0
    g6: BSplineCurve PolesCount=4 KnotsCount=2 Degree=3 IsPeriodic=0
    g7: BSplineCurve PolesCount=2 KnotsCount=2 Degree=1 IsPeriodic=0
    g8: BSplineCurve PolesCount=2 KnotsCount=2 Degree=1 IsPeriodic=0
    g9: BSplineCurve PolesCount=4 KnotsCount=2 Degree=3 IsPeriodic=0
    g10: BSplineCurve PolesCount=4 KnotsCount=2 Degree=3 IsPeriodic=0
    g11: BSplineCurve PolesCount=4 KnotsCount=2 Degree=3 IsPeriodic=0
    g12: BSplineCurve PolesCount=4 KnotsCount=2 Degree=3 IsPeriodic=0
    g13: BSplineCurve PolesCount=4 KnotsCount=2 Degree=3 IsPeriodic=0
    g14: BSplineCurve PolesCount=4 KnotsCount=2 Degree=3 IsPeriodic=0
    g15: BSplineCurve PolesCount=4 KnotsCount=2 Degree=3 IsPeriodic=0
    g16: BSplineCurve PolesCount=4 KnotsCount=2 Degree=3 IsPeriodic=0
    g17: BSplineCurve PolesCount=4 KnotsCount=2 Degree=3 IsPeriodic=0
    g18: BSplineCurve PolesCount=4 KnotsCount=2 Degree=3 IsPeriodic=0
    g19: BSplineCurve PolesCount=4 KnotsCount=2 Degree=3 IsPeriodic=0
    g20: BSplineCurve PolesCount=2 KnotsCount=2 Degree=1 IsPeriodic=0
    g21: BSplineCurve PolesCount=2 KnotsCount=2 Degree=1 IsPeriodic=0
    g22: BSplineCurve PolesCount=4 KnotsCount=2 Degree=3 IsPeriodic=0
    g23: BSplineCurve PolesCount=2 KnotsCount=2 Degree=1 IsPeriodic=0
    g24: BSplineCurve PolesCount=2 KnotsCount=2 Degree=1 IsPeriodic=0
    g25: BSplineCurve PolesCount=4 KnotsCount=2 Degree=3 IsPeriodic=0
    g26: BSplineCurve PolesCount=4 KnotsCount=2 Degree=3 IsPeriodic=0
    g27: BSplineCurve PolesCount=4 KnotsCount=2 Degree=3 IsPeriodic=0
    g28: BSplineCurve PolesCount=4 KnotsCount=2 Degree=3 IsPeriodic=0
    g29: BSplineCurve PolesCount=4 KnotsCount=2 Degree=3 IsPeriodic=0
    g30: BSplineCurve PolesCount=4 KnotsCount=2 Degree=3 IsPeriodic=0
    g31: BSplineCurve PolesCount=4 KnotsCount=2 Degree=3 IsPeriodic=0
    g32: BSplineCurve PolesCount=4 KnotsCount=2 Degree=3 IsPeriodic=0
    g33: BSplineCurve PolesCount=4 KnotsCount=2 Degree=3 IsPeriodic=0
    g34: BSplineCurve PolesCount=4 KnotsCount=2 Degree=3 IsPeriodic=0
    g35: BSplineCurve PolesCount=4 KnotsCount=2 Degree=3 IsPeriodic=0
    g36: BSplineCurve PolesCount=4 KnotsCount=2 Degree=3 IsPeriodic=0
    g37: BSplineCurve PolesCount=4 KnotsCount=2 Degree=3 IsPeriodic=0
    g38: BSplineCurve PolesCount=4 KnotsCount=2 Degree=3 IsPeriodic=0
    g39: BSplineCurve PolesCount=4 KnotsCount=2 Degree=3 IsPeriodic=0
    g40: BSplineCurve PolesCount=4 KnotsCount=2 Degree=3 IsPeriodic=0
    g41: BSplineCurve PolesCount=4 KnotsCount=2 Degree=3 IsPeriodic=0
    g42: BSplineCurve PolesCount=4 KnotsCount=2 Degree=3 IsPeriodic=0
    g43: BSplineCurve PolesCount=4 KnotsCount=2 Degree=3 IsPeriodic=0
    g44: BSplineCurve PolesCount=4 KnotsCount=2 Degree=3 IsPeriodic=0
    g45: BSplineCurve PolesCount=4 KnotsCount=2 Degree=3 IsPeriodic=0
    g46: BSplineCurve PolesCount=4 KnotsCount=2 Degree=3 IsPeriodic=0
    g47: BSplineCurve PolesCount=4 KnotsCount=2 Degree=3 IsPeriodic=0
    g48: BSplineCurve PolesCount=2 KnotsCount=2 Degree=1 IsPeriodic=0
    g49: BSplineCurve PolesCount=4 KnotsCount=2 Degree=3 IsPeriodic=0
    g50: BSplineCurve PolesCount=4 KnotsCount=2 Degree=3 IsPeriodic=0
    g51: BSplineCurve PolesCount=4 KnotsCount=2 Degree=3 IsPeriodic=0
    g52: BSplineCurve PolesCount=4 KnotsCount=2 Degree=3 IsPeriodic=0
    g53: BSplineCurve PolesCount=4 KnotsCount=2 Degree=3 IsPeriodic=0
    g54: BSplineCurve PolesCount=4 KnotsCount=2 Degree=3 IsPeriodic=0
    g55: BSplineCurve PolesCount=4 KnotsCount=2 Degree=3 IsPeriodic=0
    g56: BSplineCurve PolesCount=4 KnotsCount=2 Degree=3 IsPeriodic=0
    g57: BSplineCurve PolesCount=4 KnotsCount=2 Degree=3 IsPeriodic=0
    g58: BSplineCurve PolesCount=4 KnotsCount=2 Degree=3 IsPeriodic=0
    g59: BSplineCurve PolesCount=4 KnotsCount=2 Degree=3 IsPeriodic=0
    g60: BSplineCurve PolesCount=4 KnotsCount=2 Degree=3 IsPeriodic=0
    g61: BSplineCurve PolesCount=4 KnotsCount=2 Degree=3 IsPeriodic=0
    g62: BSplineCurve PolesCount=4 KnotsCount=2 Degree=3 IsPeriodic=0
    g63: BSplineCurve PolesCount=4 KnotsCount=2 Degree=3 IsPeriodic=0
    g64: BSplineCurve PolesCount=4 KnotsCount=2 Degree=3 IsPeriodic=0
    g65: BSplineCurve PolesCount=4 KnotsCount=2 Degree=3 IsPeriodic=0
    g66: BSplineCurve PolesCount=4 KnotsCount=2 Degree=3 IsPeriodic=0
    g67: BSplineCurve PolesCount=4 KnotsCount=2 Degree=3 IsPeriodic=0
    g68: BSplineCurve PolesCount=4 KnotsCount=2 Degree=3 IsPeriodic=0
    g69: BSplineCurve PolesCount=4 KnotsCount=2 Degree=3 IsPeriodic=0
    g70: BSplineCurve PolesCount=4 KnotsCount=2 Degree=3 IsPeriodic=0
    g71: BSplineCurve PolesCount=4 KnotsCount=2 Degree=3 IsPeriodic=0
    g72: BSplineCurve PolesCount=4 KnotsCount=2 Degree=3 IsPeriodic=0
    g73: BSplineCurve PolesCount=4 KnotsCount=2 Degree=3 IsPeriodic=0
    g74: BSplineCurve PolesCount=4 KnotsCount=2 Degree=3 IsPeriodic=0
    g75: BSplineCurve PolesCount=4 KnotsCount=2 Degree=3 IsPeriodic=0
    g76: BSplineCurve PolesCount=4 KnotsCount=2 Degree=3 IsPeriodic=0
    g77: BSplineCurve PolesCount=4 KnotsCount=2 Degree=3 IsPeriodic=0
    g78: BSplineCurve PolesCount=4 KnotsCount=2 Degree=3 IsPeriodic=0
    g79: BSplineCurve PolesCount=4 KnotsCount=2 Degree=3 IsPeriodic=0
    g80: BSplineCurve PolesCount=4 KnotsCount=2 Degree=3 IsPeriodic=0
    g81: BSplineCurve PolesCount=4 KnotsCount=2 Degree=3 IsPeriodic=0
    g82: BSplineCurve PolesCount=4 KnotsCount=2 Degree=3 IsPeriodic=0
    g83: BSplineCurve PolesCount=4 KnotsCount=2 Degree=3 IsPeriodic=0
    g84: BSplineCurve PolesCount=4 KnotsCount=2 Degree=3 IsPeriodic=0
    g85: BSplineCurve PolesCount=4 KnotsCount=2 Degree=3 IsPeriodic=0
    g86: BSplineCurve PolesCount=4 KnotsCount=2 Degree=3 IsPeriodic=0
    g87: BSplineCurve PolesCount=4 KnotsCount=2 Degree=3 IsPeriodic=0
    g88: BSplineCurve PolesCount=4 KnotsCount=2 Degree=3 IsPeriodic=0
    g89: BSplineCurve PolesCount=4 KnotsCount=2 Degree=3 IsPeriodic=0
    g90: BSplineCurve PolesCount=4 KnotsCount=2 Degree=3 IsPeriodic=0
    g91: BSplineCurve PolesCount=4 KnotsCount=2 Degree=3 IsPeriodic=0
    g92: BSplineCurve PolesCount=4 KnotsCount=2 Degree=3 IsPeriodic=0
    g93: BSplineCurve PolesCount=4 KnotsCount=2 Degree=3 IsPeriodic=0
    g94: BSplineCurve PolesCount=4 KnotsCount=2 Degree=3 IsPeriodic=0
    g95: BSplineCurve PolesCount=2 KnotsCount=2 Degree=1 IsPeriodic=0
    g96: BSplineCurve PolesCount=2 KnotsCount=2 Degree=1 IsPeriodic=0
    g97: BSplineCurve PolesCount=4 KnotsCount=2 Degree=3 IsPeriodic=0
    g98: BSplineCurve PolesCount=4 KnotsCount=2 Degree=3 IsPeriodic=0
    g99: BSplineCurve PolesCount=4 KnotsCount=2 Degree=3 IsPeriodic=0
    g100: BSplineCurve PolesCount=4 KnotsCount=2 Degree=3 IsPeriodic=0
    g101: BSplineCurve PolesCount=2 KnotsCount=2 Degree=1 IsPeriodic=0
    g102: BSplineCurve PolesCount=2 KnotsCount=2 Degree=1 IsPeriodic=0
    g103: BSplineCurve PolesCount=4 KnotsCount=2 Degree=3 IsPeriodic=0
    g104: BSplineCurve PolesCount=4 KnotsCount=2 Degree=3 IsPeriodic=0
    g105: BSplineCurve PolesCount=4 KnotsCount=2 Degree=3 IsPeriodic=0
    g106: BSplineCurve PolesCount=2 KnotsCount=2 Degree=1 IsPeriodic=0
    g107: BSplineCurve PolesCount=2 KnotsCount=2 Degree=1 IsPeriodic=0
    g108: BSplineCurve PolesCount=4 KnotsCount=2 Degree=3 IsPeriodic=0
    g109: BSplineCurve PolesCount=4 KnotsCount=2 Degree=3 IsPeriodic=0
    g110: BSplineCurve PolesCount=4 KnotsCount=2 Degree=3 IsPeriodic=0
    g111: BSplineCurve PolesCount=4 KnotsCount=2 Degree=3 IsPeriodic=0
    g112: BSplineCurve PolesCount=4 KnotsCount=2 Degree=3 IsPeriodic=0
    g113: BSplineCurve PolesCount=4 KnotsCount=2 Degree=3 IsPeriodic=0
    g114: BSplineCurve PolesCount=4 KnotsCount=2 Degree=3 IsPeriodic=0
    g115: BSplineCurve PolesCount=4 KnotsCount=2 Degree=3 IsPeriodic=0
    g116: BSplineCurve PolesCount=4 KnotsCount=2 Degree=3 IsPeriodic=0
    g117: BSplineCurve PolesCount=4 KnotsCount=2 Degree=3 IsPeriodic=0
    g118: BSplineCurve PolesCount=4 KnotsCount=2 Degree=3 IsPeriodic=0
    g119: BSplineCurve PolesCount=4 KnotsCount=2 Degree=3 IsPeriodic=0
    g120: BSplineCurve PolesCount=4 KnotsCount=2 Degree=3 IsPeriodic=0
    g121: BSplineCurve PolesCount=4 KnotsCount=2 Degree=3 IsPeriodic=0
    g122: BSplineCurve PolesCount=2 KnotsCount=2 Degree=1 IsPeriodic=0
    g123: BSplineCurve PolesCount=2 KnotsCount=2 Degree=1 IsPeriodic=0
    g124: BSplineCurve PolesCount=4 KnotsCount=2 Degree=3 IsPeriodic=0
    g125: BSplineCurve PolesCount=2 KnotsCount=2 Degree=1 IsPeriodic=0
    g126: BSplineCurve PolesCount=2 KnotsCount=2 Degree=1 IsPeriodic=0
    g127: BSplineCurve PolesCount=4 KnotsCount=2 Degree=3 IsPeriodic=0
    g128: BSplineCurve PolesCount=4 KnotsCount=2 Degree=3 IsPeriodic=0
    g129: BSplineCurve PolesCount=4 KnotsCount=2 Degree=3 IsPeriodic=0
    g130: BSplineCurve PolesCount=4 KnotsCount=2 Degree=3 IsPeriodic=0
    g131: BSplineCurve PolesCount=4 KnotsCount=2 Degree=3 IsPeriodic=0
    g132: BSplineCurve PolesCount=4 KnotsCount=2 Degree=3 IsPeriodic=0
    g133: BSplineCurve PolesCount=4 KnotsCount=2 Degree=3 IsPeriodic=0
    g134: BSplineCurve PolesCount=4 KnotsCount=2 Degree=3 IsPeriodic=0
    g135: BSplineCurve PolesCount=4 KnotsCount=2 Degree=3 IsPeriodic=0
    g136: BSplineCurve PolesCount=4 KnotsCount=2 Degree=3 IsPeriodic=0
    g137: BSplineCurve PolesCount=4 KnotsCount=2 Degree=3 IsPeriodic=0
    g138: BSplineCurve PolesCount=4 KnotsCount=2 Degree=3 IsPeriodic=0
    g139: BSplineCurve PolesCount=4 KnotsCount=2 Degree=3 IsPeriodic=0
    g140: BSplineCurve PolesCount=4 KnotsCount=2 Degree=3 IsPeriodic=0
    g141: BSplineCurve PolesCount=4 KnotsCount=2 Degree=3 IsPeriodic=0
    g142: BSplineCurve PolesCount=4 KnotsCount=2 Degree=3 IsPeriodic=0
    g143: BSplineCurve PolesCount=4 KnotsCount=2 Degree=3 IsPeriodic=0
    g144: BSplineCurve PolesCount=4 KnotsCount=2 Degree=3 IsPeriodic=0
    g145: BSplineCurve PolesCount=4 KnotsCount=2 Degree=3 IsPeriodic=0
    g146: BSplineCurve PolesCount=4 KnotsCount=2 Degree=3 IsPeriodic=0
    g147: BSplineCurve PolesCount=4 KnotsCount=2 Degree=3 IsPeriodic=0
    g148: BSplineCurve PolesCount=4 KnotsCount=2 Degree=3 IsPeriodic=0
    g149: BSplineCurve PolesCount=4 KnotsCount=2 Degree=3 IsPeriodic=0
    g150: BSplineCurve PolesCount=4 KnotsCount=2 Degree=3 IsPeriodic=0
    g151: BSplineCurve PolesCount=4 KnotsCount=2 Degree=3 IsPeriodic=0
    g152: BSplineCurve PolesCount=4 KnotsCount=2 Degree=3 IsPeriodic=0
    g153: BSplineCurve PolesCount=4 KnotsCount=2 Degree=3 IsPeriodic=0
    g154: BSplineCurve PolesCount=4 KnotsCount=2 Degree=3 IsPeriodic=0
    g155: BSplineCurve PolesCount=2 KnotsCount=2 Degree=1 IsPeriodic=0
    g156: BSplineCurve PolesCount=2 KnotsCount=2 Degree=1 IsPeriodic=0
    g157: BSplineCurve PolesCount=4 KnotsCount=2 Degree=3 IsPeriodic=0
    g158: BSplineCurve PolesCount=4 KnotsCount=2 Degree=3 IsPeriodic=0
    g159: BSplineCurve PolesCount=4 KnotsCount=2 Degree=3 IsPeriodic=0
    g160: BSplineCurve PolesCount=4 KnotsCount=2 Degree=3 IsPeriodic=0
    g161: BSplineCurve PolesCount=4 KnotsCount=2 Degree=3 IsPeriodic=0
    g162: BSplineCurve PolesCount=4 KnotsCount=2 Degree=3 IsPeriodic=0
    g163: BSplineCurve PolesCount=4 KnotsCount=2 Degree=3 IsPeriodic=0
    g164: BSplineCurve PolesCount=4 KnotsCount=2 Degree=3 IsPeriodic=0
    g165: BSplineCurve PolesCount=4 KnotsCount=2 Degree=3 IsPeriodic=0
    g166: BSplineCurve PolesCount=4 KnotsCount=2 Degree=3 IsPeriodic=0
    g167: BSplineCurve PolesCount=2 KnotsCount=2 Degree=1 IsPeriodic=0
    g168: BSplineCurve PolesCount=2 KnotsCount=2 Degree=1 IsPeriodic=0
    g169: BSplineCurve PolesCount=4 KnotsCount=2 Degree=3 IsPeriodic=0
    g170: BSplineCurve PolesCount=2 KnotsCount=2 Degree=1 IsPeriodic=0
    g171: BSplineCurve PolesCount=2 KnotsCount=2 Degree=1 IsPeriodic=0
    g172: BSplineCurve PolesCount=4 KnotsCount=2 Degree=3 IsPeriodic=0
    g173: BSplineCurve PolesCount=4 KnotsCount=2 Degree=3 IsPeriodic=0
    g174: BSplineCurve PolesCount=4 KnotsCount=2 Degree=3 IsPeriodic=0
    g175: BSplineCurve PolesCount=4 KnotsCount=2 Degree=3 IsPeriodic=0
    g176: BSplineCurve PolesCount=4 KnotsCount=2 Degree=3 IsPeriodic=0
    g177: BSplineCurve PolesCount=4 KnotsCount=2 Degree=3 IsPeriodic=0
    g178: BSplineCurve PolesCount=4 KnotsCount=2 Degree=3 IsPeriodic=0
    g179: BSplineCurve PolesCount=4 KnotsCount=2 Degree=3 IsPeriodic=0
  constraints (181):
    c: Coincident(g0,g1)
    c: Coincident(g1,g2)
    c: Coincident(g2,g3)
    c: Coincident(g3,g4)
    c: Coincident(g4,g5)
    c: Coincident(g5,g6)
    c: Coincident(g6,g7)
    c: Coincident(g7,g8)
    c: Coincident(g8,g9)
    c: Coincident(g9,g10)
    c: Coincident(g10,g11)
    c: Coincident(g11,g12)
    c: Coincident(g12,g13)
    c: Coincident(g13,g14)
    c: Coincident(g14,g15)
    c: Coincident(g15,g16)
    c: Coincident(g16,g17)
    c: Coincident(g17,g18)
    c: Coincident(g18,g19)
    c: Coincident(g19,g20)
    c: Coincident(g20,g21)
    c: Coincident(g21,g22)
    c: Coincident(g22,g23)
    c: Coincident(g23,g24)
    c: Coincident(g24,g25)
    c: Coincident(g25,g26)
    c: Coincident(g26,g27)
    c: Coincident(g27,g28)
    c: Coincident(g28,g29)
    c: Coincident(g29,g30)
    c: Coincident(g30,g31)
    c: Coincident(g31,g32)
    c: Coincident(g32,g33)
    c: Coincident(g33,g34)
    c: Coincident(g34,g35)
    c: Coincident(g35,g36)
    c: Coincident(g36,g37)
    c: Coincident(g37,g38)
    c: Coincident(g38,g39)
    c: Coincident(g39,g40)
    c: Coincident(g40,g41)
    c: Coincident(g41,g42)
    c: Coincident(g42,g43)
    c: Coincident(g43,g44)
    c: Coincident(g44,g45)
    c: Coincident(g45,g46)
    c: Coincident(g46,g47)
    c: Coincident(g47,g0)
    c: Coincident(g48,g49)
    c: Coincident(g49,g50)
    c: Coincident(g50,g51)
    c: Coincident(g51,g52)
    c: Coincident(g52,g53)
    c: Coincident(g53,g48)
    c: Coincident(g54,g55)
    c: Coincident(g55,g56)
    c: Coincident(g56,g57)
    c: Coincident(g57,g58)
    c: Coincident(g58,g59)
    c: Coincident(g59,g60)
    c: Coincident(g60,g61)
    c: Coincident(g61,g62)
    c: Coincident(g62,g63)
    c: Coincident(g63,g54)
    c: Coincident(g64,g65)
    c: Coincident(g65,g66)
    c: Coincident(g66,g67)
    c: Coincident(g67,g68)
    c: Coincident(g68,g64)
    c: Coincident(g69,g70)
    c: Coincident(g70,g71)
    c: Coincident(g71,g72)
    c: Coincident(g72,g73)
    c: Coincident(g73,g74)
    c: Coincident(g74,g75)
    c: Coincident(g75,g76)
    c: Coincident(g76,g77)
    c: Coincident(g77,g78)
    c: Coincident(g78,g79)
    c: Coincident(g79,g80)
    c: Coincident(g80,g81)
    c: Coincident(g81,g82)
    c: Coincident(g82,g83)
    c: Coincident(g83,g84)
    c: Coincident(g84,g85)
    c: Coincident(g85,g69)
    c: Coincident(g86,g87)
    c: Coincident(g87,g88)
    c: Coincident(g88,g89)
    c: Coincident(g89,g90)
    c: Coincident(g90,g91)
    c: Coincident(g91,g92)
    c: Coincident(g92,g93)
    c: Coincident(g93,g94)
    c: Coincident(g94,g95)
    c: Coincident(g95,g96)
    c: Coincident(g96,g97)
    c: Coincident(g97,g98)
    c: Coincident(g98,g99)
    c: Coincident(g99,g100)
    c: Coincident(g100,g101)
    c: Coincident(g101,g102)
    c: Coincident(g102,g103)
    c: Coincident(g103,g86)
    c: Coincident(g104,g105)
    c: Coincident(g105,g106)
    c: Coincident(g106,g107)
    c: Coincident(g107,g108)
    c: Coincident(g108,g109)
    c: Coincident(g109,g104)
    c: Coincident(g110,g111)
    c: Coincident(g111,g112)
    c: Coincident(g112,g113)
    c: Coincident(g113,g114)
    c: Coincident(g114,g110)
    c: Coincident(g115,g116)
    c: Coincident(g116,g117)
    c: Coincident(g117,g118)
    c: Coincident(g118,g119)
    c: Coincident(g119,g120)
    c: Coincident(g120,g121)
    c: Coincident(g121,g122)
    c: Coincident(g122,g123)
    c: Coincident(g123,g124)
    c: Coincident(g124,g125)
    c: Coincident(g125,g126)
    c: Coincident(g126,g127)
    c: Coincident(g127,g128)
    c: Coincident(g128,g115)
    c: Coincident(g129,g130)
    c: Coincident(g130,g131)
    c: Coincident(g131,g132)
    c: Coincident(g132,g133)
    c: Coincident(g133,g129)
    c: Coincident(g134,g135)
    c: Coincident(g135,g136)
    c: Coincident(g136,g137)
    c: Coincident(g137,g138)
    c: Coincident(g138,g134)
    c: Coincident(g139,g140)
    c: Coincident(g140,g141)
    c: Coincident(g141,g142)
    c: Coincident(g142,g143)
    c: Coincident(g143,g144)
    c: Coincident(g144,g145)
    c: Coincident(g145,g146)
    c: Coincident(g146,g139)
    c: Coincident(g147,g148)
    c: Coincident(g148,g149)
    c: Coincident(g149,g150)
    c: Coincident(g150,g151)
    c: Coincident(g151,g152)
    c: Coincident(g152,g153)
    c: Coincident(g153,g154)
    c: Coincident(g154,g155)
    c: Coincident(g155,g156)
    c: Coincident(g156,g157)
    c: Coincident(g157,g158)
    c: Coincident(g158,g159)
    c: Coincident(g159,g160)
    c: Coincident(g160,g161)
    c: Coincident(g161,g162)
    c: Coincident(g162,g163)
    c: Coincident(g163,g164)
    c: Coincident(g164,g147)
    c: Coincident(g165,g166)
    c: Coincident(g166,g167)
    c: Coincident(g167,g168)
    c: Coincident(g168,g169)
    c: Coincident(g169,g170)
    c: Coincident(g170,g171)
    c: Coincident(g171,g172)
    c: Coincident(g172,g173)
    c: Coincident(g173,g174)
    c: Coincident(g174,g175)
    c: Coincident(g175,g176)
    c: Coincident(g176,g177)
    c: Coincident(g177,g178)
    c: Coincident(g178,g179)
    c: Coincident(g179,g165)
    c: Coincident(g48,g48)
FEATURE [Sketcher::SketchObject] Sketch021  label="Washerwoman-Sketch"
  ArcFitTolerance = 1e-06
  FullyConstrained = false
  MakeInternals = false
  sketch-geometry (320):
    g0: BSplineCurve PolesCount=4 KnotsCount=2 Degree=3 IsPeriodic=0
    g1: BSplineCurve PolesCount=4 KnotsCount=2 Degree=3 IsPeriodic=0
    g2: BSplineCurve PolesCount=4 KnotsCount=2 Degree=3 IsPeriodic=0
    g3: BSplineCurve PolesCount=4 KnotsCount=2 Degree=3 IsPeriodic=0
    g4: BSplineCurve PolesCount=4 KnotsCount=2 Degree=3 IsPeriodic=0
    g5: BSplineCurve PolesCount=4 KnotsCount=2 Degree=3 IsPeriodic=0
    g6: BSplineCurve PolesCount=4 KnotsCount=2 Degree=3 IsPeriodic=0
    g7: BSplineCurve PolesCount=4 KnotsCount=2 Degree=3 IsPeriodic=0
    g8: BSplineCurve PolesCount=4 KnotsCount=2 Degree=3 IsPeriodic=0
    g9: BSplineCurve PolesCount=4 KnotsCount=2 Degree=3 IsPeriodic=0
    g10: BSplineCurve PolesCount=4 KnotsCount=2 Degree=3 IsPeriodic=0
    g11: BSplineCurve PolesCount=4 KnotsCount=2 Degree=3 IsPeriodic=0
    g12: BSplineCurve PolesCount=4 KnotsCount=2 Degree=3 IsPeriodic=0
    g13: BSplineCurve PolesCount=4 KnotsCount=2 Degree=3 IsPeriodic=0
    g14: BSplineCurve PolesCount=4 KnotsCount=2 Degree=3 IsPeriodic=0
    g15: BSplineCurve PolesCount=4 KnotsCount=2 Degree=3 IsPeriodic=0
    g16: BSplineCurve PolesCount=4 KnotsCount=2 Degree=3 IsPeriodic=0
    g17: BSplineCurve PolesCount=4 KnotsCount=2 Degree=3 IsPeriodic=0
    g18: BSplineCurve PolesCount=4 KnotsCount=2 Degree=3 IsPeriodic=0
    g19: BSplineCurve PolesCount=4 KnotsCount=2 Degree=3 IsPeriodic=0
    g20: BSplineCurve PolesCount=4 KnotsCount=2 Degree=3 IsPeriodic=0
    g21: BSplineCurve PolesCount=4 KnotsCount=2 Degree=3 IsPeriodic=0
    g22: BSplineCurve PolesCount=2 KnotsCount=2 Degree=1 IsPeriodic=0
    g23: BSplineCurve PolesCount=2 KnotsCount=2 Degree=1 IsPeriodic=0
    g24: BSplineCurve PolesCount=4 KnotsCount=2 Degree=3 IsPeriodic=0
    g25: BSplineCurve PolesCount=4 KnotsCount=2 Degree=3 IsPeriodic=0
    g26: BSplineCurve PolesCount=4 KnotsCount=2 Degree=3 IsPeriodic=0
    g27: BSplineCurve PolesCount=4 KnotsCount=2 Degree=3 IsPeriodic=0
    g28: BSplineCurve PolesCount=2 KnotsCount=2 Degree=1 IsPeriodic=0
    g29: BSplineCurve PolesCount=2 KnotsCount=2 Degree=1 IsPeriodic=0
    g30: BSplineCurve PolesCount=4 KnotsCount=2 Degree=3 IsPeriodic=0
    g31: BSplineCurve PolesCount=4 KnotsCount=2 Degree=3 IsPeriodic=0
    g32: BSplineCurve PolesCount=4 KnotsCount=2 Degree=3 IsPeriodic=0
    g33: BSplineCurve PolesCount=4 KnotsCount=2 Degree=3 IsPeriodic=0
    g34: BSplineCurve PolesCount=4 KnotsCount=2 Degree=3 IsPeriodic=0
    g35: BSplineCurve PolesCount=4 KnotsCount=2 Degree=3 IsPeriodic=0
    g36: BSplineCurve PolesCount=4 KnotsCount=2 Degree=3 IsPeriodic=0
    g37: BSplineCurve PolesCount=4 KnotsCount=2 Degree=3 IsPeriodic=0
    g38: BSplineCurve PolesCount=4 KnotsCount=2 Degree=3 IsPeriodic=0
    g39: BSplineCurve PolesCount=4 KnotsCount=2 Degree=3 IsPeriodic=0
    g40: BSplineCurve PolesCount=4 KnotsCount=2 Degree=3 IsPeriodic=0
    g41: BSplineCurve PolesCount=4 KnotsCount=2 Degree=3 IsPeriodic=0
    g42: BSplineCurve PolesCount=4 KnotsCount=2 Degree=3 IsPeriodic=0
    g43: BSplineCurve PolesCount=4 KnotsCount=2 Degree=3 IsPeriodic=0
    g44: BSplineCurve PolesCount=4 KnotsCount=2 Degree=3 IsPeriodic=0
    g45: BSplineCurve PolesCount=4 KnotsCount=2 Degree=3 IsPeriodic=0
    g46: BSplineCurve PolesCount=4 KnotsCount=2 Degree=3 IsPeriodic=0
    g47: BSplineCurve PolesCount=4 KnotsCount=2 Degree=3 IsPeriodic=0
    g48: BSplineCurve PolesCount=4 KnotsCount=2 Degree=3 IsPeriodic=0
    g49: BSplineCurve PolesCount=4 KnotsCount=2 Degree=3 IsPeriodic=0
    g50: BSplineCurve PolesCount=4 KnotsCount=2 Degree=3 IsPeriodic=0
    g51: BSplineCurve PolesCount=4 KnotsCount=2 Degree=3 IsPeriodic=0
    g52: BSplineCurve PolesCount=4 KnotsCount=2 Degree=3 IsPeriodic=0
    g53: BSplineCurve PolesCount=4 KnotsCount=2 Degree=3 IsPeriodic=0
    g54: BSplineCurve PolesCount=4 KnotsCount=2 Degree=3 IsPeriodic=0
    g55: BSplineCurve PolesCount=4 KnotsCount=2 Degree=3 IsPeriodic=0
    g56: BSplineCurve PolesCount=4 KnotsCount=2 Degree=3 IsPeriodic=0
    g57: BSplineCurve PolesCount=4 KnotsCount=2 Degree=3 IsPeriodic=0
    g58: BSplineCurve PolesCount=4 KnotsCount=2 Degree=3 IsPeriodic=0
    g59: BSplineCurve PolesCount=4 KnotsCount=2 Degree=3 IsPeriodic=0
    g60: BSplineCurve PolesCount=4 KnotsCount=2 Degree=3 IsPeriodic=0
    g61: BSplineCurve PolesCount=4 KnotsCount=2 Degree=3 IsPeriodic=0
    g62: BSplineCurve PolesCount=4 KnotsCount=2 Degree=3 IsPeriodic=0
    g63: BSplineCurve PolesCount=4 KnotsCount=2 Degree=3 IsPeriodic=0
    g64: BSplineCurve PolesCount=4 KnotsCount=2 Degree=3 IsPeriodic=0
    g65: BSplineCurve PolesCount=4 KnotsCount=2 Degree=3 IsPeriodic=0
    g66: BSplineCurve PolesCount=4 KnotsCount=2 Degree=3 IsPeriodic=0
    g67: BSplineCurve PolesCount=4 KnotsCount=2 Degree=3 IsPeriodic=0
    g68: BSplineCurve PolesCount=4 KnotsCount=2 Degree=3 IsPeriodic=0
    g69: BSplineCurve PolesCount=4 KnotsCount=2 Degree=3 IsPeriodic=0
    g70: BSplineCurve PolesCount=4 KnotsCount=2 Degree=3 IsPeriodic=0
    g71: BSplineCurve PolesCount=4 KnotsCount=2 Degree=3 IsPeriodic=0
    g72: BSplineCurve PolesCount=4 KnotsCount=2 Degree=3 IsPeriodic=0
    g73: BSplineCurve PolesCount=4 KnotsCount=2 Degree=3 IsPeriodic=0
    g74: BSplineCurve PolesCount=4 KnotsCount=2 Degree=3 IsPeriodic=0
    g75: BSplineCurve PolesCount=2 KnotsCount=2 Degree=1 IsPeriodic=0
    g76: BSplineCurve PolesCount=2 KnotsCount=2 Degree=1 IsPeriodic=0
    g77: BSplineCurve PolesCount=4 KnotsCount=2 Degree=3 IsPeriodic=0
    g78: BSplineCurve PolesCount=2 KnotsCount=2 Degree=1 IsPeriodic=0
    g79: BSplineCurve PolesCount=2 KnotsCount=2 Degree=1 IsPeriodic=0
    g80: BSplineCurve PolesCount=4 KnotsCount=2 Degree=3 IsPeriodic=0
    g81: BSplineCurve PolesCount=4 KnotsCount=2 Degree=3 IsPeriodic=0
    g82: BSplineCurve PolesCount=4 KnotsCount=2 Degree=3 IsPeriodic=0
    g83: BSplineCurve PolesCount=4 KnotsCount=2 Degree=3 IsPeriodic=0
    g84: BSplineCurve PolesCount=4 KnotsCount=2 Degree=3 IsPeriodic=0
    g85: BSplineCurve PolesCount=4 KnotsCount=2 Degree=3 IsPeriodic=0
    g86: BSplineCurve PolesCount=4 KnotsCount=2 Degree=3 IsPeriodic=0
    g87: BSplineCurve PolesCount=4 KnotsCount=2 Degree=3 IsPeriodic=0
    g88: BSplineCurve PolesCount=4 KnotsCount=2 Degree=3 IsPeriodic=0
    g89: BSplineCurve PolesCount=2 KnotsCount=2 Degree=1 IsPeriodic=0
    g90: BSplineCurve PolesCount=2 KnotsCount=2 Degree=1 IsPeriodic=0
    g91: BSplineCurve PolesCount=4 KnotsCount=2 Degree=3 IsPeriodic=0
    g92: BSplineCurve PolesCount=4 KnotsCount=2 Degree=3 IsPeriodic=0
    g93: BSplineCurve PolesCount=2 KnotsCount=2 Degree=1 IsPeriodic=0
    g94: BSplineCurve PolesCount=2 KnotsCount=2 Degree=1 IsPeriodic=0
    g95: BSplineCurve PolesCount=4 KnotsCount=2 Degree=3 IsPeriodic=0
    g96: BSplineCurve PolesCount=4 KnotsCount=2 Degree=3 IsPeriodic=0
    g97: BSplineCurve PolesCount=4 KnotsCount=2 Degree=3 IsPeriodic=0
    g98: BSplineCurve PolesCount=4 KnotsCount=2 Degree=3 IsPeriodic=0
    g99: BSplineCurve PolesCount=4 KnotsCount=2 Degree=3 IsPeriodic=0
    g100: BSplineCurve PolesCount=4 KnotsCount=2 Degree=3 IsPeriodic=0
    g101: BSplineCurve PolesCount=4 KnotsCount=2 Degree=3 IsPeriodic=0
    g102: BSplineCurve PolesCount=4 KnotsCount=2 Degree=3 IsPeriodic=0
    g103: BSplineCurve PolesCount=4 KnotsCount=2 Degree=3 IsPeriodic=0
    g104: BSplineCurve PolesCount=4 KnotsCount=2 Degree=3 IsPeriodic=0
    g105: BSplineCurve PolesCount=4 KnotsCount=2 Degree=3 IsPeriodic=0
    g106: BSplineCurve PolesCount=4 KnotsCount=2 Degree=3 IsPeriodic=0
    g107: BSplineCurve PolesCount=4 KnotsCount=2 Degree=3 IsPeriodic=0
    g108: BSplineCurve PolesCount=4 KnotsCount=2 Degree=3 IsPeriodic=0
    g109: BSplineCurve PolesCount=4 KnotsCount=2 Degree=3 IsPeriodic=0
    g110: BSplineCurve PolesCount=4 KnotsCount=2 Degree=3 IsPeriodic=0
    g111: BSplineCurve PolesCount=4 KnotsCount=2 Degree=3 IsPeriodic=0
    g112: BSplineCurve PolesCount=2 KnotsCount=2 Degree=1 IsPeriodic=0
    g113: BSplineCurve PolesCount=2 KnotsCount=2 Degree=1 IsPeriodic=0
    g114: BSplineCurve PolesCount=4 KnotsCount=2 Degree=3 IsPeriodic=0
    g115: BSplineCurve PolesCount=4 KnotsCount=2 Degree=3 IsPeriodic=0
    g116: BSplineCurve PolesCount=4 KnotsCount=2 Degree=3 IsPeriodic=0
    g117: BSplineCurve PolesCount=4 KnotsCount=2 Degree=3 IsPeriodic=0
    g118: BSplineCurve PolesCount=4 KnotsCount=2 Degree=3 IsPeriodic=0
    g119: BSplineCurve PolesCount=4 KnotsCount=2 Degree=3 IsPeriodic=0
    g120: BSplineCurve PolesCount=4 KnotsCount=2 Degree=3 IsPeriodic=0
    g121: BSplineCurve PolesCount=4 KnotsCount=2 Degree=3 IsPeriodic=0
    g122: BSplineCurve PolesCount=4 KnotsCount=2 Degree=3 IsPeriodic=0
    g123: BSplineCurve PolesCount=2 KnotsCount=2 Degree=1 IsPeriodic=0
    g124: BSplineCurve PolesCount=2 KnotsCount=2 Degree=1 IsPeriodic=0
    g125: BSplineCurve PolesCount=4 KnotsCount=2 Degree=3 IsPeriodic=0
    g126: BSplineCurve PolesCount=4 KnotsCount=2 Degree=3 IsPeriodic=0
    g127: BSplineCurve PolesCount=4 KnotsCount=2 Degree=3 IsPeriodic=0
    g128: BSplineCurve PolesCount=4 KnotsCount=2 Degree=3 IsPeriodic=0
    g129: BSplineCurve PolesCount=2 KnotsCount=2 Degree=1 IsPeriodic=0
    g130: BSplineCurve PolesCount=2 KnotsCount=2 Degree=1 IsPeriodic=0
    g131: BSplineCurve PolesCount=4 KnotsCount=2 Degree=3 IsPeriodic=0
    g132: BSplineCurve PolesCount=2 KnotsCount=2 Degree=1 IsPeriodic=0
    g133: BSplineCurve PolesCount=2 KnotsCount=2 Degree=1 IsPeriodic=0
    g134: BSplineCurve PolesCount=2 KnotsCount=2 Degree=1 IsPeriodic=0
    g135: BSplineCurve PolesCount=2 KnotsCount=2 Degree=1 IsPeriodic=0
    g136: BSplineCurve PolesCount=4 KnotsCount=2 Degree=3 IsPeriodic=0
    g137: BSplineCurve PolesCount=2 KnotsCount=2 Degree=1 IsPeriodic=0
    g138: BSplineCurve PolesCount=2 KnotsCount=2 Degree=1 IsPeriodic=0
    g139: BSplineCurve PolesCount=4 KnotsCount=2 Degree=3 IsPeriodic=0
    g140: BSplineCurve PolesCount=4 KnotsCount=2 Degree=3 IsPeriodic=0
    g141: BSplineCurve PolesCount=4 KnotsCount=2 Degree=3 IsPeriodic=0
    g142: BSplineCurve PolesCount=4 KnotsCount=2 Degree=3 IsPeriodic=0
    g143: BSplineCurve PolesCount=4 KnotsCount=2 Degree=3 IsPeriodic=0
    g144: BSplineCurve PolesCount=4 KnotsCount=2 Degree=3 IsPeriodic=0
    g145: BSplineCurve PolesCount=2 KnotsCount=2 Degree=1 IsPeriodic=0
    g146: BSplineCurve PolesCount=2 KnotsCount=2 Degree=1 IsPeriodic=0
    g147: BSplineCurve PolesCount=4 KnotsCount=2 Degree=3 IsPeriodic=0
    g148: BSplineCurve PolesCount=2 KnotsCount=2 Degree=1 IsPeriodic=0
    g149: BSplineCurve PolesCount=2 KnotsCount=2 Degree=1 IsPeriodic=0
    g150: BSplineCurve PolesCount=4 KnotsCount=2 Degree=3 IsPeriodic=0
    g151: BSplineCurve PolesCount=4 KnotsCount=2 Degree=3 IsPeriodic=0
    g152: BSplineCurve PolesCount=4 KnotsCount=2 Degree=3 IsPeriodic=0
    g153: BSplineCurve PolesCount=4 KnotsCount=2 Degree=3 IsPeriodic=0
    g154: BSplineCurve PolesCount=4 KnotsCount=2 Degree=3 IsPeriodic=0
    g155: BSplineCurve PolesCount=4 KnotsCount=2 Degree=3 IsPeriodic=0
    g156: BSplineCurve PolesCount=4 KnotsCount=2 Degree=3 IsPeriodic=0
    g157: BSplineCurve PolesCount=4 KnotsCount=2 Degree=3 IsPeriodic=0
    g158: BSplineCurve PolesCount=2 KnotsCount=2 Degree=1 IsPeriodic=0
    g159: BSplineCurve PolesCount=2 KnotsCount=2 Degree=1 IsPeriodic=0
    g160: BSplineCurve PolesCount=4 KnotsCount=2 Degree=3 IsPeriodic=0
    g161: BSplineCurve PolesCount=4 KnotsCount=2 Degree=3 IsPeriodic=0
    g162: BSplineCurve PolesCount=4 KnotsCount=2 Degree=3 IsPeriodic=0
    g163: BSplineCurve PolesCount=2 KnotsCount=2 Degree=1 IsPeriodic=0
    g164: BSplineCurve PolesCount=2 KnotsCount=2 Degree=1 IsPeriodic=0
    g165: BSplineCurve PolesCount=4 KnotsCount=2 Degree=3 IsPeriodic=0
    g166: BSplineCurve PolesCount=4 KnotsCount=2 Degree=3 IsPeriodic=0
    g167: BSplineCurve PolesCount=4 KnotsCount=2 Degree=3 IsPeriodic=0
    g168: BSplineCurve PolesCount=4 KnotsCount=2 Degree=3 IsPeriodic=0
    g169: BSplineCurve PolesCount=4 KnotsCount=2 Degree=3 IsPeriodic=0
    g170: BSplineCurve PolesCount=4 KnotsCount=2 Degree=3 IsPeriodic=0
    g171: BSplineCurve PolesCount=4 KnotsCount=2 Degree=3 IsPeriodic=0
    g172: BSplineCurve PolesCount=4 KnotsCount=2 Degree=3 IsPeriodic=0
    g173: BSplineCurve PolesCount=2 KnotsCount=2 Degree=1 IsPeriodic=0
    g174: BSplineCurve PolesCount=2 KnotsCount=2 Degree=1 IsPeriodic=0
    g175: BSplineCurve PolesCount=4 KnotsCount=2 Degree=3 IsPeriodic=0
    g176: BSplineCurve PolesCount=4 KnotsCount=2 Degree=3 IsPeriodic=0
    g177: BSplineCurve PolesCount=4 KnotsCount=2 Degree=3 IsPeriodic=0
    g178: BSplineCurve PolesCount=4 KnotsCount=2 Degree=3 IsPeriodic=0
    g179: BSplineCurve PolesCount=4 KnotsCount=2 Degree=3 IsPeriodic=0
    g180: BSplineCurve PolesCount=4 KnotsCount=2 Degree=3 IsPeriodic=0
    g181: BSplineCurve PolesCount=4 KnotsCount=2 Degree=3 IsPeriodic=0
    g182: BSplineCurve PolesCount=4 KnotsCount=2 Degree=3 IsPeriodic=0
    g183: BSplineCurve PolesCount=4 KnotsCount=2 Degree=3 IsPeriodic=0
    g184: BSplineCurve PolesCount=4 KnotsCount=2 Degree=3 IsPeriodic=0
    g185: BSplineCurve PolesCount=4 KnotsCount=2 Degree=3 IsPeriodic=0
    g186: BSplineCurve PolesCount=4 KnotsCount=2 Degree=3 IsPeriodic=0
    g187: BSplineCurve PolesCount=4 KnotsCount=2 Degree=3 IsPeriodic=0
    g188: BSplineCurve PolesCount=4 KnotsCount=2 Degree=3 IsPeriodic=0
    g189: BSplineCurve PolesCount=4 KnotsCount=2 Degree=3 IsPeriodic=0
    g190: BSplineCurve PolesCount=4 KnotsCount=2 Degree=3 IsPeriodic=0
    g191: BSplineCurve PolesCount=4 KnotsCount=2 Degree=3 IsPeriodic=0
    g192: BSplineCurve PolesCount=4 KnotsCount=2 Degree=3 IsPeriodic=0
    g193: BSplineCurve PolesCount=4 KnotsCount=2 Degree=3 IsPeriodic=0
    g194: BSplineCurve PolesCount=4 KnotsCount=2 Degree=3 IsPeriodic=0
    g195: BSplineCurve PolesCount=4 KnotsCount=2 Degree=3 IsPeriodic=0
    g196: BSplineCurve PolesCount=4 KnotsCount=2 Degree=3 IsPeriodic=0
    g197: BSplineCurve PolesCount=2 KnotsCount=2 Degree=1 IsPeriodic=0
    g198: BSplineCurve PolesCount=4 KnotsCount=2 Degree=3 IsPeriodic=0
    g199: BSplineCurve PolesCount=4 KnotsCount=2 Degree=3 IsPeriodic=0
    g200: BSplineCurve PolesCount=4 KnotsCount=2 Degree=3 IsPeriodic=0
    g201: BSplineCurve PolesCount=2 KnotsCount=2 Degree=1 IsPeriodic=0
    g202: BSplineCurve PolesCount=2 KnotsCount=2 Degree=1 IsPeriodic=0
    g203: BSplineCurve PolesCount=4 KnotsCount=2 Degree=3 IsPeriodic=0
    g204: BSplineCurve PolesCount=4 KnotsCount=2 Degree=3 IsPeriodic=0
    g205: BSplineCurve PolesCount=4 KnotsCount=2 Degree=3 IsPeriodic=0
    g206: BSplineCurve PolesCount=4 KnotsCount=2 Degree=3 IsPeriodic=0
    g207: BSplineCurve PolesCount=4 KnotsCount=2 Degree=3 IsPeriodic=0
    g208: BSplineCurve PolesCount=4 KnotsCount=2 Degree=3 IsPeriodic=0
    g209: BSplineCurve PolesCount=4 KnotsCount=2 Degree=3 IsPeriodic=0
    g210: BSplineCurve PolesCount=4 KnotsCount=2 Degree=3 IsPeriodic=0
    g211: BSplineCurve PolesCount=4 KnotsCount=2 Degree=3 IsPeriodic=0
    g212: BSplineCurve PolesCount=4 KnotsCount=2 Degree=3 IsPeriodic=0
    g213: BSplineCurve PolesCount=4 KnotsCount=2 Degree=3 IsPeriodic=0
    g214: BSplineCurve PolesCount=2 KnotsCount=2 Degree=1 IsPeriodic=0
    g215: BSplineCurve PolesCount=4 KnotsCount=2 Degree=3 IsPeriodic=0
    g216: BSplineCurve PolesCount=4 KnotsCount=2 Degree=3 IsPeriodic=0
    g217: BSplineCurve PolesCount=4 KnotsCount=2 Degree=3 IsPeriodic=0
    g218: BSplineCurve PolesCount=4 KnotsCount=2 Degree=3 IsPeriodic=0
    g219: BSplineCurve PolesCount=4 KnotsCount=2 Degree=3 IsPeriodic=0
    g220: BSplineCurve PolesCount=4 KnotsCount=2 Degree=3 IsPeriodic=0
    g221: BSplineCurve PolesCount=4 KnotsCount=2 Degree=3 IsPeriodic=0
    g222: BSplineCurve PolesCount=4 KnotsCount=2 Degree=3 IsPeriodic=0
    g223: BSplineCurve PolesCount=4 KnotsCount=2 Degree=3 IsPeriodic=0
    g224: BSplineCurve PolesCount=4 KnotsCount=2 Degree=3 IsPeriodic=0
    g225: BSplineCurve PolesCount=4 KnotsCount=2 Degree=3 IsPeriodic=0
    g226: BSplineCurve PolesCount=4 KnotsCount=2 Degree=3 IsPeriodic=0
    g227: BSplineCurve PolesCount=4 KnotsCount=2 Degree=3 IsPeriodic=0
    g228: BSplineCurve PolesCount=4 KnotsCount=2 Degree=3 IsPeriodic=0
    g229: BSplineCurve PolesCount=4 KnotsCount=2 Degree=3 IsPeriodic=0
    g230: BSplineCurve PolesCount=4 KnotsCount=2 Degree=3 IsPeriodic=0
    g231: BSplineCurve PolesCount=4 KnotsCount=2 Degree=3 IsPeriodic=0
    g232: BSplineCurve PolesCount=4 KnotsCount=2 Degree=3 IsPeriodic=0
    g233: BSplineCurve PolesCount=4 KnotsCount=2 Degree=3 IsPeriodic=0
    g234: BSplineCurve PolesCount=4 KnotsCount=2 Degree=3 IsPeriodic=0
    g235: BSplineCurve PolesCount=4 KnotsCount=2 Degree=3 IsPeriodic=0
    g236: BSplineCurve PolesCount=4 KnotsCount=2 Degree=3 IsPeriodic=0
    g237: BSplineCurve PolesCount=4 KnotsCount=2 Degree=3 IsPeriodic=0
    g238: BSplineCurve PolesCount=4 KnotsCount=2 Degree=3 IsPeriodic=0
    g239: BSplineCurve PolesCount=4 KnotsCount=2 Degree=3 IsPeriodic=0
    g240: BSplineCurve PolesCount=4 KnotsCount=2 Degree=3 IsPeriodic=0
    g241: BSplineCurve PolesCount=4 KnotsCount=2 Degree=3 IsPeriodic=0
    g242: BSplineCurve PolesCount=4 KnotsCount=2 Degree=3 IsPeriodic=0
    g243: BSplineCurve PolesCount=4 KnotsCount=2 Degree=3 IsPeriodic=0
    g244: BSplineCurve PolesCount=4 KnotsCount=2 Degree=3 IsPeriodic=0
    g245: BSplineCurve PolesCount=4 KnotsCount=2 Degree=3 IsPeriodic=0
    g246: BSplineCurve PolesCount=2 KnotsCount=2 Degree=1 IsPeriodic=0
    g247: BSplineCurve PolesCount=2 KnotsCount=2 Degree=1 IsPeriodic=0
    g248: BSplineCurve PolesCount=4 KnotsCount=2 Degree=3 IsPeriodic=0
    g249: BSplineCurve PolesCount=4 KnotsCount=2 Degree=3 IsPeriodic=0
    g250: BSplineCurve PolesCount=4 KnotsCount=2 Degree=3 IsPeriodic=0
    g251: BSplineCurve PolesCount=4 KnotsCount=2 Degree=3 IsPeriodic=0
    g252: BSplineCurve PolesCount=4 KnotsCount=2 Degree=3 IsPeriodic=0
    g253: BSplineCurve PolesCount=4 KnotsCount=2 Degree=3 IsPeriodic=0
    g254: BSplineCurve PolesCount=4 KnotsCount=2 Degree=3 IsPeriodic=0
    g255: BSplineCurve PolesCount=4 KnotsCount=2 Degree=3 IsPeriodic=0
    g256: BSplineCurve PolesCount=4 KnotsCount=2 Degree=3 IsPeriodic=0
    g257: BSplineCurve PolesCount=4 KnotsCount=2 Degree=3 IsPeriodic=0
    g258: BSplineCurve PolesCount=4 KnotsCount=2 Degree=3 IsPeriodic=0
    g259: BSplineCurve PolesCount=4 KnotsCount=2 Degree=3 IsPeriodic=0
    g260: BSplineCurve PolesCount=4 KnotsCount=2 Degree=3 IsPeriodic=0
    g261: BSplineCurve PolesCount=4 KnotsCount=2 Degree=3 IsPeriodic=0
    g262: BSplineCurve PolesCount=4 KnotsCount=2 Degree=3 IsPeriodic=0
    g263: BSplineCurve PolesCount=4 KnotsCount=2 Degree=3 IsPeriodic=0
    g264: BSplineCurve PolesCount=4 KnotsCount=2 Degree=3 IsPeriodic=0
    g265: BSplineCurve PolesCount=2 KnotsCount=2 Degree=1 IsPeriodic=0
    g266: BSplineCurve PolesCount=2 KnotsCount=2 Degree=1 IsPeriodic=0
    g267: BSplineCurve PolesCount=2 KnotsCount=2 Degree=1 IsPeriodic=0
    g268: BSplineCurve PolesCount=2 KnotsCount=2 Degree=1 IsPeriodic=0
    g269: BSplineCurve PolesCount=4 KnotsCount=2 Degree=3 IsPeriodic=0
    g270: BSplineCurve PolesCount=4 KnotsCount=2 Degree=3 IsPeriodic=0
    g271: BSplineCurve PolesCount=4 KnotsCount=2 Degree=3 IsPeriodic=0
    g272: BSplineCurve PolesCount=4 KnotsCount=2 Degree=3 IsPeriodic=0
    g273: BSplineCurve PolesCount=4 KnotsCount=2 Degree=3 IsPeriodic=0
    g274: BSplineCurve PolesCount=4 KnotsCount=2 Degree=3 IsPeriodic=0
    g275: BSplineCurve PolesCount=4 KnotsCount=2 Degree=3 IsPeriodic=0
    g276: BSplineCurve PolesCount=4 KnotsCount=2 Degree=3 IsPeriodic=0
    g277: BSplineCurve PolesCount=4 KnotsCount=2 Degree=3 IsPeriodic=0
    g278: BSplineCurve PolesCount=2 KnotsCount=2 Degree=1 IsPeriodic=0
    g279: BSplineCurve PolesCount=4 KnotsCount=2 Degree=3 IsPeriodic=0
    g280: BSplineCurve PolesCount=4 KnotsCount=2 Degree=3 IsPeriodic=0
    g281: BSplineCurve PolesCount=4 KnotsCount=2 Degree=3 IsPeriodic=0
    g282: BSplineCurve PolesCount=4 KnotsCount=2 Degree=3 IsPeriodic=0
    g283: BSplineCurve PolesCount=4 KnotsCount=2 Degree=3 IsPeriodic=0
    g284: BSplineCurve PolesCount=4 KnotsCount=2 Degree=3 IsPeriodic=0
    g285: BSplineCurve PolesCount=4 KnotsCount=2 Degree=3 IsPeriodic=0
    g286: BSplineCurve PolesCount=2 KnotsCount=2 Degree=1 IsPeriodic=0
    g287: BSplineCurve PolesCount=4 KnotsCount=2 Degree=3 IsPeriodic=0
    g288: BSplineCurve PolesCount=2 KnotsCount=2 Degree=1 IsPeriodic=0
    g289: BSplineCurve PolesCount=2 KnotsCount=2 Degree=1 IsPeriodic=0
    g290: BSplineCurve PolesCount=4 KnotsCount=2 Degree=3 IsPeriodic=0
    g291: BSplineCurve PolesCount=4 KnotsCount=2 Degree=3 IsPeriodic=0
    g292: BSplineCurve PolesCount=4 KnotsCount=2 Degree=3 IsPeriodic=0
    g293: BSplineCurve PolesCount=2 KnotsCount=2 Degree=1 IsPeriodic=0
    g294: BSplineCurve PolesCount=2 KnotsCount=2 Degree=1 IsPeriodic=0
    g295: BSplineCurve PolesCount=4 KnotsCount=2 Degree=3 IsPeriodic=0
    g296: BSplineCurve PolesCount=2 KnotsCount=2 Degree=1 IsPeriodic=0
    g297: BSplineCurve PolesCount=2 KnotsCount=2 Degree=1 IsPeriodic=0
    g298: BSplineCurve PolesCount=4 KnotsCount=2 Degree=3 IsPeriodic=0
    g299: BSplineCurve PolesCount=2 KnotsCount=2 Degree=1 IsPeriodic=0
    g300: BSplineCurve PolesCount=4 KnotsCount=2 Degree=3 IsPeriodic=0
    g301: BSplineCurve PolesCount=4 KnotsCount=2 Degree=3 IsPeriodic=0
    g302: BSplineCurve PolesCount=4 KnotsCount=2 Degree=3 IsPeriodic=0
    g303: BSplineCurve PolesCount=4 KnotsCount=2 Degree=3 IsPeriodic=0
    g304: BSplineCurve PolesCount=4 KnotsCount=2 Degree=3 IsPeriodic=0
    g305: BSplineCurve PolesCount=2 KnotsCount=2 Degree=1 IsPeriodic=0
    g306: BSplineCurve PolesCount=4 KnotsCount=2 Degree=3 IsPeriodic=0
    g307: BSplineCurve PolesCount=2 KnotsCount=2 Degree=1 IsPeriodic=0
    g308: BSplineCurve PolesCount=2 KnotsCount=2 Degree=1 IsPeriodic=0
    g309: BSplineCurve PolesCount=4 KnotsCount=2 Degree=3 IsPeriodic=0
    g310: BSplineCurve PolesCount=4 KnotsCount=2 Degree=3 IsPeriodic=0
    g311: BSplineCurve PolesCount=4 KnotsCount=2 Degree=3 IsPeriodic=0
    g312: BSplineCurve PolesCount=4 KnotsCount=2 Degree=3 IsPeriodic=0
    g313: BSplineCurve PolesCount=4 KnotsCount=2 Degree=3 IsPeriodic=0
    g314: BSplineCurve PolesCount=4 KnotsCount=2 Degree=3 IsPeriodic=0
    g315: BSplineCurve PolesCount=4 KnotsCount=2 Degree=3 IsPeriodic=0
    g316: BSplineCurve PolesCount=4 KnotsCount=2 Degree=3 IsPeriodic=0
    g317: BSplineCurve PolesCount=4 KnotsCount=2 Degree=3 IsPeriodic=0
    g318: BSplineCurve PolesCount=4 KnotsCount=2 Degree=3 IsPeriodic=0
    g319: BSplineCurve PolesCount=4 KnotsCount=2 Degree=3 IsPeriodic=0
  constraints (326):
    c: Coincident(g0,g1)
    c: Coincident(g1,g2)
    c: Coincident(g2,g3)
    c: Coincident(g3,g4)
    c: Coincident(g4,g5)
    c: Coincident(g5,g6)
    c: Coincident(g6,g7)
    c: Coincident(g7,g8)
    c: Coincident(g8,g9)
    c: Coincident(g9,g10)
    c: Coincident(g10,g11)
    c: Coincident(g11,g12)
    c: Coincident(g12,g13)
    c: Coincident(g13,g14)
    c: Coincident(g14,g15)
    c: Coincident(g15,g16)
    c: Coincident(g16,g17)
    c: Coincident(g17,g18)
    c: Coincident(g18,g19)
    c: Coincident(g19,g20)
    c: Coincident(g20,g21)
    c: Coincident(g21,g22)
    c: Coincident(g22,g23)
    c: Coincident(g23,g24)
    c: Coincident(g24,g25)
    c: Coincident(g25,g26)
    c: Coincident(g26,g27)
    c: Coincident(g27,g28)
    c: Coincident(g28,g29)
    c: Coincident(g29,g30)
    c: Coincident(g30,g31)
    c: Coincident(g31,g32)
    c: Coincident(g32,g33)
    c: Coincident(g33,g34)
    c: Coincident(g34,g35)
    c: Coincident(g35,g36)
    c: Coincident(g36,g37)
    c: Coincident(g37,g38)
    c: Coincident(g38,g39)
    c: Coincident(g39,g40)
    c: Coincident(g40,g41)
    c: Coincident(g41,g42)
    c: Coincident(g42,g43)
    c: Coincident(g43,g44)
    c: Coincident(g44,g45)
    c: Coincident(g45,g46)
    c: Coincident(g46,g47)
    c: Coincident(g47,g48)
    c: Coincident(g48,g49)
    c: Coincident(g49,g50)
    c: Coincident(g50,g51)
    c: Coincident(g51,g52)
    c: Coincident(g52,g53)
    c: Coincident(g53,g54)
    c: Coincident(g54,g55)
    c: Coincident(g55,g56)
    c: Coincident(g56,g57)
    c: Coincident(g57,g58)
    c: Coincident(g58,g59)
    c: Coincident(g59,g60)
    c: Coincident(g60,g61)
    c: Coincident(g61,g62)
    c: Coincident(g62,g63)
    c: Coincident(g63,g64)
    c: Coincident(g64,g65)
    c: Coincident(g65,g66)
    c: Coincident(g66,g67)
    c: Coincident(g67,g68)
    c: Coincident(g68,g69)
    c: Coincident(g69,g70)
    c: Coincident(g70,g71)
    c: Coincident(g71,g72)
    c: Coincident(g72,g73)
    c: Coincident(g73,g74)
    c: Coincident(g74,g75)
    c: Coincident(g75,g76)
    c: Coincident(g76,g77)
    c: Coincident(g77,g78)
    c: Coincident(g78,g79)
    c: Coincident(g79,g80)
    c: Coincident(g80,g81)
    c: Coincident(g81,g82)
    c: Coincident(g82,g83)
    c: Coincident(g83,g84)
    c: Coincident(g84,g85)
    c: Coincident(g85,g86)
    c: Coincident(g86,g87)
    c: Coincident(g87,g88)
    c: Coincident(g88,g89)
    c: Coincident(g89,g90)
    c: Coincident(g90,g91)
    c: Coincident(g91,g92)
    c: Coincident(g92,g93)
    c: Coincident(g93,g94)
    c: Coincident(g94,g95)
    c: Coincident(g95,g96)
    c: Coincident(g96,g97)
    c: Coincident(g97,g98)
    c: Coincident(g98,g99)
    c: Coincident(g99,g100)
    c: Coincident(g100,g101)
    c: Coincident(g101,g102)
    c: Coincident(g102,g103)
    c: Coincident(g103,g104)
    c: Coincident(g104,g105)
    c: Coincident(g105,g106)
    c: Coincident(g106,g107)
    c: Coincident(g107,g108)
    c: Coincident(g108,g109)
    c: Coincident(g109,g110)
    c: Coincident(g110,g111)
    c: Coincident(g111,g112)
    c: Coincident(g112,g113)
    c: Coincident(g113,g114)
    c: Coincident(g114,g115)
    c: Coincident(g115,g116)
    c: Coincident(g116,g117)
    c: Coincident(g117,g118)
    c: Coincident(g118,g119)
    c: Coincident(g119,g120)
    c: Coincident(g120,g121)
    c: Coincident(g121,g122)
    c: Coincident(g122,g123)
    c: Coincident(g123,g124)
    c: Coincident(g124,g125)
    c: Coincident(g125,g126)
    c: Coincident(g126,g127)
    c: Coincident(g127,g128)
    c: Coincident(g128,g129)
    c: Coincident(g129,g130)
    c: Coincident(g130,g131)
    c: Coincident(g131,g132)
    c: Coincident(g132,g133)
    c: Coincident(g133,g134)
    c: Coincident(g134,g135)
    c: Coincident(g135,g136)
    c: Coincident(g136,g137)
    c: Coincident(g137,g138)
    c: Coincident(g138,g139)
    c: Coincident(g139,g140)
    c: Coincident(g140,g141)
    c: Coincident(g141,g142)
    c: Coincident(g142,g143)
    c: Coincident(g143,g144)
    c: Coincident(g144,g145)
    c: Coincident(g145,g146)
    c: Coincident(g146,g147)
    c: Coincident(g147,g148)
    c: Coincident(g148,g149)
    c: Coincident(g149,g150)
    c: Coincident(g150,g151)
    c: Coincident(g151,g152)
    c: Coincident(g152,g153)
    c: Coincident(g153,g154)
    c: Coincident(g154,g155)
    c: Coincident(g155,g156)
    c: Coincident(g156,g157)
    c: Coincident(g157,g158)
    c: Coincident(g158,g159)
    c: Coincident(g159,g160)
    c: Coincident(g160,g161)
    c: Coincident(g161,g162)
    c: Coincident(g162,g163)
    c: Coincident(g163,g164)
    c: Coincident(g164,g165)
    c: Coincident(g165,g166)
    c: Coincident(g166,g167)
    c: Coincident(g167,g168)
    c: Coincident(g168,g169)
    c: Coincident(g169,g170)
    c: Coincident(g170,g171)
    c: Coincident(g171,g172)
    c: Coincident(g172,g173)
    c: Coincident(g173,g174)
    c: Coincident(g174,g175)
    c: Coincident(g175,g176)
    c: Coincident(g176,g177)
    c: Coincident(g177,g178)
    c: Coincident(g178,g179)
    c: Coincident(g179,g180)
    c: Coincident(g180,g181)
    c: Coincident(g181,g182)
    c: Coincident(g182,g183)
    c: Coincident(g183,g184)
    c: Coincident(g184,g185)
    c: Coincident(g185,g186)
    c: Coincident(g186,g187)
    c: Coincident(g187,g0)
    c: Coincident(g188,g189)
    c: Coincident(g189,g190)
    c: Coincident(g190,g191)
    c: Coincident(g191,g192)
    c: Coincident(g192,g188)
    c: Coincident(g193,g194)
    c: Coincident(g194,g195)
    c: Coincident(g195,g196)
    c: Coincident(g196,g193)
    c: Coincident(g197,g198)
    c: Coincident(g198,g199)
    c: Coincident(g199,g200)
    c: Coincident(g200,g201)
    c: Coincident(g201,g202)
    c: Coincident(g202,g203)
    c: Coincident(g203,g197)
    c: Coincident(g204,g205)
    c: Coincident(g205,g206)
    c: Coincident(g206,g204)
    c: Coincident(g207,g208)
    c: Coincident(g208,g209)
    c: Coincident(g209,g210)
    c: Coincident(g210,g211)
    c: Coincident(g211,g212)
    c: Coincident(g212,g213)
    c: Coincident(g213,g207)
    c: Coincident(g214,g215)
    c: Coincident(g215,g216)
    c: Coincident(g216,g217)
    c: Coincident(g217,g218)
    c: Coincident(g218,g219)
    c: Coincident(g219,g214)
    c: Coincident(g220,g221)
    c: Coincident(g221,g222)
    c: Coincident(g222,g223)
    c: Coincident(g223,g220)
    c: Coincident(g224,g225)
    c: Coincident(g225,g226)
    c: Coincident(g226,g227)
    c: Coincident(g227,g228)
    c: Coincident(g228,g229)
    c: Coincident(g229,g230)
    c: Coincident(g230,g224)
    c: Coincident(g231,g232)
    c: Coincident(g232,g233)
    c: Coincident(g233,g234)
    c: Coincident(g234,g231)
    c: Coincident(g235,g236)
    c: Coincident(g236,g237)
    c: Coincident(g237,g238)
    c: Coincident(g238,g239)
    c: Coincident(g239,g240)
    c: Coincident(g240,g241)
    c: Coincident(g241,g242)
    c: Coincident(g242,g243)
    c: Coincident(g243,g235)
    c: Coincident(g244,g245)
    c: Coincident(g245,g246)
    c: Coincident(g246,g247)
    c: Coincident(g247,g248)
    c: Coincident(g248,g244)
    c: Coincident(g249,g250)
    c: Coincident(g250,g251)
    c: Coincident(g251,g252)
    c: Coincident(g252,g253)
    c: Coincident(g253,g254)
    c: Coincident(g254,g255)
    c: Coincident(g255,g256)
    c: Coincident(g256,g249)
    c: Coincident(g257,g258)
    c: Coincident(g258,g259)
    c: Coincident(g259,g260)
    c: Coincident(g260,g261)
    c: Coincident(g261,g262)
    c: Coincident(g262,g257)
    c: Coincident(g263,g264)
    c: Coincident(g264,g265)
    c: Coincident(g265,g266)
    c: Coincident(g266,g267)
    c: Coincident(g267,g268)
    c: Coincident(g268,g269)
    c: Coincident(g269,g270)
    c: Coincident(g270,g271)
    c: Coincident(g271,g263)
    c: Coincident(g272,g273)
    c: Coincident(g273,g274)
    c: Coincident(g274,g272)
    c: Coincident(g275,g276)
    c: Coincident(g276,g277)
    c: Coincident(g277,g275)
    c: Coincident(g278,g279)
    c: Coincident(g279,g280)
    c: Coincident(g280,g281)
    c: Coincident(g281,g282)
    c: Coincident(g282,g283)
    c: Coincident(g283,g284)
    c: Coincident(g284,g285)
    c: Coincident(g285,g278)
    c: Coincident(g286,g287)
    c: Coincident(g287,g288)
    c: Coincident(g288,g289)
    c: Coincident(g289,g290)
    c: Coincident(g290,g291)
    c: Coincident(g291,g292)
    c: Coincident(g292,g293)
    c: Coincident(g293,g294)
    c: Coincident(g294,g295)
    c: Coincident(g295,g296)
    c: Coincident(g296,g297)
    c: Coincident(g297,g298)
    c: Coincident(g298,g286)
    c: Coincident(g299,g300)
    c: Coincident(g300,g301)
    c: Coincident(g301,g302)
    c: Coincident(g302,g303)
    c: Coincident(g303,g304)
    c: Coincident(g304,g299)
    c: Coincident(g305,g306)
    c: Coincident(g306,g307)
    c: Coincident(g307,g308)
    c: Coincident(g308,g309)
    c: Coincident(g309,g310)
    c: Coincident(g310,g311)
    c: Coincident(g311,g312)
    c: Coincident(g312,g313)
    c: Coincident(g313,g305)
    c: Coincident(g314,g315)
    c: Coincident(g315,g316)
    c: Coincident(g316,g317)
    c: Coincident(g317,g318)
    c: Coincident(g318,g319)
    c: Coincident(g319,g314)
    c: Coincident(g299,g299)
    c: Coincident(g197,g197)
    c: Coincident(g286,g286)
    c: Coincident(g278,g278)
    c: Coincident(g305,g305)
    c: Coincident(g214,g214)
FEATURE [Part::Extrusion] Extrude001  label="Butler-Extrude"
  Base = -> Sketch001
  Dir = (0,0,1)
  DirMode = 0
  FaceMakerClass = Part::FaceMakerBullseye
  FaceMakerMode = 3
  LengthFwd = 0
  LengthRev = 3
  Solid = true
  Symmetric = false
  expr: LengthRev = <<Icon_Params>>.IconDepth
FEATURE [Part::Extrusion] Extrude002  label="Chef-Extrude"
  Base = -> Sketch002
  Dir = (0,0,1)
  DirMode = 0
  FaceMakerClass = Part::FaceMakerBullseye
  FaceMakerMode = 3
  LengthFwd = 0
  LengthRev = 3
  Solid = true
  Symmetric = false
  expr: LengthRev = <<Icon_Params>>.IconDepth
FEATURE [Part::Extrusion] Extrude003  label="Drunk-Extrude"
  Base = -> Sketch003
  Dir = (0,0,1)
  DirMode = 0
  FaceMakerClass = Part::FaceMakerBullseye
  FaceMakerMode = 3
  LengthFwd = 0
  LengthRev = 3
  Solid = true
  Symmetric = false
  expr: LengthRev = <<Icon_Params>>.IconDepth
FEATURE [Part::Extrusion] Extrude004  label="Empath-Extrude"
  Base = -> Sketch004
  Dir = (0,0,1)
  DirMode = 0
  FaceMakerClass = Part::FaceMakerBullseye
  FaceMakerMode = 3
  LengthFwd = 0
  LengthRev = 3
  Solid = true
  Symmetric = false
  expr: LengthRev = <<Icon_Params>>.IconDepth
FEATURE [Part::Extrusion] Extrude005  label="Fortune_Teller-Extrude"
  Base = -> Sketch005
  Dir = (0,0,1)
  DirMode = 0
  FaceMakerClass = Part::FaceMakerBullseye
  FaceMakerMode = 3
  LengthFwd = 0
  LengthRev = 3
  Solid = true
  Symmetric = false
  expr: LengthRev = <<Icon_Params>>.IconDepth
FEATURE [Part::Extrusion] Extrude006  label="Imp-Extrude"
  Base = -> Sketch006
  Dir = (0,0,1)
  DirMode = 0
  FaceMakerClass = Part::FaceMakerBullseye
  FaceMakerMode = 3
  LengthFwd = 0
  LengthRev = 3
  Solid = true
  Symmetric = false
  expr: LengthRev = <<Icon_Params>>.IconDepth
FEATURE [Part::Extrusion] Extrude007  label="Investigator-Extrude"
  Base = -> Sketch007
  Dir = (0,0,1)
  DirMode = 0
  FaceMakerClass = Part::FaceMakerBullseye
  FaceMakerMode = 3
  LengthFwd = 0
  LengthRev = 3
  Solid = true
  Symmetric = false
  expr: LengthRev = <<Icon_Params>>.IconDepth
FEATURE [Part::Extrusion] Extrude008  label="Librarian-Extrude"
  Base = -> Sketch008
  Dir = (0,0,1)
  DirMode = 0
  FaceMakerClass = Part::FaceMakerBullseye
  FaceMakerMode = 3
  LengthFwd = 0
  LengthRev = 3
  Solid = true
  Symmetric = false
  expr: LengthRev = <<Icon_Params>>.IconDepth
FEATURE [Part::Extrusion] Extrude009  label="Mayor-Extrude"
  Base = -> Sketch009
  Dir = (0,0,1)
  DirMode = 0
  FaceMakerClass = Part::FaceMakerBullseye
  FaceMakerMode = 3
  LengthFwd = 0
  LengthRev = 3
  Solid = true
  Symmetric = false
  expr: LengthRev = <<Icon_Params>>.IconDepth
FEATURE [Part::Extrusion] Extrude010  label="Monk-Extrude"
  Base = -> Sketch010
  Dir = (0,0,1)
  DirMode = 0
  FaceMakerClass = Part::FaceMakerBullseye
  FaceMakerMode = 3
  LengthFwd = 0
  LengthRev = 3
  Solid = true
  Symmetric = false
  expr: LengthRev = <<Icon_Params>>.IconDepth
FEATURE [Part::Extrusion] Extrude011  label="Poisoner-Extrude"
  Base = -> Sketch011
  Dir = (0,0,1)
  DirMode = 0
  FaceMakerClass = Part::FaceMakerBullseye
  FaceMakerMode = 3
  LengthFwd = 0
  LengthRev = 3
  Solid = true
  Symmetric = false
  expr: LengthRev = <<Icon_Params>>.IconDepth
FEATURE [Part::Extrusion] Extrude012  label="Ravenskeeper-Extrude"
  Base = -> Sketch012
  Dir = (0,0,1)
  DirMode = 0
  FaceMakerClass = Part::FaceMakerBullseye
  FaceMakerMode = 3
  LengthFwd = 0
  LengthRev = 3
  Solid = true
  Symmetric = false
  expr: LengthRev = <<Icon_Params>>.IconDepth
FEATURE [Part::Extrusion] Extrude013  label="Recluse-Extrude"
  Base = -> Sketch013
  Dir = (0,0,1)
  DirMode = 0
  FaceMakerClass = Part::FaceMakerBullseye
  FaceMakerMode = 3
  LengthFwd = 0
  LengthRev = 3
  Solid = true
  Symmetric = false
  expr: LengthRev = <<Icon_Params>>.IconDepth
FEATURE [Part::Extrusion] Extrude014  label="Saint-Extrude"
  Base = -> Sketch014
  Dir = (0,0,1)
  DirMode = 0
  FaceMakerClass = Part::FaceMakerBullseye
  FaceMakerMode = 3
  LengthFwd = 0
  LengthRev = 3
  Solid = true
  Symmetric = false
  expr: LengthRev = <<Icon_Params>>.IconDepth
FEATURE [Part::Extrusion] Extrude015  label="Scarlet_Woman-Extrude"
  Base = -> Sketch015
  Dir = (0,0,1)
  DirMode = 0
  FaceMakerClass = Part::FaceMakerBullseye
  FaceMakerMode = 3
  LengthFwd = 0
  LengthRev = 3
  Solid = true
  Symmetric = false
  expr: LengthRev = <<Icon_Params>>.IconDepth
FEATURE [Part::Extrusion] Extrude016  label="Slayer-Extrude"
  Base = -> Sketch016
  Dir = (0,0,1)
  DirMode = 0
  FaceMakerClass = Part::FaceMakerBullseye
  FaceMakerMode = 3
  LengthFwd = 0
  LengthRev = 3
  Solid = true
  Symmetric = false
  expr: LengthRev = <<Icon_Params>>.IconDepth
FEATURE [Part::Extrusion] Extrude017  label="Soldier-Extrude"
  Base = -> Sketch017
  Dir = (0,0,1)
  DirMode = 0
  FaceMakerClass = Part::FaceMakerBullseye
  FaceMakerMode = 3
  LengthFwd = 0
  LengthRev = 3
  Solid = true
  Symmetric = false
  expr: LengthRev = <<Icon_Params>>.IconDepth
FEATURE [Part::Extrusion] Extrude018  label="Spy-Extrude"
  Base = -> Sketch018
  Dir = (0,0,1)
  DirMode = 0
  FaceMakerClass = Part::FaceMakerBullseye
  FaceMakerMode = 3
  LengthFwd = 0
  LengthRev = 3
  Solid = true
  Symmetric = false
  expr: LengthRev = <<Icon_Params>>.IconDepth
FEATURE [Part::Extrusion] Extrude019  label="Undertaker-Extrude"
  Base = -> Sketch019
  Dir = (0,0,1)
  DirMode = 0
  FaceMakerClass = Part::FaceMakerBullseye
  FaceMakerMode = 3
  LengthFwd = 0
  LengthRev = 3
  Solid = true
  Symmetric = false
  expr: LengthRev = <<Icon_Params>>.IconDepth
FEATURE [Part::Extrusion] Extrude020  label="Virgin-Extrude"
  Base = -> Sketch020
  Dir = (0,0,1)
  DirMode = 0
  FaceMakerClass = Part::FaceMakerBullseye
  FaceMakerMode = 3
  LengthFwd = 0
  LengthRev = 3
  Solid = true
  Symmetric = false
  expr: LengthRev = <<Icon_Params>>.IconDepth
FEATURE [Part::Extrusion] Extrude021  label="Washerwoman-Extrude"
  Base = -> Sketch021
  Dir = (0,0,1)
  DirMode = 0
  FaceMakerClass = Part::FaceMakerBullseye
  FaceMakerMode = 3
  LengthFwd = 0
  LengthRev = 3
  Solid = true
  Symmetric = false
  expr: LengthRev = <<Icon_Params>>.IconDepth
FEATURE [Part::Scale] Scale001  label="Butler-Scale"
  Base = -> Extrude001
  Uniform = true
  UniformScale = 1.5
  XScale = 1
  YScale = 1
  ZScale = 1
  expr: UniformScale = <<Icon_Params>>.IconScale
FEATURE [Part::Scale] Scale002  label="Chef-Scale"
  Base = -> Extrude002
  Uniform = true
  UniformScale = 1.5
  XScale = 1
  YScale = 1
  ZScale = 1
  expr: UniformScale = <<Icon_Params>>.IconScale
FEATURE [Part::Scale] Scale003  label="Drunk-Scale"
  Base = -> Extrude003
  Uniform = true
  UniformScale = 1.5
  XScale = 1
  YScale = 1
  ZScale = 1
  expr: UniformScale = <<Icon_Params>>.IconScale
FEATURE [Part::Scale] Scale004  label="Empath-Scale"
  Base = -> Extrude004
  Uniform = true
  UniformScale = 1.5
  XScale = 1
  YScale = 1
  ZScale = 1
  expr: UniformScale = <<Icon_Params>>.IconScale
FEATURE [Part::Scale] Scale005  label="Fortune_Teller-Scale"
  Base = -> Extrude005
  Uniform = true
  UniformScale = 1.5
  XScale = 1
  YScale = 1
  ZScale = 1
  expr: UniformScale = <<Icon_Params>>.IconScale
FEATURE [Part::Scale] Scale006  label="Imp-Scale"
  Base = -> Extrude006
  Uniform = true
  UniformScale = 1.5
  XScale = 1
  YScale = 1
  ZScale = 1
  expr: UniformScale = <<Icon_Params>>.IconScale
FEATURE [Part::Scale] Scale007  label="Investigator-Scale"
  Base = -> Extrude007
  Uniform = true
  UniformScale = 1.5
  XScale = 1
  YScale = 1
  ZScale = 1
  expr: UniformScale = <<Icon_Params>>.IconScale
FEATURE [Part::Scale] Scale008  label="Librarian-Scale"
  Base = -> Extrude008
  Uniform = true
  UniformScale = 1.5
  XScale = 1
  YScale = 1
  ZScale = 1
  expr: UniformScale = <<Icon_Params>>.IconScale
FEATURE [Part::Scale] Scale009  label="Mayor-Scale"
  Base = -> Extrude009
  Uniform = true
  UniformScale = 1.5
  XScale = 1
  YScale = 1
  ZScale = 1
  expr: UniformScale = <<Icon_Params>>.IconScale
FEATURE [Part::Scale] Scale010  label="Monk-Scale"
  Base = -> Extrude010
  Uniform = true
  UniformScale = 1.5
  XScale = 1
  YScale = 1
  ZScale = 1
  expr: UniformScale = <<Icon_Params>>.IconScale
FEATURE [Part::Scale] Scale011  label="Poisoner-Scale"
  Base = -> Extrude011
  Uniform = true
  UniformScale = 1.5
  XScale = 1
  YScale = 1
  ZScale = 1
  expr: UniformScale = <<Icon_Params>>.IconScale
FEATURE [Part::Scale] Scale012  label="Ravenskeeper-Scale"
  Base = -> Extrude012
  Uniform = true
  UniformScale = 1.5
  XScale = 1
  YScale = 1
  ZScale = 1
  expr: UniformScale = <<Icon_Params>>.IconScale
FEATURE [Part::Scale] Scale013  label="Recluse-Scale"
  Base = -> Extrude013
  Uniform = true
  UniformScale = 1.5
  XScale = 1
  YScale = 1
  ZScale = 1
  expr: UniformScale = <<Icon_Params>>.IconScale
FEATURE [Part::Scale] Scale014  label="Saint-Scale"
  Base = -> Extrude014
  Uniform = true
  UniformScale = 1.5
  XScale = 1
  YScale = 1
  ZScale = 1
  expr: UniformScale = <<Icon_Params>>.IconScale
FEATURE [Part::Scale] Scale015  label="Scarlet_Woman-Scale"
  Base = -> Extrude015
  Uniform = true
  UniformScale = 1.5
  XScale = 1
  YScale = 1
  ZScale = 1
  expr: UniformScale = <<Icon_Params>>.IconScale
FEATURE [Part::Scale] Scale016  label="Slayer-Scale"
  Base = -> Extrude016
  Uniform = true
  UniformScale = 1.5
  XScale = 1
  YScale = 1
  ZScale = 1
  expr: UniformScale = <<Icon_Params>>.IconScale
FEATURE [Part::Scale] Scale017  label="Soldier-Scale"
  Base = -> Extrude017
  Uniform = true
  UniformScale = 1.5
  XScale = 1
  YScale = 1
  ZScale = 1
  expr: UniformScale = <<Icon_Params>>.IconScale
FEATURE [Part::Scale] Scale018  label="Spy-Scale"
  Base = -> Extrude018
  Uniform = true
  UniformScale = 1.5
  XScale = 1
  YScale = 1
  ZScale = 1
  expr: UniformScale = <<Icon_Params>>.IconScale
FEATURE [Part::Scale] Scale019  label="Undertaker-Scale"
  Base = -> Extrude019
  Uniform = true
  UniformScale = 1.5
  XScale = 1
  YScale = 1
  ZScale = 1
  expr: UniformScale = <<Icon_Params>>.IconScale
FEATURE [Part::Scale] Scale020  label="Virgin-Scale"
  Base = -> Extrude020
  Uniform = true
  UniformScale = 1.5
  XScale = 1
  YScale = 1
  ZScale = 1
  expr: UniformScale = <<Icon_Params>>.IconScale
FEATURE [Part::Scale] Scale021  label="Washerwoman-Scale"
  Base = -> Extrude021
  Uniform = true
  UniformScale = 1.5
  XScale = 1
  YScale = 1
  ZScale = 1
  expr: UniformScale = <<Icon_Params>>.IconScale
